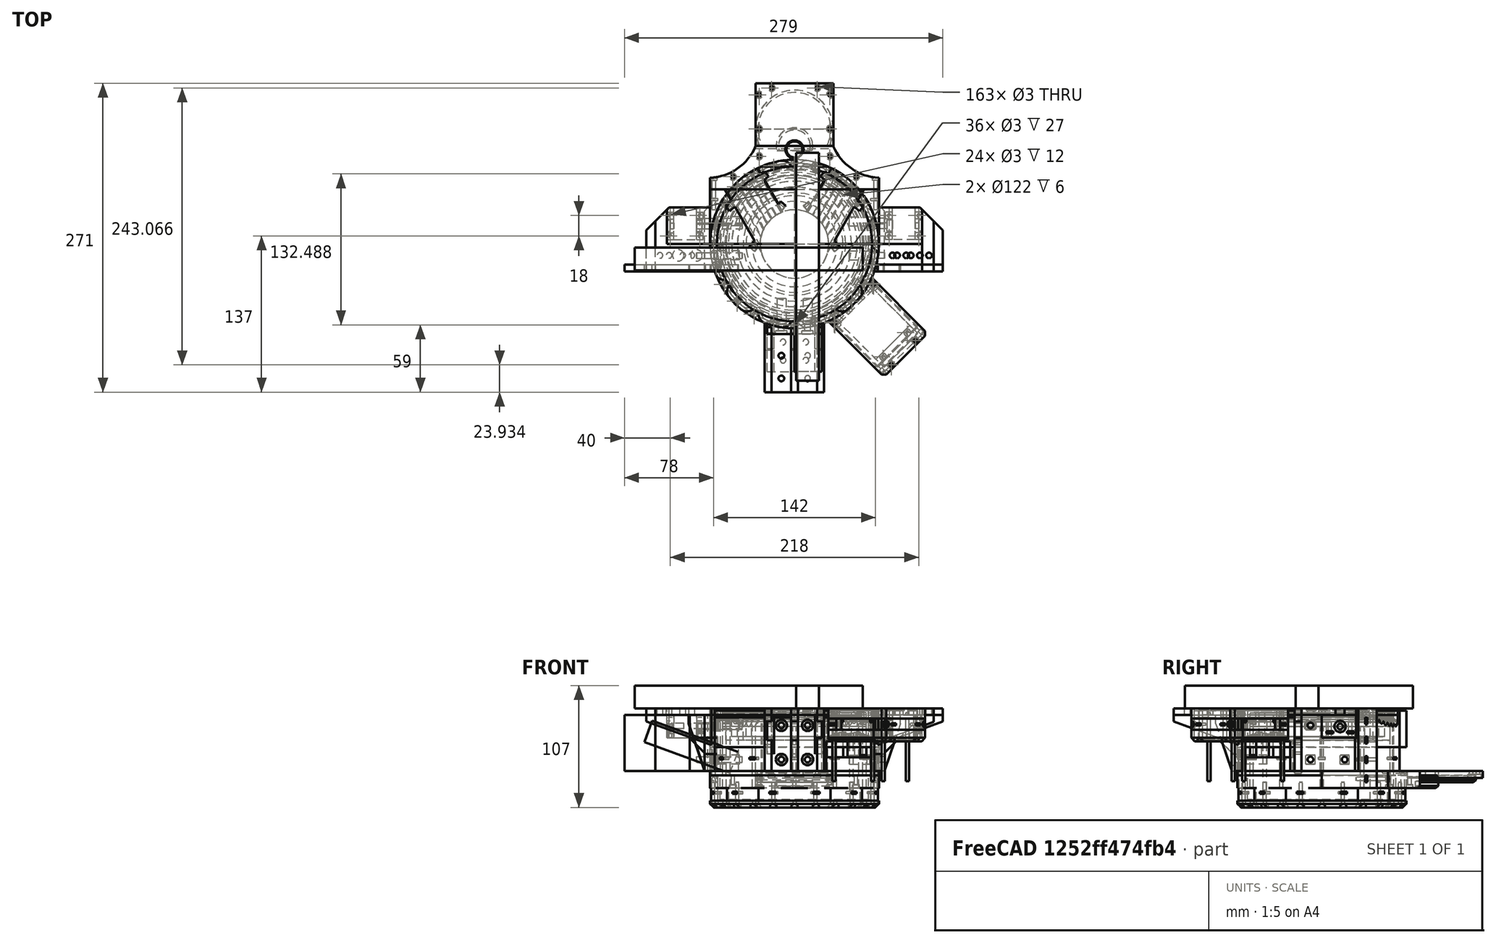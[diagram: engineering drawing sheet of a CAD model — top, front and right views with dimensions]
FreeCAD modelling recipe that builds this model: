
FCSTD DOCUMENT  (FreeCAD 0.19R24276 (Git))
Label: Base_turret_039
License: All rights reserved
LicenseURL: http://en.wikipedia.org/wiki/All_rights_reserved
objects: Part::Cylinder×614, Part::Box×522, Part::Compound×337, Part::Cut×305, Part::Mirroring×42, Part::Chamfer×39, Part::FeaturePython×20, Part::Fillet×14, Mesh::Feature×5, Part::Common×2
note: 1895 computed .brp shape members not serialized (recipe doc carries the construction recipe); baked Part::Feature solids carry a one-line shape summary decoded from their .brp

FEATURE [Part::Cylinder] Cylinder1727  label="Válec1727"
  Angle = 360
  AttacherType = Attacher::AttachEngine3D
  Height = 3
  Placement = pos=(-15,125,-80) rot=(0,0,1;0rad)
  Radius = 3
FEATURE [Part::Cylinder] Cylinder1728  label="Válec1728"
  Angle = 360
  AttacherType = Attacher::AttachEngine3D
  Height = 3
  Placement = pos=(15,125,-80) rot=(0,0,1;0rad)
  Radius = 3
FEATURE [Part::Cylinder] Cylinder1729  label="Válec1729"
  Angle = 360
  AttacherType = Attacher::AttachEngine3D
  Height = 3
  Placement = pos=(24,73,-80) rot=(0,0,1;0rad)
  Radius = 3
FEATURE [Part::Cylinder] Cylinder1730  label="Válec1730"
  Angle = 360
  AttacherType = Attacher::AttachEngine3D
  Height = 3
  Placement = pos=(-24,73,-80) rot=(0,0,1;0rad)
  Radius = 3
FEATURE [Part::Box] Box688  label="Krychle688"
  AttacherType = Attacher::AttachEngine3D
  Height = 50
  Length = 42
  Placement = pos=(-21.0011,60.0051,31) rot=(0,0,1;0rad)
  Width = 62
FEATURE [Part::Compound] Compound871
  Links = -> [Cylinder1729,Cylinder1730,Cylinder1727,Cylinder1728]
  Placement = pos=(0,0,135) rot=(0,0,1;3.92699rad)
FEATURE [Part::Compound] Compound872
  Links = -> [Box688]
  Placement = pos=(0,0,0) rot=(0,0,1;3.92699rad)
FEATURE [Part::Box] Box689  label="Krychle689"
  AttacherType = Attacher::AttachEngine3D
  Height = 10
  Length = 54
  Placement = pos=(-27.0044,59.998,75) rot=(0,0,1;0rad)
  Width = 68
FEATURE [Part::Compound] Compound873
  Links = -> [Box689]
  Placement = pos=(0,0,-20) rot=(0,0,1;3.92699rad)
FEATURE [Part::Cut] Cut502
  Base = -> Compound873
  Tool = -> Compound872
FEATURE [Part::Cylinder] Cylinder1731  label="Válec1731"
  Angle = 360
  AttacherType = Attacher::AttachEngine3D
  Height = 60
  Placement = pos=(-15,125,-80) rot=(0,0,1;0rad)
  Radius = 1.5
FEATURE [Part::Cylinder] Cylinder1732  label="Válec1732"
  Angle = 360
  AttacherType = Attacher::AttachEngine3D
  Height = 60
  Placement = pos=(15,125,-80) rot=(0,0,1;0rad)
  Radius = 1.5
FEATURE [Part::Cylinder] Cylinder1733  label="Válec1733"
  Angle = 360
  AttacherType = Attacher::AttachEngine3D
  Height = 60
  Placement = pos=(24,73,-80) rot=(0,0,1;0rad)
  Radius = 1.5
FEATURE [Part::Cylinder] Cylinder1734  label="Válec1734"
  Angle = 360
  AttacherType = Attacher::AttachEngine3D
  Height = 60
  Placement = pos=(-24,73,-80) rot=(0,0,1;0rad)
  Radius = 1.5
FEATURE [Part::Compound] Compound874
  Links = -> [Cylinder1733,Cylinder1734,Cylinder1731,Cylinder1732]
  Placement = pos=(0,0,100) rot=(0,0,1;3.92699rad)
FEATURE [Part::Cylinder] Cylinder1735  label="Válec1735"
  Angle = 360
  AttacherType = Attacher::AttachEngine3D
  Height = 40
  Placement = pos=(0,0,44) rot=(0,0,1;0rad)
  Radius = 74
FEATURE [Part::Box] Box690  label="Krychle690"
  AttacherType = Attacher::AttachEngine3D
  Height = 10
  Length = 42
  Placement = pos=(-21,-23,22) rot=(0,0,1;0rad)
  Width = 8
FEATURE [Part::Cylinder] Cylinder1736  label="Válec1736"
  Angle = 360
  AttacherType = Attacher::AttachEngine3D
  Height = 40
  Placement = pos=(0,0,44) rot=(0,0,1;0rad)
  Radius = 74
FEATURE [Part::Cylinder] Cylinder1739  label="Válec1739"
  Angle = 360
  AttacherType = Attacher::AttachEngine3D
  Height = 50
  Placement = pos=(9,100,59) rot=(1,0,0;1.5708rad)
  Radius = 1.5
FEATURE [Part::Cylinder] Cylinder1740  label="Válec1740"
  Angle = 360
  AttacherType = Attacher::AttachEngine3D
  Height = 50
  Placement = pos=(-9,100,59) rot=(1,0,0;1.5708rad)
  Radius = 1.5
FEATURE [Part::Compound] Compound876
  Links = -> [Box690]
  Placement = pos=(63.64,-63.64,43) rot=(0,0,1;3.92699rad)
FEATURE [Part::Cut] Cut506
  Base = -> Compound876
  Placement = pos=(0,0,-10) rot=(0,0,1;0rad)
  Tool = -> Cylinder1736
FEATURE [Part::Compound] Compound881
  Links = -> [Cylinder1739]
  Placement = pos=(0,0,0) rot=(0,0,1;3.92699rad)
FEATURE [Part::Compound] Compound882
  Links = -> [Cylinder1740]
  Placement = pos=(0,0,0) rot=(0,0,1;3.92699rad)
FEATURE [Part::Compound] Compound883
  Links = -> [Compound882,Compound881]
  Placement = pos=(0,0,1) rot=(0,0,1;0rad)
FEATURE [Part::Cut] Cut507
  Base = -> Cut506
  Tool = -> Compound883
FEATURE [Part::Cut] Cut510
  Base = -> Cut502
  Tool = -> Cylinder1735
FEATURE [Part::Chamfer] Chamfer054
  Base = -> Cut510
  Edges = 2 edges r=3: [Edge2,Edge13]
FEATURE [Part::Chamfer] Chamfer055
  Base = -> Chamfer054
  Edges = 2 edges r=2: [Edge3,Edge22]
FEATURE [Part::Chamfer] Chamfer056
  Base = -> Chamfer055
  Edges = 1 edges r=1: [Edge27]
FEATURE [Part::Cut] Cut511
  Base = -> Chamfer056
  Tool = -> Compound874
FEATURE [Part::Cut] Cut512
  Base = -> Cut511
  Tool = -> Compound871
FEATURE [Part::Box] Box485  label="Krychle485"
  AttacherType = Attacher::AttachEngine3D
  Height = 49
  Length = 56
  Placement = pos=(-28,35,29) rot=(0,0,1;0rad)
  Width = 200
FEATURE [Part::Box] Box486  label="Krychle486"
  AttacherType = Attacher::AttachEngine3D
  Height = 55
  Length = 148
  Placement = pos=(-74,68,29) rot=(0,0,1;0rad)
  Width = 26
FEATURE [Part::Cylinder] Cylinder971  label="Válec971"
  Angle = 360
  AttacherType = Attacher::AttachEngine3D
  Height = 6
  Placement = pos=(0,0,65) rot=(0,0,1;0rad)
  Radius = 74
FEATURE [Part::Box] Box483  label="Krychle483"
  AttacherType = Attacher::AttachEngine3D
  Height = 34
  Length = 148
  Placement = pos=(-74,68,38) rot=(0,0,1;0rad)
  Width = 20
FEATURE [Part::Cut] Cut453
  Base = -> Cylinder971
  Placement = pos=(0,0,13) rot=(0,0,1;0rad)
  Tool = -> Box483
FEATURE [Part::Box] Box648  label="Krychle648"
  AttacherType = Attacher::AttachEngine3D
  Height = 60
  Length = 200
  Placement = pos=(0,0,-5) rot=(0,0,-1;0.383972rad)
  Width = 200
FEATURE [Part::Box] Box647  label="Krychle647"
  AttacherType = Attacher::AttachEngine3D
  Height = 60
  Length = 200
  Placement = pos=(70.7107,70.7107,-5) rot=(0,0,1;3.92699rad)
  Width = 120
FEATURE [Part::Cut] Cut464
  Base = -> Box647
  Tool = -> Box648
FEATURE [Part::Box] Box649  label="Krychle649"
  AttacherType = Attacher::AttachEngine3D
  Height = 60
  Length = 200
  Placement = pos=(0,0,-5) rot=(0,0,1;3.52556rad)
  Width = 200
FEATURE [Part::Cut] Cut465
  Base = -> Cut464
  Tool = -> Box649
FEATURE [Part::FeaturePython] Tube035  # WARN: FeaturePython — macro-defined, semantics opaque (R4)
  AttacherType = Attacher::AttachEngine3D
  Height = 55
  InnerRadius = 68
  OuterRadius = 74
  Placement = pos=(0,0,29) rot=(0,0,1;0rad)
FEATURE [Part::Cut] Cut455
  Base = -> Tube035
  Tool = -> Box485
FEATURE [Part::Cut] Cut454
  Base = -> Cut455
  Tool = -> Box486
FEATURE [Part::Cut] Cut
  Base = -> Cut454
  Tool = -> Cut465
FEATURE [Part::FeaturePython] Tube036  # WARN: FeaturePython — macro-defined, semantics opaque (R4)
  AttacherType = Attacher::AttachEngine3D
  Height = 8
  InnerRadius = 50.1
  OuterRadius = 58
  Placement = pos=(0,0,72) rot=(0,0,1;0rad)
FEATURE [Part::Box] Box488  label="Krychle488"
  AttacherType = Attacher::AttachEngine3D
  Height = 2
  Length = 6
  Placement = pos=(-3,-75,39) rot=(0,0,1;0rad)
  Width = 8
FEATURE [Part::Box] Box489  label="Krychle489"
  AttacherType = Attacher::AttachEngine3D
  Height = 2
  Length = 6
  Placement = pos=(34.9,-66.45,58) rot=(0,0,1;0.523599rad)
  Width = 8
FEATURE [Part::Box] Box497  label="Krychle497"
  AttacherType = Attacher::AttachEngine3D
  Height = 2
  Length = 6
  Placement = pos=(-75,3,39) rot=(0,0,-1;1.5708rad)
  Width = 8
FEATURE [Part::Box] Box493  label="Krychle493"
  AttacherType = Attacher::AttachEngine3D
  Height = 2
  Length = 6
  Placement = pos=(40.0981,63.4519,39) rot=(0,0,1;2.61799rad)
  Width = 8
FEATURE [Part::Box] Box491  label="Krychle491"
  AttacherType = Attacher::AttachEngine3D
  Height = 2
  Length = 6
  Placement = pos=(75,-3,39) rot=(0,0,1;1.5708rad)
  Width = 8
FEATURE [Part::Box] Box495  label="Krychle495"
  AttacherType = Attacher::AttachEngine3D
  Height = 2
  Length = 6
  Placement = pos=(-34.9019,66.4519,39) rot=(0,0,1;3.66519rad)
  Width = 8
FEATURE [Part::Box] Box490  label="Krychle490"
  AttacherType = Attacher::AttachEngine3D
  Height = 2
  Length = 6
  Placement = pos=(63.45,-40.1,58) rot=(0,0,1;1.0472rad)
  Width = 8
FEATURE [Part::Box] Box494  label="Krychle494"
  AttacherType = Attacher::AttachEngine3D
  Height = 2
  Length = 6
  Placement = pos=(3,75,39) rot=(0,0,1;3.14159rad)
  Width = 8
FEATURE [Part::Box] Box498  label="Krychle498"
  AttacherType = Attacher::AttachEngine3D
  Height = 2
  Length = 6
  Placement = pos=(-66.4519,-34.9019,39) rot=(0,0,-1;1.0472rad)
  Width = 8
FEATURE [Part::Box] Box492  label="Krychle492"
  AttacherType = Attacher::AttachEngine3D
  Height = 2
  Length = 6
  Placement = pos=(66.4519,34.9019,39) rot=(0,0,1;2.0944rad)
  Width = 8
FEATURE [Part::Box] Box499  label="Krychle499"
  AttacherType = Attacher::AttachEngine3D
  Height = 2
  Length = 6
  Placement = pos=(-40.0981,-63.4519,39) rot=(0,0,-1;0.523599rad)
  Width = 8
FEATURE [Part::Box] Box496  label="Krychle496"
  AttacherType = Attacher::AttachEngine3D
  Height = 2
  Length = 6
  Placement = pos=(-63.4519,40.0981,39) rot=(0,0,1;4.18879rad)
  Width = 8
FEATURE [Part::Compound] Compound528
  Links = -> [Box488,Box489,Box490,Box491,Box492,Box493,Box494,Box495,Box496,Box497,Box498,Box499]
FEATURE [Part::Cut] Cut467
  Base = -> Cut
  Tool = -> Compound528
FEATURE [Part::Cylinder] Cylinder1629  label="Válec1629"
  Angle = 360
  AttacherType = Attacher::AttachEngine3D
  Height = 72
  Placement = pos=(71,-1.8e-14,0) rot=(0,0,1;1.5708rad)
  Radius = 1.5
FEATURE [Part::Cylinder] Cylinder1630  label="Válec1630"
  Angle = 360
  AttacherType = Attacher::AttachEngine3D
  Height = 72
  Placement = pos=(35.5,61.4878,0) rot=(0,0,1;2.61799rad)
  Radius = 1.5
FEATURE [Part::Cylinder] Cylinder1631  label="Válec1631"
  Angle = 360
  AttacherType = Attacher::AttachEngine3D
  Height = 72
  Placement = pos=(61.4878,-35.5,0) rot=(0,0,1;1.0472rad)
  Radius = 1.5
FEATURE [Part::Cylinder] Cylinder1632  label="Válec1632"
  Angle = 360
  AttacherType = Attacher::AttachEngine3D
  Height = 72
  Placement = pos=(35.5,-61.4878,0) rot=(0,0,1;0.523599rad)
  Radius = 1.5
FEATURE [Part::Cylinder] Cylinder1633  label="Válec1633"
  Angle = 360
  AttacherType = Attacher::AttachEngine3D
  Height = 72
  Placement = pos=(-35.5,-61.4878,0) rot=(0,0,-1;0.523599rad)
  Radius = 1.5
FEATURE [Part::Cylinder] Cylinder1634  label="Válec1634"
  Angle = 360
  AttacherType = Attacher::AttachEngine3D
  Height = 72
  Placement = pos=(-71,2.7e-14,0) rot=(0,0,-1;1.5708rad)
  Radius = 1.5
FEATURE [Part::Cylinder] Cylinder1635  label="Válec1635"
  Angle = 360
  AttacherType = Attacher::AttachEngine3D
  Height = 72
  Placement = pos=(-61.4878,-35.5,0) rot=(0,0,-1;1.0472rad)
  Radius = 1.5
FEATURE [Part::Cylinder] Cylinder1636  label="Válec1636"
  Angle = 360
  AttacherType = Attacher::AttachEngine3D
  Height = 72
  Placement = pos=(61.4878,35.5,0) rot=(0,0,1;2.0944rad)
  Radius = 1.5
FEATURE [Part::Cylinder] Cylinder1637  label="Válec1637"
  Angle = 360
  AttacherType = Attacher::AttachEngine3D
  Height = 72
  Placement = pos=(0,-71,0) rot=(0,0,1;0rad)
  Radius = 1.5
FEATURE [Part::Cylinder] Cylinder1638  label="Válec1638"
  Angle = 360
  AttacherType = Attacher::AttachEngine3D
  Height = 72
  Placement = pos=(-35.5,61.4878,0) rot=(0,0,1;3.66519rad)
  Radius = 1.5
FEATURE [Part::Cylinder] Cylinder1639  label="Válec1639"
  Angle = 360
  AttacherType = Attacher::AttachEngine3D
  Height = 72
  Placement = pos=(-61.4878,35.5,0) rot=(0,0,1;4.18879rad)
  Radius = 1.5
FEATURE [Part::Cylinder] Cylinder1640  label="Válec1640"
  Angle = 360
  AttacherType = Attacher::AttachEngine3D
  Height = 72
  Placement = pos=(3.1e-14,71,0) rot=(0,0,1;3.14159rad)
  Radius = 1.5
FEATURE [Part::Compound] Compound529
  Links = -> [Cylinder1637,Cylinder1632,Cylinder1631,Cylinder1629,Cylinder1636,Cylinder1630,Cylinder1640,Cylinder1638,Cylinder1639,Cylinder1634,Cylinder1635,Cylinder1633]
  Placement = pos=(0,0,-4) rot=(0,0,1;0rad)
FEATURE [Part::Cut] Cut468
  Base = -> Cut467
  Tool = -> Compound529
FEATURE [Part::Cylinder] Cylinder1722  label="Válec1722"
  Angle = 360
  AttacherType = Attacher::AttachEngine3D
  Height = 50
  Placement = pos=(-18,100,72) rot=(1,0,0;1.5708rad)
  Radius = 1.5
FEATURE [Part::Compound] Compound863
  Links = -> [Cylinder1722]
  Placement = pos=(0,0,0) rot=(0,0,1;3.92699rad)
FEATURE [Part::Cylinder] Cylinder1723  label="Válec1723"
  Angle = 360
  AttacherType = Attacher::AttachEngine3D
  Height = 50
  Placement = pos=(18,100,72) rot=(1,0,0;1.5708rad)
  Radius = 1.5
FEATURE [Part::Compound] Compound864
  Links = -> [Cylinder1723]
  Placement = pos=(0,0,0) rot=(0,0,1;3.92699rad)
FEATURE [Part::Compound] Compound865
  Links = -> [Compound863,Compound864]
  Placement = pos=(0,0,1) rot=(0,0,1;0rad)
FEATURE [Part::Box] Box686  label="Krychle686"
  AttacherType = Attacher::AttachEngine3D
  Height = 6
  Length = 6
  Placement = pos=(15,64,-50) rot=(0,0,1;0rad)
  Width = 4
FEATURE [Part::Box] Box687  label="Krychle687"
  AttacherType = Attacher::AttachEngine3D
  Height = 6
  Length = 6
  Placement = pos=(-21,64,-50) rot=(0,0,1;0rad)
  Width = 4
FEATURE [Part::Cut] Cut500
  Base = -> Cut468
  Tool = -> Compound865
FEATURE [Part::Compound] Compound866
  Links = -> [Box687,Box686]
  Placement = pos=(0,0,120) rot=(0,0,1;3.92699rad)
FEATURE [Part::Cut] Cut501
  Base = -> Cut500
  Tool = -> Compound866
FEATURE [Part::Cylinder] Cylinder1737  label="Válec1737"
  Angle = 360
  AttacherType = Attacher::AttachEngine3D
  Height = 50
  Placement = pos=(-9,100,59) rot=(1,0,0;1.5708rad)
  Radius = 1.5
FEATURE [Part::Cylinder] Cylinder1738  label="Válec1738"
  Angle = 360
  AttacherType = Attacher::AttachEngine3D
  Height = 50
  Placement = pos=(9,100,59) rot=(1,0,0;1.5708rad)
  Radius = 1.5
FEATURE [Part::Box] Box691  label="Krychle691"
  AttacherType = Attacher::AttachEngine3D
  Height = 6
  Length = 6
  Placement = pos=(6,66,-63) rot=(0,0,1;0rad)
  Width = 4
FEATURE [Part::Box] Box692  label="Krychle692"
  AttacherType = Attacher::AttachEngine3D
  Height = 6
  Length = 6
  Placement = pos=(-12,66,-63) rot=(0,0,1;0rad)
  Width = 4
FEATURE [Part::Compound] Compound878
  Links = -> [Cylinder1738]
  Placement = pos=(0,0,0) rot=(0,0,1;3.92699rad)
FEATURE [Part::Compound] Compound879
  Links = -> [Cylinder1737]
  Placement = pos=(0,0,0) rot=(0,0,1;3.92699rad)
FEATURE [Part::Compound] Compound877
  Links = -> [Compound879,Compound878]
  Placement = pos=(0,0,1) rot=(0,0,1;0rad)
FEATURE [Part::Cut] Cut508
  Base = -> Cut501
  Tool = -> Compound877
FEATURE [Part::Compound] Compound880
  Links = -> [Box692,Box691]
  Placement = pos=(0,0,120) rot=(0,0,1;3.92699rad)
FEATURE [Part::Cut] Cut509
  Base = -> Cut508
  Tool = -> Compound880
FEATURE [Part::Box] Box482  label="Krychle482"
  AttacherType = Attacher::AttachEngine3D
  Height = 55
  Length = 148
  Placement = pos=(-74,0,29) rot=(0,0,1;0rad)
  Width = 74
FEATURE [Part::Cylinder] Cylinder972  label="Válec972"
  Angle = 360
  AttacherType = Attacher::AttachEngine3D
  Height = 51
  Placement = pos=(0,0,29) rot=(0,0,1;0rad)
  Radius = 74
FEATURE [Part::Cut] Cut451
  Base = -> Box482
  Tool = -> Cylinder972
FEATURE [Part::Box] Box484  label="Krychle484"
  AttacherType = Attacher::AttachEngine3D
  Height = 55
  Length = 148
  Placement = pos=(-74,48,29) rot=(0,0,1;0rad)
  Width = 26
FEATURE [Part::Cut] Cut452
  Base = -> Cut451
  Tool = -> Box484
FEATURE [Part::Cylinder] Cylinder1753  label="Válec1753"
  Angle = 360
  AttacherType = Attacher::AttachEngine3D
  Height = 50
  Placement = pos=(-71,80,73) rot=(1,0,0;1.5708rad)
  Radius = 1.5
FEATURE [Part::Cylinder] Cylinder1754  label="Válec1754"
  Angle = 360
  AttacherType = Attacher::AttachEngine3D
  Height = 50
  Placement = pos=(71,80,39) rot=(1,0,0;1.5708rad)
  Radius = 1.5
FEATURE [Part::Cylinder] Cylinder1755  label="Válec1755"
  Angle = 360
  AttacherType = Attacher::AttachEngine3D
  Height = 50
  Placement = pos=(-71,80,39) rot=(1,0,0;1.5708rad)
  Radius = 1.5
FEATURE [Part::Cylinder] Cylinder1756  label="Válec1756"
  Angle = 360
  AttacherType = Attacher::AttachEngine3D
  Height = 50
  Placement = pos=(71,80,73) rot=(1,0,0;1.5708rad)
  Radius = 1.5
FEATURE [Part::Cylinder] Cylinder1757  label="Válec1757"
  Angle = 360
  AttacherType = Attacher::AttachEngine3D
  Height = 50
  Placement = pos=(-71,80,56) rot=(1,0,0;1.5708rad)
  Radius = 1.5
FEATURE [Part::Cylinder] Cylinder1758  label="Válec1758"
  Angle = 360
  AttacherType = Attacher::AttachEngine3D
  Height = 50
  Placement = pos=(71,80,56) rot=(1,0,0;1.5708rad)
  Radius = 1.5
FEATURE [Part::Compound] Compound887
  Links = -> [Cylinder1753,Cylinder1754,Cylinder1755,Cylinder1756,Cylinder1757,Cylinder1758]
FEATURE [Part::Cut] Cut518
  Base = -> Cut452
  Tool = -> Compound887
FEATURE [Part::Box] Box512  label="Krychle512"
  AttacherType = Attacher::AttachEngine3D
  Height = 6
  Length = 8
  Placement = pos=(-75,38,36) rot=(0,0,1;0rad)
  Width = 2
FEATURE [Part::Box] Box513  label="Krychle513"
  AttacherType = Attacher::AttachEngine3D
  Height = 6
  Length = 8
  Placement = pos=(67,38,36) rot=(0,0,1;0rad)
  Width = 2
FEATURE [Part::Box] Box514  label="Krychle514"
  AttacherType = Attacher::AttachEngine3D
  Height = 6
  Length = 8
  Placement = pos=(67,38,70) rot=(0,0,1;0rad)
  Width = 2
FEATURE [Part::Box] Box515  label="Krychle515"
  AttacherType = Attacher::AttachEngine3D
  Height = 6
  Length = 8
  Placement = pos=(-75,38,70) rot=(0,0,1;0rad)
  Width = 2
FEATURE [Part::Box] Box516  label="Krychle516"
  AttacherType = Attacher::AttachEngine3D
  Height = 6
  Length = 8
  Placement = pos=(-75,38,53) rot=(0,0,1;0rad)
  Width = 2
FEATURE [Part::Box] Box517  label="Krychle517"
  AttacherType = Attacher::AttachEngine3D
  Height = 6
  Length = 8
  Placement = pos=(67,38,53) rot=(0,0,1;0rad)
  Width = 2
FEATURE [Part::Compound] Compound530
  Links = -> [Box512,Box513,Box514,Box515,Box516,Box517]
FEATURE [Part::Cut] Cut519
  Base = -> Cut518
  Tool = -> Compound530
FEATURE [Part::Box] Box699  label="Krychle699"
  AttacherType = Attacher::AttachEngine3D
  Height = 2
  Length = 6
  Placement = pos=(-3,-75,39) rot=(0,0,1;0rad)
  Width = 8
FEATURE [Part::Box] Box700  label="Krychle700"
  AttacherType = Attacher::AttachEngine3D
  Height = 2
  Length = 6
  Placement = pos=(34.9019,-66.4519,39) rot=(0,0,1;0.523599rad)
  Width = 8
FEATURE [Part::Box] Box701  label="Krychle701"
  AttacherType = Attacher::AttachEngine3D
  Height = 2
  Length = 6
  Placement = pos=(63.4519,-40.0981,39) rot=(0,0,1;1.0472rad)
  Width = 8
FEATURE [Part::Box] Box702  label="Krychle702"
  AttacherType = Attacher::AttachEngine3D
  Height = 2
  Length = 6
  Placement = pos=(75,-3,39) rot=(0,0,1;1.5708rad)
  Width = 8
FEATURE [Part::Box] Box703  label="Krychle703"
  AttacherType = Attacher::AttachEngine3D
  Height = 2
  Length = 6
  Placement = pos=(66.4519,34.9019,39) rot=(0,0,1;2.0944rad)
  Width = 8
FEATURE [Part::Box] Box704  label="Krychle704"
  AttacherType = Attacher::AttachEngine3D
  Height = 2
  Length = 6
  Placement = pos=(40.0981,63.4519,39) rot=(0,0,1;2.61799rad)
  Width = 8
FEATURE [Part::Box] Box705  label="Krychle705"
  AttacherType = Attacher::AttachEngine3D
  Height = 2
  Length = 6
  Placement = pos=(3,75,39) rot=(0,0,1;3.14159rad)
  Width = 8
FEATURE [Part::Box] Box706  label="Krychle706"
  AttacherType = Attacher::AttachEngine3D
  Height = 2
  Length = 6
  Placement = pos=(-34.9019,66.4519,39) rot=(0,0,1;3.66519rad)
  Width = 8
FEATURE [Part::Box] Box707  label="Krychle707"
  AttacherType = Attacher::AttachEngine3D
  Height = 2
  Length = 6
  Placement = pos=(-63.4519,40.0981,39) rot=(0,0,1;4.18879rad)
  Width = 8
FEATURE [Part::Box] Box708  label="Krychle708"
  AttacherType = Attacher::AttachEngine3D
  Height = 2
  Length = 6
  Placement = pos=(-75,3,39) rot=(0,0,-1;1.5708rad)
  Width = 8
FEATURE [Part::Box] Box709  label="Krychle709"
  AttacherType = Attacher::AttachEngine3D
  Height = 2
  Length = 6
  Placement = pos=(-66.4519,-34.9019,39) rot=(0,0,-1;1.0472rad)
  Width = 8
FEATURE [Part::Box] Box710  label="Krychle710"
  AttacherType = Attacher::AttachEngine3D
  Height = 2
  Length = 6
  Placement = pos=(-40.0981,-63.4519,39) rot=(0,0,-1;0.523599rad)
  Width = 8
FEATURE [Part::Compound] Compound888
  Links = -> [Box699,Box700,Box701,Box702,Box703,Box704,Box705,Box706,Box707,Box708,Box709,Box710]
FEATURE [Part::Box] Box425  label="Krychle425"
  AttacherType = Attacher::AttachEngine3D
  Height = 2
  Length = 6
  Placement = pos=(-112,4,60) rot=(0,0,1;0rad)
  Width = 6
FEATURE [Part::Box] Box426  label="Krychle426"
  AttacherType = Attacher::AttachEngine3D
  Height = 20
  Length = 20
  Placement = pos=(-106,4,56) rot=(0,0,1;0rad)
  Width = 80
FEATURE [Part::Box] Box427  label="Krychle427"
  AttacherType = Attacher::AttachEngine3D
  Height = 2
  Length = 6
  Placement = pos=(-112,22,60) rot=(0,0,1;0rad)
  Width = 6
FEATURE [Part::Box] Box428  label="Krychle428"
  AttacherType = Attacher::AttachEngine3D
  Height = 2
  Length = 6
  Placement = pos=(-86,22,60) rot=(0,0,1;0rad)
  Width = 6
FEATURE [Part::Cylinder] Cylinder899  label="Válec899"
  Angle = 360
  AttacherType = Attacher::AttachEngine3D
  Height = 20
  Placement = pos=(-83,25,54) rot=(0,0,1;0rad)
  Radius = 1.5
FEATURE [Part::Cut] Cut520
  Base = -> Cut519
  Tool = -> Compound888
FEATURE [Part::Box] Box429  label="Krychle429"
  AttacherType = Attacher::AttachEngine3D
  Height = 2
  Length = 6
  Placement = pos=(-86,4,60) rot=(0,0,1;0rad)
  Width = 6
FEATURE [Part::Compound] Compound495
  Links = -> [Box425,Box427,Box429,Box428]
FEATURE [Part::Cylinder] Cylinder900  label="Válec900"
  Angle = 360
  AttacherType = Attacher::AttachEngine3D
  Height = 20
  Placement = pos=(-83,7,54) rot=(0,0,1;0rad)
  Radius = 1.5
FEATURE [Part::Cylinder] Cylinder901  label="Válec901"
  Angle = 360
  AttacherType = Attacher::AttachEngine3D
  Height = 20
  Placement = pos=(-109,7,54) rot=(0,0,1;0rad)
  Radius = 1.5
FEATURE [Part::Cylinder] Cylinder902  label="Válec902"
  Angle = 360
  AttacherType = Attacher::AttachEngine3D
  Height = 20
  Placement = pos=(-109,25,54) rot=(0,0,1;0rad)
  Radius = 1.5
FEATURE [Part::Compound] Compound496
  Links = -> [Cylinder900,Cylinder899,Cylinder901,Cylinder902]
FEATURE [Part::Box] Box430  label="Krychle430"
  AttacherType = Attacher::AttachEngine3D
  Height = 26
  Length = 38
  Placement = pos=(-112,0,56) rot=(0,0,1;0rad)
  Width = 32
FEATURE [Part::Cylinder] Cylinder903  label="Válec903"
  Angle = 360
  AttacherType = Attacher::AttachEngine3D
  Height = 3
  Placement = pos=(-112,16,66) rot=(0,1,0;1.5708rad)
  Radius = 5
FEATURE [Part::Cylinder] Cylinder904  label="Válec904"
  Angle = 360
  AttacherType = Attacher::AttachEngine3D
  Height = 20
  Placement = pos=(-117,16,66) rot=(0,1,0;1.5708rad)
  Radius = 2.5
FEATURE [Part::Box] Box431  label="Krychle431"
  AttacherType = Attacher::AttachEngine3D
  Height = 6
  Length = 62
  Placement = pos=(-122,-24,76) rot=(0,0,1;0rad)
  Width = 56
FEATURE [Part::Cylinder] Cylinder905  label="Válec905"
  Angle = 360
  AttacherType = Attacher::AttachEngine3D
  Height = 32
  Placement = pos=(0,0,66) rot=(0,0,1;0rad)
  Radius = 74
FEATURE [Part::Cylinder] Cylinder906  label="Válec906"
  Angle = 360
  AttacherType = Attacher::AttachEngine3D
  Height = 32
  Placement = pos=(0,0,50) rot=(0,0,1;0rad)
  Radius = 74
FEATURE [Part::Box] Box432  label="Krychle432"
  AttacherType = Attacher::AttachEngine3D
  Height = 49
  Length = 57
  Placement = pos=(-122,-24,29) rot=(0,0,1;0rad)
  Width = 6
FEATURE [Part::Cut] Cut406
  Base = -> Box432
  Tool = -> Cylinder906
FEATURE [Part::Cylinder] Cylinder907  label="Válec907"
  Angle = 360
  AttacherType = Attacher::AttachEngine3D
  Height = 20
  Placement = pos=(-90,-10,66) rot=(0,0,1;0rad)
  Radius = 2.5
FEATURE [Part::Cylinder] Cylinder908  label="Válec908"
  Angle = 360
  AttacherType = Attacher::AttachEngine3D
  Height = 20
  Placement = pos=(-110,-10,66) rot=(0,0,1;0rad)
  Radius = 2.5
FEATURE [Part::Compound] Compound498
  Links = -> [Cylinder908,Cylinder907]
FEATURE [Part::Box] Box521  label="Krychle521"
  AttacherType = Attacher::AttachEngine3D
  Height = 14
  Length = 24
  Placement = pos=(-92,-24,44) rot=(0,0,1;0rad)
  Width = 6
FEATURE [Part::Chamfer] Chamfer016
  Base = -> Box521
  Edges = 1 edges r=13.99: [Edge4]
FEATURE [Part::Box] Box416  label="Krychle416"
  AttacherType = Attacher::AttachEngine3D
  Height = 26
  Length = 38
  Placement = pos=(-112,0,56) rot=(0,0,1;0rad)
  Width = 32
FEATURE [Part::Box] Box417  label="Krychle417"
  AttacherType = Attacher::AttachEngine3D
  Height = 20
  Length = 20
  Placement = pos=(-106,4,56) rot=(0,0,1;0rad)
  Width = 80
FEATURE [Part::Box] Box418  label="Krychle418"
  AttacherType = Attacher::AttachEngine3D
  Height = 2
  Length = 6
  Placement = pos=(-112,4,60) rot=(0,0,1;0rad)
  Width = 6
FEATURE [Part::Box] Box419  label="Krychle419"
  AttacherType = Attacher::AttachEngine3D
  Height = 2
  Length = 6
  Placement = pos=(-112,22,60) rot=(0,0,1;0rad)
  Width = 6
FEATURE [Part::Box] Box420  label="Krychle420"
  AttacherType = Attacher::AttachEngine3D
  Height = 2
  Length = 6
  Placement = pos=(-86,4,60) rot=(0,0,1;0rad)
  Width = 6
FEATURE [Part::Box] Box421  label="Krychle421"
  AttacherType = Attacher::AttachEngine3D
  Height = 2
  Length = 6
  Placement = pos=(-86,22,60) rot=(0,0,1;0rad)
  Width = 6
FEATURE [Part::Cylinder] Cylinder1759  label="Válec1759"
  Angle = 360
  AttacherType = Attacher::AttachEngine3D
  Height = 20
  Placement = pos=(-83,7,54) rot=(0,0,1;0rad)
  Radius = 1.5
FEATURE [Part::Cylinder] Cylinder875  label="Válec875"
  Angle = 360
  AttacherType = Attacher::AttachEngine3D
  Height = 20
  Placement = pos=(-83,25,54) rot=(0,0,1;0rad)
  Radius = 1.5
FEATURE [Part::Cylinder] Cylinder876  label="Válec876"
  Angle = 360
  AttacherType = Attacher::AttachEngine3D
  Height = 20
  Placement = pos=(-109,7,54) rot=(0,0,1;0rad)
  Radius = 1.5
FEATURE [Part::Cylinder] Cylinder877  label="Válec877"
  Angle = 360
  AttacherType = Attacher::AttachEngine3D
  Height = 20
  Placement = pos=(-109,25,54) rot=(0,0,1;0rad)
  Radius = 1.5
FEATURE [Part::Cylinder] Cylinder892  label="Válec892"
  Angle = 360
  AttacherType = Attacher::AttachEngine3D
  Height = 20
  Placement = pos=(-117,16,66) rot=(0,1,0;1.5708rad)
  Radius = 2.5
FEATURE [Part::Cylinder] Cylinder893  label="Válec893"
  Angle = 360
  AttacherType = Attacher::AttachEngine3D
  Height = 3
  Placement = pos=(-112,16,66) rot=(0,1,0;1.5708rad)
  Radius = 5
FEATURE [Part::Box] Box423  label="Krychle423"
  AttacherType = Attacher::AttachEngine3D
  Height = 6
  Length = 51
  Placement = pos=(-112,-24,76) rot=(0,0,1;0rad)
  Width = 24
FEATURE [Part::Cylinder] Cylinder894  label="Válec894"
  Angle = 360
  AttacherType = Attacher::AttachEngine3D
  Height = 10
  Placement = pos=(0,0,72) rot=(0,0,1;0rad)
  Radius = 74
FEATURE [Part::Box] Box424  label="Krychle424"
  AttacherType = Attacher::AttachEngine3D
  Height = 26
  Length = 50
  Placement = pos=(-112,-24,56) rot=(0,0,1;0rad)
  Width = 6
FEATURE [Part::Cylinder] Cylinder895  label="Válec895"
  Angle = 360
  AttacherType = Attacher::AttachEngine3D
  Height = 20
  Placement = pos=(-102,-10,66) rot=(0,0,1;0rad)
  Radius = 2.5
FEATURE [Part::Cylinder] Cylinder897  label="Válec897"
  Angle = 360
  AttacherType = Attacher::AttachEngine3D
  Height = 32
  Placement = pos=(0,0,50) rot=(0,0,1;0rad)
  Radius = 74
FEATURE [Part::Cylinder] Cylinder898  label="Válec898"
  Angle = 360
  AttacherType = Attacher::AttachEngine3D
  Height = 20
  Placement = pos=(-86,-10,66) rot=(0,0,1;0rad)
  Radius = 2.5
FEATURE [Part::Box] Box522  label="Krychle522"
  AttacherType = Attacher::AttachEngine3D
  Height = 14
  Length = 24
  Placement = pos=(68,-24,44) rot=(0,0,1;0rad)
  Width = 6
FEATURE [Part::Cut] Cut408
  Base = -> Box431
  Tool = -> Cylinder905
FEATURE [Part::Cut] Cut407
  Base = -> Cut408
  Placement = pos=(0,0,2) rot=(0,0,1;0rad)
  Tool = -> Compound498
FEATURE [Part::Cut] Cut409
  Base = -> Box430
  Tool = -> Box426
FEATURE [Part::Cut] Cut410
  Base = -> Cut409
  Tool = -> Compound495
FEATURE [Part::Cut] Cut403
  Base = -> Cut410
  Tool = -> Compound496
FEATURE [Part::Cut] Cut404
  Base = -> Cut403
  Tool = -> Cylinder904
FEATURE [Part::Cut] Cut405
  Base = -> Cut404
  Tool = -> Cylinder903
FEATURE [Part::Chamfer] Chamfer004
  Base = -> Cut405
  Edges = 1 edges r=2: [Edge4]
  Placement = pos=(0,0,2) rot=(0,0,1;0rad)
FEATURE [Part::Cut] Cut521
  Base = -> Box416
  Tool = -> Box417
FEATURE [Part::Compound] Compound488
  Links = -> [Box418,Box419,Box420,Box421]
FEATURE [Part::Compound] Compound489
  Links = -> [Cylinder1759,Cylinder875,Cylinder876,Cylinder877]
FEATURE [Part::Compound] Compound493
  Links = -> [Cylinder895,Cylinder898]
FEATURE [Part::Cut] Cut392
  Base = -> Cut521
  Tool = -> Compound488
FEATURE [Part::Cut] Cut393
  Base = -> Cut392
  Tool = -> Compound489
FEATURE [Part::Cut] Cut398
  Base = -> Cut393
  Tool = -> Cylinder892
FEATURE [Part::Cut] Cut399
  Base = -> Cut398
  Tool = -> Cylinder893
FEATURE [Part::Chamfer] Chamfer002
  Base = -> Cut399
  Edges = 1 edges r=2: [Edge4]
FEATURE [Part::Cut] Cut400
  Base = -> Box423
  Tool = -> Cylinder894
FEATURE [Part::Cut] Cut401
  Base = -> Box424
  Tool = -> Cylinder897
FEATURE [Part::Cut] Cut402
  Base = -> Cut400
  Tool = -> Compound493
FEATURE [Part::Chamfer] Chamfer057
  Base = -> Cut401
  Edges = 1 edges r=20: [Edge4]
FEATURE [Part::Compound] Compound494  label="stabilo_holdo_left1"
  Links = -> [Chamfer057,Cut402,Chamfer002]
FEATURE [Part::Mirroring] mirror  label="stabilo_holdo_right"
  Base = (0,0,0)
  Normal = (1,0,0)
  Placement = pos=(0,0,2) rot=(0,0,1;0rad)
  Source = -> Compound494
FEATURE [Part::Chamfer] Chamfer017
  Base = -> Box522
  Edges = 1 edges r=13.99: [Edge8]
FEATURE [Part::Compound] Compound532  label="stabilo_holdo_right_silo"
  Links = -> [Chamfer017,mirror]
FEATURE [Part::Cylinder] Cylinder961  label="Válec961"
  Angle = 360
  AttacherType = Attacher::AttachEngine3D
  Height = 20
  Placement = pos=(-102,-10,66) rot=(0,0,1;0rad)
  Radius = 2.5
FEATURE [Part::Cylinder] Cylinder962  label="Válec962"
  Angle = 360
  AttacherType = Attacher::AttachEngine3D
  Height = 10
  Placement = pos=(0,0,72) rot=(0,0,1;0rad)
  Radius = 74
FEATURE [Part::Box] Box476  label="Krychle476"
  AttacherType = Attacher::AttachEngine3D
  Height = 26
  Length = 50
  Placement = pos=(-112,-24,56) rot=(0,0,1;0rad)
  Width = 6
FEATURE [Part::Cylinder] Cylinder963  label="Válec963"
  Angle = 360
  AttacherType = Attacher::AttachEngine3D
  Height = 20
  Placement = pos=(-86,-10,66) rot=(0,0,1;0rad)
  Radius = 2.5
FEATURE [Part::Compound] Compound519
  Links = -> [Cylinder961,Cylinder963]
FEATURE [Part::Cylinder] Cylinder964  label="Válec964"
  Angle = 360
  AttacherType = Attacher::AttachEngine3D
  Height = 32
  Placement = pos=(0,0,50) rot=(0,0,1;0rad)
  Radius = 74
FEATURE [Part::Cut] Cut443
  Base = -> Box476
  Placement = pos=(0,0,0) rot=(0,0,1;1.5708rad)
  Tool = -> Cylinder964
FEATURE [Part::Box] Box477  label="Krychle477"
  AttacherType = Attacher::AttachEngine3D
  Height = 6
  Length = 51
  Placement = pos=(-112,-24,76) rot=(0,0,1;0rad)
  Width = 24
FEATURE [Part::Cut] Cut445
  Base = -> Box477
  Tool = -> Cylinder962
FEATURE [Part::Cut] Cut444
  Base = -> Cut445
  Placement = pos=(0,0,0) rot=(0,0,1;1.5708rad)
  Tool = -> Compound519
FEATURE [Part::Compound] Compound520
  Links = -> [Cut443,Cut444]
  Placement = pos=(0,0,2) rot=(0,0,1;0rad)
FEATURE [Part::Cylinder] Cylinder965  label="Válec965"
  Angle = 360
  AttacherType = Attacher::AttachEngine3D
  Height = 20
  Placement = pos=(-102,-10,66) rot=(0,0,1;0rad)
  Radius = 2.5
FEATURE [Part::Box] Box478  label="Krychle478"
  AttacherType = Attacher::AttachEngine3D
  Height = 26
  Length = 50
  Placement = pos=(-112,-24,56) rot=(0,0,1;0rad)
  Width = 6
FEATURE [Part::Cylinder] Cylinder966  label="Válec966"
  Angle = 360
  AttacherType = Attacher::AttachEngine3D
  Height = 32
  Placement = pos=(0,0,50) rot=(0,0,1;0rad)
  Radius = 74
FEATURE [Part::Cut] Cut446
  Base = -> Box478
  Placement = pos=(0,0,0) rot=(0,0,1;1.5708rad)
  Tool = -> Cylinder966
FEATURE [Part::Cylinder] Cylinder967  label="Válec967"
  Angle = 360
  AttacherType = Attacher::AttachEngine3D
  Height = 10
  Placement = pos=(0,0,72) rot=(0,0,1;0rad)
  Radius = 74
FEATURE [Part::Box] Box479  label="Krychle479"
  AttacherType = Attacher::AttachEngine3D
  Height = 6
  Length = 51
  Placement = pos=(-112,-24,76) rot=(0,0,1;0rad)
  Width = 24
FEATURE [Part::Cut] Cut447
  Base = -> Box479
  Tool = -> Cylinder967
FEATURE [Part::Cylinder] Cylinder968  label="Válec968"
  Angle = 360
  AttacherType = Attacher::AttachEngine3D
  Height = 20
  Placement = pos=(-86,-10,66) rot=(0,0,1;0rad)
  Radius = 2.5
FEATURE [Part::Compound] Compound522
  Links = -> [Cylinder965,Cylinder968]
FEATURE [Part::Cut] Cut448
  Base = -> Cut447
  Placement = pos=(0,0,0) rot=(0,0,1;1.5708rad)
  Tool = -> Compound522
FEATURE [Part::Compound] Compound521
  Links = -> [Cut446,Cut448]
FEATURE [Part::Mirroring] mirror003  label="Compound521 (mirrored)"
  Base = (0,0,0)
  Normal = (1,0,0)
  Source = -> Compound521
FEATURE [Part::Box] Box480  label="Krychle480"
  AttacherType = Attacher::AttachEngine3D
  Height = 26
  Length = 50
  Placement = pos=(3,-112,56) rot=(0,0,1;1.5708rad)
  Width = 6
FEATURE [Part::Cylinder] Cylinder969  label="Válec969"
  Angle = 360
  AttacherType = Attacher::AttachEngine3D
  Height = 40
  Placement = pos=(0,0,42) rot=(0,0,1;0rad)
  Radius = 74
FEATURE [Part::Cut] Cut449
  Base = -> Box480
  Tool = -> Cylinder969
FEATURE [Part::Box] Box481  label="Krychle481"
  AttacherType = Attacher::AttachEngine3D
  Height = 55
  Length = 10
  Placement = pos=(24,-79,29) rot=(0,0,1;1.5708rad)
  Width = 48
FEATURE [Part::Cylinder] Cylinder970  label="Válec970"
  Angle = 360
  AttacherType = Attacher::AttachEngine3D
  Height = 64
  Placement = pos=(0,0,27) rot=(0,0,1;0rad)
  Radius = 74
FEATURE [Part::Cut] Cut450
  Base = -> Box481
  Tool = -> Cylinder970
FEATURE [Part::Box] Box518  label="Krychle518"
  AttacherType = Attacher::AttachEngine3D
  Height = 14
  Length = 18
  Placement = pos=(3,-92,44) rot=(0,0,1;1.5708rad)
  Width = 6
FEATURE [Part::Box] Box519  label="Krychle519"
  AttacherType = Attacher::AttachEngine3D
  Height = 14
  Length = 24
  Placement = pos=(3,-92,44) rot=(0,0,1;1.5708rad)
  Width = 6
FEATURE [Part::Box] Box520  label="Krychle520"
  AttacherType = Attacher::AttachEngine3D
  Height = 14
  Length = 24
  Placement = pos=(3,-92,44) rot=(0,0,1;1.5708rad)
  Width = 6
FEATURE [Part::Chamfer] Chamfer013
  Base = -> Box518
  Edges = 1 edges r=13.99: [Edge4]
FEATURE [Part::Chamfer] Chamfer014
  Base = -> Box519
  Edges = 1 edges r=13.99: [Edge4]
  Placement = pos=(-21,0,0) rot=(0,0,1;0rad)
FEATURE [Part::Chamfer] Chamfer015
  Base = -> Box520
  Edges = 1 edges r=13.99: [Edge4]
  Placement = pos=(21,0,0) rot=(0,0,1;0rad)
FEATURE [Part::Box] Box711  label="Krychle711"
  AttacherType = Attacher::AttachEngine3D
  Height = 10
  Length = 54
  Placement = pos=(-27,68,75) rot=(0,0,1;0rad)
  Width = 70
FEATURE [Part::Compound] Compound890
  Links = -> [Box711]
  Placement = pos=(0,0,-10) rot=(0,0,1;3.92699rad)
FEATURE [Part::Box] Box712  label="Krychle712"
  AttacherType = Attacher::AttachEngine3D
  Height = 10
  Length = 56
  Placement = pos=(-28,79,75) rot=(0,0,1;0rad)
  Width = 52
FEATURE [Part::Compound] Compound891
  Links = -> [Box712]
  Placement = pos=(0,0,-10) rot=(0,0,1;3.92699rad)
FEATURE [Part::Cut] Cut522
  Base = -> Compound890
  Tool = -> Compound891
FEATURE [Part::Box] Box713  label="Krychle713"
  AttacherType = Attacher::AttachEngine3D
  Height = 50
  Length = 42
  Placement = pos=(-21,62,31) rot=(0,0,1;0rad)
  Width = 62
FEATURE [Part::Compound] Compound892
  Links = -> [Box713]
  Placement = pos=(0,0,0) rot=(0,0,1;3.92699rad)
FEATURE [Part::Cut] Cut523
  Base = -> Cut522
  Tool = -> Compound892
FEATURE [Part::Cylinder] Cylinder1760  label="Válec1760"
  Angle = 360
  AttacherType = Attacher::AttachEngine3D
  Height = 40
  Placement = pos=(0,0,44) rot=(0,0,1;0rad)
  Radius = 74
FEATURE [Part::Cut] Cut524
  Base = -> Cut523
  Tool = -> Cylinder1760
FEATURE [Part::Cylinder] Cylinder1761  label="Válec1761"
  Angle = 360
  AttacherType = Attacher::AttachEngine3D
  Height = 50
  Placement = pos=(-24,140,72) rot=(1,0,0;1.5708rad)
  Radius = 1.5
FEATURE [Part::Compound] Compound893
  Links = -> [Cylinder1761]
  Placement = pos=(0,0,0) rot=(0,0,1;3.92699rad)
FEATURE [Part::Cylinder] Cylinder1762  label="Válec1762"
  Angle = 360
  AttacherType = Attacher::AttachEngine3D
  Height = 50
  Placement = pos=(24,140,72) rot=(1,0,0;1.5708rad)
  Radius = 1.5
FEATURE [Part::Compound] Compound894
  Links = -> [Cylinder1762]
  Placement = pos=(0,0,0) rot=(0,0,1;3.92699rad)
FEATURE [Part::Compound] Compound895
  Links = -> [Compound893,Compound894]
  Placement = pos=(0,0,-2) rot=(0,0,1;0rad)
FEATURE [Part::Cylinder] Cylinder1763  label="Válec1763"
  Angle = 360
  AttacherType = Attacher::AttachEngine3D
  Height = 3
  Placement = pos=(-24,138,72) rot=(1,0,0;1.5708rad)
  Radius = 3
FEATURE [Part::Compound] Compound896
  Links = -> [Cylinder1763]
  Placement = pos=(0,0,0) rot=(0,0,1;3.92699rad)
FEATURE [Part::Cylinder] Cylinder1764  label="Válec1764"
  Angle = 360
  AttacherType = Attacher::AttachEngine3D
  Height = 3
  Placement = pos=(24,138,72) rot=(1,0,0;1.5708rad)
  Radius = 3
FEATURE [Part::Compound] Compound897
  Links = -> [Cylinder1764]
  Placement = pos=(0,0,0) rot=(0,0,1;3.92699rad)
FEATURE [Part::Compound] Compound898
  Links = -> [Compound896,Compound897]
  Placement = pos=(0,0,-2) rot=(0,0,1;0rad)
FEATURE [Part::Box] Box714  label="Krychle714"
  AttacherType = Attacher::AttachEngine3D
  Height = 2
  Length = 6
  Placement = pos=(21,71,-48) rot=(0,0,1;0rad)
  Width = 6
FEATURE [Part::Box] Box715  label="Krychle715"
  AttacherType = Attacher::AttachEngine3D
  Height = 2
  Length = 6
  Placement = pos=(-27,71,-48) rot=(0,0,1;0rad)
  Width = 6
FEATURE [Part::Box] Box716  label="Krychle716"
  AttacherType = Attacher::AttachEngine3D
  Height = 2
  Length = 6
  Placement = pos=(-18,132,-48) rot=(0,0,1;0rad)
  Width = 6
FEATURE [Part::Box] Box717  label="Krychle717"
  AttacherType = Attacher::AttachEngine3D
  Height = 2
  Length = 6
  Placement = pos=(12,132,-48) rot=(0,0,1;0rad)
  Width = 6
FEATURE [Part::Compound] Compound899
  Links = -> [Box715,Box716,Box714,Box717]
  Placement = pos=(0,0,117) rot=(0,0,1;3.92699rad)
FEATURE [Part::Cylinder] Cylinder1765  label="Válec1765"
  Angle = 360
  AttacherType = Attacher::AttachEngine3D
  Height = 60
  Placement = pos=(-15,135,-80) rot=(0,0,1;0rad)
  Radius = 1.5
FEATURE [Part::Cylinder] Cylinder1766  label="Válec1766"
  Angle = 360
  AttacherType = Attacher::AttachEngine3D
  Height = 60
  Placement = pos=(15,135,-80) rot=(0,0,1;0rad)
  Radius = 1.5
FEATURE [Part::Cylinder] Cylinder1767  label="Válec1767"
  Angle = 360
  AttacherType = Attacher::AttachEngine3D
  Height = 60
  Placement = pos=(24,73,-80) rot=(0,0,1;0rad)
  Radius = 1.5
FEATURE [Part::Cylinder] Cylinder1768  label="Válec1768"
  Angle = 360
  AttacherType = Attacher::AttachEngine3D
  Height = 60
  Placement = pos=(-24,73,-80) rot=(0,0,1;0rad)
  Radius = 1.5
FEATURE [Part::Compound] Compound900
  Links = -> [Cylinder1767,Cylinder1768,Cylinder1765,Cylinder1766]
  Placement = pos=(0,0,100) rot=(0,0,1;3.92699rad)
FEATURE [Part::Box] Box718  label="Krychle718"
  AttacherType = Attacher::AttachEngine3D
  Height = 18
  Length = 42
  Placement = pos=(-21,-23,22) rot=(0,0,1;0rad)
  Width = 10
FEATURE [Part::Compound] Compound901
  Links = -> [Box718]
  Placement = pos=(63.64,-63.64,43) rot=(0,0,1;3.92699rad)
FEATURE [Part::Cylinder] Cylinder1769  label="Válec1769"
  Angle = 360
  AttacherType = Attacher::AttachEngine3D
  Height = 40
  Placement = pos=(0,0,44) rot=(0,0,1;0rad)
  Radius = 74
FEATURE [Part::Cut] Cut525
  Base = -> Compound901
  Tool = -> Cylinder1769
FEATURE [Part::Cylinder] Cylinder1770  label="Válec1770"
  Angle = 360
  AttacherType = Attacher::AttachEngine3D
  Height = 50
  Placement = pos=(-18,100,72) rot=(1,0,0;1.5708rad)
  Radius = 1.5
FEATURE [Part::Compound] Compound904
  Links = -> [Cylinder1770]
  Placement = pos=(0,0,0) rot=(0,0,1;3.92699rad)
FEATURE [Part::Cylinder] Cylinder1771  label="Válec1771"
  Angle = 360
  AttacherType = Attacher::AttachEngine3D
  Height = 50
  Placement = pos=(18,100,72) rot=(1,0,0;1.5708rad)
  Radius = 1.5
FEATURE [Part::Compound] Compound903
  Links = -> [Cylinder1771]
  Placement = pos=(0,0,0) rot=(0,0,1;3.92699rad)
FEATURE [Part::Compound] Compound902
  Links = -> [Compound904,Compound903]
  Placement = pos=(0,0,1) rot=(0,0,1;0rad)
FEATURE [Part::Cut] Cut526
  Base = -> Cut525
  Tool = -> Compound902
FEATURE [Part::Cut] Cut527
  Base = -> Cut526
  Tool = -> Compound900
FEATURE [Part::Cut] Cut528
  Base = -> Cut524
  Tool = -> Compound899
FEATURE [Part::Chamfer] Chamfer
  Base = -> Cut528
  Edges = 2 edges r=3: [Edge50,Edge57]
FEATURE [Part::Cut] Cut529
  Base = -> Chamfer
  Tool = -> Compound898
FEATURE [Part::Cut] Cut530
  Base = -> Cut529
  Tool = -> Compound895
FEATURE [Part::FeaturePython] Tube044  label="ZKL-6017"  # WARN: FeaturePython — macro-defined, semantics opaque (R4)
  AttacherType = Attacher::AttachEngine3D
  Height = 22
  InnerRadius = 42.5
  OuterRadius = 65
  Placement = pos=(0,0,3) rot=(0,0,1;0rad)
FEATURE [Part::Cylinder] Cylinder  label="Válec"
  Angle = 360
  AttacherType = Attacher::AttachEngine3D
  Height = 50
  Placement = pos=(50,-50,12) rot=(0,0,1;0rad)
  Radius = 1.5
FEATURE [Part::Box] Box720  label="Krychle720"
  AttacherType = Attacher::AttachEngine3D
  Height = 20
  Length = 80
  Placement = pos=(-118.17,-24,82.63) rot=(0,1,0;1.23918rad)
  Width = 6
FEATURE [Part::Cylinder] Cylinder1772  label="Válec1772"
  Angle = 360
  AttacherType = Attacher::AttachEngine3D
  Height = 32
  Placement = pos=(0,0,50) rot=(0,0,1;0rad)
  Radius = 74
FEATURE [Part::Box] Box724  label="Krychle724"
  AttacherType = Attacher::AttachEngine3D
  Height = 32
  Length = 57
  Placement = pos=(-122,-24,52) rot=(0,0,1;0rad)
  Width = 6
FEATURE [Part::Box] Box725  label="Krychle725"
  AttacherType = Attacher::AttachEngine3D
  Height = 49
  Length = 57
  Placement = pos=(-149,-24,29) rot=(0,0,1;0rad)
  Width = 6
FEATURE [Part::Box] Box726  label="Krychle726"
  AttacherType = Attacher::AttachEngine3D
  Height = 20
  Length = 80
  Placement = pos=(-131.7,-24,54.35) rot=(0,1,0;0.349066rad)
  Width = 6
FEATURE [Part::Box] Box727  label="Krychle727"
  AttacherType = Attacher::AttachEngine3D
  Height = 49
  Length = 44
  Placement = pos=(-93,-24,29) rot=(0,0,1;0rad)
  Width = 6
FEATURE [Part::Box] Box728  label="Krychle728"
  AttacherType = Attacher::AttachEngine3D
  Height = 20
  Length = 80
  Placement = pos=(-131.7,-24,54.35) rot=(0,1,0;0.349066rad)
  Width = 6
FEATURE [Part::Cut] Cut531
  Base = -> Box724
  Tool = -> Box728
FEATURE [Part::Cut] Cut532
  Base = -> Box727
  Tool = -> Box720
FEATURE [Part::Box] Box729  label="Krychle729"
  AttacherType = Attacher::AttachEngine3D
  Height = 20
  Length = 80
  Placement = pos=(-131.7,-24,54.35) rot=(0,1,0;0.349066rad)
  Width = 6
FEATURE [Part::Box] Box730  label="Krychle730"
  AttacherType = Attacher::AttachEngine3D
  Height = 49
  Length = 44
  Placement = pos=(-93,-24,29) rot=(0,0,1;0rad)
  Width = 6
FEATURE [Part::Box] Box731  label="Krychle731"
  AttacherType = Attacher::AttachEngine3D
  Height = 32
  Length = 57
  Placement = pos=(-122,-24,52) rot=(0,0,1;0rad)
  Width = 6
FEATURE [Part::Cut] Cut535
  Base = -> Box731
  Tool = -> Box729
FEATURE [Part::Box] Box732  label="Krychle732"
  AttacherType = Attacher::AttachEngine3D
  Height = 20
  Length = 80
  Placement = pos=(-118.17,-24,82.63) rot=(0,1,0;1.24616rad)
  Width = 6
FEATURE [Part::Cut] Cut536
  Base = -> Box730
  Tool = -> Box732
FEATURE [Part::Cylinder] Cylinder1773  label="Válec1773"
  Angle = 360
  AttacherType = Attacher::AttachEngine3D
  Height = 60
  Placement = pos=(0,0,26) rot=(0,0,1;0rad)
  Radius = 74
FEATURE [Part::Cut] Cut533
  Base = -> Cut536
  Tool = -> Cylinder1773
FEATURE [Part::Cylinder] Cylinder1774  label="Válec1774"
  Angle = 360
  AttacherType = Attacher::AttachEngine3D
  Height = 60
  Placement = pos=(0,0,26) rot=(0,0,1;0rad)
  Radius = 74
FEATURE [Part::Cut] Cut534
  Base = -> Cut535
  Tool = -> Cylinder1774
FEATURE [Part::Compound] Compound
  Links = -> [Cut534,Cut533]
FEATURE [Part::Box] Box733  label="Krychle733"
  AttacherType = Attacher::AttachEngine3D
  Height = 49
  Length = 10
  Placement = pos=(-79,-24,29) rot=(0,0,1;0rad)
  Width = 56
FEATURE [Part::Box] Box734  label="Krychle734"
  AttacherType = Attacher::AttachEngine3D
  Height = 20
  Length = 200
  Placement = pos=(-140,-23,84) rot=(0,0,1;0rad)
  Width = 20
FEATURE [Part::Cylinder] Cylinder1775  label="Válec1775"
  Angle = 360
  AttacherType = Attacher::AttachEngine3D
  Height = 5
  Placement = pos=(-86,-10,66) rot=(0,0,1;0rad)
  Radius = 5
FEATURE [Part::Cylinder] Cylinder1776  label="Válec1776"
  Angle = 360
  AttacherType = Attacher::AttachEngine3D
  Height = 5
  Placement = pos=(-102,-10,66) rot=(0,0,1;0rad)
  Radius = 5
FEATURE [Part::Compound] Compound905
  Links = -> [Cylinder1776,Cylinder1775]
FEATURE [Part::Box] Box001  label="Krychle001"
  AttacherType = Attacher::AttachEngine3D
  Height = 8
  Length = 8
  Placement = pos=(-68,-14,35) rot=(0,0,1;1.5708rad)
  Width = 2.5
FEATURE [Part::Box] Box735  label="Krychle735"
  AttacherType = Attacher::AttachEngine3D
  Height = 8
  Length = 8
  Placement = pos=(-48,-14,35) rot=(0,0,1;1.5708rad)
  Width = 20
FEATURE [Part::Cylinder] Cylinder1777  label="Válec1777"
  Angle = 360
  AttacherType = Attacher::AttachEngine3D
  Height = 40
  Placement = pos=(-86,-10,39) rot=(0,1,0;1.5708rad)
  Radius = 2.5
FEATURE [Part::Cylinder] Cylinder1778  label="Válec1778"
  Angle = 360
  AttacherType = Attacher::AttachEngine3D
  Height = 40
  Placement = pos=(-86,20,39) rot=(0,1,0;1.5708rad)
  Radius = 2.5
FEATURE [Part::Box] Box736  label="Krychle736"
  AttacherType = Attacher::AttachEngine3D
  Height = 8
  Length = 8
  Placement = pos=(-48,16,35) rot=(0,0,1;1.5708rad)
  Width = 20
FEATURE [Part::Box] Box737  label="Krychle737"
  AttacherType = Attacher::AttachEngine3D
  Height = 8
  Length = 8
  Placement = pos=(-68,16,35) rot=(0,0,1;1.5708rad)
  Width = 2.5
FEATURE [Part::Cylinder] Cylinder1779  label="Válec1779"
  Angle = 360
  AttacherType = Attacher::AttachEngine3D
  Height = 40
  Placement = pos=(-86,-10,69) rot=(0,1,0;1.5708rad)
  Radius = 2.5
FEATURE [Part::Box] Box738  label="Krychle738"
  AttacherType = Attacher::AttachEngine3D
  Height = 8
  Length = 8
  Placement = pos=(-48,-14,65) rot=(0,0,1;1.5708rad)
  Width = 20
FEATURE [Part::Box] Box739  label="Krychle739"
  AttacherType = Attacher::AttachEngine3D
  Height = 8
  Length = 8
  Placement = pos=(-68,-14,65) rot=(0,0,1;1.5708rad)
  Width = 2.5
FEATURE [Part::Compound] Compound906
  Links = -> [Cylinder1777,Cylinder1778,Cylinder1779]
FEATURE [Part::Compound] Compound907
  Links = -> [Box735,Box736,Box738]
FEATURE [Part::Compound] Compound908
  Links = -> [Box001,Box737,Box739]
FEATURE [Part::Chamfer] Chamfer058
  Base = -> Cut407
  Edges = 1 edges r=12: [Edge3]
FEATURE [Part::Chamfer] Chamfer059
  Base = -> Box733
  Edges = 1 edges r=3: [Edge3]
FEATURE [Part::Cut] Cut537
  Base = -> Chamfer059
  Tool = -> Compound906
FEATURE [Part::Cylinder] Cylinder1780  label="Válec1780"
  Angle = 360
  AttacherType = Attacher::AttachEngine3D
  Height = 60
  Placement = pos=(0,0,26) rot=(0,0,1;0rad)
  Radius = 74
FEATURE [Part::Cut] Cut538
  Base = -> Cut537
  Tool = -> Cylinder1780
FEATURE [Part::Box] Box740  label="Krychle740"
  AttacherType = Attacher::AttachEngine3D
  Height = 55
  Length = 148
  Placement = pos=(-74,0,29) rot=(0,0,1;0rad)
  Width = 74
FEATURE [Part::Cut] Cut539
  Base = -> Cut538
  Tool = -> Box740
FEATURE [Part::Box] Box741  label="Krychle741"
  AttacherType = Attacher::AttachEngine3D
  Height = 55
  Length = 148
  Placement = pos=(-74,0,29) rot=(0,0,1;0rad)
  Width = 74
FEATURE [Part::Cut] Cut540
  Base = -> Chamfer058
  Tool = -> Box741
FEATURE [Part::Compound] Compound909  label="Base_side-balancer1"
  Links = -> [Cut540,Cut539,Compound,Chamfer004]
FEATURE [Part::Mirroring] mirror004  label="Base_side-balancer (mirrored)"
  Base = (0,0,0)
  Normal = (1,0,0)
  Source = -> Compound909
FEATURE [Part::Box] Box742  label="Krychle742"
  AttacherType = Attacher::AttachEngine3D
  Height = 2
  Length = 6
  Placement = pos=(-112,4,60) rot=(0,0,1;0rad)
  Width = 6
FEATURE [Part::Box] Box743  label="Krychle743"
  AttacherType = Attacher::AttachEngine3D
  Height = 20
  Length = 20
  Placement = pos=(-106,4,56) rot=(0,0,1;0rad)
  Width = 80
FEATURE [Part::Box] Box744  label="Krychle744"
  AttacherType = Attacher::AttachEngine3D
  Height = 2
  Length = 6
  Placement = pos=(-112,22,60) rot=(0,0,1;0rad)
  Width = 6
FEATURE [Part::Box] Box745  label="Krychle745"
  AttacherType = Attacher::AttachEngine3D
  Height = 2
  Length = 6
  Placement = pos=(-86,22,60) rot=(0,0,1;0rad)
  Width = 6
FEATURE [Part::Cylinder] Cylinder1781  label="Válec1781"
  Angle = 360
  AttacherType = Attacher::AttachEngine3D
  Height = 20
  Placement = pos=(-83,25,54) rot=(0,0,1;0rad)
  Radius = 1.5
FEATURE [Part::Box] Box746  label="Krychle746"
  AttacherType = Attacher::AttachEngine3D
  Height = 2
  Length = 6
  Placement = pos=(-86,4,60) rot=(0,0,1;0rad)
  Width = 6
FEATURE [Part::Compound] Compound912
  Links = -> [Box742,Box744,Box746,Box745]
FEATURE [Part::Cylinder] Cylinder1782  label="Válec1782"
  Angle = 360
  AttacherType = Attacher::AttachEngine3D
  Height = 20
  Placement = pos=(-83,7,54) rot=(0,0,1;0rad)
  Radius = 1.5
FEATURE [Part::Cylinder] Cylinder1783  label="Válec1783"
  Angle = 360
  AttacherType = Attacher::AttachEngine3D
  Height = 20
  Placement = pos=(-109,7,54) rot=(0,0,1;0rad)
  Radius = 1.5
FEATURE [Part::Cylinder] Cylinder1784  label="Válec1784"
  Angle = 360
  AttacherType = Attacher::AttachEngine3D
  Height = 20
  Placement = pos=(-109,25,54) rot=(0,0,1;0rad)
  Radius = 1.5
FEATURE [Part::Compound] Compound913
  Links = -> [Cylinder1782,Cylinder1781,Cylinder1783,Cylinder1784]
FEATURE [Part::Box] Box747  label="Krychle747"
  AttacherType = Attacher::AttachEngine3D
  Height = 26
  Length = 38
  Placement = pos=(-112,0,56) rot=(0,0,1;0rad)
  Width = 32
FEATURE [Part::Cylinder] Cylinder1785  label="Válec1785"
  Angle = 360
  AttacherType = Attacher::AttachEngine3D
  Height = 3
  Placement = pos=(-112,16,66) rot=(0,1,0;1.5708rad)
  Radius = 5
FEATURE [Part::Cylinder] Cylinder1786  label="Válec1786"
  Angle = 360
  AttacherType = Attacher::AttachEngine3D
  Height = 20
  Placement = pos=(-117,16,66) rot=(0,1,0;1.5708rad)
  Radius = 2.5
FEATURE [Part::Box] Box748  label="Krychle748"
  AttacherType = Attacher::AttachEngine3D
  Height = 6
  Length = 62
  Placement = pos=(-122,-24,76) rot=(0,0,1;0rad)
  Width = 56
FEATURE [Part::Cylinder] Cylinder1787  label="Válec1787"
  Angle = 360
  AttacherType = Attacher::AttachEngine3D
  Height = 32
  Placement = pos=(0,0,66) rot=(0,0,1;0rad)
  Radius = 74
FEATURE [Part::Cut] Cut545
  Base = -> Box748
  Tool = -> Cylinder1787
FEATURE [Part::Cylinder] Cylinder1788  label="Válec1788"
  Angle = 360
  AttacherType = Attacher::AttachEngine3D
  Height = 20
  Placement = pos=(-90,-10,66) rot=(0,0,1;0rad)
  Radius = 2.5
FEATURE [Part::Cylinder] Cylinder1789  label="Válec1789"
  Angle = 360
  AttacherType = Attacher::AttachEngine3D
  Height = 20
  Placement = pos=(-110,-10,66) rot=(0,0,1;0rad)
  Radius = 2.5
FEATURE [Part::Compound] Compound914
  Links = -> [Cylinder1789,Cylinder1788]
FEATURE [Part::Cut] Cut544
  Base = -> Cut545
  Placement = pos=(0,0,2) rot=(0,0,1;0rad)
  Tool = -> Compound914
FEATURE [Part::Cut] Cut546
  Base = -> Box747
  Tool = -> Box743
FEATURE [Part::Cut] Cut547
  Base = -> Cut546
  Tool = -> Compound912
FEATURE [Part::Cut] Cut541
  Base = -> Cut547
  Tool = -> Compound913
FEATURE [Part::Cut] Cut542
  Base = -> Cut541
  Tool = -> Cylinder1786
FEATURE [Part::Cut] Cut543
  Base = -> Cut542
  Tool = -> Cylinder1785
FEATURE [Part::Chamfer] Chamfer060
  Base = -> Cut543
  Edges = 1 edges r=2: [Edge4]
  Placement = pos=(0,0,2) rot=(0,0,1;0rad)
FEATURE [Part::Chamfer] Chamfer062
  Base = -> Cut544
  Edges = 1 edges r=12: [Edge3]
FEATURE [Part::Box] Box749  label="Krychle749"
  AttacherType = Attacher::AttachEngine3D
  Height = 55
  Length = 148
  Placement = pos=(-74,0,29) rot=(0,0,1;0rad)
  Width = 74
FEATURE [Part::Box] Box750  label="Krychle750"
  AttacherType = Attacher::AttachEngine3D
  Height = 55
  Length = 148
  Placement = pos=(-74,0,29) rot=(0,0,1;0rad)
  Width = 74
FEATURE [Part::Cylinder] Cylinder1790  label="Válec1790"
  Angle = 360
  AttacherType = Attacher::AttachEngine3D
  Height = 60
  Placement = pos=(0,0,26) rot=(0,0,1;0rad)
  Radius = 74
FEATURE [Part::Cylinder] Cylinder1791  label="Válec1791"
  Angle = 360
  AttacherType = Attacher::AttachEngine3D
  Height = 40
  Placement = pos=(-86,-10,69) rot=(0,1,0;1.5708rad)
  Radius = 2.5
FEATURE [Part::Cut] Cut552
  Base = -> Chamfer062
  Tool = -> Box749
FEATURE [Part::Box] Box751  label="Krychle751"
  AttacherType = Attacher::AttachEngine3D
  Height = 20
  Length = 80
  Placement = pos=(-131.7,-24,54.35) rot=(0,1,0;0.349066rad)
  Width = 6
FEATURE [Part::Box] Box752  label="Krychle752"
  AttacherType = Attacher::AttachEngine3D
  Height = 49
  Length = 44
  Placement = pos=(-93,-24,29) rot=(0,0,1;0rad)
  Width = 6
FEATURE [Part::Box] Box753  label="Krychle753"
  AttacherType = Attacher::AttachEngine3D
  Height = 32
  Length = 57
  Placement = pos=(-122,-24,52) rot=(0,0,1;0rad)
  Width = 6
FEATURE [Part::Cut] Cut553
  Base = -> Box753
  Tool = -> Box751
FEATURE [Part::Box] Box754  label="Krychle754"
  AttacherType = Attacher::AttachEngine3D
  Height = 20
  Length = 80
  Placement = pos=(-118.17,-24,82.63) rot=(0,1,0;1.24616rad)
  Width = 6
FEATURE [Part::Cut] Cut548
  Base = -> Box752
  Tool = -> Box754
FEATURE [Part::Cylinder] Cylinder1792  label="Válec1792"
  Angle = 360
  AttacherType = Attacher::AttachEngine3D
  Height = 60
  Placement = pos=(0,0,26) rot=(0,0,1;0rad)
  Radius = 74
FEATURE [Part::Cut] Cut555
  Base = -> Cut548
  Tool = -> Cylinder1792
FEATURE [Part::Cylinder] Cylinder1793  label="Válec1793"
  Angle = 360
  AttacherType = Attacher::AttachEngine3D
  Height = 60
  Placement = pos=(0,0,26) rot=(0,0,1;0rad)
  Radius = 74
FEATURE [Part::Cut] Cut554
  Base = -> Cut553
  Tool = -> Cylinder1793
FEATURE [Part::Compound] Compound911
  Links = -> [Cut554,Cut555]
FEATURE [Part::Box] Box755  label="Krychle755"
  AttacherType = Attacher::AttachEngine3D
  Height = 49
  Length = 10
  Placement = pos=(-79,-24,29) rot=(0,0,1;0rad)
  Width = 56
FEATURE [Part::Chamfer] Chamfer061
  Base = -> Box755
  Edges = 1 edges r=3: [Edge3]
FEATURE [Part::Cylinder] Cylinder1794  label="Válec1794"
  Angle = 360
  AttacherType = Attacher::AttachEngine3D
  Height = 40
  Placement = pos=(-86,-10,39) rot=(0,1,0;1.5708rad)
  Radius = 2.5
FEATURE [Part::Cylinder] Cylinder1795  label="Válec1795"
  Angle = 360
  AttacherType = Attacher::AttachEngine3D
  Height = 40
  Placement = pos=(-86,20,39) rot=(0,1,0;1.5708rad)
  Radius = 2.5
FEATURE [Part::Compound] Compound910
  Links = -> [Cylinder1794,Cylinder1795,Cylinder1791]
FEATURE [Part::Cut] Cut549
  Base = -> Chamfer061
  Tool = -> Compound910
FEATURE [Part::Cut] Cut550
  Base = -> Cut549
  Tool = -> Cylinder1790
FEATURE [Part::Cut] Cut551
  Base = -> Cut550
  Tool = -> Box750
FEATURE [Part::Compound] Compound915  label="Base_side-balancer"
  Links = -> [Cut552,Cut551,Compound911,Chamfer060]
FEATURE [Part::Cylinder] Cylinder1796  label="Válec1796"
  Angle = 360
  AttacherType = Attacher::AttachEngine3D
  Height = 20
  Placement = pos=(-109,7,54) rot=(0,0,1;0rad)
  Radius = 1.5
FEATURE [Part::Cylinder] Cylinder1797  label="Válec1797"
  Angle = 360
  AttacherType = Attacher::AttachEngine3D
  Height = 20
  Placement = pos=(-109,25,54) rot=(0,0,1;0rad)
  Radius = 1.5
FEATURE [Part::Box] Box756  label="Krychle756"
  AttacherType = Attacher::AttachEngine3D
  Height = 2
  Length = 6
  Placement = pos=(-112,4,60) rot=(0,0,1;0rad)
  Width = 6
FEATURE [Part::Box] Box757  label="Krychle757"
  AttacherType = Attacher::AttachEngine3D
  Height = 20
  Length = 20
  Placement = pos=(-106,4,56) rot=(0,0,1;0rad)
  Width = 80
FEATURE [Part::Box] Box758  label="Krychle758"
  AttacherType = Attacher::AttachEngine3D
  Height = 2
  Length = 6
  Placement = pos=(-112,22,60) rot=(0,0,1;0rad)
  Width = 6
FEATURE [Part::Box] Box759  label="Krychle759"
  AttacherType = Attacher::AttachEngine3D
  Height = 2
  Length = 6
  Placement = pos=(-86,22,60) rot=(0,0,1;0rad)
  Width = 6
FEATURE [Part::Cylinder] Cylinder1798  label="Válec1798"
  Angle = 360
  AttacherType = Attacher::AttachEngine3D
  Height = 20
  Placement = pos=(-83,25,54) rot=(0,0,1;0rad)
  Radius = 1.5
FEATURE [Part::Box] Box760  label="Krychle760"
  AttacherType = Attacher::AttachEngine3D
  Height = 2
  Length = 6
  Placement = pos=(-86,4,60) rot=(0,0,1;0rad)
  Width = 6
FEATURE [Part::Cylinder] Cylinder1799  label="Válec1799"
  Angle = 360
  AttacherType = Attacher::AttachEngine3D
  Height = 20
  Placement = pos=(-83,7,54) rot=(0,0,1;0rad)
  Radius = 1.5
FEATURE [Part::Box] Box761  label="Krychle761"
  AttacherType = Attacher::AttachEngine3D
  Height = 26
  Length = 38
  Placement = pos=(-112,0,56) rot=(0,0,1;0rad)
  Width = 32
FEATURE [Part::Cylinder] Cylinder1800  label="Válec1800"
  Angle = 360
  AttacherType = Attacher::AttachEngine3D
  Height = 3
  Placement = pos=(-112,16,66) rot=(0,1,0;1.5708rad)
  Radius = 5
FEATURE [Part::Cylinder] Cylinder1801  label="Válec1801"
  Angle = 360
  AttacherType = Attacher::AttachEngine3D
  Height = 20
  Placement = pos=(-117,16,66) rot=(0,1,0;1.5708rad)
  Radius = 2.5
FEATURE [Part::Box] Box762  label="Krychle762"
  AttacherType = Attacher::AttachEngine3D
  Height = 6
  Length = 68
  Placement = pos=(-130,-24,76) rot=(0,0,1;0rad)
  Width = 56
FEATURE [Part::Cylinder] Cylinder1802  label="Válec1802"
  Angle = 360
  AttacherType = Attacher::AttachEngine3D
  Height = 32
  Placement = pos=(0,0,66) rot=(0,0,1;0rad)
  Radius = 74
FEATURE [Part::Cylinder] Cylinder1803  label="Válec1803"
  Angle = 360
  AttacherType = Attacher::AttachEngine3D
  Height = 20
  Placement = pos=(-90,-10,66) rot=(0,0,1;0rad)
  Radius = 2.5
FEATURE [Part::Cylinder] Cylinder1804  label="Válec1804"
  Angle = 360
  AttacherType = Attacher::AttachEngine3D
  Height = 20
  Placement = pos=(-110,-10,66) rot=(0,0,1;0rad)
  Radius = 2.5
FEATURE [Part::Box] Box763  label="Krychle763"
  AttacherType = Attacher::AttachEngine3D
  Height = 55
  Length = 148
  Placement = pos=(-74,0,29) rot=(0,0,1;0rad)
  Width = 74
FEATURE [Part::Box] Box764  label="Krychle764"
  AttacherType = Attacher::AttachEngine3D
  Height = 55
  Length = 148
  Placement = pos=(-74,0,29) rot=(0,0,1;0rad)
  Width = 74
FEATURE [Part::Cylinder] Cylinder1805  label="Válec1805"
  Angle = 360
  AttacherType = Attacher::AttachEngine3D
  Height = 60
  Placement = pos=(0,0,26) rot=(0,0,1;0rad)
  Radius = 74
FEATURE [Part::Cylinder] Cylinder1806  label="Válec1806"
  Angle = 360
  AttacherType = Attacher::AttachEngine3D
  Height = 40
  Placement = pos=(-86,-10,69) rot=(0,1,0;1.5708rad)
  Radius = 2.5
FEATURE [Part::Box] Box765  label="Krychle765"
  AttacherType = Attacher::AttachEngine3D
  Height = 20
  Length = 80
  Placement = pos=(-138.7,-24,54.35) rot=(0,1,0;0.349066rad)
  Width = 6
FEATURE [Part::Box] Box766  label="Krychle766"
  AttacherType = Attacher::AttachEngine3D
  Height = 49
  Length = 44
  Placement = pos=(-93,-24,29) rot=(0,0,1;0rad)
  Width = 6
FEATURE [Part::Box] Box767  label="Krychle767"
  AttacherType = Attacher::AttachEngine3D
  Height = 32
  Length = 57
  Placement = pos=(-130,-24,52) rot=(0,0,1;0rad)
  Width = 6
FEATURE [Part::Box] Box768  label="Krychle768"
  AttacherType = Attacher::AttachEngine3D
  Height = 20
  Length = 80
  Placement = pos=(-118.17,-24,82.63) rot=(0,1,0;1.24616rad)
  Width = 6
FEATURE [Part::Cylinder] Cylinder1807  label="Válec1807"
  Angle = 360
  AttacherType = Attacher::AttachEngine3D
  Height = 60
  Placement = pos=(0,0,26) rot=(0,0,1;0rad)
  Radius = 74
FEATURE [Part::Cylinder] Cylinder1808  label="Válec1808"
  Angle = 360
  AttacherType = Attacher::AttachEngine3D
  Height = 60
  Placement = pos=(0,0,26) rot=(0,0,1;0rad)
  Radius = 74
FEATURE [Part::Box] Box769  label="Krychle769"
  AttacherType = Attacher::AttachEngine3D
  Height = 49
  Length = 10
  Placement = pos=(-79,-24,29) rot=(0,0,1;0rad)
  Width = 56
FEATURE [Part::Cylinder] Cylinder1809  label="Válec1809"
  Angle = 360
  AttacherType = Attacher::AttachEngine3D
  Height = 40
  Placement = pos=(-86,-10,39) rot=(0,1,0;1.5708rad)
  Radius = 2.5
FEATURE [Part::Cylinder] Cylinder1810  label="Válec1810"
  Angle = 360
  AttacherType = Attacher::AttachEngine3D
  Height = 40
  Placement = pos=(-86,20,39) rot=(0,1,0;1.5708rad)
  Radius = 2.5
FEATURE [Part::Cut] Cut558
  Base = -> Box767
  Tool = -> Box765
FEATURE [Part::Cut] Cut559
  Base = -> Cut558
  Tool = -> Cylinder1808
FEATURE [Part::Cut] Cut561
  Base = -> Box762
  Tool = -> Cylinder1802
FEATURE [Part::Compound] Compound918
  Links = -> [Box756,Box758,Box760,Box759]
FEATURE [Part::Compound] Compound920
  Links = -> [Cylinder1799,Cylinder1798,Cylinder1796,Cylinder1797]
FEATURE [Part::Compound] Compound921
  Links = -> [Cylinder1804,Cylinder1803]
  Placement = pos=(-8,0,0) rot=(0,0,1;0rad)
FEATURE [Part::Cut] Cut562
  Base = -> Cut561
  Placement = pos=(0,0,2) rot=(0,0,1;0rad)
  Tool = -> Compound921
FEATURE [Part::Chamfer] Chamfer063
  Base = -> Cut562
  Edges = 1 edges r=20: [Edge3]
FEATURE [Part::Cut] Cut566
  Base = -> Chamfer063
  Tool = -> Box763
FEATURE [Part::Chamfer] Chamfer065
  Base = -> Box769
  Edges = 1 edges r=3: [Edge3]
FEATURE [Part::Cut] Cut567
  Base = -> Box761
  Tool = -> Box757
FEATURE [Part::Cut] Cut569
  Base = -> Cut567
  Tool = -> Compound918
FEATURE [Part::Cut] Cut563
  Base = -> Cut569
  Tool = -> Compound920
FEATURE [Part::Cut] Cut564
  Base = -> Cut563
  Tool = -> Cylinder1801
FEATURE [Part::Cut] Cut560
  Base = -> Cut564
  Tool = -> Cylinder1800
FEATURE [Part::Chamfer] Chamfer064
  Base = -> Cut560
  Edges = 1 edges r=2: [Edge4]
  Placement = pos=(0,0,2) rot=(0,0,1;0rad)
FEATURE [Part::Cut] Cut570
  Base = -> Box766
  Tool = -> Box768
FEATURE [Part::Cut] Cut565
  Base = -> Cut570
  Tool = -> Cylinder1807
FEATURE [Part::Compound] Compound917
  Links = -> [Cut559,Cut565]
FEATURE [Part::Cylinder] Cylinder1811  label="Válec1811"
  Angle = 360
  AttacherType = Attacher::AttachEngine3D
  Height = 20
  Placement = pos=(-109,7,54) rot=(0,0,1;0rad)
  Radius = 1.5
FEATURE [Part::Cylinder] Cylinder1812  label="Válec1812"
  Angle = 360
  AttacherType = Attacher::AttachEngine3D
  Height = 20
  Placement = pos=(-109,25,54) rot=(0,0,1;0rad)
  Radius = 1.5
FEATURE [Part::Box] Box770  label="Krychle770"
  AttacherType = Attacher::AttachEngine3D
  Height = 2
  Length = 6
  Placement = pos=(-112,4,60) rot=(0,0,1;0rad)
  Width = 6
FEATURE [Part::Box] Box771  label="Krychle771"
  AttacherType = Attacher::AttachEngine3D
  Height = 20
  Length = 20
  Placement = pos=(-106,4,56) rot=(0,0,1;0rad)
  Width = 80
FEATURE [Part::Box] Box772  label="Krychle772"
  AttacherType = Attacher::AttachEngine3D
  Height = 2
  Length = 6
  Placement = pos=(-112,22,60) rot=(0,0,1;0rad)
  Width = 6
FEATURE [Part::Box] Box773  label="Krychle773"
  AttacherType = Attacher::AttachEngine3D
  Height = 2
  Length = 6
  Placement = pos=(-86,22,60) rot=(0,0,1;0rad)
  Width = 6
FEATURE [Part::Cylinder] Cylinder1813  label="Válec1813"
  Angle = 360
  AttacherType = Attacher::AttachEngine3D
  Height = 20
  Placement = pos=(-83,25,54) rot=(0,0,1;0rad)
  Radius = 1.5
FEATURE [Part::Box] Box774  label="Krychle774"
  AttacherType = Attacher::AttachEngine3D
  Height = 2
  Length = 6
  Placement = pos=(-86,4,60) rot=(0,0,1;0rad)
  Width = 6
FEATURE [Part::Cylinder] Cylinder1814  label="Válec1814"
  Angle = 360
  AttacherType = Attacher::AttachEngine3D
  Height = 20
  Placement = pos=(-83,7,54) rot=(0,0,1;0rad)
  Radius = 1.5
FEATURE [Part::Box] Box775  label="Krychle775"
  AttacherType = Attacher::AttachEngine3D
  Height = 26
  Length = 38
  Placement = pos=(-112,0,56) rot=(0,0,1;0rad)
  Width = 32
FEATURE [Part::Cut] Cut582
  Base = -> Box775
  Tool = -> Box771
FEATURE [Part::Cylinder] Cylinder1815  label="Válec1815"
  Angle = 360
  AttacherType = Attacher::AttachEngine3D
  Height = 3
  Placement = pos=(-112,16,66) rot=(0,1,0;1.5708rad)
  Radius = 5
FEATURE [Part::Cylinder] Cylinder1816  label="Válec1816"
  Angle = 360
  AttacherType = Attacher::AttachEngine3D
  Height = 20
  Placement = pos=(-117,16,66) rot=(0,1,0;1.5708rad)
  Radius = 2.5
FEATURE [Part::Box] Box776  label="Krychle776"
  AttacherType = Attacher::AttachEngine3D
  Height = 6
  Length = 68
  Placement = pos=(-130,-24,76) rot=(0,0,1;0rad)
  Width = 56
FEATURE [Part::Cylinder] Cylinder1817  label="Válec1817"
  Angle = 360
  AttacherType = Attacher::AttachEngine3D
  Height = 32
  Placement = pos=(0,0,66) rot=(0,0,1;0rad)
  Radius = 74
FEATURE [Part::Cut] Cut571
  Base = -> Box776
  Tool = -> Cylinder1817
FEATURE [Part::Cylinder] Cylinder1818  label="Válec1818"
  Angle = 360
  AttacherType = Attacher::AttachEngine3D
  Height = 20
  Placement = pos=(-90,-10,66) rot=(0,0,1;0rad)
  Radius = 2.5
FEATURE [Part::Cylinder] Cylinder1819  label="Válec1819"
  Angle = 360
  AttacherType = Attacher::AttachEngine3D
  Height = 20
  Placement = pos=(-110,-10,66) rot=(0,0,1;0rad)
  Radius = 2.5
FEATURE [Part::Box] Box777  label="Krychle777"
  AttacherType = Attacher::AttachEngine3D
  Height = 55
  Length = 148
  Placement = pos=(-74,0,29) rot=(0,0,1;0rad)
  Width = 74
FEATURE [Part::Box] Box778  label="Krychle778"
  AttacherType = Attacher::AttachEngine3D
  Height = 55
  Length = 148
  Placement = pos=(-74,0,29) rot=(0,0,1;0rad)
  Width = 74
FEATURE [Part::Cylinder] Cylinder1820  label="Válec1820"
  Angle = 360
  AttacherType = Attacher::AttachEngine3D
  Height = 60
  Placement = pos=(0,0,26) rot=(0,0,1;0rad)
  Radius = 74
FEATURE [Part::Cylinder] Cylinder1821  label="Válec1821"
  Angle = 360
  AttacherType = Attacher::AttachEngine3D
  Height = 40
  Placement = pos=(-86,-10,69) rot=(0,1,0;1.5708rad)
  Radius = 2.5
FEATURE [Part::Box] Box779  label="Krychle779"
  AttacherType = Attacher::AttachEngine3D
  Height = 20
  Length = 80
  Placement = pos=(-138.7,-24,54.35) rot=(0,1,0;0.349066rad)
  Width = 6
FEATURE [Part::Box] Box780  label="Krychle780"
  AttacherType = Attacher::AttachEngine3D
  Height = 49
  Length = 44
  Placement = pos=(-93,-24,29) rot=(0,0,1;0rad)
  Width = 6
FEATURE [Part::Box] Box781  label="Krychle781"
  AttacherType = Attacher::AttachEngine3D
  Height = 32
  Length = 57
  Placement = pos=(-130,-24,52) rot=(0,0,1;0rad)
  Width = 6
FEATURE [Part::Cut] Cut578
  Base = -> Box781
  Tool = -> Box779
FEATURE [Part::Box] Box782  label="Krychle782"
  AttacherType = Attacher::AttachEngine3D
  Height = 20
  Length = 80
  Placement = pos=(-118.17,-24,82.63) rot=(0,1,0;1.24616rad)
  Width = 6
FEATURE [Part::Cut] Cut585
  Base = -> Box780
  Tool = -> Box782
FEATURE [Part::Cylinder] Cylinder1822  label="Válec1822"
  Angle = 360
  AttacherType = Attacher::AttachEngine3D
  Height = 60
  Placement = pos=(0,0,26) rot=(0,0,1;0rad)
  Radius = 74
FEATURE [Part::Cut] Cut575
  Base = -> Cut585
  Tool = -> Cylinder1822
FEATURE [Part::Cylinder] Cylinder1823  label="Válec1823"
  Angle = 360
  AttacherType = Attacher::AttachEngine3D
  Height = 60
  Placement = pos=(0,0,26) rot=(0,0,1;0rad)
  Radius = 74
FEATURE [Part::Cut] Cut579
  Base = -> Cut578
  Tool = -> Cylinder1823
FEATURE [Part::Box] Box783  label="Krychle783"
  AttacherType = Attacher::AttachEngine3D
  Height = 49
  Length = 10
  Placement = pos=(-79,-24,29) rot=(0,0,1;0rad)
  Width = 56
FEATURE [Part::Cylinder] Cylinder1824  label="Válec1824"
  Angle = 360
  AttacherType = Attacher::AttachEngine3D
  Height = 40
  Placement = pos=(-86,-10,39) rot=(0,1,0;1.5708rad)
  Radius = 2.5
FEATURE [Part::Cylinder] Cylinder1825  label="Válec1825"
  Angle = 360
  AttacherType = Attacher::AttachEngine3D
  Height = 40
  Placement = pos=(-86,20,39) rot=(0,1,0;1.5708rad)
  Radius = 2.5
FEATURE [Part::Compound] Compound923
  Links = -> [Cut579,Cut575]
FEATURE [Part::Compound] Compound924
  Links = -> [Box770,Box772,Box774,Box773]
FEATURE [Part::Cut] Cut584
  Base = -> Cut582
  Tool = -> Compound924
FEATURE [Part::Compound] Compound925
  Links = -> [Cylinder1824,Cylinder1825,Cylinder1821]
FEATURE [Part::Compound] Compound926
  Links = -> [Cylinder1814,Cylinder1813,Cylinder1811,Cylinder1812]
FEATURE [Part::Cut] Cut573
  Base = -> Cut584
  Tool = -> Compound926
FEATURE [Part::Cut] Cut574
  Base = -> Cut573
  Tool = -> Cylinder1816
FEATURE [Part::Cut] Cut580
  Base = -> Cut574
  Tool = -> Cylinder1815
FEATURE [Part::Chamfer] Chamfer067
  Base = -> Cut580
  Edges = 1 edges r=2: [Edge4]
  Placement = pos=(0,0,2) rot=(0,0,1;0rad)
FEATURE [Part::Compound] Compound927
  Links = -> [Cylinder1819,Cylinder1818]
  Placement = pos=(-8,0,0) rot=(0,0,1;0rad)
FEATURE [Part::Cut] Cut572
  Base = -> Cut571
  Placement = pos=(0,0,2) rot=(0,0,1;0rad)
  Tool = -> Compound927
FEATURE [Part::Chamfer] Chamfer066
  Base = -> Cut572
  Edges = 1 edges r=20: [Edge3]
FEATURE [Part::Cut] Cut581
  Base = -> Chamfer066
  Tool = -> Box777
FEATURE [Part::Chamfer] Chamfer068
  Base = -> Box783
  Edges = 1 edges r=3: [Edge3]
FEATURE [Part::Cut] Cut576
  Base = -> Chamfer068
  Tool = -> Compound925
FEATURE [Part::Cut] Cut577
  Base = -> Cut576
  Tool = -> Cylinder1820
FEATURE [Part::Cut] Cut583
  Base = -> Cut577
  Tool = -> Box778
FEATURE [Part::Compound] Compound922  label="Base_side-balancer-wide001"
  Links = -> [Compound923,Cut583,Chamfer067,Cut581]
FEATURE [Part::Mirroring] mirror005  label="Base_balancer-balancer-wide-opposite-old"
  Base = (0,0,0)
  Normal = (1,0,0)
  Source = -> Compound922
FEATURE [Part::Box] Box784  label="Krychle784"
  AttacherType = Attacher::AttachEngine3D
  Height = 20
  Length = 200
  Placement = pos=(21.5,-120,84) rot=(0,0,1;1.5708rad)
  Width = 20
FEATURE [Part::Box] Box785  label="Krychle785"
  AttacherType = Attacher::AttachEngine3D
  Height = 6
  Length = 72
  Placement = pos=(26,-130,78) rot=(0,0,1;1.5708rad)
  Width = 52
FEATURE [Part::Box] Box786  label="Krychle786"
  AttacherType = Attacher::AttachEngine3D
  Height = 20
  Length = 80
  Placement = pos=(-138.7,-24,54.35) rot=(0,1,0;0.349066rad)
  Width = 6
FEATURE [Part::Box] Box787  label="Krychle787"
  AttacherType = Attacher::AttachEngine3D
  Height = 49
  Length = 44
  Placement = pos=(-93,-24,29) rot=(0,0,1;0rad)
  Width = 6
FEATURE [Part::Box] Box788  label="Krychle788"
  AttacherType = Attacher::AttachEngine3D
  Height = 32
  Length = 57
  Placement = pos=(-130,-24,52) rot=(0,0,1;0rad)
  Width = 6
FEATURE [Part::Cut] Cut586
  Base = -> Box788
  Placement = pos=(2,0,0) rot=(0,0,1;1.5708rad)
  Tool = -> Box786
FEATURE [Part::Box] Box789  label="Krychle789"
  AttacherType = Attacher::AttachEngine3D
  Height = 20
  Length = 80
  Placement = pos=(-118.17,-24,82.63) rot=(0,1,0;1.24616rad)
  Width = 6
FEATURE [Part::Cut] Cut587
  Base = -> Box787
  Placement = pos=(2,0,0) rot=(0,0,1;1.5708rad)
  Tool = -> Box789
FEATURE [Part::Box] Box790  label="Krychle790"
  AttacherType = Attacher::AttachEngine3D
  Height = 20
  Length = 80
  Placement = pos=(-118.17,-24,82.63) rot=(0,1,0;1.24616rad)
  Width = 6
FEATURE [Part::Box] Box791  label="Krychle791"
  AttacherType = Attacher::AttachEngine3D
  Height = 32
  Length = 57
  Placement = pos=(-130,-24,52) rot=(0,0,1;0rad)
  Width = 6
FEATURE [Part::Box] Box792  label="Krychle792"
  AttacherType = Attacher::AttachEngine3D
  Height = 49
  Length = 44
  Placement = pos=(-93,-24,29) rot=(0,0,1;0rad)
  Width = 6
FEATURE [Part::Box] Box793  label="Krychle793"
  AttacherType = Attacher::AttachEngine3D
  Height = 20
  Length = 80
  Placement = pos=(-138.7,-24,54.35) rot=(0,1,0;0.349066rad)
  Width = 6
FEATURE [Part::Cut] Cut588
  Base = -> Box792
  Placement = pos=(-44,0,0) rot=(0,0,1;1.5708rad)
  Tool = -> Box790
FEATURE [Part::Cut] Cut589
  Base = -> Box791
  Placement = pos=(-44,0,0) rot=(0,0,1;1.5708rad)
  Tool = -> Box793
FEATURE [Part::Box] Box794  label="Krychle794"
  AttacherType = Attacher::AttachEngine3D
  Height = 32
  Length = 57
  Placement = pos=(-130,-24,52) rot=(0,0,1;0rad)
  Width = 6
FEATURE [Part::Box] Box795  label="Krychle795"
  AttacherType = Attacher::AttachEngine3D
  Height = 20
  Length = 80
  Placement = pos=(-118.17,-24,82.63) rot=(0,1,0;1.24616rad)
  Width = 6
FEATURE [Part::Box] Box796  label="Krychle796"
  AttacherType = Attacher::AttachEngine3D
  Height = 49
  Length = 44
  Placement = pos=(-93,-24,29) rot=(0,0,1;0rad)
  Width = 6
FEATURE [Part::Box] Box797  label="Krychle797"
  AttacherType = Attacher::AttachEngine3D
  Height = 20
  Length = 80
  Placement = pos=(-138.7,-24,54.35) rot=(0,1,0;0.349066rad)
  Width = 6
FEATURE [Part::Cut] Cut590
  Base = -> Box796
  Placement = pos=(-21,0,0) rot=(0,0,1;1.5708rad)
  Tool = -> Box795
FEATURE [Part::Cut] Cut591
  Base = -> Box794
  Placement = pos=(-21,0,0) rot=(0,0,1;1.5708rad)
  Tool = -> Box797
FEATURE [Part::Cylinder] Cylinder1826  label="Válec1826"
  Angle = 360
  AttacherType = Attacher::AttachEngine3D
  Height = 64
  Placement = pos=(0,0,25) rot=(0,0,1;0rad)
  Radius = 74
FEATURE [Part::Compound] Compound928
  Links = -> [Cut591,Cut589,Cut586]
FEATURE [Part::Compound] Compound929
  Links = -> [Cut587,Cut588,Cut590]
FEATURE [Part::Cylinder] Cylinder1827  label="Válec1827"
  Angle = 360
  AttacherType = Attacher::AttachEngine3D
  Height = 64
  Placement = pos=(0,0,25) rot=(0,0,1;0rad)
  Radius = 74
FEATURE [Part::Cut] Cut592
  Base = -> Compound928
  Tool = -> Cylinder1826
FEATURE [Part::Cut] Cut593
  Base = -> Compound929
  Tool = -> Cylinder1827
FEATURE [Part::Cylinder] Cylinder1828  label="Válec1828"
  Angle = 360
  AttacherType = Attacher::AttachEngine3D
  Height = 20
  Placement = pos=(-90,-10,66) rot=(0,0,1;0rad)
  Radius = 2.5
FEATURE [Part::Cylinder] Cylinder1829  label="Válec1829"
  Angle = 360
  AttacherType = Attacher::AttachEngine3D
  Height = 20
  Placement = pos=(-110,-10,66) rot=(0,0,1;0rad)
  Radius = 2.5
FEATURE [Part::Compound] Compound930
  Links = -> [Cylinder1829,Cylinder1828]
  Placement = pos=(1.5,-8,0) rot=(0,0,1;1.5708rad)
FEATURE [Part::Cylinder] Cylinder1830  label="Válec1830"
  Angle = 360
  AttacherType = Attacher::AttachEngine3D
  Height = 20
  Placement = pos=(-110,-10,66) rot=(0,0,1;0rad)
  Radius = 2.5
FEATURE [Part::Cylinder] Cylinder1831  label="Válec1831"
  Angle = 360
  AttacherType = Attacher::AttachEngine3D
  Height = 20
  Placement = pos=(-90,-10,66) rot=(0,0,1;0rad)
  Radius = 2.5
FEATURE [Part::Compound] Compound931
  Links = -> [Cylinder1830,Cylinder1831]
  Placement = pos=(-21.5,-8,0) rot=(0,0,1;1.5708rad)
FEATURE [Part::Compound] Compound932
  Links = -> [Compound930,Compound931]
FEATURE [Part::Cut] Cut594
  Base = -> Box785
  Tool = -> Compound932
FEATURE [Part::Cylinder] Cylinder1832  label="Válec1832"
  Angle = 360
  AttacherType = Attacher::AttachEngine3D
  Height = 40
  Placement = pos=(-86,-10,69) rot=(0,1,0;1.5708rad)
  Radius = 2.5
FEATURE [Part::Cylinder] Cylinder1833  label="Válec1833"
  Angle = 360
  AttacherType = Attacher::AttachEngine3D
  Height = 40
  Placement = pos=(-86,-10,39) rot=(0,1,0;1.5708rad)
  Radius = 2.5
FEATURE [Part::Compound] Compound933
  Links = -> [Cylinder1833,Cylinder1832]
  Placement = pos=(1.5,0,0) rot=(0,0,1;1.5708rad)
FEATURE [Part::Cylinder] Cylinder1834  label="Válec1834"
  Angle = 360
  AttacherType = Attacher::AttachEngine3D
  Height = 40
  Placement = pos=(-86,-10,69) rot=(0,1,0;1.5708rad)
  Radius = 2.5
FEATURE [Part::Cylinder] Cylinder1835  label="Válec1835"
  Angle = 360
  AttacherType = Attacher::AttachEngine3D
  Height = 40
  Placement = pos=(-86,-10,39) rot=(0,1,0;1.5708rad)
  Radius = 2.5
FEATURE [Part::Compound] Compound934
  Links = -> [Cylinder1835,Cylinder1834]
  Placement = pos=(-21.5,0,0) rot=(0,0,1;1.5708rad)
FEATURE [Part::Box] Box798  label="Krychle798"
  AttacherType = Attacher::AttachEngine3D
  Height = 8
  Length = 8
  Placement = pos=(-48,-14,65) rot=(0,0,1;1.5708rad)
  Width = 20
FEATURE [Part::Box] Box799  label="Krychle799"
  AttacherType = Attacher::AttachEngine3D
  Height = 8
  Length = 8
  Placement = pos=(-48,-14,35) rot=(0,0,1;1.5708rad)
  Width = 20
FEATURE [Part::Compound] Compound935
  Links = -> [Box799,Box798]
  Placement = pos=(1.5,0,0) rot=(0,0,1;1.5708rad)
FEATURE [Part::Box] Box801  label="Krychle801"
  AttacherType = Attacher::AttachEngine3D
  Height = 8
  Length = 8
  Placement = pos=(-68,-14,65) rot=(0,0,1;1.5708rad)
  Width = 2.5
FEATURE [Part::Box] Box803  label="Krychle803"
  AttacherType = Attacher::AttachEngine3D
  Height = 8
  Length = 8
  Placement = pos=(-68,-14,35) rot=(0,0,1;1.5708rad)
  Width = 2.5
FEATURE [Part::Compound] Compound936
  Links = -> [Box803,Box801]
  Placement = pos=(1.5,0,0) rot=(0,0,1;1.5708rad)
FEATURE [Part::Box] Box804  label="Krychle804"
  AttacherType = Attacher::AttachEngine3D
  Height = 8
  Length = 8
  Placement = pos=(-48,-14,35) rot=(0,0,1;1.5708rad)
  Width = 20
FEATURE [Part::Box] Box805  label="Krychle805"
  AttacherType = Attacher::AttachEngine3D
  Height = 8
  Length = 8
  Placement = pos=(-48,-14,65) rot=(0,0,1;1.5708rad)
  Width = 20
FEATURE [Part::Compound] Compound937
  Links = -> [Box804,Box805]
  Placement = pos=(-21.5,0,0) rot=(0,0,1;1.5708rad)
FEATURE [Part::Box] Box806  label="Krychle806"
  AttacherType = Attacher::AttachEngine3D
  Height = 8
  Length = 8
  Placement = pos=(-68,-14,65) rot=(0,0,1;1.5708rad)
  Width = 2.5
FEATURE [Part::Box] Box807  label="Krychle807"
  AttacherType = Attacher::AttachEngine3D
  Height = 8
  Length = 8
  Placement = pos=(-68,-14,35) rot=(0,0,1;1.5708rad)
  Width = 2.5
FEATURE [Part::Compound] Compound938
  Links = -> [Box807,Box806]
  Placement = pos=(-21.5,0,0) rot=(0,0,1;1.5708rad)
FEATURE [Part::Compound] Compound939
  Links = -> [Compound933,Compound934]
FEATURE [Part::Compound] Compound940
  Links = -> [Compound937,Compound935]
FEATURE [Part::Compound] Compound941
  Links = -> [Compound938,Compound936]
FEATURE [Part::Cut] Cut595
  Base = -> Cut450
  Tool = -> Compound939
FEATURE [Part::Box] Box808  label="Krychle808"
  AttacherType = Attacher::AttachEngine3D
  Height = 8
  Length = 8
  Placement = pos=(-68,-14,65) rot=(0,0,1;1.5708rad)
  Width = 2.5
FEATURE [Part::Box] Box809  label="Krychle809"
  AttacherType = Attacher::AttachEngine3D
  Height = 8
  Length = 8
  Placement = pos=(-48,-14,65) rot=(0,0,1;1.5708rad)
  Width = 20
FEATURE [Part::Box] Box810  label="Krychle810"
  AttacherType = Attacher::AttachEngine3D
  Height = 8
  Length = 8
  Placement = pos=(-68,16,35) rot=(0,0,1;1.5708rad)
  Width = 2.5
FEATURE [Part::Box] Box811  label="Krychle811"
  AttacherType = Attacher::AttachEngine3D
  Height = 8
  Length = 8
  Placement = pos=(-68,-14,35) rot=(0,0,1;1.5708rad)
  Width = 2.5
FEATURE [Part::Compound] Compound942
  Links = -> [Box811,Box810,Box808]
FEATURE [Part::Box] Box812  label="Krychle812"
  AttacherType = Attacher::AttachEngine3D
  Height = 8
  Length = 8
  Placement = pos=(-48,-14,35) rot=(0,0,1;1.5708rad)
  Width = 20
FEATURE [Part::Box] Box813  label="Krychle813"
  AttacherType = Attacher::AttachEngine3D
  Height = 8
  Length = 8
  Placement = pos=(-48,16,35) rot=(0,0,1;1.5708rad)
  Width = 20
FEATURE [Part::Compound] Compound943
  Links = -> [Box812,Box813,Box809]
FEATURE [Part::Mirroring] mirror006  label="Compound942 (mirrored)"
  Base = (0,0,0)
  Normal = (1,0,0)
  Source = -> Compound942
FEATURE [Part::Mirroring] mirror007  label="Compound943 (mirrored)"
  Base = (3.8147e-06,5,54)
  Normal = (1,0,-1.19209e-07)
  Source = -> Compound943
FEATURE [Part::Cylinder] Cylinder1836  label="Válec1836"
  Angle = 360
  AttacherType = Attacher::AttachEngine3D
  Height = 5
  Placement = pos=(-86,-10,69) rot=(0,1,0;1.5708rad)
  Radius = 5
FEATURE [Part::Cylinder] Cylinder1837  label="Válec1837"
  Angle = 360
  AttacherType = Attacher::AttachEngine3D
  Height = 5
  Placement = pos=(-86,-10,69) rot=(0,1,0;1.5708rad)
  Radius = 5
FEATURE [Part::Cylinder] Cylinder1838  label="Válec1838"
  Angle = 360
  AttacherType = Attacher::AttachEngine3D
  Height = 5
  Placement = pos=(-86,-10,39) rot=(0,1,0;1.5708rad)
  Radius = 5
FEATURE [Part::Compound] Compound944
  Links = -> [Cylinder1838,Cylinder1837]
  Placement = pos=(1.5,0,0) rot=(0,0,1;1.5708rad)
FEATURE [Part::Cylinder] Cylinder1839  label="Válec1839"
  Angle = 360
  AttacherType = Attacher::AttachEngine3D
  Height = 5
  Placement = pos=(-86,-10,39) rot=(0,1,0;1.5708rad)
  Radius = 5
FEATURE [Part::Compound] Compound945
  Links = -> [Cylinder1839,Cylinder1836]
  Placement = pos=(-21.5,0,0) rot=(0,0,1;1.5708rad)
FEATURE [Part::Compound] Compound946
  Links = -> [Compound944,Compound945]
  Placement = pos=(0,5,0) rot=(0,0,1;0rad)
FEATURE [Part::Cut] Cut596
  Base = -> Cut595
  Tool = -> Compound946
FEATURE [Part::Cylinder] Cylinder1840  label="Válec1840"
  Angle = 360
  AttacherType = Attacher::AttachEngine3D
  Height = 64
  Placement = pos=(0,0,25) rot=(0,0,1;0rad)
  Radius = 74
FEATURE [Part::Cut] Cut597
  Base = -> Cut594
  Tool = -> Cylinder1840
FEATURE [Part::Cylinder] Cylinder1848  label="Válec1848"
  Angle = 360
  AttacherType = Attacher::AttachEngine3D
  Height = 40
  Placement = pos=(-86,20,39) rot=(0,1,0;1.5708rad)
  Radius = 2.5
FEATURE [Part::Cylinder] Cylinder1845  label="Válec1845"
  Angle = 360
  AttacherType = Attacher::AttachEngine3D
  Height = 40
  Placement = pos=(-86,-10,39) rot=(0,1,0;1.5708rad)
  Radius = 2.5
FEATURE [Part::Cylinder] Cylinder1847  label="Válec1847"
  Angle = 360
  AttacherType = Attacher::AttachEngine3D
  Height = 40
  Placement = pos=(-86,-10,39) rot=(0,1,0;1.5708rad)
  Radius = 2.5
FEATURE [Part::Cylinder] Cylinder1844  label="Válec1844"
  Angle = 360
  AttacherType = Attacher::AttachEngine3D
  Height = 40
  Placement = pos=(-86,-10,69) rot=(0,1,0;1.5708rad)
  Radius = 2.5
FEATURE [Part::Cylinder] Cylinder1842  label="Válec1842"
  Angle = 360
  AttacherType = Attacher::AttachEngine3D
  Height = 40
  Placement = pos=(-86,20,39) rot=(0,1,0;1.5708rad)
  Radius = 2.5
FEATURE [Part::Cylinder] Cylinder1841  label="Válec1841"
  Angle = 360
  AttacherType = Attacher::AttachEngine3D
  Height = 40
  Placement = pos=(-86,-10,39) rot=(0,1,0;1.5708rad)
  Radius = 2.5
FEATURE [Part::Compound] Compound950
  Links = -> [Cylinder1841,Cylinder1844]
  Placement = pos=(-21.5,0,0) rot=(0,0,1;1.5708rad)
FEATURE [Part::Cylinder] Cylinder1843  label="Válec1843"
  Angle = 360
  AttacherType = Attacher::AttachEngine3D
  Height = 40
  Placement = pos=(-86,-10,69) rot=(0,1,0;1.5708rad)
  Radius = 2.5
FEATURE [Part::Compound] Compound949
  Links = -> [Cylinder1845,Cylinder1843]
  Placement = pos=(1.5,0,0) rot=(0,0,1;1.5708rad)
FEATURE [Part::Cylinder] Cylinder1849  label="Válec1849"
  Angle = 360
  AttacherType = Attacher::AttachEngine3D
  Height = 40
  Placement = pos=(-86,-10,39) rot=(0,1,0;1.5708rad)
  Radius = 2.5
FEATURE [Part::Cylinder] Cylinder1850  label="Válec1850"
  Angle = 360
  AttacherType = Attacher::AttachEngine3D
  Height = 40
  Placement = pos=(-86,-10,69) rot=(0,1,0;1.5708rad)
  Radius = 2.5
FEATURE [Part::Cylinder] Cylinder1851  label="Válec1851"
  Angle = 360
  AttacherType = Attacher::AttachEngine3D
  Height = 40
  Placement = pos=(-86,-10,39) rot=(0,1,0;1.5708rad)
  Radius = 2.5
FEATURE [Part::Cylinder] Cylinder1852  label="Válec1852"
  Angle = 360
  AttacherType = Attacher::AttachEngine3D
  Height = 40
  Placement = pos=(-86,-10,69) rot=(0,1,0;1.5708rad)
  Radius = 2.5
FEATURE [Part::Cylinder] Cylinder1853  label="Válec1853"
  Angle = 360
  AttacherType = Attacher::AttachEngine3D
  Height = 40
  Placement = pos=(-86,-10,39) rot=(0,1,0;1.5708rad)
  Radius = 2.5
FEATURE [Part::Cylinder] Cylinder1854  label="Válec1854"
  Angle = 360
  AttacherType = Attacher::AttachEngine3D
  Height = 40
  Placement = pos=(-86,20,39) rot=(0,1,0;1.5708rad)
  Radius = 2.5
FEATURE [Part::Compound] Compound951
  Links = -> [Cylinder1849,Cylinder1854,Cylinder1852]
FEATURE [Part::Cylinder] Cylinder1855  label="Válec1855"
  Angle = 360
  AttacherType = Attacher::AttachEngine3D
  Height = 40
  Placement = pos=(-86,-10,69) rot=(0,1,0;1.5708rad)
  Radius = 2.5
FEATURE [Part::Cylinder] Cylinder1856  label="Válec1856"
  Angle = 360
  AttacherType = Attacher::AttachEngine3D
  Height = 40
  Placement = pos=(-86,-10,69) rot=(0,1,0;1.5708rad)
  Radius = 2.5
FEATURE [Part::Cylinder] Cylinder1846  label="Válec1846"
  Angle = 360
  AttacherType = Attacher::AttachEngine3D
  Height = 40
  Placement = pos=(-86,-10,69) rot=(0,1,0;1.5708rad)
  Radius = 2.5
FEATURE [Part::Cylinder] Cylinder1857  label="Válec1857"
  Angle = 360
  AttacherType = Attacher::AttachEngine3D
  Height = 40
  Placement = pos=(-86,-10,39) rot=(0,1,0;1.5708rad)
  Radius = 2.5
FEATURE [Part::Cylinder] Cylinder1858  label="Válec1858"
  Angle = 360
  AttacherType = Attacher::AttachEngine3D
  Height = 50
  Placement = pos=(71,80,56) rot=(1,0,0;1.5708rad)
  Radius = 1.5
FEATURE [Part::Cylinder] Cylinder1859  label="Válec1859"
  Angle = 360
  AttacherType = Attacher::AttachEngine3D
  Height = 50
  Placement = pos=(-71,80,73) rot=(1,0,0;1.5708rad)
  Radius = 1.5
FEATURE [Part::Box] Box814  label="Krychle814"
  AttacherType = Attacher::AttachEngine3D
  Height = 6
  Length = 8
  Placement = pos=(67,38,36) rot=(0,0,1;0rad)
  Width = 2
FEATURE [Part::Box] Box815  label="Krychle815"
  AttacherType = Attacher::AttachEngine3D
  Height = 55
  Length = 148
  Placement = pos=(-74,48,29) rot=(0,0,1;0rad)
  Width = 26
FEATURE [Part::Box] Box816  label="Krychle816"
  AttacherType = Attacher::AttachEngine3D
  Height = 6
  Length = 8
  Placement = pos=(-75,38,36) rot=(0,0,1;0rad)
  Width = 2
FEATURE [Part::Cylinder] Cylinder1860  label="Válec1860"
  Angle = 360
  AttacherType = Attacher::AttachEngine3D
  Height = 51
  Placement = pos=(0,0,29) rot=(0,0,1;0rad)
  Radius = 74
FEATURE [Part::Cylinder] Cylinder1861  label="Válec1861"
  Angle = 360
  AttacherType = Attacher::AttachEngine3D
  Height = 50
  Placement = pos=(-71,80,56) rot=(1,0,0;1.5708rad)
  Radius = 1.5
FEATURE [Part::Box] Box817  label="Krychle817"
  AttacherType = Attacher::AttachEngine3D
  Height = 55
  Length = 148
  Placement = pos=(-74,0,29) rot=(0,0,1;0rad)
  Width = 74
FEATURE [Part::Cylinder] Cylinder1862  label="Válec1862"
  Angle = 360
  AttacherType = Attacher::AttachEngine3D
  Height = 50
  Placement = pos=(71,80,39) rot=(1,0,0;1.5708rad)
  Radius = 1.5
FEATURE [Part::Cylinder] Cylinder1863  label="Válec1863"
  Angle = 360
  AttacherType = Attacher::AttachEngine3D
  Height = 50
  Placement = pos=(71,80,73) rot=(1,0,0;1.5708rad)
  Radius = 1.5
FEATURE [Part::Box] Box818  label="Krychle818"
  AttacherType = Attacher::AttachEngine3D
  Height = 34
  Length = 148
  Placement = pos=(-74,68,38) rot=(0,0,1;0rad)
  Width = 20
FEATURE [Part::Cylinder] Cylinder1864  label="Válec1864"
  Angle = 360
  AttacherType = Attacher::AttachEngine3D
  Height = 6
  Placement = pos=(0,0,65) rot=(0,0,1;0rad)
  Radius = 74
FEATURE [Part::Box] Box819  label="Krychle819"
  AttacherType = Attacher::AttachEngine3D
  Height = 8
  Length = 8
  Placement = pos=(-48,16,35) rot=(0,0,1;1.5708rad)
  Width = 20
FEATURE [Part::Box] Box820  label="Krychle820"
  AttacherType = Attacher::AttachEngine3D
  Height = 8
  Length = 8
  Placement = pos=(-48,-14,35) rot=(0,0,1;1.5708rad)
  Width = 20
FEATURE [Part::Cylinder] Cylinder1865  label="Válec1865"
  Angle = 360
  AttacherType = Attacher::AttachEngine3D
  Height = 50
  Placement = pos=(-71,80,39) rot=(1,0,0;1.5708rad)
  Radius = 1.5
FEATURE [Part::Box] Box821  label="Krychle821"
  AttacherType = Attacher::AttachEngine3D
  Height = 8
  Length = 8
  Placement = pos=(-68,-14,35) rot=(0,0,1;1.5708rad)
  Width = 2.5
FEATURE [Part::Box] Box822  label="Krychle822"
  AttacherType = Attacher::AttachEngine3D
  Height = 8
  Length = 8
  Placement = pos=(-68,16,35) rot=(0,0,1;1.5708rad)
  Width = 2.5
FEATURE [Part::Box] Box823  label="Krychle823"
  AttacherType = Attacher::AttachEngine3D
  Height = 8
  Length = 8
  Placement = pos=(-48,-14,65) rot=(0,0,1;1.5708rad)
  Width = 20
FEATURE [Part::Box] Box824  label="Krychle824"
  AttacherType = Attacher::AttachEngine3D
  Height = 8
  Length = 8
  Placement = pos=(-68,-14,65) rot=(0,0,1;1.5708rad)
  Width = 2.5
FEATURE [Part::Box] Box825  label="Krychle825"
  AttacherType = Attacher::AttachEngine3D
  Height = 6
  Length = 8
  Placement = pos=(67,38,70) rot=(0,0,1;0rad)
  Width = 2
FEATURE [Part::Cut] Cut603
  Base = -> Cylinder1864
  Placement = pos=(0,0,13) rot=(0,0,1;0rad)
  Tool = -> Box818
FEATURE [Part::Compound] Compound967
  Links = -> [Box821,Box822,Box824]
FEATURE [Part::Compound] Compound969
  Links = -> [Cylinder1859,Cylinder1862,Cylinder1865,Cylinder1863,Cylinder1861,Cylinder1858]
FEATURE [Part::Compound] Compound972
  Links = -> [Box820,Box819,Box823]
FEATURE [Part::Compound] Compound974
  Links = -> [Cylinder1851,Cylinder1842,Cylinder1850]
FEATURE [Part::Mirroring] mirror008  label="Compound944 (mirrored)001"
  Base = (0,0,0)
  Normal = (1,0,0)
  Source = -> Compound974
FEATURE [Part::Compound] Compound975
  Links = -> [Compound949,Compound950]
FEATURE [Part::Mirroring] mirror009  label="Compound944 (mirrored)"
  Base = (0,0,0)
  Normal = (1,0,0)
  Source = -> Compound951
FEATURE [Part::Compound] Compound947
  Links = -> [Cylinder1847,Cylinder1848,Cylinder1846]
FEATURE [Part::Compound] Compound948
  Links = -> [Compound947,Compound975,mirror008]
FEATURE [Part::Box] Box826  label="Krychle826"
  AttacherType = Attacher::AttachEngine3D
  Height = 49
  Length = 56
  Placement = pos=(-28,35,29) rot=(0,0,1;0rad)
  Width = 200
FEATURE [Part::Box] Box827  label="Krychle827"
  AttacherType = Attacher::AttachEngine3D
  Height = 55
  Length = 148
  Placement = pos=(-74,68,29) rot=(0,0,1;0rad)
  Width = 26
FEATURE [Part::Box] Box828  label="Krychle828"
  AttacherType = Attacher::AttachEngine3D
  Height = 60
  Length = 200
  Placement = pos=(0,0,-5) rot=(0,0,-1;0.383972rad)
  Width = 200
FEATURE [Part::Box] Box829  label="Krychle829"
  AttacherType = Attacher::AttachEngine3D
  Height = 60
  Length = 200
  Placement = pos=(70.7107,70.7107,-5) rot=(0,0,1;3.92699rad)
  Width = 120
FEATURE [Part::Box] Box830  label="Krychle830"
  AttacherType = Attacher::AttachEngine3D
  Height = 60
  Length = 200
  Placement = pos=(0,0,-5) rot=(0,0,1;3.52556rad)
  Width = 200
FEATURE [Part::Box] Box831  label="Krychle831"
  AttacherType = Attacher::AttachEngine3D
  Height = 2
  Length = 6
  Placement = pos=(-3,-75,39) rot=(0,0,1;0rad)
  Width = 8
FEATURE [Part::Box] Box832  label="Krychle832"
  AttacherType = Attacher::AttachEngine3D
  Height = 2
  Length = 6
  Placement = pos=(34.9,-66.45,58) rot=(0,0,1;0.523599rad)
  Width = 8
FEATURE [Part::Box] Box833  label="Krychle833"
  AttacherType = Attacher::AttachEngine3D
  Height = 2
  Length = 6
  Placement = pos=(-75,3,39) rot=(0,0,-1;1.5708rad)
  Width = 8
FEATURE [Part::Box] Box834  label="Krychle834"
  AttacherType = Attacher::AttachEngine3D
  Height = 2
  Length = 6
  Placement = pos=(40.0981,63.4519,39) rot=(0,0,1;2.61799rad)
  Width = 8
FEATURE [Part::Cut] Cut606
  Base = -> Box829
  Tool = -> Box828
FEATURE [Part::Cut] Cut607
  Base = -> Cut606
  Tool = -> Box830
FEATURE [Part::Compound] Compound994
  Links = -> [Cylinder1857,Cylinder1855]
  Placement = pos=(1.5,0,0) rot=(0,0,1;1.5708rad)
FEATURE [Part::Compound] Compound995
  Links = -> [Cylinder1853,Cylinder1856]
  Placement = pos=(-21.5,0,0) rot=(0,0,1;1.5708rad)
FEATURE [Part::Compound] Compound952
  Links = -> [Compound994,Compound995]
FEATURE [Part::FeaturePython] Tube045  # WARN: FeaturePython — macro-defined, semantics opaque (R4)
  AttacherType = Attacher::AttachEngine3D
  Height = 55
  InnerRadius = 68
  OuterRadius = 74
  Placement = pos=(0,0,29) rot=(0,0,1;0rad)
FEATURE [Part::Cut] Cut605
  Base = -> Tube045
  Tool = -> Box826
FEATURE [Part::Cut] Cut604
  Base = -> Cut605
  Tool = -> Box827
FEATURE [Part::Cut] Cut608
  Base = -> Cut604
  Tool = -> Cut607
FEATURE [Part::FeaturePython] Tube046  # WARN: FeaturePython — macro-defined, semantics opaque (R4)
  AttacherType = Attacher::AttachEngine3D
  Height = 8
  InnerRadius = 50.1
  OuterRadius = 58
  Placement = pos=(0,0,72) rot=(0,0,1;0rad)
FEATURE [Part::Box] Box835  label="Krychle835"
  AttacherType = Attacher::AttachEngine3D
  Height = 2
  Length = 6
  Placement = pos=(75,-3,39) rot=(0,0,1;1.5708rad)
  Width = 8
FEATURE [Part::Box] Box836  label="Krychle836"
  AttacherType = Attacher::AttachEngine3D
  Height = 2
  Length = 6
  Placement = pos=(-34.9019,66.4519,39) rot=(0,0,1;3.66519rad)
  Width = 8
FEATURE [Part::Box] Box837  label="Krychle837"
  AttacherType = Attacher::AttachEngine3D
  Height = 2
  Length = 6
  Placement = pos=(63.45,-40.1,58) rot=(0,0,1;1.0472rad)
  Width = 8
FEATURE [Part::Box] Box838  label="Krychle838"
  AttacherType = Attacher::AttachEngine3D
  Height = 2
  Length = 6
  Placement = pos=(3,75,39) rot=(0,0,1;3.14159rad)
  Width = 8
FEATURE [Part::Box] Box839  label="Krychle839"
  AttacherType = Attacher::AttachEngine3D
  Height = 2
  Length = 6
  Placement = pos=(-66.4519,-34.9019,39) rot=(0,0,-1;1.0472rad)
  Width = 8
FEATURE [Part::Box] Box840  label="Krychle840"
  AttacherType = Attacher::AttachEngine3D
  Height = 2
  Length = 6
  Placement = pos=(66.4519,34.9019,39) rot=(0,0,1;2.0944rad)
  Width = 8
FEATURE [Part::Box] Box841  label="Krychle841"
  AttacherType = Attacher::AttachEngine3D
  Height = 2
  Length = 6
  Placement = pos=(-40.0981,-63.4519,39) rot=(0,0,-1;0.523599rad)
  Width = 8
FEATURE [Part::Box] Box842  label="Krychle842"
  AttacherType = Attacher::AttachEngine3D
  Height = 2
  Length = 6
  Placement = pos=(-63.4519,40.0981,39) rot=(0,0,1;4.18879rad)
  Width = 8
FEATURE [Part::Compound] Compound976
  Links = -> [Box831,Box832,Box837,Box835,Box840,Box834,Box838,Box836,Box842,Box833,Box839,Box841]
FEATURE [Part::Cut] Cut609
  Base = -> Cut608
  Tool = -> Compound976
FEATURE [Part::Cylinder] Cylinder1866  label="Válec1866"
  Angle = 360
  AttacherType = Attacher::AttachEngine3D
  Height = 72
  Placement = pos=(71,-1.8e-14,0) rot=(0,0,1;1.5708rad)
  Radius = 1.5
FEATURE [Part::Cylinder] Cylinder1867  label="Válec1867"
  Angle = 360
  AttacherType = Attacher::AttachEngine3D
  Height = 72
  Placement = pos=(35.5,61.4878,0) rot=(0,0,1;2.61799rad)
  Radius = 1.5
FEATURE [Part::Cylinder] Cylinder1868  label="Válec1868"
  Angle = 360
  AttacherType = Attacher::AttachEngine3D
  Height = 72
  Placement = pos=(61.4878,-35.5,0) rot=(0,0,1;1.0472rad)
  Radius = 1.5
FEATURE [Part::Cylinder] Cylinder1869  label="Válec1869"
  Angle = 360
  AttacherType = Attacher::AttachEngine3D
  Height = 72
  Placement = pos=(35.5,-61.4878,0) rot=(0,0,1;0.523599rad)
  Radius = 1.5
FEATURE [Part::Cylinder] Cylinder1870  label="Válec1870"
  Angle = 360
  AttacherType = Attacher::AttachEngine3D
  Height = 72
  Placement = pos=(-35.5,-61.4878,0) rot=(0,0,-1;0.523599rad)
  Radius = 1.5
FEATURE [Part::Cylinder] Cylinder1871  label="Válec1871"
  Angle = 360
  AttacherType = Attacher::AttachEngine3D
  Height = 72
  Placement = pos=(-71,2.7e-14,0) rot=(0,0,-1;1.5708rad)
  Radius = 1.5
FEATURE [Part::Cylinder] Cylinder1872  label="Válec1872"
  Angle = 360
  AttacherType = Attacher::AttachEngine3D
  Height = 72
  Placement = pos=(-61.4878,-35.5,0) rot=(0,0,-1;1.0472rad)
  Radius = 1.5
FEATURE [Part::Cylinder] Cylinder1873  label="Válec1873"
  Angle = 360
  AttacherType = Attacher::AttachEngine3D
  Height = 72
  Placement = pos=(61.4878,35.5,0) rot=(0,0,1;2.0944rad)
  Radius = 1.5
FEATURE [Part::Cylinder] Cylinder1874  label="Válec1874"
  Angle = 360
  AttacherType = Attacher::AttachEngine3D
  Height = 72
  Placement = pos=(0,-71,0) rot=(0,0,1;0rad)
  Radius = 1.5
FEATURE [Part::Cylinder] Cylinder1875  label="Válec1875"
  Angle = 360
  AttacherType = Attacher::AttachEngine3D
  Height = 72
  Placement = pos=(-35.5,61.4878,0) rot=(0,0,1;3.66519rad)
  Radius = 1.5
FEATURE [Part::Cylinder] Cylinder1876  label="Válec1876"
  Angle = 360
  AttacherType = Attacher::AttachEngine3D
  Height = 72
  Placement = pos=(-61.4878,35.5,0) rot=(0,0,1;4.18879rad)
  Radius = 1.5
FEATURE [Part::Cylinder] Cylinder1877  label="Válec1877"
  Angle = 360
  AttacherType = Attacher::AttachEngine3D
  Height = 72
  Placement = pos=(3.1e-14,71,0) rot=(0,0,1;3.14159rad)
  Radius = 1.5
FEATURE [Part::Compound] Compound977
  Links = -> [Cylinder1874,Cylinder1869,Cylinder1868,Cylinder1866,Cylinder1873,Cylinder1867,Cylinder1877,Cylinder1875,Cylinder1876,Cylinder1871,Cylinder1872,Cylinder1870]
  Placement = pos=(0,0,-4) rot=(0,0,1;0rad)
FEATURE [Part::Cut] Cut610
  Base = -> Cut609
  Tool = -> Compound977
FEATURE [Part::Cylinder] Cylinder1878  label="Válec1878"
  Angle = 360
  AttacherType = Attacher::AttachEngine3D
  Height = 50
  Placement = pos=(-18,100,72) rot=(1,0,0;1.5708rad)
  Radius = 1.5
FEATURE [Part::Compound] Compound978
  Links = -> [Cylinder1878]
  Placement = pos=(0,0,0) rot=(0,0,1;3.92699rad)
FEATURE [Part::Cylinder] Cylinder1879  label="Válec1879"
  Angle = 360
  AttacherType = Attacher::AttachEngine3D
  Height = 50
  Placement = pos=(18,100,72) rot=(1,0,0;1.5708rad)
  Radius = 1.5
FEATURE [Part::Compound] Compound979
  Links = -> [Cylinder1879]
  Placement = pos=(0,0,0) rot=(0,0,1;3.92699rad)
FEATURE [Part::Compound] Compound980
  Links = -> [Compound978,Compound979]
  Placement = pos=(0,0,1) rot=(0,0,1;0rad)
FEATURE [Part::Cut] Cut611
  Base = -> Cut610
  Tool = -> Compound980
FEATURE [Part::Box] Box843  label="Krychle843"
  AttacherType = Attacher::AttachEngine3D
  Height = 6
  Length = 6
  Placement = pos=(15,64,-50) rot=(0,0,1;0rad)
  Width = 4
FEATURE [Part::Box] Box844  label="Krychle844"
  AttacherType = Attacher::AttachEngine3D
  Height = 6
  Length = 6
  Placement = pos=(-21,64,-50) rot=(0,0,1;0rad)
  Width = 4
FEATURE [Part::Compound] Compound981
  Links = -> [Box844,Box843]
  Placement = pos=(0,0,120) rot=(0,0,1;3.92699rad)
FEATURE [Part::Cut] Cut612
  Base = -> Cut611
  Tool = -> Compound981
FEATURE [Part::Cylinder] Cylinder1880  label="Válec1880"
  Angle = 360
  AttacherType = Attacher::AttachEngine3D
  Height = 50
  Placement = pos=(-9,100,59) rot=(1,0,0;1.5708rad)
  Radius = 1.5
FEATURE [Part::Compound] Compound984
  Links = -> [Cylinder1880]
  Placement = pos=(0,0,0) rot=(0,0,1;3.92699rad)
FEATURE [Part::Cylinder] Cylinder1881  label="Válec1881"
  Angle = 360
  AttacherType = Attacher::AttachEngine3D
  Height = 50
  Placement = pos=(9,100,59) rot=(1,0,0;1.5708rad)
  Radius = 1.5
FEATURE [Part::Compound] Compound983
  Links = -> [Cylinder1881]
  Placement = pos=(0,0,0) rot=(0,0,1;3.92699rad)
FEATURE [Part::Compound] Compound982
  Links = -> [Compound984,Compound983]
  Placement = pos=(0,0,1) rot=(0,0,1;0rad)
FEATURE [Part::Box] Box845  label="Krychle845"
  AttacherType = Attacher::AttachEngine3D
  Height = 6
  Length = 6
  Placement = pos=(6,66,-63) rot=(0,0,1;0rad)
  Width = 4
FEATURE [Part::Box] Box846  label="Krychle846"
  AttacherType = Attacher::AttachEngine3D
  Height = 6
  Length = 6
  Placement = pos=(-12,66,-63) rot=(0,0,1;0rad)
  Width = 4
FEATURE [Part::Compound] Compound985
  Links = -> [Box846,Box845]
  Placement = pos=(0,0,120) rot=(0,0,1;3.92699rad)
FEATURE [Part::Box] Box847  label="Krychle847"
  AttacherType = Attacher::AttachEngine3D
  Height = 6
  Length = 8
  Placement = pos=(-75,38,70) rot=(0,0,1;0rad)
  Width = 2
FEATURE [Part::Box] Box848  label="Krychle848"
  AttacherType = Attacher::AttachEngine3D
  Height = 6
  Length = 8
  Placement = pos=(-75,38,53) rot=(0,0,1;0rad)
  Width = 2
FEATURE [Part::Box] Box849  label="Krychle849"
  AttacherType = Attacher::AttachEngine3D
  Height = 6
  Length = 8
  Placement = pos=(67,38,53) rot=(0,0,1;0rad)
  Width = 2
FEATURE [Part::Compound] Compound970
  Links = -> [Box816,Box814,Box825,Box847,Box848,Box849]
FEATURE [Part::Box] Box850  label="Krychle850"
  AttacherType = Attacher::AttachEngine3D
  Height = 2
  Length = 6
  Placement = pos=(-3,-75,39) rot=(0,0,1;0rad)
  Width = 8
FEATURE [Part::Box] Box851  label="Krychle851"
  AttacherType = Attacher::AttachEngine3D
  Height = 2
  Length = 6
  Placement = pos=(34.9019,-66.4519,39) rot=(0,0,1;0.523599rad)
  Width = 8
FEATURE [Part::Box] Box852  label="Krychle852"
  AttacherType = Attacher::AttachEngine3D
  Height = 2
  Length = 6
  Placement = pos=(63.4519,-40.0981,39) rot=(0,0,1;1.0472rad)
  Width = 8
FEATURE [Part::Box] Box853  label="Krychle853"
  AttacherType = Attacher::AttachEngine3D
  Height = 2
  Length = 6
  Placement = pos=(75,-3,39) rot=(0,0,1;1.5708rad)
  Width = 8
FEATURE [Part::Box] Box854  label="Krychle854"
  AttacherType = Attacher::AttachEngine3D
  Height = 2
  Length = 6
  Placement = pos=(66.4519,34.9019,39) rot=(0,0,1;2.0944rad)
  Width = 8
FEATURE [Part::Box] Box855  label="Krychle855"
  AttacherType = Attacher::AttachEngine3D
  Height = 2
  Length = 6
  Placement = pos=(40.0981,63.4519,39) rot=(0,0,1;2.61799rad)
  Width = 8
FEATURE [Part::Box] Box856  label="Krychle856"
  AttacherType = Attacher::AttachEngine3D
  Height = 2
  Length = 6
  Placement = pos=(3,75,39) rot=(0,0,1;3.14159rad)
  Width = 8
FEATURE [Part::Box] Box857  label="Krychle857"
  AttacherType = Attacher::AttachEngine3D
  Height = 2
  Length = 6
  Placement = pos=(-34.9019,66.4519,39) rot=(0,0,1;3.66519rad)
  Width = 8
FEATURE [Part::Box] Box858  label="Krychle858"
  AttacherType = Attacher::AttachEngine3D
  Height = 2
  Length = 6
  Placement = pos=(-63.4519,40.0981,39) rot=(0,0,1;4.18879rad)
  Width = 8
FEATURE [Part::Box] Box859  label="Krychle859"
  AttacherType = Attacher::AttachEngine3D
  Height = 2
  Length = 6
  Placement = pos=(-75,3,39) rot=(0,0,-1;1.5708rad)
  Width = 8
FEATURE [Part::Box] Box860  label="Krychle860"
  AttacherType = Attacher::AttachEngine3D
  Height = 2
  Length = 6
  Placement = pos=(-66.4519,-34.9019,39) rot=(0,0,-1;1.0472rad)
  Width = 8
FEATURE [Part::Box] Box861  label="Krychle861"
  AttacherType = Attacher::AttachEngine3D
  Height = 2
  Length = 6
  Placement = pos=(-40.0981,-63.4519,39) rot=(0,0,-1;0.523599rad)
  Width = 8
FEATURE [Part::Compound] Compound968
  Links = -> [Box850,Box851,Box852,Box853,Box854,Box855,Box856,Box857,Box858,Box859,Box860,Box861]
FEATURE [Part::Cylinder] Cylinder1882  label="Válec1882"
  Angle = 360
  AttacherType = Attacher::AttachEngine3D
  Height = 40
  Placement = pos=(-86,-10,69) rot=(0,1,0;1.5708rad)
  Radius = 2.5
FEATURE [Part::Cylinder] Cylinder1883  label="Válec1883"
  Angle = 360
  AttacherType = Attacher::AttachEngine3D
  Height = 40
  Placement = pos=(-86,-10,39) rot=(0,1,0;1.5708rad)
  Radius = 2.5
FEATURE [Part::Cylinder] Cylinder1884  label="Válec1884"
  Angle = 360
  AttacherType = Attacher::AttachEngine3D
  Height = 40
  Placement = pos=(-86,20,39) rot=(0,1,0;1.5708rad)
  Radius = 2.5
FEATURE [Part::Compound] Compound971
  Links = -> [Cylinder1883,Cylinder1884,Cylinder1882]
FEATURE [Part::Compound] Compound973
  Links = -> [Compound971,Compound952,mirror009]
FEATURE [Part::Box] Box862  label="Krychle862"
  AttacherType = Attacher::AttachEngine3D
  Height = 8
  Length = 8
  Placement = pos=(-48,-14,35) rot=(0,0,1;1.5708rad)
  Width = 20
FEATURE [Part::Box] Box863  label="Krychle863"
  AttacherType = Attacher::AttachEngine3D
  Height = 8
  Length = 8
  Placement = pos=(-68,-14,65) rot=(0,0,1;1.5708rad)
  Width = 2.5
FEATURE [Part::Box] Box864  label="Krychle864"
  AttacherType = Attacher::AttachEngine3D
  Height = 8
  Length = 8
  Placement = pos=(-48,-14,65) rot=(0,0,1;1.5708rad)
  Width = 20
FEATURE [Part::Compound] Compound988
  Links = -> [Box862,Box864]
  Placement = pos=(1.5,0,0) rot=(0,0,1;1.5708rad)
FEATURE [Part::Box] Box865  label="Krychle865"
  AttacherType = Attacher::AttachEngine3D
  Height = 8
  Length = 8
  Placement = pos=(-48,-14,65) rot=(0,0,1;1.5708rad)
  Width = 20
FEATURE [Part::Box] Box866  label="Krychle866"
  AttacherType = Attacher::AttachEngine3D
  Height = 8
  Length = 8
  Placement = pos=(-68,-14,65) rot=(0,0,1;1.5708rad)
  Width = 2.5
FEATURE [Part::Box] Box867  label="Krychle867"
  AttacherType = Attacher::AttachEngine3D
  Height = 8
  Length = 8
  Placement = pos=(-68,-14,35) rot=(0,0,1;1.5708rad)
  Width = 2.5
FEATURE [Part::Compound] Compound989
  Links = -> [Box867,Box866]
  Placement = pos=(1.5,0,0) rot=(0,0,1;1.5708rad)
FEATURE [Part::Box] Box868  label="Krychle868"
  AttacherType = Attacher::AttachEngine3D
  Height = 8
  Length = 8
  Placement = pos=(-48,-14,35) rot=(0,0,1;1.5708rad)
  Width = 20
FEATURE [Part::Box] Box869  label="Krychle869"
  AttacherType = Attacher::AttachEngine3D
  Height = 8
  Length = 8
  Placement = pos=(-48,-14,65) rot=(0,0,1;1.5708rad)
  Width = 20
FEATURE [Part::Compound] Compound990
  Links = -> [Box868,Box869]
  Placement = pos=(-21.5,0,0) rot=(0,0,1;1.5708rad)
FEATURE [Part::Compound] Compound987
  Links = -> [Compound990,Compound988]
FEATURE [Part::Box] Box870  label="Krychle870"
  AttacherType = Attacher::AttachEngine3D
  Height = 8
  Length = 8
  Placement = pos=(-68,-14,65) rot=(0,0,1;1.5708rad)
  Width = 2.5
FEATURE [Part::Box] Box871  label="Krychle871"
  AttacherType = Attacher::AttachEngine3D
  Height = 8
  Length = 8
  Placement = pos=(-68,-14,35) rot=(0,0,1;1.5708rad)
  Width = 2.5
FEATURE [Part::Compound] Compound991
  Links = -> [Box871,Box870]
  Placement = pos=(-21.5,0,0) rot=(0,0,1;1.5708rad)
FEATURE [Part::Compound] Compound986
  Links = -> [Compound991,Compound989]
FEATURE [Part::Box] Box872  label="Krychle872"
  AttacherType = Attacher::AttachEngine3D
  Height = 8
  Length = 8
  Placement = pos=(-68,16,35) rot=(0,0,1;1.5708rad)
  Width = 2.5
FEATURE [Part::Box] Box873  label="Krychle873"
  AttacherType = Attacher::AttachEngine3D
  Height = 8
  Length = 8
  Placement = pos=(-68,-14,35) rot=(0,0,1;1.5708rad)
  Width = 2.5
FEATURE [Part::Compound] Compound992
  Links = -> [Box873,Box872,Box863]
FEATURE [Part::Mirroring] mirror010  label="Compound942 (mirrored)001"
  Base = (0,0,0)
  Normal = (1,0,0)
  Source = -> Compound992
FEATURE [Part::Compound] Compound958
  Links = -> [Compound967,mirror010,Compound986]
FEATURE [Part::Box] Box874  label="Krychle874"
  AttacherType = Attacher::AttachEngine3D
  Height = 8
  Length = 8
  Placement = pos=(-48,-14,35) rot=(0,0,1;1.5708rad)
  Width = 20
FEATURE [Part::Box] Box875  label="Krychle875"
  AttacherType = Attacher::AttachEngine3D
  Height = 8
  Length = 8
  Placement = pos=(-48,16,35) rot=(0,0,1;1.5708rad)
  Width = 20
FEATURE [Part::Compound] Compound993
  Links = -> [Box874,Box875,Box865]
FEATURE [Part::Mirroring] mirror011  label="Compound943 (mirrored)001"
  Base = (0,0,0)
  Normal = (1,0,0)
  Source = -> Compound993
FEATURE [Part::Compound] Compound966
  Links = -> [Compound987,mirror011,Compound972]
FEATURE [Part::Cut] Cut613
  Base = -> Cut612
  Tool = -> Compound982
FEATURE [Part::Cut] Cut614
  Base = -> Cut613
  Tool = -> Compound985
FEATURE [Part::Cut] Cut599
  Base = -> Cut614
  Tool = -> Compound973
FEATURE [Part::Cut] Cut601
  Base = -> Cut599
  Tool = -> Compound966
FEATURE [Part::Cut] Cut602
  Base = -> Cut601
  Tool = -> Compound958
FEATURE [Part::Cut] Cut615
  Base = -> Box817
  Tool = -> Cylinder1860
FEATURE [Part::Cut] Cut616
  Base = -> Cut615
  Tool = -> Box815
FEATURE [Part::Cut] Cut617
  Base = -> Cut616
  Tool = -> Compound969
FEATURE [Part::Cut] Cut618
  Base = -> Cut617
  Tool = -> Compound970
FEATURE [Part::Cut] Cut598
  Base = -> Cut618
  Tool = -> Compound968
FEATURE [Part::Cut] Cut600
  Base = -> Cut598
  Tool = -> Compound948
FEATURE [Part::Compound] Compound996  label="Base_balancer-front"
  Links = -> [Cut597,Cut596,Cut593,Cut592]
FEATURE [Part::Cylinder] Cylinder1885  label="Válec1885"
  Angle = 360
  AttacherType = Attacher::AttachEngine3D
  Height = 40
  Placement = pos=(-86,16,68) rot=(0,1,0;1.5708rad)
  Radius = 2.5
FEATURE [Part::Compound] Compound919
  Links = -> [Cylinder1809,Cylinder1810,Cylinder1806,Cylinder1885]
FEATURE [Part::Cut] Cut556
  Base = -> Chamfer065
  Tool = -> Compound919
FEATURE [Part::Cut] Cut557
  Base = -> Cut556
  Tool = -> Cylinder1805
FEATURE [Part::Cut] Cut568
  Base = -> Cut557
  Tool = -> Box764
FEATURE [Part::Cylinder] Cylinder1886  label="Válec1886"
  Angle = 360
  AttacherType = Attacher::AttachEngine3D
  Height = 40
  Placement = pos=(-90,16,68) rot=(0,1,0;1.5708rad)
  Radius = 2.5
FEATURE [Part::Cylinder] Cylinder1887  label="Válec1887"
  Angle = 360
  AttacherType = Attacher::AttachEngine3D
  Height = 5
  Placement = pos=(-86,16,68) rot=(0,1,0;1.5708rad)
  Radius = 5
FEATURE [Part::Cylinder] Cylinder1888  label="Válec1888"
  Angle = 360
  AttacherType = Attacher::AttachEngine3D
  Height = 40
  Placement = pos=(-86,-10,69) rot=(0,1,0;1.5708rad)
  Radius = 2.5
FEATURE [Part::Cylinder] Cylinder1889  label="Válec1889"
  Angle = 360
  AttacherType = Attacher::AttachEngine3D
  Height = 40
  Placement = pos=(-86,-10,39) rot=(0,1,0;1.5708rad)
  Radius = 2.5
FEATURE [Part::Cylinder] Cylinder1890  label="Válec1890"
  Angle = 360
  AttacherType = Attacher::AttachEngine3D
  Height = 40
  Placement = pos=(-86,20,39) rot=(0,1,0;1.5708rad)
  Radius = 2.5
FEATURE [Part::Cylinder] Cylinder1891  label="Válec1891"
  Angle = 360
  AttacherType = Attacher::AttachEngine3D
  Height = 40
  Placement = pos=(-86,16,68) rot=(0,1,0;1.5708rad)
  Radius = 2.5
FEATURE [Part::Compound] Compound997
  Links = -> [Cylinder1889,Cylinder1890,Cylinder1888,Cylinder1891]
FEATURE [Part::Cut] Cut619
  Base = -> Chamfer064
  Tool = -> Cylinder1886
FEATURE [Part::Cut] Cut620
  Base = -> Cut619
  Tool = -> Cylinder1887
FEATURE [Part::Cylinder] Cylinder1892  label="Válec1892"
  Angle = 360
  AttacherType = Attacher::AttachEngine3D
  Height = 40
  Placement = pos=(-86,16,68) rot=(0,1,0;1.5708rad)
  Radius = 2.5
FEATURE [Part::Cylinder] Cylinder1893  label="Válec1893"
  Angle = 360
  AttacherType = Attacher::AttachEngine3D
  Height = 72
  Placement = pos=(0,-71,0) rot=(0,0,1;0rad)
  Radius = 1.5
FEATURE [Part::FeaturePython] Tube047  # WARN: FeaturePython — macro-defined, semantics opaque (R4)
  AttacherType = Attacher::AttachEngine3D
  Height = 55
  InnerRadius = 68
  OuterRadius = 74
  Placement = pos=(0,0,29) rot=(0,0,1;0rad)
FEATURE [Part::Box] Box876  label="Krychle876"
  AttacherType = Attacher::AttachEngine3D
  Height = 49
  Length = 56
  Placement = pos=(-28,35,29) rot=(0,0,1;0rad)
  Width = 200
FEATURE [Part::Box] Box877  label="Krychle877"
  AttacherType = Attacher::AttachEngine3D
  Height = 55
  Length = 148
  Placement = pos=(-74,68,29) rot=(0,0,1;0rad)
  Width = 26
FEATURE [Part::Box] Box878  label="Krychle878"
  AttacherType = Attacher::AttachEngine3D
  Height = 60
  Length = 200
  Placement = pos=(0,0,-5) rot=(0,0,-1;0.383972rad)
  Width = 200
FEATURE [Part::Box] Box879  label="Krychle879"
  AttacherType = Attacher::AttachEngine3D
  Height = 60
  Length = 200
  Placement = pos=(70.7107,70.7107,-5) rot=(0,0,1;3.92699rad)
  Width = 120
FEATURE [Part::Box] Box880  label="Krychle880"
  AttacherType = Attacher::AttachEngine3D
  Height = 60
  Length = 200
  Placement = pos=(0,0,-5) rot=(0,0,1;3.52556rad)
  Width = 200
FEATURE [Part::Box] Box881  label="Krychle881"
  AttacherType = Attacher::AttachEngine3D
  Height = 2
  Length = 6
  Placement = pos=(-3,-75,39) rot=(0,0,1;0rad)
  Width = 8
FEATURE [Part::Box] Box882  label="Krychle882"
  AttacherType = Attacher::AttachEngine3D
  Height = 2
  Length = 6
  Placement = pos=(34.9,-66.45,58) rot=(0,0,1;0.523599rad)
  Width = 8
FEATURE [Part::Box] Box883  label="Krychle883"
  AttacherType = Attacher::AttachEngine3D
  Height = 2
  Length = 6
  Placement = pos=(-75,3,39) rot=(0,0,-1;1.5708rad)
  Width = 8
FEATURE [Part::Box] Box884  label="Krychle884"
  AttacherType = Attacher::AttachEngine3D
  Height = 2
  Length = 6
  Placement = pos=(40.0981,63.4519,39) rot=(0,0,1;2.61799rad)
  Width = 8
FEATURE [Part::Cylinder] Cylinder1894  label="Válec1894"
  Angle = 360
  AttacherType = Attacher::AttachEngine3D
  Height = 72
  Placement = pos=(61.4878,35.5,0) rot=(0,0,1;2.0944rad)
  Radius = 1.5
FEATURE [Part::Box] Box885  label="Krychle885"
  AttacherType = Attacher::AttachEngine3D
  Height = 2
  Length = 6
  Placement = pos=(75,-3,39) rot=(0,0,1;1.5708rad)
  Width = 8
FEATURE [Part::Box] Box886  label="Krychle886"
  AttacherType = Attacher::AttachEngine3D
  Height = 2
  Length = 6
  Placement = pos=(-34.9019,66.4519,39) rot=(0,0,1;3.66519rad)
  Width = 8
FEATURE [Part::Box] Box887  label="Krychle887"
  AttacherType = Attacher::AttachEngine3D
  Height = 2
  Length = 6
  Placement = pos=(63.45,-40.1,58) rot=(0,0,1;1.0472rad)
  Width = 8
FEATURE [Part::Box] Box888  label="Krychle888"
  AttacherType = Attacher::AttachEngine3D
  Height = 2
  Length = 6
  Placement = pos=(3,75,39) rot=(0,0,1;3.14159rad)
  Width = 8
FEATURE [Part::Box] Box889  label="Krychle889"
  AttacherType = Attacher::AttachEngine3D
  Height = 2
  Length = 6
  Placement = pos=(-66.4519,-34.9019,39) rot=(0,0,-1;1.0472rad)
  Width = 8
FEATURE [Part::Box] Box890  label="Krychle890"
  AttacherType = Attacher::AttachEngine3D
  Height = 2
  Length = 6
  Placement = pos=(66.4519,34.9019,39) rot=(0,0,1;2.0944rad)
  Width = 8
FEATURE [Part::Box] Box891  label="Krychle891"
  AttacherType = Attacher::AttachEngine3D
  Height = 2
  Length = 6
  Placement = pos=(-40.0981,-63.4519,39) rot=(0,0,-1;0.523599rad)
  Width = 8
FEATURE [Part::Box] Box892  label="Krychle892"
  AttacherType = Attacher::AttachEngine3D
  Height = 2
  Length = 6
  Placement = pos=(-63.4519,40.0981,39) rot=(0,0,1;4.18879rad)
  Width = 8
FEATURE [Part::Compound] Compound998
  Links = -> [Box881,Box882,Box887,Box885,Box890,Box884,Box888,Box886,Box892,Box883,Box889,Box891]
FEATURE [Part::Cylinder] Cylinder1895  label="Válec1895"
  Angle = 360
  AttacherType = Attacher::AttachEngine3D
  Height = 72
  Placement = pos=(71,-1.8e-14,0) rot=(0,0,1;1.5708rad)
  Radius = 1.5
FEATURE [Part::Cylinder] Cylinder1896  label="Válec1896"
  Angle = 360
  AttacherType = Attacher::AttachEngine3D
  Height = 72
  Placement = pos=(35.5,61.4878,0) rot=(0,0,1;2.61799rad)
  Radius = 1.5
FEATURE [Part::Cylinder] Cylinder1897  label="Válec1897"
  Angle = 360
  AttacherType = Attacher::AttachEngine3D
  Height = 72
  Placement = pos=(61.4878,-35.5,0) rot=(0,0,1;1.0472rad)
  Radius = 1.5
FEATURE [Part::Cylinder] Cylinder1898  label="Válec1898"
  Angle = 360
  AttacherType = Attacher::AttachEngine3D
  Height = 72
  Placement = pos=(35.5,-61.4878,0) rot=(0,0,1;0.523599rad)
  Radius = 1.5
FEATURE [Part::Cylinder] Cylinder1899  label="Válec1899"
  Angle = 360
  AttacherType = Attacher::AttachEngine3D
  Height = 72
  Placement = pos=(-35.5,-61.4878,0) rot=(0,0,-1;0.523599rad)
  Radius = 1.5
FEATURE [Part::Cylinder] Cylinder1900  label="Válec1900"
  Angle = 360
  AttacherType = Attacher::AttachEngine3D
  Height = 72
  Placement = pos=(-71,2.7e-14,0) rot=(0,0,-1;1.5708rad)
  Radius = 1.5
FEATURE [Part::Cylinder] Cylinder1901  label="Válec1901"
  Angle = 360
  AttacherType = Attacher::AttachEngine3D
  Height = 72
  Placement = pos=(-61.4878,-35.5,0) rot=(0,0,-1;1.0472rad)
  Radius = 1.5
FEATURE [Part::Cut] Cut622
  Base = -> Tube047
  Tool = -> Box876
FEATURE [Part::Cut] Cut621
  Base = -> Cut622
  Tool = -> Box877
FEATURE [Part::FeaturePython] Tube048  # WARN: FeaturePython — macro-defined, semantics opaque (R4)
  AttacherType = Attacher::AttachEngine3D
  Height = 8
  InnerRadius = 55.1
  OuterRadius = 63
  Placement = pos=(0,0,72) rot=(0,0,1;0rad)
FEATURE [Part::Cut] Cut628
  Base = -> Box879
  Tool = -> Box878
FEATURE [Part::Cut] Cut629
  Base = -> Cut628
  Tool = -> Box880
FEATURE [Part::Cut] Cut630
  Base = -> Cut621
  Tool = -> Cut629
FEATURE [Part::Cut] Cut631
  Base = -> Cut630
  Tool = -> Compound998
FEATURE [Part::Cylinder] Cylinder1902  label="Válec1902"
  Angle = 360
  AttacherType = Attacher::AttachEngine3D
  Height = 72
  Placement = pos=(-35.5,61.4878,0) rot=(0,0,1;3.66519rad)
  Radius = 1.5
FEATURE [Part::Cylinder] Cylinder1903  label="Válec1903"
  Angle = 360
  AttacherType = Attacher::AttachEngine3D
  Height = 72
  Placement = pos=(-61.4878,35.5,0) rot=(0,0,1;4.18879rad)
  Radius = 1.5
FEATURE [Part::Cylinder] Cylinder1904  label="Válec1904"
  Angle = 360
  AttacherType = Attacher::AttachEngine3D
  Height = 72
  Placement = pos=(3.1e-14,71,0) rot=(0,0,1;3.14159rad)
  Radius = 1.5
FEATURE [Part::Compound] Compound1000
  Links = -> [Cylinder1893,Cylinder1898,Cylinder1897,Cylinder1895,Cylinder1894,Cylinder1896,Cylinder1904,Cylinder1902,Cylinder1903,Cylinder1900,Cylinder1901,Cylinder1899]
  Placement = pos=(0,0,-4) rot=(0,0,1;0rad)
FEATURE [Part::Cut] Cut632
  Base = -> Cut631
  Tool = -> Compound1000
FEATURE [Part::Cylinder] Cylinder1905  label="Válec1905"
  Angle = 360
  AttacherType = Attacher::AttachEngine3D
  Height = 50
  Placement = pos=(-18,100,72) rot=(1,0,0;1.5708rad)
  Radius = 1.5
FEATURE [Part::Compound] Compound999
  Links = -> [Cylinder1905]
  Placement = pos=(0,0,0) rot=(0,0,1;3.92699rad)
FEATURE [Part::Cylinder] Cylinder1906  label="Válec1906"
  Angle = 360
  AttacherType = Attacher::AttachEngine3D
  Height = 50
  Placement = pos=(18,100,72) rot=(1,0,0;1.5708rad)
  Radius = 1.5
FEATURE [Part::Compound] Compound1001
  Links = -> [Cylinder1906]
  Placement = pos=(0,0,0) rot=(0,0,1;3.92699rad)
FEATURE [Part::Compound] Compound1002
  Links = -> [Compound999,Compound1001]
  Placement = pos=(0,0,1) rot=(0,0,1;0rad)
FEATURE [Part::Cut] Cut633
  Base = -> Cut632
  Tool = -> Compound1002
FEATURE [Part::Box] Box893  label="Krychle893"
  AttacherType = Attacher::AttachEngine3D
  Height = 6
  Length = 6
  Placement = pos=(15,64,-50) rot=(0,0,1;0rad)
  Width = 4
FEATURE [Part::Box] Box894  label="Krychle894"
  AttacherType = Attacher::AttachEngine3D
  Height = 6
  Length = 6
  Placement = pos=(-21,64,-50) rot=(0,0,1;0rad)
  Width = 4
FEATURE [Part::Compound] Compound1003
  Links = -> [Box894,Box893]
  Placement = pos=(0,0,120) rot=(0,0,1;3.92699rad)
FEATURE [Part::Cut] Cut634
  Base = -> Cut633
  Tool = -> Compound1003
FEATURE [Part::Cylinder] Cylinder1907  label="Válec1907"
  Angle = 360
  AttacherType = Attacher::AttachEngine3D
  Height = 50
  Placement = pos=(-9,100,59) rot=(1,0,0;1.5708rad)
  Radius = 1.5
FEATURE [Part::Compound] Compound1006
  Links = -> [Cylinder1907]
  Placement = pos=(0,0,0) rot=(0,0,1;3.92699rad)
FEATURE [Part::Cylinder] Cylinder1908  label="Válec1908"
  Angle = 360
  AttacherType = Attacher::AttachEngine3D
  Height = 50
  Placement = pos=(9,100,59) rot=(1,0,0;1.5708rad)
  Radius = 1.5
FEATURE [Part::Compound] Compound1005
  Links = -> [Cylinder1908]
  Placement = pos=(0,0,0) rot=(0,0,1;3.92699rad)
FEATURE [Part::Compound] Compound1004
  Links = -> [Compound1006,Compound1005]
  Placement = pos=(0,0,1) rot=(0,0,1;0rad)
FEATURE [Part::Cut] Cut635
  Base = -> Cut634
  Tool = -> Compound1004
FEATURE [Part::Box] Box895  label="Krychle895"
  AttacherType = Attacher::AttachEngine3D
  Height = 6
  Length = 6
  Placement = pos=(6,66,-63) rot=(0,0,1;0rad)
  Width = 4
FEATURE [Part::Box] Box896  label="Krychle896"
  AttacherType = Attacher::AttachEngine3D
  Height = 6
  Length = 6
  Placement = pos=(-12,66,-63) rot=(0,0,1;0rad)
  Width = 4
FEATURE [Part::Compound] Compound1007
  Links = -> [Box896,Box895]
  Placement = pos=(0,0,120) rot=(0,0,1;3.92699rad)
FEATURE [Part::Cut] Cut636
  Base = -> Cut635
  Tool = -> Compound1007
FEATURE [Part::Box] Box897  label="Krychle897"
  AttacherType = Attacher::AttachEngine3D
  Height = 8
  Length = 8
  Placement = pos=(-48,16,35) rot=(0,0,1;1.5708rad)
  Width = 20
FEATURE [Part::Box] Box898  label="Krychle898"
  AttacherType = Attacher::AttachEngine3D
  Height = 8
  Length = 8
  Placement = pos=(-48,-14,35) rot=(0,0,1;1.5708rad)
  Width = 20
FEATURE [Part::Box] Box899  label="Krychle899"
  AttacherType = Attacher::AttachEngine3D
  Height = 8
  Length = 8
  Placement = pos=(-48,-14,65) rot=(0,0,1;1.5708rad)
  Width = 20
FEATURE [Part::Box] Box900  label="Krychle900"
  AttacherType = Attacher::AttachEngine3D
  Height = 8
  Length = 8
  Placement = pos=(-48,-14,35) rot=(0,0,1;1.5708rad)
  Width = 20
FEATURE [Part::Box] Box901  label="Krychle901"
  AttacherType = Attacher::AttachEngine3D
  Height = 8
  Length = 8
  Placement = pos=(-48,-14,65) rot=(0,0,1;1.5708rad)
  Width = 20
FEATURE [Part::Box] Box902  label="Krychle902"
  AttacherType = Attacher::AttachEngine3D
  Height = 8
  Length = 8
  Placement = pos=(-48,-14,35) rot=(0,0,1;1.5708rad)
  Width = 20
FEATURE [Part::Box] Box903  label="Krychle903"
  AttacherType = Attacher::AttachEngine3D
  Height = 8
  Length = 8
  Placement = pos=(-48,-14,65) rot=(0,0,1;1.5708rad)
  Width = 20
FEATURE [Part::Cylinder] Cylinder1909  label="Válec1909"
  Angle = 360
  AttacherType = Attacher::AttachEngine3D
  Height = 40
  Placement = pos=(-86,-10,69) rot=(0,1,0;1.5708rad)
  Radius = 2.5
FEATURE [Part::Cylinder] Cylinder1910  label="Válec1910"
  Angle = 360
  AttacherType = Attacher::AttachEngine3D
  Height = 40
  Placement = pos=(-86,-10,39) rot=(0,1,0;1.5708rad)
  Radius = 2.5
FEATURE [Part::Cylinder] Cylinder1911  label="Válec1911"
  Angle = 360
  AttacherType = Attacher::AttachEngine3D
  Height = 40
  Placement = pos=(-86,20,39) rot=(0,1,0;1.5708rad)
  Radius = 2.5
FEATURE [Part::Cylinder] Cylinder1912  label="Válec1912"
  Angle = 360
  AttacherType = Attacher::AttachEngine3D
  Height = 40
  Placement = pos=(-86,16,68) rot=(0,1,0;1.5708rad)
  Radius = 2.5
FEATURE [Part::Cylinder] Cylinder1913  label="Válec1913"
  Angle = 360
  AttacherType = Attacher::AttachEngine3D
  Height = 40
  Placement = pos=(-86,-10,39) rot=(0,1,0;1.5708rad)
  Radius = 2.5
FEATURE [Part::Cylinder] Cylinder1914  label="Válec1914"
  Angle = 360
  AttacherType = Attacher::AttachEngine3D
  Height = 40
  Placement = pos=(-86,-10,69) rot=(0,1,0;1.5708rad)
  Radius = 2.5
FEATURE [Part::Compound] Compound1010
  Links = -> [Box900,Box901]
  Placement = pos=(1.5,0,0) rot=(0,0,1;1.5708rad)
FEATURE [Part::Compound] Compound1011
  Links = -> [Box902,Box903]
  Placement = pos=(-21.5,0,0) rot=(0,0,1;1.5708rad)
FEATURE [Part::Compound] Compound1009
  Links = -> [Compound1011,Compound1010]
FEATURE [Part::Compound] Compound1012
  Links = -> [Cylinder1910,Cylinder1911,Cylinder1909,Cylinder1912]
FEATURE [Part::Cylinder] Cylinder1915  label="Válec1915"
  Angle = 360
  AttacherType = Attacher::AttachEngine3D
  Height = 40
  Placement = pos=(-86,-10,69) rot=(0,1,0;1.5708rad)
  Radius = 2.5
FEATURE [Part::Compound] Compound1014
  Links = -> [Cylinder1913,Cylinder1915]
  Placement = pos=(-21.5,0,0) rot=(0,0,1;1.5708rad)
FEATURE [Part::Cylinder] Cylinder1916  label="Válec1916"
  Angle = 360
  AttacherType = Attacher::AttachEngine3D
  Height = 40
  Placement = pos=(-86,-10,39) rot=(0,1,0;1.5708rad)
  Radius = 2.5
FEATURE [Part::Compound] Compound1013
  Links = -> [Cylinder1916,Cylinder1914]
  Placement = pos=(1.5,0,0) rot=(0,0,1;1.5708rad)
FEATURE [Part::Compound] Compound1015
  Links = -> [Compound1013,Compound1014]
FEATURE [Part::Box] Box904  label="Krychle904"
  AttacherType = Attacher::AttachEngine3D
  Height = 8
  Length = 8
  Placement = pos=(-68,-14,35) rot=(0,0,1;1.5708rad)
  Width = 2.5
FEATURE [Part::Box] Box905  label="Krychle905"
  AttacherType = Attacher::AttachEngine3D
  Height = 8
  Length = 8
  Placement = pos=(-68,16,35) rot=(0,0,1;1.5708rad)
  Width = 2.5
FEATURE [Part::Box] Box906  label="Krychle906"
  AttacherType = Attacher::AttachEngine3D
  Height = 8
  Length = 8
  Placement = pos=(-68,-14,65) rot=(0,0,1;1.5708rad)
  Width = 2.5
FEATURE [Part::Box] Box907  label="Krychle907"
  AttacherType = Attacher::AttachEngine3D
  Height = 8
  Length = 8
  Placement = pos=(-68,-14,65) rot=(0,0,1;1.5708rad)
  Width = 2.5
FEATURE [Part::Box] Box908  label="Krychle908"
  AttacherType = Attacher::AttachEngine3D
  Height = 8
  Length = 8
  Placement = pos=(-68,-14,35) rot=(0,0,1;1.5708rad)
  Width = 2.5
FEATURE [Part::Compound] Compound1018
  Links = -> [Box908,Box907]
  Placement = pos=(1.5,0,0) rot=(0,0,1;1.5708rad)
FEATURE [Part::Box] Box909  label="Krychle909"
  AttacherType = Attacher::AttachEngine3D
  Height = 8
  Length = 8
  Placement = pos=(-68,-14,65) rot=(0,0,1;1.5708rad)
  Width = 2.5
FEATURE [Part::Box] Box910  label="Krychle910"
  AttacherType = Attacher::AttachEngine3D
  Height = 8
  Length = 8
  Placement = pos=(-68,-14,35) rot=(0,0,1;1.5708rad)
  Width = 2.5
FEATURE [Part::Compound] Compound1019
  Links = -> [Box910,Box909]
  Placement = pos=(-21.5,0,0) rot=(0,0,1;1.5708rad)
FEATURE [Part::Compound] Compound1017
  Links = -> [Compound1019,Compound1018]
FEATURE [Part::Box] Box911  label="Krychle911"
  AttacherType = Attacher::AttachEngine3D
  Height = 8
  Length = 8
  Placement = pos=(-48,12,64) rot=(0,0,1;1.5708rad)
  Width = 20
FEATURE [Part::Compound] Compound1008
  Links = -> [Box898,Box897,Box899,Box911]
FEATURE [Part::Box] Box912  label="Krychle912"
  AttacherType = Attacher::AttachEngine3D
  Height = 8
  Length = 8
  Placement = pos=(-68,12,64) rot=(0,0,1;1.5708rad)
  Width = 2.5
FEATURE [Part::Compound] Compound1016
  Links = -> [Box904,Box905,Box906,Box912]
FEATURE [Part::Cylinder] Cylinder1917  label="Válec1917"
  Angle = 360
  AttacherType = Attacher::AttachEngine3D
  Height = 51
  Placement = pos=(0,0,29) rot=(0,0,1;0rad)
  Radius = 74
FEATURE [Part::Box] Box913  label="Krychle913"
  AttacherType = Attacher::AttachEngine3D
  Height = 6
  Length = 8
  Placement = pos=(-75,38,36) rot=(0,0,1;0rad)
  Width = 2
FEATURE [Part::Box] Box914  label="Krychle914"
  AttacherType = Attacher::AttachEngine3D
  Height = 55
  Length = 148
  Placement = pos=(-74,48,29) rot=(0,0,1;0rad)
  Width = 26
FEATURE [Part::Box] Box915  label="Krychle915"
  AttacherType = Attacher::AttachEngine3D
  Height = 6
  Length = 8
  Placement = pos=(67,38,36) rot=(0,0,1;0rad)
  Width = 2
FEATURE [Part::Cylinder] Cylinder1918  label="Válec1918"
  Angle = 360
  AttacherType = Attacher::AttachEngine3D
  Height = 50
  Placement = pos=(-71,80,73) rot=(1,0,0;1.5708rad)
  Radius = 1.5
FEATURE [Part::Cylinder] Cylinder1919  label="Válec1919"
  Angle = 360
  AttacherType = Attacher::AttachEngine3D
  Height = 50
  Placement = pos=(71,80,56) rot=(1,0,0;1.5708rad)
  Radius = 1.5
FEATURE [Part::Cylinder] Cylinder1920  label="Válec1920"
  Angle = 360
  AttacherType = Attacher::AttachEngine3D
  Height = 40
  Placement = pos=(-86,-10,69) rot=(0,1,0;1.5708rad)
  Radius = 2.5
FEATURE [Part::Cylinder] Cylinder1921  label="Válec1921"
  Angle = 360
  AttacherType = Attacher::AttachEngine3D
  Height = 40
  Placement = pos=(-86,-10,39) rot=(0,1,0;1.5708rad)
  Radius = 2.5
FEATURE [Part::Box] Box916  label="Krychle916"
  AttacherType = Attacher::AttachEngine3D
  Height = 55
  Length = 148
  Placement = pos=(-74,0,29) rot=(0,0,1;0rad)
  Width = 74
FEATURE [Part::Cylinder] Cylinder1922  label="Válec1922"
  Angle = 360
  AttacherType = Attacher::AttachEngine3D
  Height = 50
  Placement = pos=(71,80,73) rot=(1,0,0;1.5708rad)
  Radius = 1.5
FEATURE [Part::Cylinder] Cylinder1923  label="Válec1923"
  Angle = 360
  AttacherType = Attacher::AttachEngine3D
  Height = 50
  Placement = pos=(71,80,39) rot=(1,0,0;1.5708rad)
  Radius = 1.5
FEATURE [Part::Cylinder] Cylinder1924  label="Válec1924"
  Angle = 360
  AttacherType = Attacher::AttachEngine3D
  Height = 50
  Placement = pos=(-71,80,56) rot=(1,0,0;1.5708rad)
  Radius = 1.5
FEATURE [Part::Cut] Cut638
  Base = -> Box916
  Tool = -> Cylinder1917
FEATURE [Part::Cut] Cut639
  Base = -> Cut638
  Tool = -> Box914
FEATURE [Part::Cylinder] Cylinder1925  label="Válec1925"
  Angle = 360
  AttacherType = Attacher::AttachEngine3D
  Height = 40
  Placement = pos=(-86,-10,69) rot=(0,1,0;1.5708rad)
  Radius = 2.5
FEATURE [Part::Cylinder] Cylinder1926  label="Válec1926"
  Angle = 360
  AttacherType = Attacher::AttachEngine3D
  Height = 40
  Placement = pos=(-86,-10,39) rot=(0,1,0;1.5708rad)
  Radius = 2.5
FEATURE [Part::Cylinder] Cylinder1927  label="Válec1927"
  Angle = 360
  AttacherType = Attacher::AttachEngine3D
  Height = 40
  Placement = pos=(-86,-10,39) rot=(0,1,0;1.5708rad)
  Radius = 2.5
FEATURE [Part::Cylinder] Cylinder1928  label="Válec1928"
  Angle = 360
  AttacherType = Attacher::AttachEngine3D
  Height = 40
  Placement = pos=(-86,20,39) rot=(0,1,0;1.5708rad)
  Radius = 2.5
FEATURE [Part::Cylinder] Cylinder1929  label="Válec1929"
  Angle = 360
  AttacherType = Attacher::AttachEngine3D
  Height = 40
  Placement = pos=(-86,-10,69) rot=(0,1,0;1.5708rad)
  Radius = 2.5
FEATURE [Part::Box] Box917  label="Krychle917"
  AttacherType = Attacher::AttachEngine3D
  Height = 8
  Length = 8
  Placement = pos=(-48,-14,65) rot=(0,0,1;1.5708rad)
  Width = 20
FEATURE [Part::Box] Box918  label="Krychle918"
  AttacherType = Attacher::AttachEngine3D
  Height = 8
  Length = 8
  Placement = pos=(-48,-14,35) rot=(0,0,1;1.5708rad)
  Width = 20
FEATURE [Part::Compound] Compound1029
  Links = -> [Box918,Box917]
  Placement = pos=(-21.5,0,0) rot=(0,0,1;1.5708rad)
FEATURE [Part::Box] Box919  label="Krychle919"
  AttacherType = Attacher::AttachEngine3D
  Height = 8
  Length = 8
  Placement = pos=(-48,-14,65) rot=(0,0,1;1.5708rad)
  Width = 20
FEATURE [Part::Cylinder] Cylinder1930  label="Válec1930"
  Angle = 360
  AttacherType = Attacher::AttachEngine3D
  Height = 40
  Placement = pos=(-86,-10,39) rot=(0,1,0;1.5708rad)
  Radius = 2.5
FEATURE [Part::Compound] Compound1022
  Links = -> [Cylinder1930,Cylinder1925]
  Placement = pos=(-21.5,0,0) rot=(0,0,1;1.5708rad)
FEATURE [Part::Cylinder] Cylinder1931  label="Válec1931"
  Angle = 360
  AttacherType = Attacher::AttachEngine3D
  Height = 40
  Placement = pos=(-86,20,39) rot=(0,1,0;1.5708rad)
  Radius = 2.5
FEATURE [Part::Cylinder] Cylinder1932  label="Válec1932"
  Angle = 360
  AttacherType = Attacher::AttachEngine3D
  Height = 6
  Placement = pos=(0,0,65) rot=(0,0,1;0rad)
  Radius = 74
FEATURE [Part::Box] Box920  label="Krychle920"
  AttacherType = Attacher::AttachEngine3D
  Height = 34
  Length = 148
  Placement = pos=(-74,68,38) rot=(0,0,1;0rad)
  Width = 20
FEATURE [Part::Cut] Cut625
  Base = -> Cylinder1932
  Placement = pos=(0,0,13) rot=(0,0,1;0rad)
  Tool = -> Box920
FEATURE [Part::Box] Box921  label="Krychle921"
  AttacherType = Attacher::AttachEngine3D
  Height = 8
  Length = 8
  Placement = pos=(-48,-14,35) rot=(0,0,1;1.5708rad)
  Width = 20
FEATURE [Part::Box] Box922  label="Krychle922"
  AttacherType = Attacher::AttachEngine3D
  Height = 8
  Length = 8
  Placement = pos=(-48,-14,35) rot=(0,0,1;1.5708rad)
  Width = 20
FEATURE [Part::Compound] Compound1032
  Links = -> [Box922,Box919]
  Placement = pos=(1.5,0,0) rot=(0,0,1;1.5708rad)
FEATURE [Part::Compound] Compound1028
  Links = -> [Compound1029,Compound1032]
FEATURE [Part::Box] Box923  label="Krychle923"
  AttacherType = Attacher::AttachEngine3D
  Height = 8
  Length = 8
  Placement = pos=(-48,-14,65) rot=(0,0,1;1.5708rad)
  Width = 20
FEATURE [Part::Box] Box924  label="Krychle924"
  AttacherType = Attacher::AttachEngine3D
  Height = 8
  Length = 8
  Placement = pos=(-48,16,35) rot=(0,0,1;1.5708rad)
  Width = 20
FEATURE [Part::Box] Box925  label="Krychle925"
  AttacherType = Attacher::AttachEngine3D
  Height = 8
  Length = 8
  Placement = pos=(-48,16,35) rot=(0,0,1;1.5708rad)
  Width = 20
FEATURE [Part::Box] Box926  label="Krychle926"
  AttacherType = Attacher::AttachEngine3D
  Height = 8
  Length = 8
  Placement = pos=(-68,12,64) rot=(0,0,1;1.5708rad)
  Width = 2.5
FEATURE [Part::Box] Box927  label="Krychle927"
  AttacherType = Attacher::AttachEngine3D
  Height = 8
  Length = 8
  Placement = pos=(-48,-14,65) rot=(0,0,1;1.5708rad)
  Width = 20
FEATURE [Part::Box] Box928  label="Krychle928"
  AttacherType = Attacher::AttachEngine3D
  Height = 8
  Length = 8
  Placement = pos=(-48,-14,35) rot=(0,0,1;1.5708rad)
  Width = 20
FEATURE [Part::Box] Box929  label="Krychle929"
  AttacherType = Attacher::AttachEngine3D
  Height = 8
  Length = 8
  Placement = pos=(-68,-14,65) rot=(0,0,1;1.5708rad)
  Width = 2.5
FEATURE [Part::Box] Box930  label="Krychle930"
  AttacherType = Attacher::AttachEngine3D
  Height = 8
  Length = 8
  Placement = pos=(-68,16,35) rot=(0,0,1;1.5708rad)
  Width = 2.5
FEATURE [Part::Box] Box931  label="Krychle931"
  AttacherType = Attacher::AttachEngine3D
  Height = 8
  Length = 8
  Placement = pos=(-68,-14,35) rot=(0,0,1;1.5708rad)
  Width = 2.5
FEATURE [Part::Box] Box932  label="Krychle932"
  AttacherType = Attacher::AttachEngine3D
  Height = 8
  Length = 8
  Placement = pos=(-48,12,64) rot=(0,0,1;1.5708rad)
  Width = 20
FEATURE [Part::Cylinder] Cylinder1933  label="Válec1933"
  Angle = 360
  AttacherType = Attacher::AttachEngine3D
  Height = 40
  Placement = pos=(-86,-10,69) rot=(0,1,0;1.5708rad)
  Radius = 2.5
FEATURE [Part::Cylinder] Cylinder1934  label="Válec1934"
  Angle = 360
  AttacherType = Attacher::AttachEngine3D
  Height = 40
  Placement = pos=(-86,-10,69) rot=(0,1,0;1.5708rad)
  Radius = 2.5
FEATURE [Part::Compound] Compound1020
  Links = -> [Cylinder1927,Cylinder1934]
  Placement = pos=(1.5,0,0) rot=(0,0,1;1.5708rad)
FEATURE [Part::Cylinder] Cylinder1935  label="Válec1935"
  Angle = 360
  AttacherType = Attacher::AttachEngine3D
  Height = 40
  Placement = pos=(-86,16,68) rot=(0,1,0;1.5708rad)
  Radius = 2.5
FEATURE [Part::Cylinder] Cylinder1936  label="Válec1936"
  Angle = 360
  AttacherType = Attacher::AttachEngine3D
  Height = 40
  Placement = pos=(-86,20,39) rot=(0,1,0;1.5708rad)
  Radius = 2.5
FEATURE [Part::Cylinder] Cylinder1937  label="Válec1937"
  Angle = 360
  AttacherType = Attacher::AttachEngine3D
  Height = 40
  Placement = pos=(-86,-10,39) rot=(0,1,0;1.5708rad)
  Radius = 2.5
FEATURE [Part::Cylinder] Cylinder1938  label="Válec1938"
  Angle = 360
  AttacherType = Attacher::AttachEngine3D
  Height = 40
  Placement = pos=(-86,-10,69) rot=(0,1,0;1.5708rad)
  Radius = 2.5
FEATURE [Part::Box] Box933  label="Krychle933"
  AttacherType = Attacher::AttachEngine3D
  Height = 8
  Length = 8
  Placement = pos=(-68,12,64) rot=(0,0,1;1.5708rad)
  Width = 2.5
FEATURE [Part::Box] Box934  label="Krychle934"
  AttacherType = Attacher::AttachEngine3D
  Height = 8
  Length = 8
  Placement = pos=(-48,16,35) rot=(0,0,1;1.5708rad)
  Width = 20
FEATURE [Part::Box] Box935  label="Krychle935"
  AttacherType = Attacher::AttachEngine3D
  Height = 8
  Length = 8
  Placement = pos=(-48,-14,35) rot=(0,0,1;1.5708rad)
  Width = 20
FEATURE [Part::Box] Box936  label="Krychle936"
  AttacherType = Attacher::AttachEngine3D
  Height = 8
  Length = 8
  Placement = pos=(-48,-14,65) rot=(0,0,1;1.5708rad)
  Width = 20
FEATURE [Part::Box] Box937  label="Krychle937"
  AttacherType = Attacher::AttachEngine3D
  Height = 8
  Length = 8
  Placement = pos=(-48,12,64) rot=(0,0,1;1.5708rad)
  Width = 20
FEATURE [Part::Box] Box938  label="Krychle938"
  AttacherType = Attacher::AttachEngine3D
  Height = 8
  Length = 8
  Placement = pos=(-68,-14,35) rot=(0,0,1;1.5708rad)
  Width = 2.5
FEATURE [Part::Box] Box939  label="Krychle939"
  AttacherType = Attacher::AttachEngine3D
  Height = 8
  Length = 8
  Placement = pos=(-68,16,35) rot=(0,0,1;1.5708rad)
  Width = 2.5
FEATURE [Part::Box] Box940  label="Krychle940"
  AttacherType = Attacher::AttachEngine3D
  Height = 8
  Length = 8
  Placement = pos=(-68,-14,65) rot=(0,0,1;1.5708rad)
  Width = 2.5
FEATURE [Part::Box] Box941  label="Krychle941"
  AttacherType = Attacher::AttachEngine3D
  Height = 8
  Length = 8
  Placement = pos=(-68,12,64) rot=(0,0,1;1.5708rad)
  Width = 2.5
FEATURE [Part::Compound] Compound1024
  Links = -> [Box938,Box939,Box940,Box941]
FEATURE [Part::Mirroring] mirror001  label="Compound999 (mirrored)"
  Base = (0,0,0)
  Normal = (1,0,0)
  Source = -> Compound1024
FEATURE [Part::Compound] Compound1030
  Links = -> [Compound1016,Compound1017,mirror001]
FEATURE [Part::Cylinder] Cylinder1939  label="Válec1939"
  Angle = 360
  AttacherType = Attacher::AttachEngine3D
  Height = 40
  Placement = pos=(-86,-10,69) rot=(0,1,0;1.5708rad)
  Radius = 2.5
FEATURE [Part::Cylinder] Cylinder1940  label="Válec1940"
  Angle = 360
  AttacherType = Attacher::AttachEngine3D
  Height = 40
  Placement = pos=(-86,-10,39) rot=(0,1,0;1.5708rad)
  Radius = 2.5
FEATURE [Part::Cylinder] Cylinder1941  label="Válec1941"
  Angle = 360
  AttacherType = Attacher::AttachEngine3D
  Height = 40
  Placement = pos=(-86,20,39) rot=(0,1,0;1.5708rad)
  Radius = 2.5
FEATURE [Part::Cylinder] Cylinder1942  label="Válec1942"
  Angle = 360
  AttacherType = Attacher::AttachEngine3D
  Height = 40
  Placement = pos=(-86,16,68) rot=(0,1,0;1.5708rad)
  Radius = 2.5
FEATURE [Part::Compound] Compound1026
  Links = -> [Cylinder1940,Cylinder1941,Cylinder1939,Cylinder1942]
FEATURE [Part::Mirroring] mirror002  label="Compound1000 (mirrored)"
  Base = (0,0,0)
  Normal = (1,0,0)
  Source = -> Compound1026
FEATURE [Part::Cylinder] Cylinder1943  label="Válec1943"
  Angle = 360
  AttacherType = Attacher::AttachEngine3D
  Height = 40
  Placement = pos=(-86,-10,39) rot=(0,1,0;1.5708rad)
  Radius = 2.5
FEATURE [Part::Cylinder] Cylinder1944  label="Válec1944"
  Angle = 360
  AttacherType = Attacher::AttachEngine3D
  Height = 40
  Placement = pos=(-86,20,39) rot=(0,1,0;1.5708rad)
  Radius = 2.5
FEATURE [Part::Cylinder] Cylinder1945  label="Válec1945"
  Angle = 360
  AttacherType = Attacher::AttachEngine3D
  Height = 40
  Placement = pos=(-86,16,68) rot=(0,1,0;1.5708rad)
  Radius = 2.5
FEATURE [Part::Cylinder] Cylinder1946  label="Válec1946"
  Angle = 360
  AttacherType = Attacher::AttachEngine3D
  Height = 40
  Placement = pos=(-86,-10,39) rot=(0,1,0;1.5708rad)
  Radius = 2.5
FEATURE [Part::Cylinder] Cylinder1947  label="Válec1947"
  Angle = 360
  AttacherType = Attacher::AttachEngine3D
  Height = 40
  Placement = pos=(-86,-10,69) rot=(0,1,0;1.5708rad)
  Radius = 2.5
FEATURE [Part::Cylinder] Cylinder1948  label="Válec1948"
  Angle = 360
  AttacherType = Attacher::AttachEngine3D
  Height = 40
  Placement = pos=(-86,-10,69) rot=(0,1,0;1.5708rad)
  Radius = 2.5
FEATURE [Part::Cylinder] Cylinder1949  label="Válec1949"
  Angle = 360
  AttacherType = Attacher::AttachEngine3D
  Height = 40
  Placement = pos=(-86,-10,39) rot=(0,1,0;1.5708rad)
  Radius = 2.5
FEATURE [Part::Box] Box942  label="Krychle942"
  AttacherType = Attacher::AttachEngine3D
  Height = 8
  Length = 8
  Placement = pos=(-68,-14,35) rot=(0,0,1;1.5708rad)
  Width = 2.5
FEATURE [Part::Box] Box943  label="Krychle943"
  AttacherType = Attacher::AttachEngine3D
  Height = 8
  Length = 8
  Placement = pos=(-68,16,35) rot=(0,0,1;1.5708rad)
  Width = 2.5
FEATURE [Part::Box] Box944  label="Krychle944"
  AttacherType = Attacher::AttachEngine3D
  Height = 8
  Length = 8
  Placement = pos=(-68,-14,65) rot=(0,0,1;1.5708rad)
  Width = 2.5
FEATURE [Part::Box] Box945  label="Krychle945"
  AttacherType = Attacher::AttachEngine3D
  Height = 8
  Length = 8
  Placement = pos=(-68,-14,65) rot=(0,0,1;1.5708rad)
  Width = 2.5
FEATURE [Part::Box] Box946  label="Krychle946"
  AttacherType = Attacher::AttachEngine3D
  Height = 8
  Length = 8
  Placement = pos=(-68,-14,35) rot=(0,0,1;1.5708rad)
  Width = 2.5
FEATURE [Part::Box] Box947  label="Krychle947"
  AttacherType = Attacher::AttachEngine3D
  Height = 8
  Length = 8
  Placement = pos=(-68,-14,65) rot=(0,0,1;1.5708rad)
  Width = 2.5
FEATURE [Part::Box] Box948  label="Krychle948"
  AttacherType = Attacher::AttachEngine3D
  Height = 8
  Length = 8
  Placement = pos=(-68,-14,35) rot=(0,0,1;1.5708rad)
  Width = 2.5
FEATURE [Part::Box] Box949  label="Krychle949"
  AttacherType = Attacher::AttachEngine3D
  Height = 8
  Length = 8
  Placement = pos=(-48,12,64) rot=(0,0,1;1.5708rad)
  Width = 20
FEATURE [Part::Compound] Compound1031
  Links = -> [Box921,Box924,Box923,Box949]
FEATURE [Part::Compound] Compound1033
  Links = -> [Compound1012,Compound1015,mirror002]
FEATURE [Part::Cylinder] Cylinder1950  label="Válec1950"
  Angle = 360
  AttacherType = Attacher::AttachEngine3D
  Height = 50
  Placement = pos=(-71,80,39) rot=(1,0,0;1.5708rad)
  Radius = 1.5
FEATURE [Part::Compound] Compound1025
  Links = -> [Cylinder1918,Cylinder1923,Cylinder1950,Cylinder1922,Cylinder1924,Cylinder1919]
FEATURE [Part::Cut] Cut640
  Base = -> Cut639
  Tool = -> Compound1025
FEATURE [Part::Box] Box950  label="Krychle950"
  AttacherType = Attacher::AttachEngine3D
  Height = 6
  Length = 8
  Placement = pos=(67,38,70) rot=(0,0,1;0rad)
  Width = 2
FEATURE [Part::Box] Box951  label="Krychle951"
  AttacherType = Attacher::AttachEngine3D
  Height = 6
  Length = 8
  Placement = pos=(-75,38,70) rot=(0,0,1;0rad)
  Width = 2
FEATURE [Part::Box] Box952  label="Krychle952"
  AttacherType = Attacher::AttachEngine3D
  Height = 6
  Length = 8
  Placement = pos=(-75,38,53) rot=(0,0,1;0rad)
  Width = 2
FEATURE [Part::Box] Box953  label="Krychle953"
  AttacherType = Attacher::AttachEngine3D
  Height = 6
  Length = 8
  Placement = pos=(67,38,53) rot=(0,0,1;0rad)
  Width = 2
FEATURE [Part::Compound] Compound1021
  Links = -> [Box913,Box915,Box950,Box951,Box952,Box953]
FEATURE [Part::Cut] Cut641
  Base = -> Cut640
  Tool = -> Compound1021
FEATURE [Part::Box] Box954  label="Krychle954"
  AttacherType = Attacher::AttachEngine3D
  Height = 2
  Length = 6
  Placement = pos=(-3,-75,39) rot=(0,0,1;0rad)
  Width = 8
FEATURE [Part::Box] Box955  label="Krychle955"
  AttacherType = Attacher::AttachEngine3D
  Height = 2
  Length = 6
  Placement = pos=(34.9019,-66.4519,39) rot=(0,0,1;0.523599rad)
  Width = 8
FEATURE [Part::Box] Box956  label="Krychle956"
  AttacherType = Attacher::AttachEngine3D
  Height = 2
  Length = 6
  Placement = pos=(63.4519,-40.0981,39) rot=(0,0,1;1.0472rad)
  Width = 8
FEATURE [Part::Box] Box957  label="Krychle957"
  AttacherType = Attacher::AttachEngine3D
  Height = 2
  Length = 6
  Placement = pos=(75,-3,39) rot=(0,0,1;1.5708rad)
  Width = 8
FEATURE [Part::Box] Box958  label="Krychle958"
  AttacherType = Attacher::AttachEngine3D
  Height = 2
  Length = 6
  Placement = pos=(66.4519,34.9019,39) rot=(0,0,1;2.0944rad)
  Width = 8
FEATURE [Part::Box] Box959  label="Krychle959"
  AttacherType = Attacher::AttachEngine3D
  Height = 2
  Length = 6
  Placement = pos=(40.0981,63.4519,39) rot=(0,0,1;2.61799rad)
  Width = 8
FEATURE [Part::Box] Box960  label="Krychle960"
  AttacherType = Attacher::AttachEngine3D
  Height = 2
  Length = 6
  Placement = pos=(3,75,39) rot=(0,0,1;3.14159rad)
  Width = 8
FEATURE [Part::Box] Box961  label="Krychle961"
  AttacherType = Attacher::AttachEngine3D
  Height = 2
  Length = 6
  Placement = pos=(-34.9019,66.4519,39) rot=(0,0,1;3.66519rad)
  Width = 8
FEATURE [Part::Box] Box962  label="Krychle962"
  AttacherType = Attacher::AttachEngine3D
  Height = 2
  Length = 6
  Placement = pos=(-63.4519,40.0981,39) rot=(0,0,1;4.18879rad)
  Width = 8
FEATURE [Part::Box] Box963  label="Krychle963"
  AttacherType = Attacher::AttachEngine3D
  Height = 2
  Length = 6
  Placement = pos=(-75,3,39) rot=(0,0,-1;1.5708rad)
  Width = 8
FEATURE [Part::Box] Box964  label="Krychle964"
  AttacherType = Attacher::AttachEngine3D
  Height = 2
  Length = 6
  Placement = pos=(-66.4519,-34.9019,39) rot=(0,0,-1;1.0472rad)
  Width = 8
FEATURE [Part::Box] Box965  label="Krychle965"
  AttacherType = Attacher::AttachEngine3D
  Height = 2
  Length = 6
  Placement = pos=(-40.0981,-63.4519,39) rot=(0,0,-1;0.523599rad)
  Width = 8
FEATURE [Part::Compound] Compound1023
  Links = -> [Box954,Box955,Box956,Box957,Box958,Box959,Box960,Box961,Box962,Box963,Box964,Box965]
FEATURE [Part::Cut] Cut626
  Base = -> Cut641
  Tool = -> Compound1023
FEATURE [Part::Compound] Compound1034
  Links = -> [Box935,Box934,Box936,Box937]
FEATURE [Part::Mirroring] mirror013  label="Compound998 (mirrored)"
  Base = (0,0,0)
  Normal = (1,0,0)
  Source = -> Compound1034
FEATURE [Part::Compound] Compound1035
  Links = -> [Cylinder1949,Cylinder1947]
  Placement = pos=(1.5,0,0) rot=(0,0,1;1.5708rad)
FEATURE [Part::Compound] Compound1036
  Links = -> [Cylinder1943,Cylinder1944,Cylinder1929,Cylinder1945]
FEATURE [Part::Compound] Compound1037
  Links = -> [Compound1008,Compound1009,mirror013]
FEATURE [Part::Cut] Cut637
  Base = -> Cut636
  Tool = -> Compound1037
FEATURE [Part::Cut] Cut623
  Base = -> Cut637
  Tool = -> Compound1030
FEATURE [Part::Cut] Cut624
  Base = -> Cut623
  Tool = -> Compound1033
FEATURE [Part::Compound] Compound1038
  Links = -> [Cylinder1946,Cylinder1948]
  Placement = pos=(-21.5,0,0) rot=(0,0,1;1.5708rad)
FEATURE [Part::Compound] Compound1039
  Links = -> [Compound1035,Compound1038]
FEATURE [Part::Compound] Compound1040
  Links = -> [Box942,Box943,Box944,Box926]
FEATURE [Part::Compound] Compound1042
  Links = -> [Box946,Box945]
  Placement = pos=(1.5,0,0) rot=(0,0,1;1.5708rad)
FEATURE [Part::Compound] Compound1043
  Links = -> [Box948,Box947]
  Placement = pos=(-21.5,0,0) rot=(0,0,1;1.5708rad)
FEATURE [Part::Compound] Compound1041
  Links = -> [Compound1043,Compound1042]
FEATURE [Part::Compound] Compound1044
  Links = -> [Box931,Box930,Box929,Box933]
FEATURE [Part::Mirroring] mirror014  label="Compound999 (mirrored)001"
  Base = (0,0,0)
  Normal = (1,0,0)
  Source = -> Compound1044
FEATURE [Part::Compound] Compound1045
  Links = -> [Cylinder1937,Cylinder1936,Cylinder1938,Cylinder1935]
FEATURE [Part::Mirroring] mirror015  label="Compound1000 (mirrored)001"
  Base = (0,0,0)
  Normal = (1,0,0)
  Source = -> Compound1045
FEATURE [Part::Compound] Compound1046
  Links = -> [Compound1040,Compound1041,mirror014]
FEATURE [Part::Compound] Compound1047
  Links = -> [Compound1036,Compound1039,mirror015]
FEATURE [Part::Compound] Compound1048
  Links = -> [Box928,Box925,Box927,Box932]
FEATURE [Part::Mirroring] mirror016  label="Compound998 (mirrored)001"
  Base = (0,0,0)
  Normal = (1,0,0)
  Source = -> Compound1048
FEATURE [Part::Compound] Compound1049
  Links = -> [Compound1031,Compound1028,mirror016]
FEATURE [Part::Compound] Compound1050
  Links = -> [Cylinder1921,Cylinder1931,Cylinder1933]
FEATURE [Part::Mirroring] mirror012  label="Compound944 (mirrored)002"
  Base = (0,0,0)
  Normal = (1,0,0)
  Source = -> Compound1050
FEATURE [Part::Compound] Compound1051
  Links = -> [Compound1020,Compound1022]
FEATURE [Part::Compound] Compound1053
  Links = -> [Cylinder1926,Cylinder1928,Cylinder1920]
FEATURE [Part::Compound] Compound1052
  Links = -> [Compound1053,Compound1051,mirror012]
FEATURE [Part::Cut] Cut627
  Base = -> Cut626
  Tool = -> Compound1052
FEATURE [Part::Cut] Cut642
  Base = -> Cut627
  Tool = -> Compound1049
FEATURE [Part::Cut] Cut643
  Base = -> Cut642
  Tool = -> Compound1047
FEATURE [Part::Cut] Cut644
  Base = -> Cut643
  Tool = -> Compound1046
FEATURE [Part::Compound] Compound1027  label="Base_bare-turret"
  Links = -> [Cut624,Cut625,Cut644,Tube048]
FEATURE [Part::Compound] Compound1054  label="Base_balancer-side-wide"
  Links = -> [Cut566,Compound917,Cut620,Cut568]
FEATURE [Part::Cylinder] Cylinder1951  label="Válec1951"
  Angle = 360
  AttacherType = Attacher::AttachEngine3D
  Height = 20
  Placement = pos=(-109,7,54) rot=(0,0,1;0rad)
  Radius = 1.5
FEATURE [Part::Cylinder] Cylinder1952  label="Válec1952"
  Angle = 360
  AttacherType = Attacher::AttachEngine3D
  Height = 20
  Placement = pos=(-109,25,54) rot=(0,0,1;0rad)
  Radius = 1.5
FEATURE [Part::Box] Box966  label="Krychle966"
  AttacherType = Attacher::AttachEngine3D
  Height = 2
  Length = 6
  Placement = pos=(-112,4,60) rot=(0,0,1;0rad)
  Width = 6
FEATURE [Part::Box] Box967  label="Krychle967"
  AttacherType = Attacher::AttachEngine3D
  Height = 20
  Length = 20
  Placement = pos=(-106,4,56) rot=(0,0,1;0rad)
  Width = 80
FEATURE [Part::Box] Box968  label="Krychle968"
  AttacherType = Attacher::AttachEngine3D
  Height = 2
  Length = 6
  Placement = pos=(-112,22,60) rot=(0,0,1;0rad)
  Width = 6
FEATURE [Part::Box] Box969  label="Krychle969"
  AttacherType = Attacher::AttachEngine3D
  Height = 2
  Length = 6
  Placement = pos=(-86,22,60) rot=(0,0,1;0rad)
  Width = 6
FEATURE [Part::Cylinder] Cylinder1953  label="Válec1953"
  Angle = 360
  AttacherType = Attacher::AttachEngine3D
  Height = 20
  Placement = pos=(-83,25,54) rot=(0,0,1;0rad)
  Radius = 1.5
FEATURE [Part::Box] Box970  label="Krychle970"
  AttacherType = Attacher::AttachEngine3D
  Height = 2
  Length = 6
  Placement = pos=(-86,4,60) rot=(0,0,1;0rad)
  Width = 6
FEATURE [Part::Cylinder] Cylinder1954  label="Válec1954"
  Angle = 360
  AttacherType = Attacher::AttachEngine3D
  Height = 20
  Placement = pos=(-83,7,54) rot=(0,0,1;0rad)
  Radius = 1.5
FEATURE [Part::Box] Box971  label="Krychle971"
  AttacherType = Attacher::AttachEngine3D
  Height = 26
  Length = 38
  Placement = pos=(-112,0,56) rot=(0,0,1;0rad)
  Width = 32
FEATURE [Part::Cylinder] Cylinder1955  label="Válec1955"
  Angle = 360
  AttacherType = Attacher::AttachEngine3D
  Height = 3
  Placement = pos=(-112,16,66) rot=(0,1,0;1.5708rad)
  Radius = 5
FEATURE [Part::Cylinder] Cylinder1956  label="Válec1956"
  Angle = 360
  AttacherType = Attacher::AttachEngine3D
  Height = 20
  Placement = pos=(-117,16,66) rot=(0,1,0;1.5708rad)
  Radius = 2.5
FEATURE [Part::Box] Box972  label="Krychle972"
  AttacherType = Attacher::AttachEngine3D
  Height = 6
  Length = 68
  Placement = pos=(-130,-24,76) rot=(0,0,1;0rad)
  Width = 56
FEATURE [Part::Cylinder] Cylinder1957  label="Válec1957"
  Angle = 360
  AttacherType = Attacher::AttachEngine3D
  Height = 32
  Placement = pos=(0,0,66) rot=(0,0,1;0rad)
  Radius = 74
FEATURE [Part::Cylinder] Cylinder1958  label="Válec1958"
  Angle = 360
  AttacherType = Attacher::AttachEngine3D
  Height = 20
  Placement = pos=(-90,-10,66) rot=(0,0,1;0rad)
  Radius = 2.5
FEATURE [Part::Cylinder] Cylinder1959  label="Válec1959"
  Angle = 360
  AttacherType = Attacher::AttachEngine3D
  Height = 20
  Placement = pos=(-110,-10,66) rot=(0,0,1;0rad)
  Radius = 2.5
FEATURE [Part::Box] Box973  label="Krychle973"
  AttacherType = Attacher::AttachEngine3D
  Height = 55
  Length = 148
  Placement = pos=(-74,0,29) rot=(0,0,1;0rad)
  Width = 74
FEATURE [Part::Box] Box974  label="Krychle974"
  AttacherType = Attacher::AttachEngine3D
  Height = 55
  Length = 148
  Placement = pos=(-74,0,29) rot=(0,0,1;0rad)
  Width = 74
FEATURE [Part::Cylinder] Cylinder1960  label="Válec1960"
  Angle = 360
  AttacherType = Attacher::AttachEngine3D
  Height = 60
  Placement = pos=(0,0,26) rot=(0,0,1;0rad)
  Radius = 74
FEATURE [Part::Cylinder] Cylinder1961  label="Válec1961"
  Angle = 360
  AttacherType = Attacher::AttachEngine3D
  Height = 40
  Placement = pos=(-86,-10,69) rot=(0,1,0;1.5708rad)
  Radius = 2.5
FEATURE [Part::Box] Box975  label="Krychle975"
  AttacherType = Attacher::AttachEngine3D
  Height = 20
  Length = 80
  Placement = pos=(-138.7,-24,54.35) rot=(0,1,0;0.349066rad)
  Width = 6
FEATURE [Part::Box] Box976  label="Krychle976"
  AttacherType = Attacher::AttachEngine3D
  Height = 49
  Length = 44
  Placement = pos=(-93,-24,29) rot=(0,0,1;0rad)
  Width = 6
FEATURE [Part::Box] Box977  label="Krychle977"
  AttacherType = Attacher::AttachEngine3D
  Height = 32
  Length = 57
  Placement = pos=(-130,-24,52) rot=(0,0,1;0rad)
  Width = 6
FEATURE [Part::Cut] Cut649
  Base = -> Box977
  Tool = -> Box975
FEATURE [Part::Box] Box978  label="Krychle978"
  AttacherType = Attacher::AttachEngine3D
  Height = 20
  Length = 80
  Placement = pos=(-118.17,-24,82.63) rot=(0,1,0;1.24616rad)
  Width = 6
FEATURE [Part::Cylinder] Cylinder1962  label="Válec1962"
  Angle = 360
  AttacherType = Attacher::AttachEngine3D
  Height = 60
  Placement = pos=(0,0,26) rot=(0,0,1;0rad)
  Radius = 74
FEATURE [Part::Cylinder] Cylinder1963  label="Válec1963"
  Angle = 360
  AttacherType = Attacher::AttachEngine3D
  Height = 60
  Placement = pos=(0,0,26) rot=(0,0,1;0rad)
  Radius = 74
FEATURE [Part::Cut] Cut650
  Base = -> Cut649
  Tool = -> Cylinder1963
FEATURE [Part::Cut] Cut652
  Base = -> Box972
  Tool = -> Cylinder1957
FEATURE [Part::Cut] Cut658
  Base = -> Box971
  Tool = -> Box967
FEATURE [Part::Box] Box979  label="Krychle979"
  AttacherType = Attacher::AttachEngine3D
  Height = 49
  Length = 10
  Placement = pos=(-79,-24,29) rot=(0,0,1;0rad)
  Width = 56
FEATURE [Part::Cylinder] Cylinder1964  label="Válec1964"
  Angle = 360
  AttacherType = Attacher::AttachEngine3D
  Height = 40
  Placement = pos=(-86,-10,39) rot=(0,1,0;1.5708rad)
  Radius = 2.5
FEATURE [Part::Cylinder] Cylinder1965  label="Válec1965"
  Angle = 360
  AttacherType = Attacher::AttachEngine3D
  Height = 40
  Placement = pos=(-86,20,39) rot=(0,1,0;1.5708rad)
  Radius = 2.5
FEATURE [Part::Compound] Compound1056
  Links = -> [Box966,Box968,Box970,Box969]
FEATURE [Part::Compound] Compound1058
  Links = -> [Cylinder1954,Cylinder1953,Cylinder1951,Cylinder1952]
FEATURE [Part::Compound] Compound1059
  Links = -> [Cylinder1959,Cylinder1958]
  Placement = pos=(-8,0,0) rot=(0,0,1;0rad)
FEATURE [Part::Cut] Cut653
  Base = -> Cut652
  Placement = pos=(0,0,2) rot=(0,0,1;0rad)
  Tool = -> Compound1059
FEATURE [Part::Chamfer] Chamfer069
  Base = -> Cut653
  Edges = 1 edges r=20: [Edge3]
FEATURE [Part::Cut] Cut657
  Base = -> Chamfer069
  Tool = -> Box973
FEATURE [Part::Chamfer] Chamfer071
  Base = -> Box979
  Edges = 1 edges r=3: [Edge3]
FEATURE [Part::Cut] Cut660
  Base = -> Cut658
  Tool = -> Compound1056
FEATURE [Part::Cut] Cut654
  Base = -> Cut660
  Tool = -> Compound1058
FEATURE [Part::Cut] Cut655
  Base = -> Cut654
  Tool = -> Cylinder1956
FEATURE [Part::Cut] Cut651
  Base = -> Cut655
  Tool = -> Cylinder1955
FEATURE [Part::Chamfer] Chamfer070
  Base = -> Cut651
  Edges = 1 edges r=2: [Edge4]
  Placement = pos=(0,0,2) rot=(0,0,1;0rad)
FEATURE [Part::Cut] Cut661
  Base = -> Box976
  Tool = -> Box978
FEATURE [Part::Cut] Cut656
  Base = -> Cut661
  Tool = -> Cylinder1962
FEATURE [Part::Compound] Compound1055
  Links = -> [Cut650,Cut656]
FEATURE [Part::Cylinder] Cylinder1966  label="Válec1966"
  Angle = 360
  AttacherType = Attacher::AttachEngine3D
  Height = 40
  Placement = pos=(-90,16,68) rot=(0,1,0;1.5708rad)
  Radius = 2.5
FEATURE [Part::Cut] Cut645
  Base = -> Chamfer070
  Tool = -> Cylinder1966
FEATURE [Part::Cylinder] Cylinder1967  label="Válec1967"
  Angle = 360
  AttacherType = Attacher::AttachEngine3D
  Height = 40
  Placement = pos=(-86,16,68) rot=(0,1,0;1.5708rad)
  Radius = 2.5
FEATURE [Part::Compound] Compound1057
  Links = -> [Cylinder1964,Cylinder1965,Cylinder1961,Cylinder1967]
FEATURE [Part::Cut] Cut647
  Base = -> Chamfer071
  Tool = -> Compound1057
FEATURE [Part::Cut] Cut648
  Base = -> Cut647
  Tool = -> Cylinder1960
FEATURE [Part::Cut] Cut659
  Base = -> Cut648
  Tool = -> Box974
FEATURE [Part::Cylinder] Cylinder1968  label="Válec1968"
  Angle = 360
  AttacherType = Attacher::AttachEngine3D
  Height = 5
  Placement = pos=(-86,16,68) rot=(0,1,0;1.5708rad)
  Radius = 5
FEATURE [Part::Cut] Cut646
  Base = -> Cut645
  Tool = -> Cylinder1968
FEATURE [Part::Compound] Compound1060  label="Base_balancer-side-wide001"
  Links = -> [Cut657,Compound1055,Cut646,Cut659]
FEATURE [Part::Mirroring] mirror017  label="Base_balancer-side-wide_opposite"
  Base = (0,0,0)
  Normal = (1,0,0)
  Source = -> Compound1060
FEATURE [Part::FeaturePython] Tube  label="ZKL-51115A-NF"  # WARN: FeaturePython — macro-defined, semantics opaque (R4)
  AttacherType = Attacher::AttachEngine3D
  Height = 19
  InnerRadius = 37.5
  OuterRadius = 50
  Placement = pos=(0,0,59) rot=(0,0,1;0rad)
FEATURE [Part::FeaturePython] Tube049  label="ZKL-51117A-NF"  # WARN: FeaturePython — macro-defined, semantics opaque (R4)
  AttacherType = Attacher::AttachEngine3D
  Height = 19
  InnerRadius = 42.5
  OuterRadius = 55
  Placement = pos=(0,0,59) rot=(0,0,1;0rad)
FEATURE [Part::FeaturePython] Tube050  label="ZKL-51118A-NF"  # WARN: FeaturePython — macro-defined, semantics opaque (R4)
  AttacherType = Attacher::AttachEngine3D
  Height = 22
  InnerRadius = 45
  OuterRadius = 60
  Placement = pos=(0,0,56) rot=(0,0,1;0rad)
FEATURE [Part::Box] Box980  label="Krychle980"
  AttacherType = Attacher::AttachEngine3D
  Height = 50
  Length = 42
  Placement = pos=(-21.0011,60.0051,31) rot=(0,0,1;0rad)
  Width = 72
FEATURE [Part::Compound] Compound1061
  Links = -> [Box980]
  Placement = pos=(0,0,1) rot=(0,0,1;3.92699rad)
FEATURE [Part::Box] Box981  label="Krychle981"
  AttacherType = Attacher::AttachEngine3D
  Height = 9
  Length = 54
  Placement = pos=(-27.0044,59.998,75) rot=(0,0,1;0rad)
  Width = 78
FEATURE [Part::Compound] Compound1062
  Links = -> [Box981]
  Placement = pos=(0,0,0) rot=(0,0,1;3.92699rad)
FEATURE [Part::Cylinder] Cylinder1969  label="Válec1969"
  Angle = 360
  AttacherType = Attacher::AttachEngine3D
  Height = 40
  Placement = pos=(0,0,44) rot=(0,0,1;0rad)
  Radius = 74
FEATURE [Part::Cut] Cut662
  Base = -> Compound1062
  Tool = -> Compound1061
FEATURE [Part::Cut] Cut663
  Base = -> Cut662
  Tool = -> Cylinder1969
FEATURE [Part::Chamfer] Chamfer072
  Base = -> Cut663
  Edges = 2 edges r=3: [Edge2,Edge9]
FEATURE [Part::Cylinder] Cylinder1970  label="Válec1970"
  Angle = 360
  AttacherType = Attacher::AttachEngine3D
  Height = 60
  Placement = pos=(-15,125,-80) rot=(0,0,1;0rad)
  Radius = 1.5
FEATURE [Part::Cylinder] Cylinder1971  label="Válec1971"
  Angle = 360
  AttacherType = Attacher::AttachEngine3D
  Height = 60
  Placement = pos=(15,125,-80) rot=(0,0,1;0rad)
  Radius = 1.5
FEATURE [Part::Cylinder] Cylinder1972  label="Válec1972"
  Angle = 360
  AttacherType = Attacher::AttachEngine3D
  Height = 60
  Placement = pos=(24,73,-80) rot=(0,0,1;0rad)
  Radius = 1.5
FEATURE [Part::Cylinder] Cylinder1973  label="Válec1973"
  Angle = 360
  AttacherType = Attacher::AttachEngine3D
  Height = 60
  Placement = pos=(-24,73,-80) rot=(0,0,1;0rad)
  Radius = 1.5
FEATURE [Part::Compound] Compound1063
  Links = -> [Cylinder1972,Cylinder1973,Cylinder1970,Cylinder1971]
  Placement = pos=(0,0,100) rot=(0,0,1;3.92699rad)
FEATURE [Part::Cylinder] Cylinder1974  label="Válec1974"
  Angle = 360
  AttacherType = Attacher::AttachEngine3D
  Height = 3
  Placement = pos=(-15,135,-80) rot=(0,0,1;0rad)
  Radius = 3
FEATURE [Part::Cylinder] Cylinder1975  label="Válec1975"
  Angle = 360
  AttacherType = Attacher::AttachEngine3D
  Height = 3
  Placement = pos=(15,135,-80) rot=(0,0,1;0rad)
  Radius = 3
FEATURE [Part::Cylinder] Cylinder1976  label="Válec1976"
  Angle = 360
  AttacherType = Attacher::AttachEngine3D
  Height = 3
  Placement = pos=(24,74,-80) rot=(0,0,1;0rad)
  Radius = 3
FEATURE [Part::Cylinder] Cylinder1977  label="Válec1977"
  Angle = 360
  AttacherType = Attacher::AttachEngine3D
  Height = 3
  Placement = pos=(-24,74,-80) rot=(0,0,1;0rad)
  Radius = 3
FEATURE [Part::Compound] Compound1064
  Links = -> [Cylinder1976,Cylinder1977,Cylinder1974,Cylinder1975]
  Placement = pos=(0,0,135) rot=(0,0,1;3.92699rad)
FEATURE [Part::Box] Box982  label="Krychle982"
  AttacherType = Attacher::AttachEngine3D
  Height = 50
  Length = 42
  Placement = pos=(-21.0011,60.0051,31) rot=(0,0,1;0rad)
  Width = 62
FEATURE [Part::Compound] Compound1065
  Links = -> [Box982]
  Placement = pos=(0,0,0) rot=(0,0,1;3.92699rad)
FEATURE [Part::Box] Box983  label="Krychle983"
  AttacherType = Attacher::AttachEngine3D
  Height = 10
  Length = 54
  Placement = pos=(-27.0044,59.998,75) rot=(0,0,1;0rad)
  Width = 68
FEATURE [Part::Compound] Compound1066
  Links = -> [Box983]
  Placement = pos=(0,0,-20) rot=(0,0,1;3.92699rad)
FEATURE [Part::Cut] Cut666
  Base = -> Compound1066
  Tool = -> Compound1065
FEATURE [Part::Cylinder] Cylinder1978  label="Válec1978"
  Angle = 360
  AttacherType = Attacher::AttachEngine3D
  Height = 60
  Placement = pos=(-15,135,-80) rot=(0,0,1;0rad)
  Radius = 1.5
FEATURE [Part::Cylinder] Cylinder1979  label="Válec1979"
  Angle = 360
  AttacherType = Attacher::AttachEngine3D
  Height = 60
  Placement = pos=(15,135,-80) rot=(0,0,1;0rad)
  Radius = 1.5
FEATURE [Part::Cylinder] Cylinder1980  label="Válec1980"
  Angle = 360
  AttacherType = Attacher::AttachEngine3D
  Height = 60
  Placement = pos=(24,74,-80) rot=(0,0,1;0rad)
  Radius = 1.5
FEATURE [Part::Cylinder] Cylinder1981  label="Válec1981"
  Angle = 360
  AttacherType = Attacher::AttachEngine3D
  Height = 60
  Placement = pos=(-24,74,-80) rot=(0,0,1;0rad)
  Radius = 1.5
FEATURE [Part::Compound] Compound1067
  Links = -> [Cylinder1980,Cylinder1981,Cylinder1978,Cylinder1979]
  Placement = pos=(0,0,100) rot=(0,0,1;3.92699rad)
FEATURE [Part::Cylinder] Cylinder1982  label="Válec1982"
  Angle = 360
  AttacherType = Attacher::AttachEngine3D
  Height = 40
  Placement = pos=(0,0,44) rot=(0,0,1;0rad)
  Radius = 74
FEATURE [Part::Box] Box984  label="Krychle984"
  AttacherType = Attacher::AttachEngine3D
  Height = 10
  Length = 42
  Placement = pos=(-21,-23,22) rot=(0,0,1;0rad)
  Width = 8
FEATURE [Part::Compound] Compound1068
  Links = -> [Box984]
  Placement = pos=(63.64,-63.64,43) rot=(0,0,1;3.92699rad)
FEATURE [Part::Cylinder] Cylinder1983  label="Válec1983"
  Angle = 360
  AttacherType = Attacher::AttachEngine3D
  Height = 40
  Placement = pos=(0,0,44) rot=(0,0,1;0rad)
  Radius = 74
FEATURE [Part::Cut] Cut667
  Base = -> Compound1068
  Placement = pos=(0,0,-10) rot=(0,0,1;0rad)
  Tool = -> Cylinder1983
FEATURE [Part::Cylinder] Cylinder1984  label="Válec1984"
  Angle = 360
  AttacherType = Attacher::AttachEngine3D
  Height = 50
  Placement = pos=(9,100,59) rot=(1,0,0;1.5708rad)
  Radius = 1.5
FEATURE [Part::Compound] Compound1069
  Links = -> [Cylinder1984]
  Placement = pos=(0,0,0) rot=(0,0,1;3.92699rad)
FEATURE [Part::Cylinder] Cylinder1985  label="Válec1985"
  Angle = 360
  AttacherType = Attacher::AttachEngine3D
  Height = 50
  Placement = pos=(-9,100,59) rot=(1,0,0;1.5708rad)
  Radius = 1.5
FEATURE [Part::Compound] Compound1070
  Links = -> [Cylinder1985]
  Placement = pos=(0,0,0) rot=(0,0,1;3.92699rad)
FEATURE [Part::Compound] Compound1071
  Links = -> [Compound1070,Compound1069]
  Placement = pos=(0,0,1) rot=(0,0,1;0rad)
FEATURE [Part::Cut] Cut668
  Base = -> Cut667
  Tool = -> Compound1071
FEATURE [Part::Cut] Cut669
  Base = -> Cut666
  Tool = -> Cylinder1982
FEATURE [Part::Chamfer] Chamfer073
  Base = -> Cut669
  Edges = 2 edges r=3: [Edge2,Edge13]
FEATURE [Part::Chamfer] Chamfer074
  Base = -> Chamfer073
  Edges = 2 edges r=2: [Edge3,Edge22]
FEATURE [Part::Chamfer] Chamfer075
  Base = -> Chamfer074
  Edges = 1 edges r=1: [Edge27]
FEATURE [Part::Cut] Cut665
  Base = -> Chamfer075
  Tool = -> Compound1067
FEATURE [Part::Cut] Cut664
  Base = -> Cut665
  Tool = -> Compound1064
FEATURE [Part::Box] Box985  label="Krychle985"
  AttacherType = Attacher::AttachEngine3D
  Height = 50
  Length = 42
  Placement = pos=(-21.0011,60.0051,31) rot=(0,0,1;0rad)
  Width = 72
FEATURE [Part::Box] Box986  label="Krychle986"
  AttacherType = Attacher::AttachEngine3D
  Height = 10
  Length = 54
  Placement = pos=(-27.0044,59.998,75) rot=(0,0,1;0rad)
  Width = 78
FEATURE [Part::Cylinder] Cylinder1986  label="Válec1986"
  Angle = 360
  AttacherType = Attacher::AttachEngine3D
  Height = 40
  Placement = pos=(0,0,44) rot=(0,0,1;0rad)
  Radius = 74
FEATURE [Part::Compound] Compound1072
  Links = -> [Box985]
  Placement = pos=(0,0,0) rot=(0,0,1;3.92699rad)
FEATURE [Part::Compound] Compound1073
  Links = -> [Box986]
  Placement = pos=(0,0,-20) rot=(0,0,1;3.92699rad)
FEATURE [Part::Cut] Cut670
  Base = -> Compound1073
  Tool = -> Compound1072
FEATURE [Part::Cut] Cut671
  Base = -> Cut670
  Tool = -> Cylinder1986
FEATURE [Part::Cylinder] Cylinder1987  label="Válec1987"
  Angle = 360
  AttacherType = Attacher::AttachEngine3D
  Height = 3
  Placement = pos=(-15,135,-80) rot=(0,0,1;0rad)
  Radius = 3
FEATURE [Part::Cylinder] Cylinder1988  label="Válec1988"
  Angle = 360
  AttacherType = Attacher::AttachEngine3D
  Height = 3
  Placement = pos=(15,135,-80) rot=(0,0,1;0rad)
  Radius = 3
FEATURE [Part::Cylinder] Cylinder1989  label="Válec1989"
  Angle = 360
  AttacherType = Attacher::AttachEngine3D
  Height = 3
  Placement = pos=(24,74,-80) rot=(0,0,1;0rad)
  Radius = 3
FEATURE [Part::Cylinder] Cylinder1990  label="Válec1990"
  Angle = 360
  AttacherType = Attacher::AttachEngine3D
  Height = 3
  Placement = pos=(-24,74,-80) rot=(0,0,1;0rad)
  Radius = 3
FEATURE [Part::Cylinder] Cylinder1991  label="Válec1991"
  Angle = 360
  AttacherType = Attacher::AttachEngine3D
  Height = 60
  Placement = pos=(-15,135,-80) rot=(0,0,1;0rad)
  Radius = 1.5
FEATURE [Part::Cylinder] Cylinder1992  label="Válec1992"
  Angle = 360
  AttacherType = Attacher::AttachEngine3D
  Height = 60
  Placement = pos=(15,135,-80) rot=(0,0,1;0rad)
  Radius = 1.5
FEATURE [Part::Cylinder] Cylinder1993  label="Válec1993"
  Angle = 360
  AttacherType = Attacher::AttachEngine3D
  Height = 60
  Placement = pos=(24,74,-80) rot=(0,0,1;0rad)
  Radius = 1.5
FEATURE [Part::Cylinder] Cylinder1994  label="Válec1994"
  Angle = 360
  AttacherType = Attacher::AttachEngine3D
  Height = 60
  Placement = pos=(-24,74,-80) rot=(0,0,1;0rad)
  Radius = 1.5
FEATURE [Part::Compound] Compound1074
  Links = -> [Cylinder1993,Cylinder1994,Cylinder1991,Cylinder1992]
  Placement = pos=(0,0,100) rot=(0,0,1;3.92699rad)
FEATURE [Part::Compound] Compound1075
  Links = -> [Cylinder1989,Cylinder1990,Cylinder1987,Cylinder1988]
  Placement = pos=(0,0,135) rot=(0,0,1;3.92699rad)
FEATURE [Part::Box] Box987  label="Krychle987"
  AttacherType = Attacher::AttachEngine3D
  Height = 10
  Length = 42
  Placement = pos=(-21,-23,22) rot=(0,0,1;0rad)
  Width = 10
FEATURE [Part::Compound] Compound1076
  Links = -> [Box987]
  Placement = pos=(63.64,-63.64,43) rot=(0,0,1;3.92699rad)
FEATURE [Part::Cylinder] Cylinder1995  label="Válec1995"
  Angle = 360
  AttacherType = Attacher::AttachEngine3D
  Height = 40
  Placement = pos=(0,0,44) rot=(0,0,1;0rad)
  Radius = 74
FEATURE [Part::Cut] Cut672
  Base = -> Compound1076
  Placement = pos=(0,0,-10) rot=(0,0,1;0rad)
  Tool = -> Cylinder1995
FEATURE [Part::Cylinder] Cylinder1996  label="Válec1996"
  Angle = 360
  AttacherType = Attacher::AttachEngine3D
  Height = 50
  Placement = pos=(9,100,59) rot=(1,0,0;1.5708rad)
  Radius = 1.5
FEATURE [Part::Compound] Compound1077
  Links = -> [Cylinder1996]
  Placement = pos=(0,0,0) rot=(0,0,1;3.92699rad)
FEATURE [Part::Cylinder] Cylinder1997  label="Válec1997"
  Angle = 360
  AttacherType = Attacher::AttachEngine3D
  Height = 50
  Placement = pos=(-9,100,59) rot=(1,0,0;1.5708rad)
  Radius = 1.5
FEATURE [Part::Compound] Compound1078
  Links = -> [Cylinder1997]
  Placement = pos=(0,0,0) rot=(0,0,1;3.92699rad)
FEATURE [Part::Compound] Compound1079
  Links = -> [Compound1078,Compound1077]
  Placement = pos=(0,0,1) rot=(0,0,1;0rad)
FEATURE [Part::Cut] Cut673
  Base = -> Cut672
  Tool = -> Compound1079
FEATURE [Part::Cylinder] Cylinder1998  label="Válec1998"
  Angle = 360
  AttacherType = Attacher::AttachEngine3D
  Height = 60
  Placement = pos=(-15,135,-80) rot=(0,0,1;0rad)
  Radius = 1.5
FEATURE [Part::Cylinder] Cylinder1999  label="Válec1999"
  Angle = 360
  AttacherType = Attacher::AttachEngine3D
  Height = 60
  Placement = pos=(15,135,-80) rot=(0,0,1;0rad)
  Radius = 1.5
FEATURE [Part::Cylinder] Cylinder2000  label="Válec2000"
  Angle = 360
  AttacherType = Attacher::AttachEngine3D
  Height = 60
  Placement = pos=(24,74,-80) rot=(0,0,1;0rad)
  Radius = 1.5
FEATURE [Part::Cylinder] Cylinder2001  label="Válec2001"
  Angle = 360
  AttacherType = Attacher::AttachEngine3D
  Height = 60
  Placement = pos=(-24,74,-80) rot=(0,0,1;0rad)
  Radius = 1.5
FEATURE [Part::Compound] Compound1080
  Links = -> [Cylinder2000,Cylinder2001,Cylinder1998,Cylinder1999]
  Placement = pos=(0,0,100) rot=(0,0,1;3.92699rad)
FEATURE [Part::Cut] Cut674
  Base = -> Cut530
  Tool = -> Compound1080
FEATURE [Part::Chamfer] Chamfer076
  Base = -> Cut671
  Edges = 2 edges r=3: [Edge2,Edge13]
FEATURE [Part::Chamfer] Chamfer077
  Base = -> Chamfer076
  Edges = 5 edges r=3: [Edge3,Edge14,Edge22,Edge23,Edge24]
FEATURE [Part::Cut] Cut675
  Base = -> Chamfer077
  Tool = -> Compound1075
FEATURE [Part::Cut] Cut676
  Base = -> Cut675
  Tool = -> Compound1074
FEATURE [Part::Cylinder] Cylinder2002  label="Válec2002"
  Angle = 360
  AttacherType = Attacher::AttachEngine3D
  Height = 60
  Placement = pos=(-15,135,-80) rot=(0,0,1;0rad)
  Radius = 1.5
FEATURE [Part::Cylinder] Cylinder2003  label="Válec2003"
  Angle = 360
  AttacherType = Attacher::AttachEngine3D
  Height = 60
  Placement = pos=(15,135,-80) rot=(0,0,1;0rad)
  Radius = 1.5
FEATURE [Part::Cylinder] Cylinder2004  label="Válec2004"
  Angle = 360
  AttacherType = Attacher::AttachEngine3D
  Height = 60
  Placement = pos=(24,74,-80) rot=(0,0,1;0rad)
  Radius = 1.5
FEATURE [Part::Cylinder] Cylinder2005  label="Válec2005"
  Angle = 360
  AttacherType = Attacher::AttachEngine3D
  Height = 60
  Placement = pos=(-24,74,-80) rot=(0,0,1;0rad)
  Radius = 1.5
FEATURE [Part::Compound] Compound1081
  Links = -> [Cylinder2004,Cylinder2005,Cylinder2002,Cylinder2003]
  Placement = pos=(0,0,109) rot=(0,0,1;3.92699rad)
FEATURE [Part::Cut] Cut677
  Base = -> Chamfer072
  Tool = -> Compound1081
FEATURE [Part::Compound] Compound1082  label="Base_encoder-tophold"
  Links = -> [Cut673,Cut676]
FEATURE [Part::Compound] Compound1083  label="Base_encoder-lowhold"
  Links = -> [Cut527,Cut677,Cut674]
FEATURE [Mesh::Feature] Mesh001  label="Base_encoder-tophold (Meshed)"
FEATURE [Mesh::Feature] Mesh002  label="Base_encoder-lowhold (Meshed)"
FEATURE [Part::FeaturePython] Tube051  label="ring"  # WARN: FeaturePython — macro-defined, semantics opaque (R4)
  AttacherType = Attacher::AttachEngine3D
  Height = 22
  InnerRadius = 65.1
  OuterRadius = 74
  Placement = pos=(0,0,3) rot=(0,0,1;0rad)
FEATURE [Part::FeaturePython] Tube052  label="ring001"  # WARN: FeaturePython — macro-defined, semantics opaque (R4)
  AttacherType = Attacher::AttachEngine3D
  Height = 4
  InnerRadius = 60
  OuterRadius = 74
  Placement = pos=(0,0,25) rot=(0,0,1;0rad)
FEATURE [Part::Cylinder] Cylinder2006  label="Válec2006"
  Angle = 360
  AttacherType = Attacher::AttachEngine3D
  Height = 72
  Placement = pos=(61.4878,-35.5,0) rot=(0,0,1;1.0472rad)
  Radius = 1.5
FEATURE [Part::Cylinder] Cylinder2007  label="Válec2007"
  Angle = 360
  AttacherType = Attacher::AttachEngine3D
  Height = 72
  Placement = pos=(35.5,-61.4878,0) rot=(0,0,1;0.523599rad)
  Radius = 1.5
FEATURE [Part::Cylinder] Cylinder2008  label="Válec2008"
  Angle = 360
  AttacherType = Attacher::AttachEngine3D
  Height = 72
  Placement = pos=(-61.4878,-35.5,0) rot=(0,0,-1;1.0472rad)
  Radius = 1.5
FEATURE [Part::Cylinder] Cylinder2009  label="Válec2009"
  Angle = 360
  AttacherType = Attacher::AttachEngine3D
  Height = 72
  Placement = pos=(0,-71,0) rot=(0,0,1;0rad)
  Radius = 1.5
FEATURE [Part::Cylinder] Cylinder2010  label="Válec2010"
  Angle = 360
  AttacherType = Attacher::AttachEngine3D
  Height = 72
  Placement = pos=(3.1e-14,71,0) rot=(0,0,1;3.14159rad)
  Radius = 1.5
FEATURE [Part::Cylinder] Cylinder2011  label="Válec2011"
  Angle = 360
  AttacherType = Attacher::AttachEngine3D
  Height = 72
  Placement = pos=(71,-1.8e-14,0) rot=(0,0,1;1.5708rad)
  Radius = 1.5
FEATURE [Part::Cylinder] Cylinder2012  label="Válec2012"
  Angle = 360
  AttacherType = Attacher::AttachEngine3D
  Height = 72
  Placement = pos=(61.4878,35.5,0) rot=(0,0,1;2.0944rad)
  Radius = 1.5
FEATURE [Part::Cylinder] Cylinder2013  label="Válec2013"
  Angle = 360
  AttacherType = Attacher::AttachEngine3D
  Height = 72
  Placement = pos=(35.5,61.4878,0) rot=(0,0,1;2.61799rad)
  Radius = 1.5
FEATURE [Part::Cylinder] Cylinder2014  label="Válec2014"
  Angle = 360
  AttacherType = Attacher::AttachEngine3D
  Height = 72
  Placement = pos=(-35.5,-61.4878,0) rot=(0,0,-1;0.523599rad)
  Radius = 1.5
FEATURE [Part::Cylinder] Cylinder2015  label="Válec2015"
  Angle = 360
  AttacherType = Attacher::AttachEngine3D
  Height = 72
  Placement = pos=(-71,2.7e-14,0) rot=(0,0,-1;1.5708rad)
  Radius = 1.5
FEATURE [Part::Cylinder] Cylinder2016  label="Válec2016"
  Angle = 360
  AttacherType = Attacher::AttachEngine3D
  Height = 72
  Placement = pos=(-61.4878,35.5,0) rot=(0,0,1;4.18879rad)
  Radius = 1.5
FEATURE [Part::Cylinder] Cylinder2017  label="Válec2017"
  Angle = 360
  AttacherType = Attacher::AttachEngine3D
  Height = 72
  Placement = pos=(-35.5,61.4878,0) rot=(0,0,1;3.66519rad)
  Radius = 1.5
FEATURE [Part::Compound] Compound1084
  Links = -> [Cylinder2009,Cylinder2007,Cylinder2006,Cylinder2011,Cylinder2012,Cylinder2013,Cylinder2010,Cylinder2017,Cylinder2016,Cylinder2015,Cylinder2008,Cylinder2014]
  Placement = pos=(0,0,-4) rot=(0,0,1;0rad)
FEATURE [Part::Cylinder] Cylinder2018  label="Válec2018"
  Angle = 360
  AttacherType = Attacher::AttachEngine3D
  Height = 72
  Placement = pos=(61.4878,-35.5,0) rot=(0,0,1;1.0472rad)
  Radius = 1.5
FEATURE [Part::Cylinder] Cylinder2019  label="Válec2019"
  Angle = 360
  AttacherType = Attacher::AttachEngine3D
  Height = 72
  Placement = pos=(35.5,-61.4878,0) rot=(0,0,1;0.523599rad)
  Radius = 1.5
FEATURE [Part::Cylinder] Cylinder2020  label="Válec2020"
  Angle = 360
  AttacherType = Attacher::AttachEngine3D
  Height = 72
  Placement = pos=(-61.4878,-35.5,0) rot=(0,0,-1;1.0472rad)
  Radius = 1.5
FEATURE [Part::Cylinder] Cylinder2021  label="Válec2021"
  Angle = 360
  AttacherType = Attacher::AttachEngine3D
  Height = 72
  Placement = pos=(0,-71,0) rot=(0,0,1;0rad)
  Radius = 1.5
FEATURE [Part::Cylinder] Cylinder2022  label="Válec2022"
  Angle = 360
  AttacherType = Attacher::AttachEngine3D
  Height = 72
  Placement = pos=(3.1e-14,71,0) rot=(0,0,1;3.14159rad)
  Radius = 1.5
FEATURE [Part::Cylinder] Cylinder2023  label="Válec2023"
  Angle = 360
  AttacherType = Attacher::AttachEngine3D
  Height = 72
  Placement = pos=(71,-1.8e-14,0) rot=(0,0,1;1.5708rad)
  Radius = 1.5
FEATURE [Part::Cylinder] Cylinder2024  label="Válec2024"
  Angle = 360
  AttacherType = Attacher::AttachEngine3D
  Height = 72
  Placement = pos=(61.4878,35.5,0) rot=(0,0,1;2.0944rad)
  Radius = 1.5
FEATURE [Part::Cylinder] Cylinder2025  label="Válec2025"
  Angle = 360
  AttacherType = Attacher::AttachEngine3D
  Height = 72
  Placement = pos=(35.5,61.4878,0) rot=(0,0,1;2.61799rad)
  Radius = 1.5
FEATURE [Part::Cylinder] Cylinder2026  label="Válec2026"
  Angle = 360
  AttacherType = Attacher::AttachEngine3D
  Height = 72
  Placement = pos=(-61.4878,35.5,0) rot=(0,0,1;4.18879rad)
  Radius = 1.5
FEATURE [Part::Cylinder] Cylinder2027  label="Válec2027"
  Angle = 360
  AttacherType = Attacher::AttachEngine3D
  Height = 72
  Placement = pos=(-35.5,61.4878,0) rot=(0,0,1;3.66519rad)
  Radius = 1.5
FEATURE [Part::Cylinder] Cylinder2028  label="Válec2028"
  Angle = 360
  AttacherType = Attacher::AttachEngine3D
  Height = 72
  Placement = pos=(-35.5,-61.4878,0) rot=(0,0,-1;0.523599rad)
  Radius = 1.5
FEATURE [Part::Cylinder] Cylinder2029  label="Válec2029"
  Angle = 360
  AttacherType = Attacher::AttachEngine3D
  Height = 72
  Placement = pos=(-71,2.7e-14,0) rot=(0,0,-1;1.5708rad)
  Radius = 1.5
FEATURE [Part::Compound] Compound1085
  Links = -> [Cylinder2021,Cylinder2019,Cylinder2018,Cylinder2023,Cylinder2024,Cylinder2025,Cylinder2022,Cylinder2027,Cylinder2026,Cylinder2029,Cylinder2020,Cylinder2028]
  Placement = pos=(0,0,-4) rot=(0,0,1;0rad)
FEATURE [Part::Cut] Cut678
  Base = -> Tube052
  Tool = -> Compound1084
FEATURE [Part::Cut] Cut679
  Base = -> Tube051
  Tool = -> Compound1085
FEATURE [Part::Cylinder] Cylinder2030  label="Válec2030"
  Angle = 360
  AttacherType = Attacher::AttachEngine3D
  Height = 32
  Placement = pos=(61.4878,-35.5,0) rot=(0,0,1;1.0472rad)
  Radius = 4
FEATURE [Part::Cylinder] Cylinder2031  label="Válec2031"
  Angle = 360
  AttacherType = Attacher::AttachEngine3D
  Height = 32
  Placement = pos=(35.5,-61.4878,0) rot=(0,0,1;0.523599rad)
  Radius = 4
FEATURE [Part::Cylinder] Cylinder2032  label="Válec2032"
  Angle = 360
  AttacherType = Attacher::AttachEngine3D
  Height = 32
  Placement = pos=(-61.4878,-35.5,0) rot=(0,0,-1;1.0472rad)
  Radius = 4
FEATURE [Part::Cylinder] Cylinder2033  label="Válec2033"
  Angle = 360
  AttacherType = Attacher::AttachEngine3D
  Height = 32
  Placement = pos=(0,-71,0) rot=(0,0,1;0rad)
  Radius = 4
FEATURE [Part::Cylinder] Cylinder2034  label="Válec2034"
  Angle = 360
  AttacherType = Attacher::AttachEngine3D
  Height = 32
  Placement = pos=(3.1e-14,71,0) rot=(0,0,1;3.14159rad)
  Radius = 4
FEATURE [Part::Cylinder] Cylinder2035  label="Válec2035"
  Angle = 360
  AttacherType = Attacher::AttachEngine3D
  Height = 32
  Placement = pos=(71,-1.8e-14,0) rot=(0,0,1;1.5708rad)
  Radius = 4
FEATURE [Part::Cylinder] Cylinder2036  label="Válec2036"
  Angle = 360
  AttacherType = Attacher::AttachEngine3D
  Height = 32
  Placement = pos=(61.4878,35.5,0) rot=(0,0,1;2.0944rad)
  Radius = 4
FEATURE [Part::Cylinder] Cylinder2037  label="Válec2037"
  Angle = 360
  AttacherType = Attacher::AttachEngine3D
  Height = 32
  Placement = pos=(35.5,61.4878,0) rot=(0,0,1;2.61799rad)
  Radius = 4
FEATURE [Part::Cylinder] Cylinder2038  label="Válec2038"
  Angle = 360
  AttacherType = Attacher::AttachEngine3D
  Height = 32
  Placement = pos=(-61.4878,35.5,0) rot=(0,0,1;4.18879rad)
  Radius = 4
FEATURE [Part::Cylinder] Cylinder2039  label="Válec2039"
  Angle = 360
  AttacherType = Attacher::AttachEngine3D
  Height = 32
  Placement = pos=(-35.5,61.4878,0) rot=(0,0,1;3.66519rad)
  Radius = 4
FEATURE [Part::Cylinder] Cylinder2040  label="Válec2040"
  Angle = 360
  AttacherType = Attacher::AttachEngine3D
  Height = 32
  Placement = pos=(-35.5,-61.4878,0) rot=(0,0,-1;0.523599rad)
  Radius = 4
FEATURE [Part::Cylinder] Cylinder2041  label="Válec2041"
  Angle = 360
  AttacherType = Attacher::AttachEngine3D
  Height = 32
  Placement = pos=(-71,2.7e-14,0) rot=(0,0,-1;1.5708rad)
  Radius = 4
FEATURE [Part::Compound] Compound1086
  Links = -> [Cylinder2033,Cylinder2031,Cylinder2030,Cylinder2035,Cylinder2036,Cylinder2037,Cylinder2034,Cylinder2039,Cylinder2038,Cylinder2041,Cylinder2032,Cylinder2040]
  Placement = pos=(0,0,-18) rot=(0,0,1;0rad)
FEATURE [Part::Cut] Cut680
  Base = -> Cut679
  Tool = -> Compound1086
FEATURE [Part::Box] Box176  label="Krychle176"
  AttacherType = Attacher::AttachEngine3D
  Height = 15
  Length = 148
  Placement = pos=(-74,0,16) rot=(0,0,1;0rad)
  Width = 48
FEATURE [Part::Cylinder] Cylinder485  label="Válec485"
  Angle = 360
  AttacherType = Attacher::AttachEngine3D
  Height = 15
  Placement = pos=(0,0,16) rot=(0,0,1;0rad)
  Radius = 74
FEATURE [Part::Cylinder] Cylinder482  label="Válec482"
  Angle = 360
  AttacherType = Attacher::AttachEngine3D
  Height = 15
  Placement = pos=(0,0,16) rot=(0,0,1;0rad)
  Radius = 74
FEATURE [Part::Cut] Cut185
  Base = -> Box176
  Tool = -> Cylinder482
FEATURE [Part::Cut] Cut188
  Base = -> Cut185
  Tool = -> Cylinder485
FEATURE [Part::Cylinder] Cylinder510  label="Válec510"
  Angle = 360
  AttacherType = Attacher::AttachEngine3D
  Height = 50
  Placement = pos=(-71,80,24) rot=(1,0,0;1.5708rad)
  Radius = 1.5
FEATURE [Part::Box] Box208  label="Krychle208"
  AttacherType = Attacher::AttachEngine3D
  Height = 6
  Length = 8
  Placement = pos=(67,38,21) rot=(0,0,1;0rad)
  Width = 2
FEATURE [Part::Cylinder] Cylinder509  label="Válec509"
  Angle = 360
  AttacherType = Attacher::AttachEngine3D
  Height = 50
  Placement = pos=(71,80,24) rot=(1,0,0;1.5708rad)
  Radius = 1.5
FEATURE [Part::Compound] Compound339
  Links = -> [Cylinder509,Cylinder510]
FEATURE [Part::Box] Box209  label="Krychle209"
  AttacherType = Attacher::AttachEngine3D
  Height = 6
  Length = 8
  Placement = pos=(-75,38,21) rot=(0,0,1;0rad)
  Width = 2
FEATURE [Part::Compound] Compound338
  Links = -> [Box208,Box209]
FEATURE [Part::Cut] Cut681
  Base = -> Cut188
  Tool = -> Compound338
FEATURE [Part::Cut] Cut682
  Base = -> Cut681
  Placement = pos=(0,0,-2) rot=(0,0,1;0rad)
  Tool = -> Compound339
FEATURE [Part::Box] Box179  label="Krychle179"
  AttacherType = Attacher::AttachEngine3D
  Height = 47
  Length = 56
  Placement = pos=(-28,0,27) rot=(0,0,1;0rad)
  Width = 200
FEATURE [Part::Cut] Cut683
  Base = -> Cut678
  Tool = -> Box179
FEATURE [Part::FeaturePython] Tube032  # WARN: FeaturePython — macro-defined, semantics opaque (R4)
  AttacherType = Attacher::AttachEngine3D
  Height = 1
  InnerRadius = 7
  OuterRadius = 8
  Placement = pos=(0,83,25) rot=(0,0,1;0rad)
FEATURE [Part::Cylinder] Cylinder2042  label="Válec2042"
  Angle = 360
  AttacherType = Attacher::AttachEngine3D
  Height = 15
  Placement = pos=(0,0,16) rot=(0,0,1;0rad)
  Radius = 74
FEATURE [Part::Box] Box988  label="Krychle988"
  AttacherType = Attacher::AttachEngine3D
  Height = 15
  Length = 148
  Placement = pos=(-74,48,16) rot=(0,0,1;0rad)
  Width = 38
FEATURE [Part::Cylinder] Cylinder2043  label="Válec2043"
  Angle = 360
  AttacherType = Attacher::AttachEngine3D
  Height = 36
  Placement = pos=(-76.3,104,16) rot=(0,0,1;0rad)
  Radius = 46
FEATURE [Part::Cylinder] Cylinder2044  label="Válec2044"
  Angle = 360
  AttacherType = Attacher::AttachEngine3D
  Height = 50
  Placement = pos=(71,80,24) rot=(1,0,0;1.5708rad)
  Radius = 1.5
FEATURE [Part::Cylinder] Cylinder2045  label="Válec2045"
  Angle = 360
  AttacherType = Attacher::AttachEngine3D
  Height = 50
  Placement = pos=(-71,106,24) rot=(1,0,0;1.5708rad)
  Radius = 3
FEATURE [Part::Cylinder] Cylinder2046  label="Válec2046"
  Angle = 360
  AttacherType = Attacher::AttachEngine3D
  Height = 50
  Placement = pos=(-71,80,24) rot=(1,0,0;1.5708rad)
  Radius = 1.5
FEATURE [Part::Cylinder] Cylinder2047  label="Válec2047"
  Angle = 360
  AttacherType = Attacher::AttachEngine3D
  Height = 36
  Placement = pos=(76.3,104,16) rot=(0,0,1;0rad)
  Radius = 46
FEATURE [Part::Cylinder] Cylinder2048  label="Válec2048"
  Angle = 360
  AttacherType = Attacher::AttachEngine3D
  Height = 6
  Placement = pos=(0,83,25) rot=(0,0,1;0rad)
  Radius = 8
FEATURE [Part::Cylinder] Cylinder2049  label="Válec2049"
  Angle = 360
  AttacherType = Attacher::AttachEngine3D
  Height = 50
  Placement = pos=(-31,131,0) rot=(0,0,1;0.785398rad)
  Radius = 1.5
FEATURE [Part::Cylinder] Cylinder2050  label="Válec2050"
  Angle = 360
  AttacherType = Attacher::AttachEngine3D
  Height = 50
  Placement = pos=(31,131,0) rot=(0,0,1;0.785398rad)
  Radius = 1.5
FEATURE [Part::Cylinder] Cylinder2051  label="Válec2051"
  Angle = 360
  AttacherType = Attacher::AttachEngine3D
  Height = 50
  Placement = pos=(20,137,0) rot=(0,0,1;0.785398rad)
  Radius = 1.5
FEATURE [Part::Cylinder] Cylinder2052  label="Válec2052"
  Angle = 360
  AttacherType = Attacher::AttachEngine3D
  Height = 50
  Placement = pos=(-20,137,0) rot=(0,0,1;0.785398rad)
  Radius = 1.5
FEATURE [Part::Cylinder] Cylinder2053  label="Válec2053"
  Angle = 360
  AttacherType = Attacher::AttachEngine3D
  Height = 50
  Placement = pos=(-54,59,0) rot=(0,0,1;0.785398rad)
  Radius = 1.5
FEATURE [Part::Cylinder] Cylinder2054  label="Válec2054"
  Angle = 360
  AttacherType = Attacher::AttachEngine3D
  Height = 3
  Placement = pos=(-31,77,0) rot=(0,0,1;0.785398rad)
  Radius = 3
FEATURE [Part::Cylinder] Cylinder2055  label="Válec2055"
  Angle = 360
  AttacherType = Attacher::AttachEngine3D
  Height = 50
  Placement = pos=(54,59,0) rot=(0,0,1;0.785398rad)
  Radius = 1.5
FEATURE [Part::Cylinder] Cylinder2056  label="Válec2056"
  Angle = 360
  AttacherType = Attacher::AttachEngine3D
  Height = 50
  Placement = pos=(31,77,0) rot=(0,0,1;0.785398rad)
  Radius = 1.5
FEATURE [Part::Cylinder] Cylinder2057  label="Válec2057"
  Angle = 360
  AttacherType = Attacher::AttachEngine3D
  Height = 50
  Placement = pos=(-31,77,0) rot=(0,0,1;0.785398rad)
  Radius = 1.5
FEATURE [Part::Cylinder] Cylinder2058  label="Válec2058"
  Angle = 360
  AttacherType = Attacher::AttachEngine3D
  Height = 3
  Placement = pos=(31,77,0) rot=(0,0,1;0.785398rad)
  Radius = 3
FEATURE [Part::Cylinder] Cylinder2059  label="Válec2059"
  Angle = 360
  AttacherType = Attacher::AttachEngine3D
  Height = 3
  Placement = pos=(54,59,0) rot=(0,0,1;0.785398rad)
  Radius = 3
FEATURE [Part::Cylinder] Cylinder2060  label="Válec2060"
  Angle = 360
  AttacherType = Attacher::AttachEngine3D
  Height = 50
  Placement = pos=(71,106,24) rot=(1,0,0;1.5708rad)
  Radius = 3
FEATURE [Part::Cylinder] Cylinder2061  label="Válec2061"
  Angle = 360
  AttacherType = Attacher::AttachEngine3D
  Height = 6
  Placement = pos=(0,83,25) rot=(0,0,1;0rad)
  Radius = 8
FEATURE [Part::Compound] Compound955
  Links = -> [Cylinder2060,Cylinder2045]
FEATURE [Part::Cut] Cut701
  Base = -> Box988
  Tool = -> Cylinder2043
FEATURE [Part::Cut] Cut695
  Base = -> Cut701
  Tool = -> Cylinder2047
FEATURE [Part::Cut] Cut699
  Base = -> Cut695
  Tool = -> Cylinder2042
FEATURE [Part::Compound] Compound964
  Links = -> [Cylinder2049,Cylinder2050]
FEATURE [Part::Compound] Compound959
  Links = -> [Cylinder2055,Cylinder2053]
FEATURE [Part::Compound] Compound1105
  Links = -> [Cylinder2058,Cylinder2054]
FEATURE [Part::Compound] Compound960
  Links = -> [Cylinder2056,Cylinder2057]
FEATURE [Part::Compound] Compound1089
  Links = -> [Compound959,Compound960]
FEATURE [Part::Compound] Compound953
  Links = -> [Cylinder2044,Cylinder2046]
FEATURE [Part::Cut] Cut685
  Base = -> Cut699
  Tool = -> Compound953
FEATURE [Part::Cut] Cut697
  Base = -> Cut685
  Tool = -> Compound955
FEATURE [Part::Cut] Cut687
  Base = -> Cut697
  Tool = -> Cylinder2048
FEATURE [Part::Chamfer] Chamfer078
  Base = -> Cut687
  Edges = 1 edges r=2: [Edge24]
FEATURE [Part::Compound] Compound961
  Links = -> [Cylinder2052,Cylinder2051]
FEATURE [Part::Box] Box989  label="Krychle989"
  AttacherType = Attacher::AttachEngine3D
  Height = 6
  Length = 68
  Placement = pos=(-34,86,21) rot=(0,0,1;0rad)
  Width = 15
FEATURE [Part::Cylinder] Cylinder2062  label="Válec2062"
  Angle = 360
  AttacherType = Attacher::AttachEngine3D
  Height = 50
  Placement = pos=(31,101,0) rot=(0,0,1;0.785398rad)
  Radius = 1.5
FEATURE [Part::Cylinder] Cylinder2063  label="Válec2063"
  Angle = 360
  AttacherType = Attacher::AttachEngine3D
  Height = 3
  Placement = pos=(20,137,0) rot=(0,0,1;0.785398rad)
  Radius = 3
FEATURE [Part::Cylinder] Cylinder2064  label="Válec2064"
  Angle = 360
  AttacherType = Attacher::AttachEngine3D
  Height = 3
  Placement = pos=(-31,101,0) rot=(0,0,1;0.785398rad)
  Radius = 3
FEATURE [Part::Cylinder] Cylinder2065  label="Válec2065"
  Angle = 360
  AttacherType = Attacher::AttachEngine3D
  Height = 3
  Placement = pos=(-31,131,0) rot=(0,0,1;0.785398rad)
  Radius = 3
FEATURE [Part::Cylinder] Cylinder2066  label="Válec2066"
  Angle = 360
  AttacherType = Attacher::AttachEngine3D
  Height = 50
  Placement = pos=(-20,137,0) rot=(0,0,1;0.785398rad)
  Radius = 1.5
FEATURE [Part::Cylinder] Cylinder2067  label="Válec2067"
  Angle = 360
  AttacherType = Attacher::AttachEngine3D
  Height = 3
  Placement = pos=(-31,101,0) rot=(0,0,1;0.785398rad)
  Radius = 3
FEATURE [Part::Cylinder] Cylinder2068  label="Válec2068"
  Angle = 360
  AttacherType = Attacher::AttachEngine3D
  Height = 3
  Placement = pos=(-54,59,0) rot=(0,0,1;0.785398rad)
  Radius = 3
FEATURE [Part::Compound] Compound965
  Links = -> [Cylinder2059,Cylinder2068]
FEATURE [Part::Compound] Compound1098
  Links = -> [Compound965,Compound1105]
  Placement = pos=(0,0,16) rot=(0,0,1;0rad)
FEATURE [Part::Cut] Cut689
  Base = -> Chamfer078
  Tool = -> Compound1098
FEATURE [Part::Cut] Cut686
  Base = -> Cut689
  Tool = -> Compound1089
FEATURE [Part::Cylinder] Cylinder2069  label="Válec2069"
  Angle = 360
  AttacherType = Attacher::AttachEngine3D
  Height = 50
  Placement = pos=(-31,101,0) rot=(0,0,1;0.785398rad)
  Radius = 1.5
FEATURE [Part::Compound] Compound1090
  Links = -> [Cylinder2069,Cylinder2062]
FEATURE [Part::Compound] Compound1109
  Links = -> [Compound1090,Compound961,Compound964]
FEATURE [Part::Cylinder] Cylinder2070  label="Válec2070"
  Angle = 360
  AttacherType = Attacher::AttachEngine3D
  Height = 3
  Placement = pos=(-20,137,0) rot=(0,0,1;0.785398rad)
  Radius = 3
FEATURE [Part::Compound] Compound1097
  Links = -> [Cylinder2070,Cylinder2063]
  Placement = pos=(0,0,25) rot=(0,0,1;0rad)
FEATURE [Part::Cylinder] Cylinder2071  label="Válec2071"
  Angle = 360
  AttacherType = Attacher::AttachEngine3D
  Height = 6
  Placement = pos=(0,83,25) rot=(0,0,1;0rad)
  Radius = 8
FEATURE [Part::Cut] Cut702
  Base = -> Box989
  Tool = -> Cylinder2071
FEATURE [Part::Cylinder] Cylinder2072  label="Válec2072"
  Angle = 360
  AttacherType = Attacher::AttachEngine3D
  Height = 6
  Placement = pos=(0,101,21) rot=(0,0,1;0rad)
  Radius = 34
FEATURE [Part::Cylinder] Cylinder2073  label="Válec2073"
  Angle = 360
  AttacherType = Attacher::AttachEngine3D
  Height = 6
  Placement = pos=(0,83,25) rot=(0,0,1;0rad)
  Radius = 8
FEATURE [Part::Cylinder] Cylinder2074  label="Válec2074"
  Angle = 360
  AttacherType = Attacher::AttachEngine3D
  Height = 3
  Placement = pos=(31,101,0) rot=(0,0,1;0.785398rad)
  Radius = 3
FEATURE [Part::Compound] Compound1091
  Links = -> [Cylinder2064,Cylinder2074]
  Placement = pos=(0,0,21) rot=(0,0,1;0rad)
FEATURE [Part::Cylinder] Cylinder2075  label="Válec2075"
  Angle = 360
  AttacherType = Attacher::AttachEngine3D
  Height = 50
  Placement = pos=(-31,131,0) rot=(0,0,1;0.785398rad)
  Radius = 1.5
FEATURE [Part::Box] Box802  label="Krychle802"
  AttacherType = Attacher::AttachEngine3D
  Height = 6
  Length = 68
  Placement = pos=(-34,86,25) rot=(0,0,1;0rad)
  Width = 55
FEATURE [Part::Cut] Cut692
  Base = -> Box802
  Tool = -> Cylinder2061
FEATURE [Part::Cylinder] Cylinder2076  label="Válec2076"
  Angle = 360
  AttacherType = Attacher::AttachEngine3D
  Height = 3
  Placement = pos=(31,131,0) rot=(0,0,1;0.785398rad)
  Radius = 3
FEATURE [Part::Compound] Compound1099
  Links = -> [Cylinder2065,Cylinder2076]
  Placement = pos=(0,0,25) rot=(0,0,1;0rad)
FEATURE [Part::Compound] Compound1096
  Links = -> [Compound1097,Compound1099,Compound1091]
FEATURE [Part::Cut] Cut700
  Base = -> Cut702
  Tool = -> Compound1096
FEATURE [Part::Chamfer] Chamfer081
  Base = -> Cut700
  Edges = 2 edges r=2: [Edge5,Edge25]
FEATURE [Part::Cylinder] Cylinder2077  label="Válec2077"
  Angle = 360
  AttacherType = Attacher::AttachEngine3D
  Height = 50
  Placement = pos=(20,137,0) rot=(0,0,1;0.785398rad)
  Radius = 1.5
FEATURE [Part::Compound] Compound1111
  Links = -> [Cylinder2066,Cylinder2077]
FEATURE [Part::Cylinder] Cylinder2078  label="Válec2078"
  Angle = 360
  AttacherType = Attacher::AttachEngine3D
  Height = 3
  Placement = pos=(31,131,0) rot=(0,0,1;0.785398rad)
  Radius = 3
FEATURE [Part::Box] Box990  label="Krychle990"
  AttacherType = Attacher::AttachEngine3D
  Height = 40
  Length = 148
  Placement = pos=(-74,46,16) rot=(0,0,1;0rad)
  Width = 40
FEATURE [Part::Cut] Cut693
  Base = -> Cylinder2072
  Tool = -> Box990
FEATURE [Part::Cut] Cut684
  Base = -> Cut693
  Tool = -> Cylinder2073
FEATURE [Part::Chamfer] Chamfer079
  Base = -> Cut684
  Edges = 1 edges r=2: [Edge7]
FEATURE [Part::Cylinder] Cylinder2079  label="Válec2079"
  Angle = 360
  AttacherType = Attacher::AttachEngine3D
  Height = 3
  Placement = pos=(-31,101,0) rot=(0,0,1;0.785398rad)
  Radius = 3
FEATURE [Part::Cylinder] Cylinder2080  label="Válec2080"
  Angle = 360
  AttacherType = Attacher::AttachEngine3D
  Height = 3
  Placement = pos=(20,137,0) rot=(0,0,1;0.785398rad)
  Radius = 3
FEATURE [Part::Cylinder] Cylinder2081  label="Válec2081"
  Angle = 360
  AttacherType = Attacher::AttachEngine3D
  Height = 3
  Placement = pos=(-31,131,0) rot=(0,0,1;0.785398rad)
  Radius = 3
FEATURE [Part::Cylinder] Cylinder2082  label="Válec2082"
  Angle = 360
  AttacherType = Attacher::AttachEngine3D
  Height = 3
  Placement = pos=(-20,137,0) rot=(0,0,1;0.785398rad)
  Radius = 3
FEATURE [Part::Cylinder] Cylinder2083  label="Válec2083"
  Angle = 360
  AttacherType = Attacher::AttachEngine3D
  Height = 50
  Placement = pos=(-20,137,0) rot=(0,0,1;0.785398rad)
  Radius = 1.5
FEATURE [Part::Cylinder] Cylinder2084  label="Válec2084"
  Angle = 360
  AttacherType = Attacher::AttachEngine3D
  Height = 3
  Placement = pos=(20,137,0) rot=(0,0,1;0.785398rad)
  Radius = 3
FEATURE [Part::Compound] Compound1102
  Links = -> [Cylinder2082,Cylinder2084]
  Placement = pos=(0,0,25) rot=(0,0,1;0rad)
FEATURE [Part::Cylinder] Cylinder2085  label="Válec2085"
  Angle = 360
  AttacherType = Attacher::AttachEngine3D
  Height = 3
  Placement = pos=(31,131,0) rot=(0,0,1;0.785398rad)
  Radius = 3
FEATURE [Part::Compound] Compound1101
  Links = -> [Cylinder2081,Cylinder2085]
  Placement = pos=(0,0,25) rot=(0,0,1;0rad)
FEATURE [Part::Cylinder] Cylinder2086  label="Válec2086"
  Angle = 360
  AttacherType = Attacher::AttachEngine3D
  Height = 3
  Placement = pos=(31,101,0) rot=(0,0,1;0.785398rad)
  Radius = 3
FEATURE [Part::Compound] Compound1095
  Links = -> [Cylinder2079,Cylinder2086]
  Placement = pos=(0,0,21) rot=(0,0,1;0rad)
FEATURE [Part::Cylinder] Cylinder2087  label="Válec2087"
  Angle = 360
  AttacherType = Attacher::AttachEngine3D
  Height = 3
  Placement = pos=(-31,131,0) rot=(0,0,1;0.785398rad)
  Radius = 3
FEATURE [Part::Compound] Compound1094
  Links = -> [Cylinder2087,Cylinder2078]
  Placement = pos=(0,0,25) rot=(0,0,1;0rad)
FEATURE [Part::Compound] Compound1093
  Links = -> [Compound1102,Compound1094,Compound1095]
FEATURE [Part::Cut] Cut694
  Base = -> Chamfer079
  Tool = -> Compound1093
FEATURE [Part::Cylinder] Cylinder2088  label="Válec2088"
  Angle = 360
  AttacherType = Attacher::AttachEngine3D
  Height = 3
  Placement = pos=(-20,137,0) rot=(0,0,1;0.785398rad)
  Radius = 3
FEATURE [Part::Compound] Compound1104
  Links = -> [Cylinder2088,Cylinder2080]
  Placement = pos=(0,0,25) rot=(0,0,1;0rad)
FEATURE [Part::Cylinder] Cylinder2089  label="Válec2089"
  Angle = 360
  AttacherType = Attacher::AttachEngine3D
  Height = 50
  Placement = pos=(31,131,0) rot=(0,0,1;0.785398rad)
  Radius = 1.5
FEATURE [Part::Compound] Compound1108
  Links = -> [Cylinder2075,Cylinder2089]
FEATURE [Part::Cylinder] Cylinder2090  label="Válec2090"
  Angle = 360
  AttacherType = Attacher::AttachEngine3D
  Height = 50
  Placement = pos=(-31,101,0) rot=(0,0,1;0.785398rad)
  Radius = 1.5
FEATURE [Part::Cylinder] Cylinder2091  label="Válec2091"
  Angle = 360
  AttacherType = Attacher::AttachEngine3D
  Height = 3
  Placement = pos=(31,101,0) rot=(0,0,1;0.785398rad)
  Radius = 3
FEATURE [Part::Compound] Compound1103
  Links = -> [Cylinder2067,Cylinder2091]
  Placement = pos=(0,0,21) rot=(0,0,1;0rad)
FEATURE [Part::Compound] Compound1106
  Links = -> [Compound1104,Compound1101,Compound1103]
FEATURE [Part::Cut] Cut696
  Base = -> Cut692
  Tool = -> Compound1106
FEATURE [Part::Cut] Cut698
  Base = -> Cut696
  Tool = -> Compound1109
FEATURE [Part::Cylinder] Cylinder2092  label="Válec2092"
  Angle = 360
  AttacherType = Attacher::AttachEngine3D
  Height = 50
  Placement = pos=(-31,131,0) rot=(0,0,1;0.785398rad)
  Radius = 1.5
FEATURE [Part::Cylinder] Cylinder2093  label="Válec2093"
  Angle = 360
  AttacherType = Attacher::AttachEngine3D
  Height = 50
  Placement = pos=(31,101,0) rot=(0,0,1;0.785398rad)
  Radius = 1.5
FEATURE [Part::Compound] Compound1100
  Links = -> [Cylinder2090,Cylinder2093]
FEATURE [Part::Compound] Compound1092
  Links = -> [Compound1100,Compound1111,Compound1108]
FEATURE [Part::Cut] Cut688
  Base = -> Cut694
  Tool = -> Compound1092
FEATURE [Part::Cylinder] Cylinder2094  label="Válec2094"
  Angle = 360
  AttacherType = Attacher::AttachEngine3D
  Height = 50
  Placement = pos=(-31,101,0) rot=(0,0,1;0.785398rad)
  Radius = 1.5
FEATURE [Part::Cylinder] Cylinder2095  label="Válec2095"
  Angle = 360
  AttacherType = Attacher::AttachEngine3D
  Height = 50
  Placement = pos=(31,101,0) rot=(0,0,1;0.785398rad)
  Radius = 1.5
FEATURE [Part::Compound] Compound1112
  Links = -> [Cylinder2094,Cylinder2095]
FEATURE [Part::Cylinder] Cylinder2096  label="Válec2096"
  Angle = 360
  AttacherType = Attacher::AttachEngine3D
  Height = 50
  Placement = pos=(31,131,0) rot=(0,0,1;0.785398rad)
  Radius = 1.5
FEATURE [Part::Compound] Compound1088
  Links = -> [Cylinder2092,Cylinder2096]
FEATURE [Part::Cylinder] Cylinder2097  label="Válec2097"
  Angle = 360
  AttacherType = Attacher::AttachEngine3D
  Height = 50
  Placement = pos=(20,137,0) rot=(0,0,1;0.785398rad)
  Radius = 1.5
FEATURE [Part::Compound] Compound1087
  Links = -> [Cylinder2083,Cylinder2097]
FEATURE [Part::Compound] Compound1110
  Links = -> [Compound1112,Compound1087,Compound1088]
FEATURE [Part::Cut] Cut690
  Base = -> Chamfer081
  Tool = -> Compound1110
FEATURE [Part::Box] Box991  label="Krychle991"
  AttacherType = Attacher::AttachEngine3D
  Height = 40
  Length = 148
  Placement = pos=(-74,42,16) rot=(0,0,1;0rad)
  Width = 40
FEATURE [Part::Cylinder] Cylinder2098  label="Válec2098"
  Angle = 360
  AttacherType = Attacher::AttachEngine3D
  Height = 6
  Placement = pos=(0,86,16) rot=(0,0,1;0rad)
  Radius = 16
FEATURE [Part::Cut] Cut691
  Base = -> Cylinder2098
  Tool = -> Box991
FEATURE [Part::Chamfer] Chamfer080
  Base = -> Cut691
  Edges = 1 edges r=2: [Edge7]
FEATURE [Part::Compound] Compound1107  label="Base_rear-gearbox-cover"
  Links = -> [Tube032,Cut688,Cut690,Cut698,Cut686,Chamfer080]
  Placement = pos=(0,0,-2) rot=(0,0,1;0rad)
FEATURE [Part::Fillet] Fillet
  Base = -> Cut680
  Edges = 4 edges r=8: [Edge29,Edge31,Edge33,Edge35]
FEATURE [Part::Fillet] Fillet001
  Base = -> Fillet
  Edges = 4 edges r=8: [Edge26,Edge30,Edge34,Edge38]
FEATURE [Part::Fillet] Fillet002
  Base = -> Fillet001
  Edges = 4 edges r=8: [Edge26,Edge30,Edge34,Edge45]
FEATURE [Part::Fillet] Fillet003
  Base = -> Fillet002
  Edges = 6 edges r=8: [Edge33,Edge37,Edge41,Edge45,Edge49,Edge53]
FEATURE [Part::Fillet] Fillet004
  Base = -> Fillet003
  Edges = 6 edges r=8: [Edge37,Edge41,Edge45,Edge49,Edge53,Edge57]
FEATURE [Part::Box] Box992  label="Krychle992"
  AttacherType = Attacher::AttachEngine3D
  Height = 2
  Length = 6
  Placement = pos=(66.4519,34.9019,39) rot=(0,0,1;2.0944rad)
  Width = 8
FEATURE [Part::Box] Box993  label="Krychle993"
  AttacherType = Attacher::AttachEngine3D
  Height = 2
  Length = 6
  Placement = pos=(75,-3,39) rot=(0,0,1;1.5708rad)
  Width = 8
FEATURE [Part::Box] Box994  label="Krychle994"
  AttacherType = Attacher::AttachEngine3D
  Height = 2
  Length = 6
  Placement = pos=(3,75,39) rot=(0,0,1;3.14159rad)
  Width = 8
FEATURE [Part::Box] Box995  label="Krychle995"
  AttacherType = Attacher::AttachEngine3D
  Height = 2
  Length = 6
  Placement = pos=(-63.4519,40.0981,39) rot=(0,0,1;4.18879rad)
  Width = 8
FEATURE [Part::Box] Box996  label="Krychle996"
  AttacherType = Attacher::AttachEngine3D
  Height = 2
  Length = 6
  Placement = pos=(-3,-75,39) rot=(0,0,1;0rad)
  Width = 8
FEATURE [Part::Box] Box997  label="Krychle997"
  AttacherType = Attacher::AttachEngine3D
  Height = 2
  Length = 6
  Placement = pos=(34.9019,-66.4519,39) rot=(0,0,1;0.523599rad)
  Width = 8
FEATURE [Part::Box] Box998  label="Krychle998"
  AttacherType = Attacher::AttachEngine3D
  Height = 2
  Length = 6
  Placement = pos=(-34.9019,66.4519,39) rot=(0,0,1;3.66519rad)
  Width = 8
FEATURE [Part::Box] Box999  label="Krychle999"
  AttacherType = Attacher::AttachEngine3D
  Height = 2
  Length = 6
  Placement = pos=(40.0981,63.4519,39) rot=(0,0,1;2.61799rad)
  Width = 8
FEATURE [Part::Box] Box1000  label="Krychle1000"
  AttacherType = Attacher::AttachEngine3D
  Height = 2
  Length = 6
  Placement = pos=(-75,3,39) rot=(0,0,-1;1.5708rad)
  Width = 8
FEATURE [Part::Box] Box1001  label="Krychle1001"
  AttacherType = Attacher::AttachEngine3D
  Height = 2
  Length = 6
  Placement = pos=(63.4519,-40.0981,39) rot=(0,0,1;1.0472rad)
  Width = 8
FEATURE [Part::Box] Box1002  label="Krychle1002"
  AttacherType = Attacher::AttachEngine3D
  Height = 2
  Length = 6
  Placement = pos=(-66.4519,-34.9019,39) rot=(0,0,-1;1.0472rad)
  Width = 8
FEATURE [Part::Box] Box1003  label="Krychle1003"
  AttacherType = Attacher::AttachEngine3D
  Height = 2
  Length = 6
  Placement = pos=(-40.0981,-63.4519,39) rot=(0,0,-1;0.523599rad)
  Width = 8
FEATURE [Part::Compound] Compound1113
  Links = -> [Box996,Box997,Box1001,Box993,Box992,Box999,Box994,Box998,Box995,Box1000,Box1002,Box1003]
  Placement = pos=(0,0,-30) rot=(0,0,1;0.261799rad)
FEATURE [Part::Cylinder] Cylinder2099  label="Válec2099"
  Angle = 360
  AttacherType = Attacher::AttachEngine3D
  Height = 32
  Placement = pos=(61.4878,-35.5,0) rot=(0,0,1;1.0472rad)
  Radius = 1.5
FEATURE [Part::Cylinder] Cylinder2100  label="Válec2100"
  Angle = 360
  AttacherType = Attacher::AttachEngine3D
  Height = 32
  Placement = pos=(35.5,-61.4878,0) rot=(0,0,1;0.523599rad)
  Radius = 1.5
FEATURE [Part::Cylinder] Cylinder2101  label="Válec2101"
  Angle = 360
  AttacherType = Attacher::AttachEngine3D
  Height = 32
  Placement = pos=(-61.4878,-35.5,0) rot=(0,0,-1;1.0472rad)
  Radius = 1.5
FEATURE [Part::Cylinder] Cylinder2102  label="Válec2102"
  Angle = 360
  AttacherType = Attacher::AttachEngine3D
  Height = 32
  Placement = pos=(0,-71,0) rot=(0,0,1;0rad)
  Radius = 1.5
FEATURE [Part::Cylinder] Cylinder2103  label="Válec2103"
  Angle = 360
  AttacherType = Attacher::AttachEngine3D
  Height = 32
  Placement = pos=(3.1e-14,71,0) rot=(0,0,1;3.14159rad)
  Radius = 1.5
FEATURE [Part::Cylinder] Cylinder2104  label="Válec2104"
  Angle = 360
  AttacherType = Attacher::AttachEngine3D
  Height = 32
  Placement = pos=(71,-1.8e-14,0) rot=(0,0,1;1.5708rad)
  Radius = 1.5
FEATURE [Part::Cylinder] Cylinder2105  label="Válec2105"
  Angle = 360
  AttacherType = Attacher::AttachEngine3D
  Height = 32
  Placement = pos=(61.4878,35.5,0) rot=(0,0,1;2.0944rad)
  Radius = 1.5
FEATURE [Part::Cylinder] Cylinder2106  label="Válec2106"
  Angle = 360
  AttacherType = Attacher::AttachEngine3D
  Height = 32
  Placement = pos=(35.5,61.4878,0) rot=(0,0,1;2.61799rad)
  Radius = 1.5
FEATURE [Part::Cylinder] Cylinder2107  label="Válec2107"
  Angle = 360
  AttacherType = Attacher::AttachEngine3D
  Height = 32
  Placement = pos=(-35.5,-61.4878,0) rot=(0,0,-1;0.523599rad)
  Radius = 1.5
FEATURE [Part::Cylinder] Cylinder2108  label="Válec2108"
  Angle = 360
  AttacherType = Attacher::AttachEngine3D
  Height = 32
  Placement = pos=(-71,2.7e-14,0) rot=(0,0,-1;1.5708rad)
  Radius = 1.5
FEATURE [Part::Cylinder] Cylinder2109  label="Válec2109"
  Angle = 360
  AttacherType = Attacher::AttachEngine3D
  Height = 32
  Placement = pos=(-61.4878,35.5,0) rot=(0,0,1;4.18879rad)
  Radius = 1.5
FEATURE [Part::Cylinder] Cylinder2110  label="Válec2110"
  Angle = 360
  AttacherType = Attacher::AttachEngine3D
  Height = 32
  Placement = pos=(-35.5,61.4878,0) rot=(0,0,1;3.66519rad)
  Radius = 1.5
FEATURE [Part::Compound] Compound1114
  Links = -> [Cylinder2102,Cylinder2100,Cylinder2099,Cylinder2104,Cylinder2105,Cylinder2106,Cylinder2103,Cylinder2110,Cylinder2109,Cylinder2108,Cylinder2101,Cylinder2107]
  Placement = pos=(0,0,-13) rot=(0,0,1;0.261799rad)
FEATURE [Part::Cut] Cut703
  Base = -> Fillet004
  Tool = -> Compound1113
FEATURE [Part::Cut] Cut704
  Base = -> Cut703
  Tool = -> Compound1114
FEATURE [Part::Chamfer] Chamfer082
  Base = -> Cut704
  Edges = 1 edges r=1: [Edge171]
FEATURE [Part::Compound] Compound1115  label="Base_turret-big-ring"
  Links = -> [Cut682,Cut683,Chamfer082]
FEATURE [Part::Box] Box698  label="Krychle698"
  AttacherType = Attacher::AttachEngine3D
  Height = 14
  Length = 200
  Placement = pos=(70.7107,70.7107,-5) rot=(0,0,1;3.92699rad)
  Width = 120
FEATURE [Part::Cylinder] Cylinder1747  label="Válec1747"
  Angle = 360
  AttacherType = Attacher::AttachEngine3D
  Height = 72
  Placement = pos=(-61.4878,-35.5,0) rot=(0,0,-1;1.0472rad)
  Radius = 1.5
FEATURE [Part::Box] Box694  label="Krychle694"
  AttacherType = Attacher::AttachEngine3D
  Height = 12
  Length = 200
  Placement = pos=(70.7107,70.7107,-5) rot=(0,0,1;3.92699rad)
  Width = 120
FEATURE [Part::Cylinder] Cylinder1744  label="Válec1744"
  Angle = 360
  AttacherType = Attacher::AttachEngine3D
  Height = 72
  Placement = pos=(35.5,-61.4878,0) rot=(0,0,1;0.523599rad)
  Radius = 1.5
FEATURE [Part::Cylinder] Cylinder1748  label="Válec1748"
  Angle = 360
  AttacherType = Attacher::AttachEngine3D
  Height = 72
  Placement = pos=(61.4878,35.5,0) rot=(0,0,1;2.0944rad)
  Radius = 1.5
FEATURE [Part::Cylinder] Cylinder1741  label="Válec1741"
  Angle = 360
  AttacherType = Attacher::AttachEngine3D
  Height = 72
  Placement = pos=(71,-1.8e-14,0) rot=(0,0,1;1.5708rad)
  Radius = 1.5
FEATURE [Part::Box] Box695  label="Krychle695"
  AttacherType = Attacher::AttachEngine3D
  Height = 60
  Length = 200
  Placement = pos=(0,0,-5) rot=(0,0,1;3.52556rad)
  Width = 200
FEATURE [Part::Box] Box697  label="Krychle697"
  AttacherType = Attacher::AttachEngine3D
  Height = 60
  Length = 200
  Placement = pos=(0,0,-5) rot=(0,0,1;3.82227rad)
  Width = 200
FEATURE [Part::Cylinder] Cylinder1743  label="Válec1743"
  Angle = 360
  AttacherType = Attacher::AttachEngine3D
  Height = 72
  Placement = pos=(61.4878,-35.5,0) rot=(0,0,1;1.0472rad)
  Radius = 1.5
FEATURE [Part::Cylinder] Cylinder1745  label="Válec1745"
  Angle = 360
  AttacherType = Attacher::AttachEngine3D
  Height = 72
  Placement = pos=(-35.5,-61.4878,0) rot=(0,0,-1;0.523599rad)
  Radius = 1.5
FEATURE [Part::Box] Box693  label="Krychle693"
  AttacherType = Attacher::AttachEngine3D
  Height = 60
  Length = 200
  Placement = pos=(0,0,-5) rot=(0,0,-1;0.383972rad)
  Width = 200
FEATURE [Part::Box] Box696  label="Krychle696"
  AttacherType = Attacher::AttachEngine3D
  Height = 60
  Length = 200
  Placement = pos=(0,0,-5) rot=(0,0,-1;0.680678rad)
  Width = 200
FEATURE [Part::Cylinder] Cylinder1742  label="Válec1742"
  Angle = 360
  AttacherType = Attacher::AttachEngine3D
  Height = 72
  Placement = pos=(35.5,61.4878,0) rot=(0,0,1;2.61799rad)
  Radius = 1.5
FEATURE [Part::Cylinder] Cylinder1746  label="Válec1746"
  Angle = 360
  AttacherType = Attacher::AttachEngine3D
  Height = 72
  Placement = pos=(-71,2.7e-14,0) rot=(0,0,-1;1.5708rad)
  Radius = 1.5
FEATURE [Part::FeaturePython] Tube038  # WARN: FeaturePython — macro-defined, semantics opaque (R4)
  AttacherType = Attacher::AttachEngine3D
  Height = 55
  InnerRadius = 68
  OuterRadius = 74
  Placement = pos=(0,0,29) rot=(0,0,1;0rad)
FEATURE [Part::FeaturePython] Tube039  # WARN: FeaturePython — macro-defined, semantics opaque (R4)
  AttacherType = Attacher::AttachEngine3D
  Height = 55
  InnerRadius = 68
  OuterRadius = 74
  Placement = pos=(0,0,29) rot=(0,0,1;0rad)
FEATURE [Part::Cut] Cut513
  Base = -> Box694
  Tool = -> Box693
FEATURE [Part::Cut] Cut514
  Base = -> Cut513
  Placement = pos=(0,0,34) rot=(0,0,1;0rad)
  Tool = -> Box695
FEATURE [Part::Common] Common
  Base = -> Cut514
  Tool = -> Tube038
FEATURE [Part::Cut] Cut515
  Base = -> Box698
  Tool = -> Box696
FEATURE [Part::Cut] Cut516
  Base = -> Cut515
  Placement = pos=(0,0,46) rot=(0,0,1;0rad)
  Tool = -> Box697
FEATURE [Part::Common] Common001
  Base = -> Cut516
  Tool = -> Tube039
FEATURE [Part::Compound] Compound885
  Links = -> [Common,Common001]
FEATURE [Part::Cylinder] Cylinder1749  label="Válec1749"
  Angle = 360
  AttacherType = Attacher::AttachEngine3D
  Height = 72
  Placement = pos=(0,-71,0) rot=(0,0,1;0rad)
  Radius = 1.5
FEATURE [Part::Cylinder] Cylinder1752  label="Válec1752"
  Angle = 360
  AttacherType = Attacher::AttachEngine3D
  Height = 72
  Placement = pos=(3.1e-14,71,0) rot=(0,0,1;3.14159rad)
  Radius = 1.5
FEATURE [Part::Cylinder] Cylinder1751  label="Válec1751"
  Angle = 360
  AttacherType = Attacher::AttachEngine3D
  Height = 72
  Placement = pos=(-61.4878,35.5,0) rot=(0,0,1;4.18879rad)
  Radius = 1.5
FEATURE [Part::Cylinder] Cylinder1750  label="Válec1750"
  Angle = 360
  AttacherType = Attacher::AttachEngine3D
  Height = 72
  Placement = pos=(-35.5,61.4878,0) rot=(0,0,1;3.66519rad)
  Radius = 1.5
FEATURE [Part::Compound] Compound886
  Links = -> [Cylinder1749,Cylinder1744,Cylinder1743,Cylinder1741,Cylinder1748,Cylinder1742,Cylinder1752,Cylinder1750,Cylinder1751,Cylinder1746,Cylinder1747,Cylinder1745]
FEATURE [Part::Cut] Cut517  label="Base_pulley-cover"
  Base = -> Compound885
  Tool = -> Compound886
FEATURE [Mesh::Feature] Mesh004  label="Base_pulley-cover (Meshed)"
FEATURE [Part::Cylinder] Cylinder979  label="Válec979"
  Angle = 360
  AttacherType = Attacher::AttachEngine3D
  Height = 60
  Placement = pos=(3.1e-14,71,0) rot=(0,0,1;3.14159rad)
  Radius = 1.5
FEATURE [Part::Cylinder] Cylinder975  label="Válec975"
  Angle = 360
  AttacherType = Attacher::AttachEngine3D
  Height = 60
  Placement = pos=(61.4878,-35.5,0) rot=(0,0,1;1.0472rad)
  Radius = 1.5
FEATURE [Part::Cylinder] Cylinder983  label="Válec983"
  Angle = 360
  AttacherType = Attacher::AttachEngine3D
  Height = 60
  Placement = pos=(-61.4878,-35.5,0) rot=(0,0,-1;1.0472rad)
  Radius = 1.5
FEATURE [Part::Cylinder] Cylinder978  label="Válec978"
  Angle = 360
  AttacherType = Attacher::AttachEngine3D
  Height = 60
  Placement = pos=(35.5,61.4878,0) rot=(0,0,1;2.61799rad)
  Radius = 1.5
FEATURE [Part::Cylinder] Cylinder976  label="Válec976"
  Angle = 360
  AttacherType = Attacher::AttachEngine3D
  Height = 60
  Placement = pos=(71,-1.8e-14,0) rot=(0,0,1;1.5708rad)
  Radius = 1.5
FEATURE [Part::Cylinder] Cylinder982  label="Válec982"
  Angle = 360
  AttacherType = Attacher::AttachEngine3D
  Height = 60
  Placement = pos=(-71,2.7e-14,0) rot=(0,0,-1;1.5708rad)
  Radius = 1.5
FEATURE [Part::Cylinder] Cylinder981  label="Válec981"
  Angle = 360
  AttacherType = Attacher::AttachEngine3D
  Height = 60
  Placement = pos=(-61.4878,35.5,0) rot=(0,0,1;4.18879rad)
  Radius = 1.5
FEATURE [Part::Cylinder] Cylinder977  label="Válec977"
  Angle = 360
  AttacherType = Attacher::AttachEngine3D
  Height = 60
  Placement = pos=(61.4878,35.5,0) rot=(0,0,1;2.0944rad)
  Radius = 1.5
FEATURE [Part::Cylinder] Cylinder986  label="Válec986"
  Angle = 360
  AttacherType = Attacher::AttachEngine3D
  Height = 3
  Placement = pos=(-71,2.7e-14,0) rot=(0,0,-1;1.5708rad)
  Radius = 3
FEATURE [Part::Cylinder] Cylinder980  label="Válec980"
  Angle = 360
  AttacherType = Attacher::AttachEngine3D
  Height = 60
  Placement = pos=(-35.5,61.4878,0) rot=(0,0,1;3.66519rad)
  Radius = 1.5
FEATURE [Part::Cylinder] Cylinder973  label="Válec973"
  Angle = 360
  AttacherType = Attacher::AttachEngine3D
  Height = 60
  Placement = pos=(0,-71,0) rot=(0,0,1;0rad)
  Radius = 1.5
FEATURE [Part::Cylinder] Cylinder992  label="Válec992"
  Angle = 360
  AttacherType = Attacher::AttachEngine3D
  Height = 3
  Placement = pos=(-61.4878,-35.5,0) rot=(0,0,-1;1.0472rad)
  Radius = 3
FEATURE [Part::Cylinder] Cylinder988  label="Válec988"
  Angle = 360
  AttacherType = Attacher::AttachEngine3D
  Height = 3
  Placement = pos=(61.4878,35.5,0) rot=(0,0,1;2.0944rad)
  Radius = 3
FEATURE [Part::Cylinder] Cylinder989  label="Válec989"
  Angle = 360
  AttacherType = Attacher::AttachEngine3D
  Height = 3
  Placement = pos=(3.1e-14,71,0) rot=(0,0,1;3.14159rad)
  Radius = 3
FEATURE [Part::Cylinder] Cylinder984  label="Válec984"
  Angle = 360
  AttacherType = Attacher::AttachEngine3D
  Height = 3
  Placement = pos=(35.5,61.4878,0) rot=(0,0,1;2.61799rad)
  Radius = 3
FEATURE [Part::Cylinder] Cylinder985  label="Válec985"
  Angle = 360
  AttacherType = Attacher::AttachEngine3D
  Height = 3
  Placement = pos=(-61.4878,35.5,0) rot=(0,0,1;4.18879rad)
  Radius = 3
FEATURE [Part::Cylinder] Cylinder974  label="Válec974"
  Angle = 360
  AttacherType = Attacher::AttachEngine3D
  Height = 60
  Placement = pos=(35.5,-61.4878,0) rot=(0,0,1;0.523599rad)
  Radius = 1.5
FEATURE [Part::Compound] Compound525
  Links = -> [Cylinder973,Cylinder974,Cylinder975,Cylinder976,Cylinder977,Cylinder978,Cylinder979,Cylinder980,Cylinder981,Cylinder982,Cylinder983]
FEATURE [Part::Cylinder] Cylinder991  label="Válec991"
  Angle = 360
  AttacherType = Attacher::AttachEngine3D
  Height = 3
  Placement = pos=(61.4878,-35.5,0) rot=(0,0,1;1.0472rad)
  Radius = 3
FEATURE [Part::Cylinder] Cylinder990  label="Válec990"
  Angle = 360
  AttacherType = Attacher::AttachEngine3D
  Height = 3
  Placement = pos=(35.5,-61.4878,0) rot=(0,0,1;0.523599rad)
  Radius = 3
FEATURE [Part::Cylinder] Cylinder993  label="Válec993"
  Angle = 360
  AttacherType = Attacher::AttachEngine3D
  Height = 3
  Placement = pos=(0,-71,0) rot=(0,0,1;0rad)
  Radius = 3
FEATURE [Part::Cylinder] Cylinder987  label="Válec987"
  Angle = 360
  AttacherType = Attacher::AttachEngine3D
  Height = 3
  Placement = pos=(71,-1.8e-14,0) rot=(0,0,1;1.5708rad)
  Radius = 3
FEATURE [Part::Cylinder] Cylinder994  label="Válec994"
  Angle = 360
  AttacherType = Attacher::AttachEngine3D
  Height = 3
  Placement = pos=(-35.5,61.4878,0) rot=(0,0,1;3.66519rad)
  Radius = 3
FEATURE [Part::Compound] Compound526
  Links = -> [Cylinder993,Cylinder990,Cylinder991,Cylinder987,Cylinder988,Cylinder984,Cylinder989,Cylinder994,Cylinder985,Cylinder986,Cylinder992]
  Placement = pos=(0,0,17) rot=(0,0,1;0rad)
FEATURE [Part::FeaturePython] Tube031  # WARN: FeaturePython — macro-defined, semantics opaque (R4)
  AttacherType = Attacher::AttachEngine3D
  Height = 6
  InnerRadius = 61
  OuterRadius = 74
  Placement = pos=(0,0,14) rot=(0,0,1;0rad)
FEATURE [Part::Chamfer] Chamfer083
  Base = -> Tube031
  Edges = 1 edges r=3: [Edge1]
FEATURE [Part::Cut] Cut207
  Base = -> Chamfer083
  Tool = -> Compound526
FEATURE [Part::Cut] Cut208  label="Base_big-ring-seal"
  Base = -> Cut207
  Placement = pos=(0,0,17) rot=(1,0,0;3.14159rad)
  Tool = -> Compound525
FEATURE [Part::Cylinder] Cylinder2111  label="Válec2111"
  Angle = 360
  AttacherType = Attacher::AttachEngine3D
  Height = 3
  Placement = pos=(-61.4878,35.5,0) rot=(0,0,1;4.18879rad)
  Radius = 3
FEATURE [Part::Cylinder] Cylinder2112  label="Válec2112"
  Angle = 360
  AttacherType = Attacher::AttachEngine3D
  Height = 60
  Placement = pos=(-61.4878,35.5,0) rot=(0,0,1;4.18879rad)
  Radius = 1.5
FEATURE [Part::Cylinder] Cylinder2113  label="Válec2113"
  Angle = 360
  AttacherType = Attacher::AttachEngine3D
  Height = 60
  Placement = pos=(-71,2.7e-14,0) rot=(0,0,-1;1.5708rad)
  Radius = 1.5
FEATURE [Part::Cylinder] Cylinder2114  label="Válec2114"
  Angle = 360
  AttacherType = Attacher::AttachEngine3D
  Height = 60
  Placement = pos=(-61.4878,-35.5,0) rot=(0,0,-1;1.0472rad)
  Radius = 1.5
FEATURE [Part::FeaturePython] Tube053  # WARN: FeaturePython — macro-defined, semantics opaque (R4)
  AttacherType = Attacher::AttachEngine3D
  Height = 6
  InnerRadius = 61
  OuterRadius = 74
  Placement = pos=(0,0,14) rot=(0,0,1;0rad)
FEATURE [Part::Cylinder] Cylinder2115  label="Válec2115"
  Angle = 360
  AttacherType = Attacher::AttachEngine3D
  Height = 3
  Placement = pos=(35.5,-61.4878,0) rot=(0,0,1;0.523599rad)
  Radius = 3
FEATURE [Part::Cylinder] Cylinder2116  label="Válec2116"
  Angle = 360
  AttacherType = Attacher::AttachEngine3D
  Height = 3
  Placement = pos=(-61.4878,-35.5,0) rot=(0,0,-1;1.0472rad)
  Radius = 3
FEATURE [Part::Cylinder] Cylinder2117  label="Válec2117"
  Angle = 360
  AttacherType = Attacher::AttachEngine3D
  Height = 60
  Placement = pos=(71,-1.8e-14,0) rot=(0,0,1;1.5708rad)
  Radius = 1.5
FEATURE [Part::Cylinder] Cylinder2118  label="Válec2118"
  Angle = 360
  AttacherType = Attacher::AttachEngine3D
  Height = 60
  Placement = pos=(61.4878,35.5,0) rot=(0,0,1;2.0944rad)
  Radius = 1.5
FEATURE [Part::Cylinder] Cylinder2119  label="Válec2119"
  Angle = 360
  AttacherType = Attacher::AttachEngine3D
  Height = 3
  Placement = pos=(35.5,61.4878,0) rot=(0,0,1;2.61799rad)
  Radius = 3
FEATURE [Part::Cylinder] Cylinder2120  label="Válec2120"
  Angle = 360
  AttacherType = Attacher::AttachEngine3D
  Height = 3
  Placement = pos=(61.4878,35.5,0) rot=(0,0,1;2.0944rad)
  Radius = 3
FEATURE [Part::Cylinder] Cylinder2121  label="Válec2121"
  Angle = 360
  AttacherType = Attacher::AttachEngine3D
  Height = 60
  Placement = pos=(-35.5,61.4878,0) rot=(0,0,1;3.66519rad)
  Radius = 1.5
FEATURE [Part::Cylinder] Cylinder2122  label="Válec2122"
  Angle = 360
  AttacherType = Attacher::AttachEngine3D
  Height = 60
  Placement = pos=(0,-71,0) rot=(0,0,1;0rad)
  Radius = 1.5
FEATURE [Part::Cylinder] Cylinder2123  label="Válec2123"
  Angle = 360
  AttacherType = Attacher::AttachEngine3D
  Height = 60
  Placement = pos=(3.1e-14,71,0) rot=(0,0,1;3.14159rad)
  Radius = 1.5
FEATURE [Part::Cylinder] Cylinder2124  label="Válec2124"
  Angle = 360
  AttacherType = Attacher::AttachEngine3D
  Height = 60
  Placement = pos=(35.5,-61.4878,0) rot=(0,0,1;0.523599rad)
  Radius = 1.5
FEATURE [Part::Cylinder] Cylinder2125  label="Válec2125"
  Angle = 360
  AttacherType = Attacher::AttachEngine3D
  Height = 3
  Placement = pos=(-71,2.7e-14,0) rot=(0,0,-1;1.5708rad)
  Radius = 3
FEATURE [Part::Cylinder] Cylinder2126  label="Válec2126"
  Angle = 360
  AttacherType = Attacher::AttachEngine3D
  Height = 60
  Placement = pos=(35.5,61.4878,0) rot=(0,0,1;2.61799rad)
  Radius = 1.5
FEATURE [Part::Cylinder] Cylinder2127  label="Válec2127"
  Angle = 360
  AttacherType = Attacher::AttachEngine3D
  Height = 3
  Placement = pos=(71,-1.8e-14,0) rot=(0,0,1;1.5708rad)
  Radius = 3
FEATURE [Part::Cylinder] Cylinder2128  label="Válec2128"
  Angle = 360
  AttacherType = Attacher::AttachEngine3D
  Height = 60
  Placement = pos=(61.4878,-35.5,0) rot=(0,0,1;1.0472rad)
  Radius = 1.5
FEATURE [Part::Cylinder] Cylinder2129  label="Válec2129"
  Angle = 360
  AttacherType = Attacher::AttachEngine3D
  Height = 3
  Placement = pos=(61.4878,-35.5,0) rot=(0,0,1;1.0472rad)
  Radius = 3
FEATURE [Part::Cylinder] Cylinder2130  label="Válec2130"
  Angle = 360
  AttacherType = Attacher::AttachEngine3D
  Height = 3
  Placement = pos=(3.1e-14,71,0) rot=(0,0,1;3.14159rad)
  Radius = 3
FEATURE [Part::Cylinder] Cylinder2131  label="Válec2131"
  Angle = 360
  AttacherType = Attacher::AttachEngine3D
  Height = 32
  Placement = pos=(61.4878,35.5,0) rot=(0,0,1;2.0944rad)
  Radius = 4
FEATURE [Part::Cylinder] Cylinder2132  label="Válec2132"
  Angle = 360
  AttacherType = Attacher::AttachEngine3D
  Height = 32
  Placement = pos=(-35.5,61.4878,0) rot=(0,0,1;3.66519rad)
  Radius = 4
FEATURE [Part::Cylinder] Cylinder2133  label="Válec2133"
  Angle = 360
  AttacherType = Attacher::AttachEngine3D
  Height = 32
  Placement = pos=(0,-71,0) rot=(0,0,1;0rad)
  Radius = 4
FEATURE [Part::Cylinder] Cylinder2134  label="Válec2134"
  Angle = 360
  AttacherType = Attacher::AttachEngine3D
  Height = 32
  Placement = pos=(71,-1.8e-14,0) rot=(0,0,1;1.5708rad)
  Radius = 4
FEATURE [Part::Cylinder] Cylinder2135  label="Válec2135"
  Angle = 360
  AttacherType = Attacher::AttachEngine3D
  Height = 32
  Placement = pos=(35.5,61.4878,0) rot=(0,0,1;2.61799rad)
  Radius = 4
FEATURE [Part::Cylinder] Cylinder2136  label="Válec2136"
  Angle = 360
  AttacherType = Attacher::AttachEngine3D
  Height = 32
  Placement = pos=(-35.5,-61.4878,0) rot=(0,0,-1;0.523599rad)
  Radius = 4
FEATURE [Part::Cylinder] Cylinder2137  label="Válec2137"
  Angle = 360
  AttacherType = Attacher::AttachEngine3D
  Height = 32
  Placement = pos=(61.4878,-35.5,0) rot=(0,0,1;1.0472rad)
  Radius = 4
FEATURE [Part::Cylinder] Cylinder2138  label="Válec2138"
  Angle = 360
  AttacherType = Attacher::AttachEngine3D
  Height = 3
  Placement = pos=(0,-71,0) rot=(0,0,1;0rad)
  Radius = 3
FEATURE [Part::Cylinder] Cylinder2139  label="Válec2139"
  Angle = 360
  AttacherType = Attacher::AttachEngine3D
  Height = 3
  Placement = pos=(-35.5,61.4878,0) rot=(0,0,1;3.66519rad)
  Radius = 3
FEATURE [Part::Cylinder] Cylinder2140  label="Válec2140"
  Angle = 360
  AttacherType = Attacher::AttachEngine3D
  Height = 32
  Placement = pos=(-71,2.7e-14,0) rot=(0,0,-1;1.5708rad)
  Radius = 4
FEATURE [Part::Cylinder] Cylinder2141  label="Válec2141"
  Angle = 360
  AttacherType = Attacher::AttachEngine3D
  Height = 32
  Placement = pos=(3.1e-14,71,0) rot=(0,0,1;3.14159rad)
  Radius = 4
FEATURE [Part::Cylinder] Cylinder2142  label="Válec2142"
  Angle = 360
  AttacherType = Attacher::AttachEngine3D
  Height = 32
  Placement = pos=(35.5,-61.4878,0) rot=(0,0,1;0.523599rad)
  Radius = 4
FEATURE [Part::Cylinder] Cylinder2143  label="Válec2143"
  Angle = 360
  AttacherType = Attacher::AttachEngine3D
  Height = 32
  Placement = pos=(-61.4878,35.5,0) rot=(0,0,1;4.18879rad)
  Radius = 4
FEATURE [Part::Cylinder] Cylinder2144  label="Válec2144"
  Angle = 360
  AttacherType = Attacher::AttachEngine3D
  Height = 32
  Placement = pos=(-61.4878,-35.5,0) rot=(0,0,-1;1.0472rad)
  Radius = 4
FEATURE [Part::Compound] Compound1118
  Links = -> [Cylinder2133,Cylinder2142,Cylinder2137,Cylinder2134,Cylinder2131,Cylinder2135,Cylinder2141,Cylinder2132,Cylinder2143,Cylinder2140,Cylinder2144,Cylinder2136]
  Placement = pos=(8e-15,0,0) rot=(0,0,1;0.261799rad)
FEATURE [Part::Cut] Cut705
  Base = -> Tube053
  Tool = -> Compound1118
FEATURE [Part::Fillet] Fillet005
  Base = -> Cut705
  Edges = 2 edges r=8: [Edge98,Edge100]
FEATURE [Part::Fillet] Fillet006
  Base = -> Fillet005
  Edges = 6 edges r=8: [Edge56,Edge64,Edge68,Edge76,Edge80,Edge88]
FEATURE [Part::Fillet] Fillet007
  Base = -> Fillet006
  Edges = 10 edges r=8: [Edge44,Edge53,Edge57,Edge65,Edge72,Edge81,Edge84,Edge93,Edge96,Edge105]
FEATURE [Part::Fillet] Fillet008
  Base = -> Fillet007
  Edges = 6 edges r=8: [Edge114,Edge121,Edge125,Edge132,Edge133,Edge137]
FEATURE [Part::Chamfer] Chamfer084
  Base = -> Fillet008
  Edges = 13 edges r=3: [Edge51,Edge55,Edge57,Edge58,Edge60,Edge63,Edge65,Edge67,Edge68,Edge71,Edge74,Edge79,Edge83]
FEATURE [Part::Box] Box1292  label="Krychle1292"
  AttacherType = Attacher::AttachEngine3D
  Height = 8
  Length = 8
  Placement = pos=(-68,-14,35) rot=(0,0,1;1.5708rad)
  Width = 2.5
FEATURE [Part::Box] Box1289  label="Krychle1289"
  AttacherType = Attacher::AttachEngine3D
  Height = 8
  Length = 8
  Placement = pos=(-68,-14,35) rot=(0,0,1;1.5708rad)
  Width = 2.5
FEATURE [Part::Box] Box1285  label="Krychle1285"
  AttacherType = Attacher::AttachEngine3D
  Height = 8
  Length = 8
  Placement = pos=(-48,-14,35) rot=(0,0,1;1.5708rad)
  Width = 20
FEATURE [Part::Box] Box1291  label="Krychle1291"
  AttacherType = Attacher::AttachEngine3D
  Height = 8
  Length = 8
  Placement = pos=(-68,12,64) rot=(0,0,1;1.5708rad)
  Width = 2.5
FEATURE [Part::Box] Box1287  label="Krychle1287"
  AttacherType = Attacher::AttachEngine3D
  Height = 8
  Length = 8
  Placement = pos=(-48,12,64) rot=(0,0,1;1.5708rad)
  Width = 20
FEATURE [Part::Box] Box1290  label="Krychle1290"
  AttacherType = Attacher::AttachEngine3D
  Height = 8
  Length = 8
  Placement = pos=(-68,12,64) rot=(0,0,1;1.5708rad)
  Width = 2.5
FEATURE [Part::Box] Box1286  label="Krychle1286"
  AttacherType = Attacher::AttachEngine3D
  Height = 8
  Length = 8
  Placement = pos=(-48,-14,65) rot=(0,0,1;1.5708rad)
  Width = 20
FEATURE [Part::Box] Box1288  label="Krychle1288"
  AttacherType = Attacher::AttachEngine3D
  Height = 8
  Length = 8
  Placement = pos=(-48,-14,35) rot=(0,0,1;1.5708rad)
  Width = 20
FEATURE [Part::Box] Box1293  label="Krychle1293"
  AttacherType = Attacher::AttachEngine3D
  Height = 8
  Length = 8
  Placement = pos=(-68,16,35) rot=(0,0,1;1.5708rad)
  Width = 2.5
FEATURE [Part::Box] Box1294  label="Krychle1294"
  AttacherType = Attacher::AttachEngine3D
  Height = 8
  Length = 8
  Placement = pos=(-68,-14,65) rot=(0,0,1;1.5708rad)
  Width = 2.5
FEATURE [Part::Compound] Compound1174
  Links = -> [Box1292,Box1293,Box1294,Box1291]
FEATURE [Part::Mirroring] mirror041  label="Compound999 (mirrored)002"
  Base = (0,0,0)
  Normal = (1,0,0)
  Source = -> Compound1174
FEATURE [Part::FeaturePython] Tube054  # WARN: FeaturePython — macro-defined, semantics opaque (R4)
  AttacherType = Attacher::AttachEngine3D
  Height = 4
  InnerRadius = 63
  OuterRadius = 74
  Placement = pos=(0,0,68) rot=(0,0,1;0rad)
FEATURE [Part::Box] Box1295  label="Krychle1295"
  AttacherType = Attacher::AttachEngine3D
  Height = 8
  Length = 8
  Placement = pos=(-48,16,35) rot=(0,0,1;1.5708rad)
  Width = 20
FEATURE [Part::Cylinder] Cylinder2145  label="Válec2145"
  Angle = 360
  AttacherType = Attacher::AttachEngine3D
  Height = 40
  Placement = pos=(-86,-10,69) rot=(0,1,0;1.5708rad)
  Radius = 2.5
FEATURE [Part::Cylinder] Cylinder2146  label="Válec2146"
  Angle = 360
  AttacherType = Attacher::AttachEngine3D
  Height = 40
  Placement = pos=(-86,-10,39) rot=(0,1,0;1.5708rad)
  Radius = 2.5
FEATURE [Part::Cylinder] Cylinder2147  label="Válec2147"
  Angle = 360
  AttacherType = Attacher::AttachEngine3D
  Height = 40
  Placement = pos=(-86,-10,39) rot=(0,1,0;1.5708rad)
  Radius = 2.5
FEATURE [Part::Cylinder] Cylinder2148  label="Válec2148"
  Angle = 360
  AttacherType = Attacher::AttachEngine3D
  Height = 40
  Placement = pos=(-86,-10,39) rot=(0,1,0;1.5708rad)
  Radius = 2.5
FEATURE [Part::Cylinder] Cylinder2149  label="Válec2149"
  Angle = 360
  AttacherType = Attacher::AttachEngine3D
  Height = 40
  Placement = pos=(-86,-10,69) rot=(0,1,0;1.5708rad)
  Radius = 2.5
FEATURE [Part::Cylinder] Cylinder2150  label="Válec2150"
  Angle = 360
  AttacherType = Attacher::AttachEngine3D
  Height = 40
  Placement = pos=(-86,-10,69) rot=(0,1,0;1.5708rad)
  Radius = 2.5
FEATURE [Part::Cylinder] Cylinder2151  label="Válec2151"
  Angle = 360
  AttacherType = Attacher::AttachEngine3D
  Height = 40
  Placement = pos=(-86,20,39) rot=(0,1,0;1.5708rad)
  Radius = 2.5
FEATURE [Part::Cylinder] Cylinder2152  label="Válec2152"
  Angle = 360
  AttacherType = Attacher::AttachEngine3D
  Height = 40
  Placement = pos=(-86,-10,39) rot=(0,1,0;1.5708rad)
  Radius = 2.5
FEATURE [Part::Cylinder] Cylinder2153  label="Válec2153"
  Angle = 360
  AttacherType = Attacher::AttachEngine3D
  Height = 40
  Placement = pos=(-86,16,68) rot=(0,1,0;1.5708rad)
  Radius = 2.5
FEATURE [Part::Cylinder] Cylinder2154  label="Válec2154"
  Angle = 360
  AttacherType = Attacher::AttachEngine3D
  Height = 40
  Placement = pos=(-86,20,39) rot=(0,1,0;1.5708rad)
  Radius = 2.5
FEATURE [Part::Box] Box1296  label="Krychle1296"
  AttacherType = Attacher::AttachEngine3D
  Height = 8
  Length = 8
  Placement = pos=(-48,-14,35) rot=(0,0,1;1.5708rad)
  Width = 20
FEATURE [Part::Cylinder] Cylinder2155  label="Válec2155"
  Angle = 360
  AttacherType = Attacher::AttachEngine3D
  Height = 40
  Placement = pos=(-86,-10,69) rot=(0,1,0;1.5708rad)
  Radius = 2.5
FEATURE [Part::Cylinder] Cylinder2156  label="Válec2156"
  Angle = 360
  AttacherType = Attacher::AttachEngine3D
  Height = 40
  Placement = pos=(-86,16,68) rot=(0,1,0;1.5708rad)
  Radius = 2.5
FEATURE [Part::Box] Box1297  label="Krychle1297"
  AttacherType = Attacher::AttachEngine3D
  Height = 8
  Length = 8
  Placement = pos=(-68,-14,65) rot=(0,0,1;1.5708rad)
  Width = 2.5
FEATURE [Part::Box] Box1298  label="Krychle1298"
  AttacherType = Attacher::AttachEngine3D
  Height = 8
  Length = 8
  Placement = pos=(-68,-14,65) rot=(0,0,1;1.5708rad)
  Width = 2.5
FEATURE [Part::Box] Box1299  label="Krychle1299"
  AttacherType = Attacher::AttachEngine3D
  Height = 8
  Length = 8
  Placement = pos=(-68,-14,35) rot=(0,0,1;1.5708rad)
  Width = 2.5
FEATURE [Part::Box] Box1300  label="Krychle1300"
  AttacherType = Attacher::AttachEngine3D
  Height = 8
  Length = 8
  Placement = pos=(-48,12,64) rot=(0,0,1;1.5708rad)
  Width = 20
FEATURE [Part::Box] Box1301  label="Krychle1301"
  AttacherType = Attacher::AttachEngine3D
  Height = 8
  Length = 8
  Placement = pos=(-48,-14,65) rot=(0,0,1;1.5708rad)
  Width = 20
FEATURE [Part::Box] Box1302  label="Krychle1302"
  AttacherType = Attacher::AttachEngine3D
  Height = 8
  Length = 8
  Placement = pos=(-48,16,35) rot=(0,0,1;1.5708rad)
  Width = 20
FEATURE [Part::Box] Box1303  label="Krychle1303"
  AttacherType = Attacher::AttachEngine3D
  Height = 8
  Length = 8
  Placement = pos=(-68,16,35) rot=(0,0,1;1.5708rad)
  Width = 2.5
FEATURE [Part::Box] Box1304  label="Krychle1304"
  AttacherType = Attacher::AttachEngine3D
  Height = 8
  Length = 8
  Placement = pos=(-68,-14,35) rot=(0,0,1;1.5708rad)
  Width = 2.5
FEATURE [Part::Box] Box1305  label="Krychle1305"
  AttacherType = Attacher::AttachEngine3D
  Height = 8
  Length = 8
  Placement = pos=(-48,-14,65) rot=(0,0,1;1.5708rad)
  Width = 20
FEATURE [Part::Box] Box1306  label="Krychle1306"
  AttacherType = Attacher::AttachEngine3D
  Height = 8
  Length = 8
  Placement = pos=(-68,-14,65) rot=(0,0,1;1.5708rad)
  Width = 2.5
FEATURE [Part::Box] Box1307  label="Krychle1307"
  AttacherType = Attacher::AttachEngine3D
  Height = 8
  Length = 8
  Placement = pos=(-48,-14,65) rot=(0,0,1;1.5708rad)
  Width = 20
FEATURE [Part::Box] Box1308  label="Krychle1308"
  AttacherType = Attacher::AttachEngine3D
  Height = 8
  Length = 8
  Placement = pos=(-48,-14,35) rot=(0,0,1;1.5708rad)
  Width = 20
FEATURE [Part::Box] Box1309  label="Krychle1309"
  AttacherType = Attacher::AttachEngine3D
  Height = 8
  Length = 8
  Placement = pos=(-48,-14,35) rot=(0,0,1;1.5708rad)
  Width = 20
FEATURE [Part::Box] Box1310  label="Krychle1310"
  AttacherType = Attacher::AttachEngine3D
  Height = 8
  Length = 8
  Placement = pos=(-48,-14,65) rot=(0,0,1;1.5708rad)
  Width = 20
FEATURE [Part::Box] Box1311  label="Krychle1311"
  AttacherType = Attacher::AttachEngine3D
  Height = 8
  Length = 8
  Placement = pos=(-48,12,64) rot=(0,0,1;1.5708rad)
  Width = 20
FEATURE [Part::Box] Box1312  label="Krychle1312"
  AttacherType = Attacher::AttachEngine3D
  Height = 8
  Length = 8
  Placement = pos=(-48,-14,35) rot=(0,0,1;1.5708rad)
  Width = 20
FEATURE [Part::Box] Box1313  label="Krychle1313"
  AttacherType = Attacher::AttachEngine3D
  Height = 8
  Length = 8
  Placement = pos=(-68,-14,35) rot=(0,0,1;1.5708rad)
  Width = 2.5
FEATURE [Part::Box] Box1314  label="Krychle1314"
  AttacherType = Attacher::AttachEngine3D
  Height = 8
  Length = 8
  Placement = pos=(-68,12,64) rot=(0,0,1;1.5708rad)
  Width = 2.5
FEATURE [Part::Cylinder] Cylinder2396  label="Válec2396"
  Angle = 360
  AttacherType = Attacher::AttachEngine3D
  Height = 40
  Placement = pos=(-86,-10,39) rot=(0,1,0;1.5708rad)
  Radius = 2.5
FEATURE [Part::Box] Box1315  label="Krychle1315"
  AttacherType = Attacher::AttachEngine3D
  Height = 8
  Length = 8
  Placement = pos=(-68,12,64) rot=(0,0,1;1.5708rad)
  Width = 2.5
FEATURE [Part::Box] Box1272  label="Krychle1272"
  AttacherType = Attacher::AttachEngine3D
  Height = 8
  Length = 8
  Placement = pos=(-48,-14,35) rot=(0,0,1;1.5708rad)
  Width = 20
FEATURE [Part::Box] Box1316  label="Krychle1316"
  AttacherType = Attacher::AttachEngine3D
  Height = 8
  Length = 8
  Placement = pos=(-68,-14,35) rot=(0,0,1;1.5708rad)
  Width = 2.5
FEATURE [Part::Box] Box1317  label="Krychle1317"
  AttacherType = Attacher::AttachEngine3D
  Height = 8
  Length = 8
  Placement = pos=(-68,16,35) rot=(0,0,1;1.5708rad)
  Width = 2.5
FEATURE [Part::Cylinder] Cylinder2389  label="Válec2389"
  Angle = 360
  AttacherType = Attacher::AttachEngine3D
  Height = 40
  Placement = pos=(-86,-10,69) rot=(0,1,0;1.5708rad)
  Radius = 2.5
FEATURE [Part::Compound] Compound1167
  Links = -> [Cylinder2396,Cylinder2389]
  Placement = pos=(-21.5,0,0) rot=(0,0,1;1.5708rad)
FEATURE [Part::Cylinder] Cylinder2390  label="Válec2390"
  Angle = 360
  AttacherType = Attacher::AttachEngine3D
  Height = 40
  Placement = pos=(-86,-10,39) rot=(0,1,0;1.5708rad)
  Radius = 2.5
FEATURE [Part::Cylinder] Cylinder2399  label="Válec2399"
  Angle = 360
  AttacherType = Attacher::AttachEngine3D
  Height = 40
  Placement = pos=(-86,-10,69) rot=(0,1,0;1.5708rad)
  Radius = 2.5
FEATURE [Part::Box] Box1278  label="Krychle1278"
  AttacherType = Attacher::AttachEngine3D
  Height = 8
  Length = 8
  Placement = pos=(-48,16,35) rot=(0,0,1;1.5708rad)
  Width = 20
FEATURE [Part::Compound] Compound1171
  Links = -> [Box1288,Box1278,Box1286,Box1287]
FEATURE [Part::Mirroring] mirror040  label="Compound998 (mirrored)002"
  Base = (0,0,0)
  Normal = (1,0,0)
  Source = -> Compound1171
FEATURE [Part::Cylinder] Cylinder2391  label="Válec2391"
  Angle = 360
  AttacherType = Attacher::AttachEngine3D
  Height = 40
  Placement = pos=(-86,-10,39) rot=(0,1,0;1.5708rad)
  Radius = 2.5
FEATURE [Part::Box] Box1318  label="Krychle1318"
  AttacherType = Attacher::AttachEngine3D
  Height = 8
  Length = 8
  Placement = pos=(-68,-14,65) rot=(0,0,1;1.5708rad)
  Width = 2.5
FEATURE [Part::Cylinder] Cylinder2394  label="Válec2394"
  Angle = 360
  AttacherType = Attacher::AttachEngine3D
  Height = 40
  Placement = pos=(-86,-10,69) rot=(0,1,0;1.5708rad)
  Radius = 2.5
FEATURE [Part::Cylinder] Cylinder2393  label="Válec2393"
  Angle = 360
  AttacherType = Attacher::AttachEngine3D
  Height = 40
  Placement = pos=(-86,-10,69) rot=(0,1,0;1.5708rad)
  Radius = 2.5
FEATURE [Part::Box] Box1271  label="Krychle1271"
  AttacherType = Attacher::AttachEngine3D
  Height = 8
  Length = 8
  Placement = pos=(-48,16,35) rot=(0,0,1;1.5708rad)
  Width = 20
FEATURE [Part::Cylinder] Cylinder2392  label="Válec2392"
  Angle = 360
  AttacherType = Attacher::AttachEngine3D
  Height = 40
  Placement = pos=(-86,-10,39) rot=(0,1,0;1.5708rad)
  Radius = 2.5
FEATURE [Part::Compound] Compound1168
  Links = -> [Cylinder2392,Cylinder2393]
  Placement = pos=(1.5,0,0) rot=(0,0,1;1.5708rad)
FEATURE [Part::Compound] Compound1166
  Links = -> [Compound1168,Compound1167]
FEATURE [Part::Cylinder] Cylinder2395  label="Válec2395"
  Angle = 360
  AttacherType = Attacher::AttachEngine3D
  Height = 40
  Placement = pos=(-86,20,39) rot=(0,1,0;1.5708rad)
  Radius = 2.5
FEATURE [Part::Cylinder] Cylinder2397  label="Válec2397"
  Angle = 360
  AttacherType = Attacher::AttachEngine3D
  Height = 40
  Placement = pos=(-86,16,68) rot=(0,1,0;1.5708rad)
  Radius = 2.5
FEATURE [Part::Compound] Compound1163
  Links = -> [Cylinder2390,Cylinder2395,Cylinder2399,Cylinder2397]
FEATURE [Part::Cylinder] Cylinder2398  label="Válec2398"
  Angle = 360
  AttacherType = Attacher::AttachEngine3D
  Height = 40
  Placement = pos=(-86,20,39) rot=(0,1,0;1.5708rad)
  Radius = 2.5
FEATURE [Part::Box] Box1274  label="Krychle1274"
  AttacherType = Attacher::AttachEngine3D
  Height = 8
  Length = 8
  Placement = pos=(-68,-14,65) rot=(0,0,1;1.5708rad)
  Width = 2.5
FEATURE [Part::Compound] Compound1176
  Links = -> [Box1289,Box1274]
  Placement = pos=(-21.5,0,0) rot=(0,0,1;1.5708rad)
FEATURE [Part::Cylinder] Cylinder2400  label="Válec2400"
  Angle = 360
  AttacherType = Attacher::AttachEngine3D
  Height = 40
  Placement = pos=(-86,16,68) rot=(0,1,0;1.5708rad)
  Radius = 2.5
FEATURE [Part::Compound] Compound1164
  Links = -> [Cylinder2391,Cylinder2398,Cylinder2394,Cylinder2400]
FEATURE [Part::Mirroring] mirror039  label="Compound1000 (mirrored)002"
  Base = (0,0,0)
  Normal = (1,0,0)
  Source = -> Compound1164
FEATURE [Part::Compound] Compound1165
  Links = -> [Compound1163,Compound1166,mirror039]
FEATURE [Part::Box] Box1273  label="Krychle1273"
  AttacherType = Attacher::AttachEngine3D
  Height = 8
  Length = 8
  Placement = pos=(-68,-14,65) rot=(0,0,1;1.5708rad)
  Width = 2.5
FEATURE [Part::Box] Box1275  label="Krychle1275"
  AttacherType = Attacher::AttachEngine3D
  Height = 8
  Length = 8
  Placement = pos=(-68,-14,35) rot=(0,0,1;1.5708rad)
  Width = 2.5
FEATURE [Part::Compound] Compound1179
  Links = -> [Box1275,Box1273]
  Placement = pos=(1.5,0,0) rot=(0,0,1;1.5708rad)
FEATURE [Part::Compound] Compound1177
  Links = -> [Compound1176,Compound1179]
FEATURE [Part::Box] Box1277  label="Krychle1277"
  AttacherType = Attacher::AttachEngine3D
  Height = 8
  Length = 8
  Placement = pos=(-48,-14,65) rot=(0,0,1;1.5708rad)
  Width = 20
FEATURE [Part::Box] Box1276  label="Krychle1276"
  AttacherType = Attacher::AttachEngine3D
  Height = 8
  Length = 8
  Placement = pos=(-48,12,64) rot=(0,0,1;1.5708rad)
  Width = 20
FEATURE [Part::Compound] Compound1172
  Links = -> [Box1285,Box1271,Box1277,Box1276]
FEATURE [Part::Box] Box1279  label="Krychle1279"
  AttacherType = Attacher::AttachEngine3D
  Height = 8
  Length = 8
  Placement = pos=(-68,16,35) rot=(0,0,1;1.5708rad)
  Width = 2.5
FEATURE [Part::Box] Box1280  label="Krychle1280"
  AttacherType = Attacher::AttachEngine3D
  Height = 8
  Length = 8
  Placement = pos=(-68,-14,35) rot=(0,0,1;1.5708rad)
  Width = 2.5
FEATURE [Part::Box] Box1281  label="Krychle1281"
  AttacherType = Attacher::AttachEngine3D
  Height = 8
  Length = 8
  Placement = pos=(-48,-14,65) rot=(0,0,1;1.5708rad)
  Width = 20
FEATURE [Part::Compound] Compound1180
  Links = -> [Box1272,Box1281]
  Placement = pos=(1.5,0,0) rot=(0,0,1;1.5708rad)
FEATURE [Part::Box] Box1282  label="Krychle1282"
  AttacherType = Attacher::AttachEngine3D
  Height = 8
  Length = 8
  Placement = pos=(-68,-14,65) rot=(0,0,1;1.5708rad)
  Width = 2.5
FEATURE [Part::Compound] Compound1178
  Links = -> [Box1280,Box1279,Box1282,Box1290]
FEATURE [Part::Compound] Compound1175
  Links = -> [Compound1178,Compound1177,mirror041]
FEATURE [Part::Box] Box1283  label="Krychle1283"
  AttacherType = Attacher::AttachEngine3D
  Height = 8
  Length = 8
  Placement = pos=(-48,-14,65) rot=(0,0,1;1.5708rad)
  Width = 20
FEATURE [Part::Box] Box1284  label="Krychle1284"
  AttacherType = Attacher::AttachEngine3D
  Height = 8
  Length = 8
  Placement = pos=(-48,-14,35) rot=(0,0,1;1.5708rad)
  Width = 20
FEATURE [Part::Compound] Compound1173
  Links = -> [Box1284,Box1283]
  Placement = pos=(-21.5,0,0) rot=(0,0,1;1.5708rad)
FEATURE [Part::Compound] Compound1169
  Links = -> [Compound1173,Compound1180]
FEATURE [Part::Compound] Compound1170
  Links = -> [Compound1172,Compound1169,mirror040]
FEATURE [Part::Box] Box1222  label="Krychle1222"
  AttacherType = Attacher::AttachEngine3D
  Height = 40
  Length = 34
  Placement = pos=(-6,0,80) rot=(0,0,-1;0.523599rad)
  Width = 100
FEATURE [Part::Mirroring] mirror029  label="Krychle1212 (mirrored)001"
  Base = (0,0,0)
  Normal = (1,0,0)
  Placement = pos=(0,0,-2) rot=(0,0,1;0rad)
  Source = -> Box1222
FEATURE [Part::Cylinder] Cylinder2366  label="Válec2366"
  Angle = 360
  AttacherType = Attacher::AttachEngine3D
  Height = 200
  Placement = pos=(30,0,81) rot=(0.186157,0.694747,0.694747;2.7735rad)
  Radius = 2.5
FEATURE [Part::Cylinder] Cylinder2365  label="Válec2365"
  Angle = 360
  AttacherType = Attacher::AttachEngine3D
  Height = 200
  Placement = pos=(6,0,81) rot=(0.186157,0.694747,0.694747;2.7735rad)
  Radius = 2.5
FEATURE [Part::Box] Box1221  label="Krychle1221"
  AttacherType = Attacher::AttachEngine3D
  Height = 20
  Length = 8
  Placement = pos=(50.79,34,80) rot=(0,0,-1;0.698132rad)
  Width = 6
FEATURE [Part::Compound] Compound1181
  Links = -> [Cylinder2146,Cylinder2151,Cylinder2155,Cylinder2153]
FEATURE [Part::Compound] Compound1182
  Links = -> [Cylinder2147,Cylinder2154,Cylinder2150,Cylinder2156]
FEATURE [Part::Mirroring] mirror042  label="Compound1000 (mirrored)003"
  Base = (0,0,0)
  Normal = (1,0,0)
  Source = -> Compound1182
FEATURE [Part::Cylinder] Cylinder2318  label="Válec2318"
  Angle = 360
  AttacherType = Attacher::AttachEngine3D
  Height = 200
  Placement = pos=(12,0,81) rot=(0.186157,0.694747,0.694747;2.7735rad)
  Radius = 2.5
FEATURE [Part::Cylinder] Cylinder2401  label="Válec2401"
  Angle = 360
  AttacherType = Attacher::AttachEngine3D
  Height = 72
  Placement = pos=(61.4878,-35.5,0) rot=(0,0,1;1.0472rad)
  Radius = 1.5
FEATURE [Part::Cylinder] Cylinder2402  label="Válec2402"
  Angle = 360
  AttacherType = Attacher::AttachEngine3D
  Height = 50
  Placement = pos=(9,100,59) rot=(1,0,0;1.5708rad)
  Radius = 1.5
FEATURE [Part::Cylinder] Cylinder2403  label="Válec2403"
  Angle = 360
  AttacherType = Attacher::AttachEngine3D
  Height = 72
  Placement = pos=(3.1e-14,71,0) rot=(0,0,1;3.14159rad)
  Radius = 1.5
FEATURE [Part::Cylinder] Cylinder2404  label="Válec2404"
  Angle = 360
  AttacherType = Attacher::AttachEngine3D
  Height = 72
  Placement = pos=(61.4878,35.5,0) rot=(0,0,1;2.0944rad)
  Radius = 1.5
FEATURE [Part::Box] Box1032  label="Krychle1032"
  AttacherType = Attacher::AttachEngine3D
  Height = 2
  Length = 6
  Placement = pos=(3,75,39) rot=(0,0,1;3.14159rad)
  Width = 8
FEATURE [Part::Box] Box1033  label="Krychle1033"
  AttacherType = Attacher::AttachEngine3D
  Height = 60
  Length = 200
  Placement = pos=(70.7107,70.7107,-5) rot=(0,0,1;3.92699rad)
  Width = 120
FEATURE [Part::Box] Box1034  label="Krychle1034"
  AttacherType = Attacher::AttachEngine3D
  Height = 2
  Length = 6
  Placement = pos=(-3,-75,39) rot=(0,0,1;0rad)
  Width = 8
FEATURE [Part::Cylinder] Cylinder2405  label="Válec2405"
  Angle = 360
  AttacherType = Attacher::AttachEngine3D
  Height = 50
  Placement = pos=(18,100,72) rot=(1,0,0;1.5708rad)
  Radius = 1.5
FEATURE [Part::Box] Box1031  label="Krychle1031"
  AttacherType = Attacher::AttachEngine3D
  Height = 6
  Length = 6
  Placement = pos=(15,64,-50) rot=(0,0,1;0rad)
  Width = 4
FEATURE [Part::Box] Box1035  label="Krychle1035"
  AttacherType = Attacher::AttachEngine3D
  Height = 6
  Length = 6
  Placement = pos=(6,66,-63) rot=(0,0,1;0rad)
  Width = 4
FEATURE [Part::Cylinder] Cylinder2406  label="Válec2406"
  Angle = 360
  AttacherType = Attacher::AttachEngine3D
  Height = 72
  Placement = pos=(0,-71,0) rot=(0,0,1;0rad)
  Radius = 1.5
FEATURE [Part::Box] Box1043  label="Krychle1043"
  AttacherType = Attacher::AttachEngine3D
  Height = 2
  Length = 6
  Placement = pos=(75,-3,39) rot=(0,0,1;1.5708rad)
  Width = 8
FEATURE [Part::Box] Box1045  label="Krychle1045"
  AttacherType = Attacher::AttachEngine3D
  Height = 2
  Length = 6
  Placement = pos=(66.4519,34.9019,39) rot=(0,0,1;2.0944rad)
  Width = 8
FEATURE [Part::Cylinder] Cylinder2407  label="Válec2407"
  Angle = 360
  AttacherType = Attacher::AttachEngine3D
  Height = 72
  Placement = pos=(-61.4878,-35.5,0) rot=(0,0,-1;1.0472rad)
  Radius = 1.5
FEATURE [Part::Box] Box1041  label="Krychle1041"
  AttacherType = Attacher::AttachEngine3D
  Height = 2
  Length = 6
  Placement = pos=(-75,3,39) rot=(0,0,-1;1.5708rad)
  Width = 8
FEATURE [Part::Box] Box1039  label="Krychle1039"
  AttacherType = Attacher::AttachEngine3D
  Height = 2
  Length = 6
  Placement = pos=(34.9,-66.45,58) rot=(0,0,1;0.523599rad)
  Width = 8
FEATURE [Part::Box] Box1038  label="Krychle1038"
  AttacherType = Attacher::AttachEngine3D
  Height = 2
  Length = 6
  Placement = pos=(40.0981,63.4519,39) rot=(0,0,1;2.61799rad)
  Width = 8
FEATURE [Part::Cylinder] Cylinder2408  label="Válec2408"
  Angle = 360
  AttacherType = Attacher::AttachEngine3D
  Height = 72
  Placement = pos=(35.5,-61.4878,0) rot=(0,0,1;0.523599rad)
  Radius = 1.5
FEATURE [Part::Box] Box1049  label="Krychle1049"
  AttacherType = Attacher::AttachEngine3D
  Height = 6
  Length = 6
  Placement = pos=(-12,66,-63) rot=(0,0,1;0rad)
  Width = 4
FEATURE [Part::Box] Box1046  label="Krychle1046"
  AttacherType = Attacher::AttachEngine3D
  Height = 2
  Length = 6
  Placement = pos=(-40.0981,-63.4519,39) rot=(0,0,-1;0.523599rad)
  Width = 8
FEATURE [Part::Box] Box1037  label="Krychle1037"
  AttacherType = Attacher::AttachEngine3D
  Height = 55
  Length = 148
  Placement = pos=(-74,68,29) rot=(0,0,1;0rad)
  Width = 26
FEATURE [Part::Box] Box1040  label="Krychle1040"
  AttacherType = Attacher::AttachEngine3D
  Height = 60
  Length = 200
  Placement = pos=(0,0,-5) rot=(0,0,-1;0.383972rad)
  Width = 200
FEATURE [Part::Box] Box1042  label="Krychle1042"
  AttacherType = Attacher::AttachEngine3D
  Height = 2
  Length = 6
  Placement = pos=(-63.4519,40.0981,39) rot=(0,0,1;4.18879rad)
  Width = 8
FEATURE [Part::Box] Box1044  label="Krychle1044"
  AttacherType = Attacher::AttachEngine3D
  Height = 60
  Length = 200
  Placement = pos=(0,0,-5) rot=(0,0,1;3.52556rad)
  Width = 200
FEATURE [Part::Cylinder] Cylinder2409  label="Válec2409"
  Angle = 360
  AttacherType = Attacher::AttachEngine3D
  Height = 72
  Placement = pos=(71,-1.8e-14,0) rot=(0,0,1;1.5708rad)
  Radius = 1.5
FEATURE [Part::Box] Box1036  label="Krychle1036"
  AttacherType = Attacher::AttachEngine3D
  Height = 49
  Length = 56
  Placement = pos=(-28,35,29) rot=(0,0,1;0rad)
  Width = 200
FEATURE [Part::Box] Box1047  label="Krychle1047"
  AttacherType = Attacher::AttachEngine3D
  Height = 2
  Length = 6
  Placement = pos=(-34.9019,66.4519,39) rot=(0,0,1;3.66519rad)
  Width = 8
FEATURE [Part::Cylinder] Cylinder2410  label="Válec2410"
  Angle = 360
  AttacherType = Attacher::AttachEngine3D
  Height = 50
  Placement = pos=(-18,100,72) rot=(1,0,0;1.5708rad)
  Radius = 1.5
FEATURE [Part::Cylinder] Cylinder2411  label="Válec2411"
  Angle = 360
  AttacherType = Attacher::AttachEngine3D
  Height = 72
  Placement = pos=(-35.5,-61.4878,0) rot=(0,0,-1;0.523599rad)
  Radius = 1.5
FEATURE [Part::Box] Box1048  label="Krychle1048"
  AttacherType = Attacher::AttachEngine3D
  Height = 2
  Length = 6
  Placement = pos=(-66.4519,-34.9019,39) rot=(0,0,-1;1.0472rad)
  Width = 8
FEATURE [Part::Cylinder] Cylinder2307  label="Válec2307"
  Angle = 360
  AttacherType = Attacher::AttachEngine3D
  Height = 160
  Placement = pos=(0,0,-60) rot=(0,0,1;0rad)
  Radius = 30
FEATURE [Part::Cylinder] Cylinder2412  label="Válec2412"
  Angle = 360
  AttacherType = Attacher::AttachEngine3D
  Height = 72
  Placement = pos=(-71,2.7e-14,0) rot=(0,0,-1;1.5708rad)
  Radius = 1.5
FEATURE [Part::Cylinder] Cylinder2413  label="Válec2413"
  Angle = 360
  AttacherType = Attacher::AttachEngine3D
  Height = 72
  Placement = pos=(-61.4878,35.5,0) rot=(0,0,1;4.18879rad)
  Radius = 1.5
FEATURE [Part::Box] Box1164  label="Krychle1164"
  AttacherType = Attacher::AttachEngine3D
  Height = 2
  Length = 6
  Placement = pos=(66.4519,34.9019,39) rot=(0,0,1;2.0944rad)
  Width = 8
FEATURE [Part::Box] Box1149  label="Krychle1149"
  AttacherType = Attacher::AttachEngine3D
  Height = 40
  Length = 34
  Placement = pos=(-6,0,78) rot=(0,0,-1;0.523599rad)
  Width = 100
FEATURE [Part::Cylinder] Cylinder2414  label="Válec2414"
  Angle = 360
  AttacherType = Attacher::AttachEngine3D
  Height = 72
  Placement = pos=(35.5,61.4878,0) rot=(0,0,1;2.61799rad)
  Radius = 1.5
FEATURE [Part::Cylinder] Cylinder2309  label="Válec2309"
  Angle = 360
  AttacherType = Attacher::AttachEngine3D
  Height = 50
  Placement = pos=(71,80,39) rot=(1,0,0;1.5708rad)
  Radius = 1.5
FEATURE [Part::Box] Box1050  label="Krychle1050"
  AttacherType = Attacher::AttachEngine3D
  Height = 2
  Length = 6
  Placement = pos=(63.45,-40.1,58) rot=(0,0,1;1.0472rad)
  Width = 8
FEATURE [Part::Box] Box1051  label="Krychle1051"
  AttacherType = Attacher::AttachEngine3D
  Height = 6
  Length = 6
  Placement = pos=(-21,64,-50) rot=(0,0,1;0rad)
  Width = 4
FEATURE [Part::Cylinder] Cylinder2415  label="Válec2415"
  Angle = 360
  AttacherType = Attacher::AttachEngine3D
  Height = 72
  Placement = pos=(-35.5,61.4878,0) rot=(0,0,1;3.66519rad)
  Radius = 1.5
FEATURE [Part::Box] Box1156  label="Krychle1156"
  AttacherType = Attacher::AttachEngine3D
  Height = 6
  Length = 8
  Placement = pos=(67,38,70) rot=(0,0,1;0rad)
  Width = 2
FEATURE [Part::Box] Box1157  label="Krychle1157"
  AttacherType = Attacher::AttachEngine3D
  Height = 6
  Length = 8
  Placement = pos=(-75,38,53) rot=(0,0,1;0rad)
  Width = 2
FEATURE [Part::Box] Box1162  label="Krychle1162"
  AttacherType = Attacher::AttachEngine3D
  Height = 6
  Length = 8
  Placement = pos=(-75,38,70) rot=(0,0,1;0rad)
  Width = 2
FEATURE [Part::Cylinder] Cylinder2306  label="Válec2306"
  Angle = 360
  AttacherType = Attacher::AttachEngine3D
  Height = 10
  Placement = pos=(0,0,61) rot=(0,0,1;0rad)
  Radius = 74
FEATURE [Part::Cylinder] Cylinder2310  label="Válec2310"
  Angle = 360
  AttacherType = Attacher::AttachEngine3D
  Height = 50
  Placement = pos=(-71,80,73) rot=(1,0,0;1.5708rad)
  Radius = 1.5
FEATURE [Part::Cylinder] Cylinder2416  label="Válec2416"
  Angle = 360
  AttacherType = Attacher::AttachEngine3D
  Height = 50
  Placement = pos=(-9,100,59) rot=(1,0,0;1.5708rad)
  Radius = 1.5
FEATURE [Part::Box] Box1153  label="Krychle1153"
  AttacherType = Attacher::AttachEngine3D
  Height = 34
  Length = 148
  Placement = pos=(-74,68,38) rot=(0,0,1;0rad)
  Width = 20
FEATURE [Part::Box] Box1158  label="Krychle1158"
  AttacherType = Attacher::AttachEngine3D
  Height = 6
  Length = 8
  Placement = pos=(67,38,53) rot=(0,0,1;0rad)
  Width = 2
FEATURE [Part::Box] Box1161  label="Krychle1161"
  AttacherType = Attacher::AttachEngine3D
  Height = 2
  Length = 6
  Placement = pos=(-3,-75,39) rot=(0,0,1;0rad)
  Width = 8
FEATURE [Part::Box] Box1165  label="Krychle1165"
  AttacherType = Attacher::AttachEngine3D
  Height = 2
  Length = 6
  Placement = pos=(34.9019,-66.4519,39) rot=(0,0,1;0.523599rad)
  Width = 8
FEATURE [Part::Box] Box1155  label="Krychle1155"
  AttacherType = Attacher::AttachEngine3D
  Height = 2
  Length = 6
  Placement = pos=(75,-3,39) rot=(0,0,1;1.5708rad)
  Width = 8
FEATURE [Part::Box] Box1172  label="Krychle1172"
  AttacherType = Attacher::AttachEngine3D
  Height = 55
  Length = 148
  Placement = pos=(-74,0,29) rot=(0,0,1;0rad)
  Width = 74
FEATURE [Part::Cylinder] Cylinder2308  label="Válec2308"
  Angle = 360
  AttacherType = Attacher::AttachEngine3D
  Height = 50
  Placement = pos=(-71,80,39) rot=(1,0,0;1.5708rad)
  Radius = 1.5
FEATURE [Part::Box] Box1160  label="Krychle1160"
  AttacherType = Attacher::AttachEngine3D
  Height = 2
  Length = 6
  Placement = pos=(-75,3,39) rot=(0,0,-1;1.5708rad)
  Width = 8
FEATURE [Part::Box] Box1163  label="Krychle1163"
  AttacherType = Attacher::AttachEngine3D
  Height = 2
  Length = 6
  Placement = pos=(-66.4519,-34.9019,39) rot=(0,0,-1;1.0472rad)
  Width = 8
FEATURE [Part::Box] Box1175  label="Krychle1175"
  AttacherType = Attacher::AttachEngine3D
  Height = 40
  Length = 34
  Placement = pos=(-6,0,78) rot=(0,0,-1;0.523599rad)
  Width = 100
FEATURE [Part::Box] Box1159  label="Krychle1159"
  AttacherType = Attacher::AttachEngine3D
  Height = 2
  Length = 6
  Placement = pos=(-34.9019,66.4519,39) rot=(0,0,1;3.66519rad)
  Width = 8
FEATURE [Part::Box] Box1166  label="Krychle1166"
  AttacherType = Attacher::AttachEngine3D
  Height = 6
  Length = 8
  Placement = pos=(67,38,36) rot=(0,0,1;0rad)
  Width = 2
FEATURE [Part::Box] Box1154  label="Krychle1154"
  AttacherType = Attacher::AttachEngine3D
  Height = 2
  Length = 6
  Placement = pos=(63.4519,-40.0981,39) rot=(0,0,1;1.0472rad)
  Width = 8
FEATURE [Part::Compound] Compound1185
  Links = -> [Cylinder2152,Cylinder2145]
  Placement = pos=(-21.5,0,0) rot=(0,0,1;1.5708rad)
FEATURE [Part::Compound] Compound1186
  Links = -> [Cylinder2148,Cylinder2149]
  Placement = pos=(1.5,0,0) rot=(0,0,1;1.5708rad)
FEATURE [Part::Compound] Compound1184
  Links = -> [Compound1186,Compound1185]
FEATURE [Part::Compound] Compound1183
  Links = -> [Compound1181,Compound1184,mirror042]
FEATURE [Part::Compound] Compound1187
  Links = -> [Cylinder2410]
  Placement = pos=(0,0,0) rot=(0,0,1;3.92699rad)
FEATURE [Part::FeaturePython] Tube055  # WARN: FeaturePython — macro-defined, semantics opaque (R4)
  AttacherType = Attacher::AttachEngine3D
  Height = 8
  InnerRadius = 55.1
  OuterRadius = 63
  Placement = pos=(0,0,68) rot=(0,0,1;0rad)
FEATURE [Part::FeaturePython] Tube056  # WARN: FeaturePython — macro-defined, semantics opaque (R4)
  AttacherType = Attacher::AttachEngine3D
  Height = 55
  InnerRadius = 68
  OuterRadius = 74
  Placement = pos=(0,0,29) rot=(0,0,1;0rad)
FEATURE [Part::Compound] Compound1190
  Links = -> [Box1312,Box1302,Box1310,Box1311]
FEATURE [Part::Mirroring] mirror043  label="Compound998 (mirrored)003"
  Base = (0,0,0)
  Normal = (1,0,0)
  Source = -> Compound1190
FEATURE [Part::Compound] Compound1191
  Links = -> [Box1309,Box1295,Box1301,Box1300]
FEATURE [Part::Compound] Compound1192
  Links = -> [Box1308,Box1307]
  Placement = pos=(-21.5,0,0) rot=(0,0,1;1.5708rad)
FEATURE [Part::Compound] Compound1194
  Links = -> [Box1316,Box1317,Box1318,Box1315]
FEATURE [Part::Mirroring] mirror044  label="Compound999 (mirrored)003"
  Base = (0,0,0)
  Normal = (1,0,0)
  Source = -> Compound1194
FEATURE [Part::Compound] Compound1196
  Links = -> [Box1313,Box1298]
  Placement = pos=(-21.5,0,0) rot=(0,0,1;1.5708rad)
FEATURE [Part::Compound] Compound1198
  Links = -> [Box1304,Box1303,Box1306,Box1314]
FEATURE [Part::Compound] Compound1199
  Links = -> [Box1299,Box1297]
  Placement = pos=(1.5,0,0) rot=(0,0,1;1.5708rad)
FEATURE [Part::Compound] Compound1197
  Links = -> [Compound1196,Compound1199]
FEATURE [Part::Compound] Compound1195
  Links = -> [Compound1198,Compound1197,mirror044]
FEATURE [Part::Cut] Cut812
  Base = -> Tube056
  Tool = -> Box1036
FEATURE [Part::Cut] Cut811
  Base = -> Cut812
  Tool = -> Box1037
FEATURE [Part::Cut] Cut754
  Base = -> Cylinder2306
  Placement = pos=(0,0,13) rot=(0,0,1;0rad)
  Tool = -> Box1153
FEATURE [Part::Cut] Cut755
  Base = -> Cut754
  Tool = -> Cylinder2307
FEATURE [Part::Cut] Cut762
  Base = -> Cut755
  Tool = -> Box1149
FEATURE [Part::Cut] Cut814
  Base = -> Box1033
  Tool = -> Box1040
FEATURE [Part::Cut] Cut806
  Base = -> Cut814
  Tool = -> Box1044
FEATURE [Part::Cut] Cut810
  Base = -> Cut811
  Tool = -> Cut806
FEATURE [Part::Compound] Compound1200
  Links = -> [Box1296,Box1305]
  Placement = pos=(1.5,0,0) rot=(0,0,1;1.5708rad)
FEATURE [Part::Compound] Compound1188
  Links = -> [Compound1192,Compound1200]
FEATURE [Part::Compound] Compound1189
  Links = -> [Compound1191,Compound1188,mirror043]
FEATURE [Part::Compound] Compound1202
  Links = -> [Box1034,Box1039,Box1050,Box1043,Box1045,Box1038,Box1032,Box1047,Box1042,Box1041,Box1048,Box1046]
FEATURE [Part::Cut] Cut813
  Base = -> Cut810
  Tool = -> Compound1202
FEATURE [Part::Compound] Compound1203
  Links = -> [Cylinder2402]
  Placement = pos=(0,0,0) rot=(0,0,1;3.92699rad)
FEATURE [Part::Compound] Compound1204
  Links = -> [Box1051,Box1031]
  Placement = pos=(0,0,120) rot=(0,0,1;3.92699rad)
FEATURE [Part::Compound] Compound1206
  Links = -> [Box1049,Box1035]
  Placement = pos=(0,0,120) rot=(0,0,1;3.92699rad)
FEATURE [Part::Compound] Compound1207
  Links = -> [Cylinder2416]
  Placement = pos=(0,0,0) rot=(0,0,1;3.92699rad)
FEATURE [Part::Compound] Compound1205
  Links = -> [Compound1207,Compound1203]
  Placement = pos=(0,0,1) rot=(0,0,1;0rad)
FEATURE [Part::Compound] Compound1208
  Links = -> [Cylinder2406,Cylinder2408,Cylinder2401,Cylinder2409,Cylinder2404,Cylinder2414,Cylinder2403,Cylinder2415,Cylinder2413,Cylinder2412,Cylinder2407,Cylinder2411]
  Placement = pos=(0,0,-4) rot=(0,0,1;0rad)
FEATURE [Part::Cut] Cut815
  Base = -> Cut813
  Tool = -> Compound1208
FEATURE [Part::Compound] Compound1209
  Links = -> [Cylinder2405]
  Placement = pos=(0,0,0) rot=(0,0,1;3.92699rad)
FEATURE [Part::Compound] Compound1201
  Links = -> [Compound1187,Compound1209]
  Placement = pos=(0,0,1) rot=(0,0,1;0rad)
FEATURE [Part::Cut] Cut816
  Base = -> Cut815
  Tool = -> Compound1201
FEATURE [Part::Cut] Cut809
  Base = -> Cut816
  Tool = -> Compound1204
FEATURE [Part::Cut] Cut808
  Base = -> Cut809
  Tool = -> Compound1205
FEATURE [Part::Cut] Cut807
  Base = -> Cut808
  Tool = -> Compound1206
FEATURE [Part::Cut] Cut764
  Base = -> Cut807
  Tool = -> Box1175
FEATURE [Part::Cylinder] Cylinder2342  label="Válec2342"
  Angle = 360
  AttacherType = Attacher::AttachEngine3D
  Height = 200
  Placement = pos=(0,0,81) rot=(0.186157,0.694747,0.694747;2.77349rad)
  Radius = 2.5
FEATURE [Part::Box] Box1268  label="Krychle1268"
  AttacherType = Attacher::AttachEngine3D
  Height = 20
  Length = 8
  Placement = pos=(50.79,34,80) rot=(0,0,-1;0.698132rad)
  Width = 6
FEATURE [Part::Cylinder] Cylinder2337  label="Válec2337"
  Angle = 360
  AttacherType = Attacher::AttachEngine3D
  Height = 200
  Placement = pos=(6,0,81) rot=(0.186157,0.694747,0.694747;2.7735rad)
  Radius = 2.5
FEATURE [Part::Cylinder] Cylinder2341  label="Válec2341"
  Angle = 360
  AttacherType = Attacher::AttachEngine3D
  Height = 200
  Placement = pos=(24,0,81) rot=(0.186157,0.694747,0.694747;2.7735rad)
  Radius = 2.5
FEATURE [Part::Cylinder] Cylinder2347  label="Válec2347"
  Angle = 360
  AttacherType = Attacher::AttachEngine3D
  Height = 200
  Placement = pos=(24,0,81) rot=(0.186157,0.694747,0.694747;2.7735rad)
  Radius = 2.5
FEATURE [Part::Cylinder] Cylinder2345  label="Válec2345"
  Angle = 360
  AttacherType = Attacher::AttachEngine3D
  Height = 200
  Placement = pos=(30,0,81) rot=(0.186157,0.694747,0.694747;2.7735rad)
  Radius = 2.5
FEATURE [Part::Box] Box1263  label="Krychle1263"
  AttacherType = Attacher::AttachEngine3D
  Height = 20
  Length = 8
  Placement = pos=(7.64,33.65,80) rot=(0,0,-1;0.872665rad)
  Width = 6
FEATURE [Part::Cylinder] Cylinder2340  label="Válec2340"
  Angle = 360
  AttacherType = Attacher::AttachEngine3D
  Height = 200
  Placement = pos=(18,0,81) rot=(0.186157,0.694747,0.694747;2.7735rad)
  Radius = 2.5
FEATURE [Part::Cylinder] Cylinder2333  label="Válec2333"
  Angle = 360
  AttacherType = Attacher::AttachEngine3D
  Height = 200
  Placement = pos=(18,0,81) rot=(0.186157,0.694747,0.694747;2.7735rad)
  Radius = 2.5
FEATURE [Part::Cylinder] Cylinder2350  label="Válec2350"
  Angle = 360
  AttacherType = Attacher::AttachEngine3D
  Height = 200
  Placement = pos=(12,0,81) rot=(0.186157,0.694747,0.694747;2.7735rad)
  Radius = 2.5
FEATURE [Part::Cylinder] Cylinder2343  label="Válec2343"
  Angle = 360
  AttacherType = Attacher::AttachEngine3D
  Height = 200
  Placement = pos=(6,0,81) rot=(0.186157,0.694747,0.694747;2.7735rad)
  Radius = 2.5
FEATURE [Part::Cylinder] Cylinder2335  label="Válec2335"
  Angle = 360
  AttacherType = Attacher::AttachEngine3D
  Height = 200
  Placement = pos=(24,0,81) rot=(0.186157,0.694747,0.694747;2.7735rad)
  Radius = 2.5
FEATURE [Part::Cylinder] Cylinder2334  label="Válec2334"
  Angle = 360
  AttacherType = Attacher::AttachEngine3D
  Height = 200
  Placement = pos=(30,0,81) rot=(0.186157,0.694747,0.694747;2.7735rad)
  Radius = 2.5
FEATURE [Part::Box] Box1270  label="Krychle1270"
  AttacherType = Attacher::AttachEngine3D
  Height = 55
  Length = 148
  Placement = pos=(-74,0,29) rot=(0,0,1;0rad)
  Width = 74
FEATURE [Part::Cut] Cut798
  Base = -> Tube054
  Placement = pos=(0,0,4) rot=(0,0,1;0rad)
  Tool = -> Box1270
FEATURE [Part::Cylinder] Cylinder2348  label="Válec2348"
  Angle = 360
  AttacherType = Attacher::AttachEngine3D
  Height = 200
  Placement = pos=(0,0,81) rot=(0.186157,0.694747,0.694747;2.77349rad)
  Radius = 2.5
FEATURE [Part::Cylinder] Cylinder2339  label="Válec2339"
  Angle = 360
  AttacherType = Attacher::AttachEngine3D
  Height = 200
  Placement = pos=(30,0,81) rot=(0.186157,0.694747,0.694747;2.7735rad)
  Radius = 2.5
FEATURE [Part::Cylinder] Cylinder2338  label="Válec2338"
  Angle = 360
  AttacherType = Attacher::AttachEngine3D
  Height = 200
  Placement = pos=(12,0,81) rot=(0.186157,0.694747,0.694747;2.7735rad)
  Radius = 2.5
FEATURE [Part::Cylinder] Cylinder2344  label="Válec2344"
  Angle = 360
  AttacherType = Attacher::AttachEngine3D
  Height = 200
  Placement = pos=(12,0,81) rot=(0.186157,0.694747,0.694747;2.7735rad)
  Radius = 2.5
FEATURE [Part::Cylinder] Cylinder2346  label="Válec2346"
  Angle = 360
  AttacherType = Attacher::AttachEngine3D
  Height = 200
  Placement = pos=(18,0,81) rot=(0.186157,0.694747,0.694747;2.7735rad)
  Radius = 2.5
FEATURE [Part::Compound] Compound1141
  Links = -> [Cylinder2342,Cylinder2343,Cylinder2344,Cylinder2346,Cylinder2341,Cylinder2345]
  Placement = pos=(-6.01912,-7.56902,40.5645) rot=(-0.866025,0.5,0;0.785398rad)
FEATURE [Part::Cylinder] Cylinder2336  label="Válec2336"
  Angle = 360
  AttacherType = Attacher::AttachEngine3D
  Height = 200
  Placement = pos=(0,0,81) rot=(0.186157,0.694747,0.694747;2.77349rad)
  Radius = 2.5
FEATURE [Part::Compound] Compound1140
  Links = -> [Cylinder2336,Cylinder2337,Cylinder2338,Cylinder2340,Cylinder2335,Cylinder2339]
  Placement = pos=(-6.01912,-7.56902,40.5645) rot=(-0.866025,0.5,0;0.785398rad)
FEATURE [Part::Box] Box1178  label="Krychle1178"
  AttacherType = Attacher::AttachEngine3D
  Height = 40
  Length = 34
  Placement = pos=(23.08,50.36,89.4) rot=(-0.819161,0.219493,-0.529904;0.936369rad)
  Width = 100
FEATURE [Part::Box] Box1198  label="Krychle1198"
  AttacherType = Attacher::AttachEngine3D
  Height = 100
  Length = 1.5
  Placement = pos=(8.63532,33.646,7e-15) rot=(0,0,-1;0.872665rad)
  Width = 4
FEATURE [Part::Cylinder] Cylinder2352  label="Válec2352"
  Angle = 360
  AttacherType = Attacher::AttachEngine3D
  Height = 200
  Placement = pos=(18,0,81) rot=(0.186157,0.694747,0.694747;2.7735rad)
  Radius = 2.5
FEATURE [Part::Box] Box1195  label="Krychle1195"
  AttacherType = Attacher::AttachEngine3D
  Height = 100
  Length = 1.5
  Placement = pos=(53.7894,33.3071,0) rot=(0,0,-1;0.698132rad)
  Width = 4
FEATURE [Part::Box] Box1179  label="Krychle1179"
  AttacherType = Attacher::AttachEngine3D
  Height = 40
  Length = 34
  Placement = pos=(23.08,50.36,89.4) rot=(-0.819161,0.219493,-0.529904;0.936369rad)
  Width = 100
FEATURE [Part::Cylinder] Cylinder2351  label="Válec2351"
  Angle = 360
  AttacherType = Attacher::AttachEngine3D
  Height = 200
  Placement = pos=(30,0,81) rot=(0.186157,0.694747,0.694747;2.7735rad)
  Radius = 2.5
FEATURE [Part::Box] Box1193  label="Krychle1193"
  AttacherType = Attacher::AttachEngine3D
  Height = 100
  Length = 1.5
  Placement = pos=(33.6353,-2.354,7e-15) rot=(0,0,-1;0.872665rad)
  Width = 4
FEATURE [Part::Box] Box1188  label="Krychle1188"
  AttacherType = Attacher::AttachEngine3D
  Height = 100
  Length = 1.5
  Placement = pos=(23.7894,59.3071,0) rot=(0,0,-1;0.698132rad)
  Width = 4
FEATURE [Part::Box] Box1191  label="Krychle1191"
  AttacherType = Attacher::AttachEngine3D
  Height = 100
  Length = 1.5
  Placement = pos=(53.7894,33.3071,0) rot=(0,0,-1;0.698132rad)
  Width = 4
FEATURE [Part::Box] Box1177  label="Krychle1177"
  AttacherType = Attacher::AttachEngine3D
  Height = 40
  Length = 34
  Placement = pos=(23.08,50.36,89.4) rot=(-0.819161,0.219493,-0.529904;0.936369rad)
  Width = 100
FEATURE [Part::Box] Box1190  label="Krychle1190"
  AttacherType = Attacher::AttachEngine3D
  Height = 100
  Length = 1.5
  Placement = pos=(8.63532,33.646,7e-15) rot=(0,0,-1;0.872665rad)
  Width = 4
FEATURE [Part::Box] Box1194  label="Krychle1194"
  AttacherType = Attacher::AttachEngine3D
  Height = 100
  Length = 1.5
  Placement = pos=(8.63532,33.646,7e-15) rot=(0,0,-1;0.872665rad)
  Width = 4
FEATURE [Part::Cylinder] Cylinder2356  label="Válec2356"
  Angle = 360
  AttacherType = Attacher::AttachEngine3D
  Height = 200
  Placement = pos=(6,0,81) rot=(0.186157,0.694747,0.694747;2.7735rad)
  Radius = 2.5
FEATURE [Part::Cylinder] Cylinder2360  label="Válec2360"
  Angle = 360
  AttacherType = Attacher::AttachEngine3D
  Height = 200
  Placement = pos=(12,0,81) rot=(0.186157,0.694747,0.694747;2.7735rad)
  Radius = 2.5
FEATURE [Part::Cylinder] Cylinder2349  label="Válec2349"
  Angle = 360
  AttacherType = Attacher::AttachEngine3D
  Height = 200
  Placement = pos=(6,0,81) rot=(0.186157,0.694747,0.694747;2.7735rad)
  Radius = 2.5
FEATURE [Part::Compound] Compound1142
  Links = -> [Cylinder2348,Cylinder2349,Cylinder2350,Cylinder2352,Cylinder2347,Cylinder2351]
  Placement = pos=(-6.01912,-7.56902,40.5645) rot=(-0.866025,0.5,0;0.785398rad)
FEATURE [Part::Box] Box1189  label="Krychle1189"
  AttacherType = Attacher::AttachEngine3D
  Height = 100
  Length = 1.5
  Placement = pos=(33.6353,-2.354,7e-15) rot=(0,0,-1;0.872665rad)
  Width = 4
FEATURE [Part::Compound] Compound1145
  Links = -> [Box1188,Box1190,Box1189,Box1191]
FEATURE [Part::Box] Box1192  label="Krychle1192"
  AttacherType = Attacher::AttachEngine3D
  Height = 100
  Length = 1.5
  Placement = pos=(23.7894,59.3071,0) rot=(0,0,-1;0.698132rad)
  Width = 4
FEATURE [Part::Compound] Compound1146
  Links = -> [Box1192,Box1194,Box1193,Box1195]
FEATURE [Part::Cylinder] Cylinder2359  label="Válec2359"
  Angle = 360
  AttacherType = Attacher::AttachEngine3D
  Height = 200
  Placement = pos=(24,0,81) rot=(0.186157,0.694747,0.694747;2.7735rad)
  Radius = 2.5
FEATURE [Part::Cylinder] Cylinder2358  label="Válec2358"
  Angle = 360
  AttacherType = Attacher::AttachEngine3D
  Height = 200
  Placement = pos=(24,0,81) rot=(0.186157,0.694747,0.694747;2.7735rad)
  Radius = 2.5
FEATURE [Part::Cylinder] Cylinder2361  label="Válec2361"
  Angle = 360
  AttacherType = Attacher::AttachEngine3D
  Height = 200
  Placement = pos=(0,0,81) rot=(0.186157,0.694747,0.694747;2.77349rad)
  Radius = 2.5
FEATURE [Part::Box] Box1214  label="Krychle1214"
  AttacherType = Attacher::AttachEngine3D
  Height = 100
  Length = 1.5
  Placement = pos=(23.7894,59.3071,0) rot=(0,0,-1;0.698132rad)
  Width = 4
FEATURE [Part::Cylinder] Cylinder2353  label="Válec2353"
  Angle = 360
  AttacherType = Attacher::AttachEngine3D
  Height = 200
  Placement = pos=(0,0,81) rot=(0.186157,0.694747,0.694747;2.77349rad)
  Radius = 2.5
FEATURE [Part::Box] Box1196  label="Krychle1196"
  AttacherType = Attacher::AttachEngine3D
  Height = 100
  Length = 1.5
  Placement = pos=(23.7894,59.3071,0) rot=(0,0,-1;0.698132rad)
  Width = 4
FEATURE [Part::Box] Box1199  label="Krychle1199"
  AttacherType = Attacher::AttachEngine3D
  Height = 100
  Length = 1.5
  Placement = pos=(53.7894,33.3071,0) rot=(0,0,-1;0.698132rad)
  Width = 4
FEATURE [Part::Box] Box1201  label="Krychle1201"
  AttacherType = Attacher::AttachEngine3D
  Height = 20
  Length = 8
  Placement = pos=(22.79,59.31,80) rot=(0,0,-1;0.698132rad)
  Width = 6
FEATURE [Part::Box] Box1197  label="Krychle1197"
  AttacherType = Attacher::AttachEngine3D
  Height = 100
  Length = 1.5
  Placement = pos=(33.6353,-2.354,7e-15) rot=(0,0,-1;0.872665rad)
  Width = 4
FEATURE [Part::Compound] Compound1147
  Links = -> [Box1196,Box1198,Box1197,Box1199]
FEATURE [Part::Cylinder] Cylinder2355  label="Válec2355"
  Angle = 360
  AttacherType = Attacher::AttachEngine3D
  Height = 200
  Placement = pos=(18,0,81) rot=(0.186157,0.694747,0.694747;2.7735rad)
  Radius = 2.5
FEATURE [Part::Box] Box1202  label="Krychle1202"
  AttacherType = Attacher::AttachEngine3D
  Height = 20
  Length = 8
  Placement = pos=(50.79,34,80) rot=(0,0,-1;0.698132rad)
  Width = 6
FEATURE [Part::Box] Box1200  label="Krychle1200"
  AttacherType = Attacher::AttachEngine3D
  Height = 20
  Length = 8
  Placement = pos=(7.64,33.65,80) rot=(0,0,-1;0.872665rad)
  Width = 6
FEATURE [Part::Cylinder] Cylinder2354  label="Válec2354"
  Angle = 360
  AttacherType = Attacher::AttachEngine3D
  Height = 200
  Placement = pos=(30,0,81) rot=(0.186157,0.694747,0.694747;2.7735rad)
  Radius = 2.5
FEATURE [Part::Box] Box1212  label="Krychle1212"
  AttacherType = Attacher::AttachEngine3D
  Height = 40
  Length = 34
  Placement = pos=(-6,0,78) rot=(0,0,-1;0.523599rad)
  Width = 100
FEATURE [Part::Mirroring] mirror024  label="Krychle1212 (mirrored)"
  Base = (0,0,0)
  Normal = (1,0,0)
  Source = -> Box1212
FEATURE [Part::Box] Box1203  label="Krychle1203"
  AttacherType = Attacher::AttachEngine3D
  Height = 20
  Length = 8
  Placement = pos=(30,-0.35,80) rot=(0,0,-1;0.872665rad)
  Width = 6
FEATURE [Part::Compound] Compound1148
  Links = -> [Box1201,Box1200,Box1202,Box1203]
FEATURE [Part::Cylinder] Cylinder2357  label="Válec2357"
  Angle = 360
  AttacherType = Attacher::AttachEngine3D
  Height = 200
  Placement = pos=(12,0,81) rot=(0.186157,0.694747,0.694747;2.7735rad)
  Radius = 2.5
FEATURE [Part::Compound] Compound1151
  Links = -> [Cylinder2353,Cylinder2356,Cylinder2357,Cylinder2355,Cylinder2358,Cylinder2354]
  Placement = pos=(-8,-11,-2) rot=(0,0,1;0rad)
FEATURE [Part::Mirroring] mirror021  label="Compound1151 (mirrored)"
  Base = (0,0,0)
  Normal = (1,0,0)
  Source = -> Compound1151
FEATURE [Part::Box] Box1213  label="Krychle1213"
  AttacherType = Attacher::AttachEngine3D
  Height = 40
  Length = 34
  Placement = pos=(23.08,50.36,89.4) rot=(-0.819161,0.219493,-0.529904;0.936369rad)
  Width = 100
FEATURE [Part::Mirroring] mirror025  label="Krychle1213 (mirrored)"
  Base = (0,0,0)
  Normal = (1,0,0)
  Source = -> Box1213
FEATURE [Part::Cylinder] Cylinder2362  label="Válec2362"
  Angle = 360
  AttacherType = Attacher::AttachEngine3D
  Height = 200
  Placement = pos=(6,0,81) rot=(0.186157,0.694747,0.694747;2.7735rad)
  Radius = 2.5
FEATURE [Part::Cylinder] Cylinder2363  label="Válec2363"
  Angle = 360
  AttacherType = Attacher::AttachEngine3D
  Height = 200
  Placement = pos=(30,0,81) rot=(0.186157,0.694747,0.694747;2.7735rad)
  Radius = 2.5
FEATURE [Part::Box] Box1216  label="Krychle1216"
  AttacherType = Attacher::AttachEngine3D
  Height = 100
  Length = 1.5
  Placement = pos=(53.7894,33.3071,0) rot=(0,0,-1;0.698132rad)
  Width = 4
FEATURE [Part::Box] Box1215  label="Krychle1215"
  AttacherType = Attacher::AttachEngine3D
  Height = 100
  Length = 1.5
  Placement = pos=(33.6353,-2.354,7e-15) rot=(0,0,-1;0.872665rad)
  Width = 4
FEATURE [Part::Cylinder] Cylinder2364  label="Válec2364"
  Angle = 360
  AttacherType = Attacher::AttachEngine3D
  Height = 200
  Placement = pos=(18,0,81) rot=(0.186157,0.694747,0.694747;2.7735rad)
  Radius = 2.5
FEATURE [Part::Compound] Compound1154
  Links = -> [Cylinder2361,Cylinder2362,Cylinder2360,Cylinder2364,Cylinder2359,Cylinder2363]
  Placement = pos=(-6.01912,-7.56902,40.5645) rot=(-0.866025,0.5,0;0.785398rad)
FEATURE [Part::Mirroring] mirror026  label="Compound1154 (mirrored)"
  Base = (0,0,0)
  Normal = (1,0,0)
  Source = -> Compound1154
FEATURE [Part::Box] Box1218  label="Krychle1218"
  AttacherType = Attacher::AttachEngine3D
  Height = 20
  Length = 8
  Placement = pos=(7.64,33.65,80) rot=(0,0,-1;0.872665rad)
  Width = 6
FEATURE [Part::Box] Box1219  label="Krychle1219"
  AttacherType = Attacher::AttachEngine3D
  Height = 20
  Length = 8
  Placement = pos=(22.79,59.31,80) rot=(0,0,-1;0.698132rad)
  Width = 6
FEATURE [Part::Cylinder] Cylinder2367  label="Válec2367"
  Angle = 360
  AttacherType = Attacher::AttachEngine3D
  Height = 200
  Placement = pos=(0,0,81) rot=(0.186157,0.694747,0.694747;2.77349rad)
  Radius = 2.5
FEATURE [Part::Box] Box1220  label="Krychle1220"
  AttacherType = Attacher::AttachEngine3D
  Height = 20
  Length = 8
  Placement = pos=(30,-0.35,80) rot=(0,0,-1;0.872665rad)
  Width = 6
FEATURE [Part::Compound] Compound1153
  Links = -> [Box1219,Box1218,Box1221,Box1220]
FEATURE [Part::Mirroring] mirror023  label="Compound1153 (mirrored)"
  Base = (0,0,0)
  Normal = (1,0,0)
  Source = -> Compound1153
FEATURE [Part::Box] Box1217  label="Krychle1217"
  AttacherType = Attacher::AttachEngine3D
  Height = 100
  Length = 1.5
  Placement = pos=(8.63532,33.646,7e-15) rot=(0,0,-1;0.872665rad)
  Width = 4
FEATURE [Part::Compound] Compound1152
  Links = -> [Box1214,Box1217,Box1215,Box1216]
FEATURE [Part::Mirroring] mirror022  label="Compound1152 (mirrored)"
  Base = (0,0,0)
  Normal = (1,0,0)
  Source = -> Compound1152
FEATURE [Part::Box] Box1171  label="Krychle1171"
  AttacherType = Attacher::AttachEngine3D
  Height = 6
  Length = 8
  Placement = pos=(-75,38,36) rot=(0,0,1;0rad)
  Width = 2
FEATURE [Part::Compound] Compound1135
  Links = -> [Box1171,Box1166,Box1156,Box1162,Box1157,Box1158]
FEATURE [Part::Cylinder] Cylinder2313  label="Válec2313"
  Angle = 360
  AttacherType = Attacher::AttachEngine3D
  Height = 50
  Placement = pos=(71,80,56) rot=(1,0,0;1.5708rad)
  Radius = 1.5
FEATURE [Part::Box] Box1173  label="Krychle1173"
  AttacherType = Attacher::AttachEngine3D
  Height = 2
  Length = 6
  Placement = pos=(-40.0981,-63.4519,39) rot=(0,0,-1;0.523599rad)
  Width = 8
FEATURE [Part::Cylinder] Cylinder2311  label="Válec2311"
  Angle = 360
  AttacherType = Attacher::AttachEngine3D
  Height = 50
  Placement = pos=(71,80,73) rot=(1,0,0;1.5708rad)
  Radius = 1.5
FEATURE [Part::Cylinder] Cylinder2312  label="Válec2312"
  Angle = 360
  AttacherType = Attacher::AttachEngine3D
  Height = 50
  Placement = pos=(-71,80,56) rot=(1,0,0;1.5708rad)
  Radius = 1.5
FEATURE [Part::Compound] Compound1134
  Links = -> [Cylinder2310,Cylinder2309,Cylinder2308,Cylinder2311,Cylinder2312,Cylinder2313]
FEATURE [Part::Cylinder] Cylinder2315  label="Válec2315"
  Angle = 360
  AttacherType = Attacher::AttachEngine3D
  Height = 160
  Placement = pos=(0,0,-60) rot=(0,0,1;0rad)
  Radius = 30
FEATURE [Part::Cylinder] Cylinder2326  label="Válec2326"
  Angle = 360
  AttacherType = Attacher::AttachEngine3D
  Height = 200
  Placement = pos=(6,0,81) rot=(0.186157,0.694747,0.694747;2.7735rad)
  Radius = 2.5
FEATURE [Part::Cylinder] Cylinder2331  label="Válec2331"
  Angle = 360
  AttacherType = Attacher::AttachEngine3D
  Height = 200
  Placement = pos=(0,0,81) rot=(0.186157,0.694747,0.694747;2.77349rad)
  Radius = 2.5
FEATURE [Part::Box] Box1169  label="Krychle1169"
  AttacherType = Attacher::AttachEngine3D
  Height = 2
  Length = 6
  Placement = pos=(40.0981,63.4519,39) rot=(0,0,1;2.61799rad)
  Width = 8
FEATURE [Part::Cylinder] Cylinder2324  label="Válec2324"
  Angle = 360
  AttacherType = Attacher::AttachEngine3D
  Height = 200
  Placement = pos=(12,0,81) rot=(0.186157,0.694747,0.694747;2.7735rad)
  Radius = 2.5
FEATURE [Part::Box] Box1167  label="Krychle1167"
  AttacherType = Attacher::AttachEngine3D
  Height = 2
  Length = 6
  Placement = pos=(-63.4519,40.0981,39) rot=(0,0,1;4.18879rad)
  Width = 8
FEATURE [Part::Cylinder] Cylinder2320  label="Válec2320"
  Angle = 360
  AttacherType = Attacher::AttachEngine3D
  Height = 200
  Placement = pos=(6,0,81) rot=(0.186157,0.694747,0.694747;2.7735rad)
  Radius = 2.5
FEATURE [Part::Cylinder] Cylinder2314  label="Válec2314"
  Angle = 360
  AttacherType = Attacher::AttachEngine3D
  Height = 51
  Placement = pos=(0,0,23) rot=(0,0,1;0rad)
  Radius = 74
FEATURE [Part::Cut] Cut759
  Base = -> Box1172
  Tool = -> Cylinder2314
FEATURE [Part::Box] Box1170  label="Krychle1170"
  AttacherType = Attacher::AttachEngine3D
  Height = 2
  Length = 6
  Placement = pos=(3,75,39) rot=(0,0,1;3.14159rad)
  Width = 8
FEATURE [Part::Compound] Compound1136
  Links = -> [Box1161,Box1165,Box1154,Box1155,Box1164,Box1169,Box1170,Box1159,Box1167,Box1160,Box1163,Box1173]
FEATURE [Part::Box] Box1174  label="Krychle1174"
  AttacherType = Attacher::AttachEngine3D
  Height = 40
  Length = 34
  Placement = pos=(-6,0,78) rot=(0,0,-1;0.523599rad)
  Width = 100
FEATURE [Part::Box] Box1168  label="Krychle1168"
  AttacherType = Attacher::AttachEngine3D
  Height = 55
  Length = 148
  Placement = pos=(-74,48,29) rot=(0,0,1;0rad)
  Width = 26
FEATURE [Part::Cut] Cut757
  Base = -> Cut759
  Tool = -> Box1168
FEATURE [Part::Cut] Cut760
  Base = -> Cut757
  Tool = -> Compound1134
FEATURE [Part::Cut] Cut756
  Base = -> Cut760
  Tool = -> Compound1135
FEATURE [Part::Cut] Cut758
  Base = -> Cut756
  Tool = -> Compound1136
FEATURE [Part::Cut] Cut761
  Base = -> Cut758
  Tool = -> Cylinder2315
FEATURE [Part::Cut] Cut763
  Base = -> Cut761
  Tool = -> Box1174
FEATURE [Part::Cylinder] Cylinder2317  label="Válec2317"
  Angle = 360
  AttacherType = Attacher::AttachEngine3D
  Height = 200
  Placement = pos=(24,0,81) rot=(0.186157,0.694747,0.694747;2.7735rad)
  Radius = 2.5
FEATURE [Part::Cylinder] Cylinder2319  label="Válec2319"
  Angle = 360
  AttacherType = Attacher::AttachEngine3D
  Height = 200
  Placement = pos=(0,0,81) rot=(0.186157,0.694747,0.694747;2.77349rad)
  Radius = 2.5
FEATURE [Part::Cylinder] Cylinder2321  label="Válec2321"
  Angle = 360
  AttacherType = Attacher::AttachEngine3D
  Height = 200
  Placement = pos=(18,0,81) rot=(0.186157,0.694747,0.694747;2.7735rad)
  Radius = 2.5
FEATURE [Part::Cylinder] Cylinder2323  label="Válec2323"
  Angle = 360
  AttacherType = Attacher::AttachEngine3D
  Height = 200
  Placement = pos=(24,0,81) rot=(0.186157,0.694747,0.694747;2.7735rad)
  Radius = 2.5
FEATURE [Part::Cylinder] Cylinder2327  label="Válec2327"
  Angle = 360
  AttacherType = Attacher::AttachEngine3D
  Height = 200
  Placement = pos=(18,0,81) rot=(0.186157,0.694747,0.694747;2.7735rad)
  Radius = 2.5
FEATURE [Part::Cylinder] Cylinder2322  label="Válec2322"
  Angle = 360
  AttacherType = Attacher::AttachEngine3D
  Height = 200
  Placement = pos=(30,0,81) rot=(0.186157,0.694747,0.694747;2.7735rad)
  Radius = 2.5
FEATURE [Part::Compound] Compound1137
  Links = -> [Cylinder2319,Cylinder2320,Cylinder2318,Cylinder2321,Cylinder2317,Cylinder2322]
  Placement = pos=(-8,-11,-2) rot=(0,0,1;0rad)
FEATURE [Part::Cut] Cut765
  Base = -> Cut762
  Tool = -> Compound1137
FEATURE [Part::Cut] Cut768
  Base = -> Cut765
  Tool = -> Compound1140
FEATURE [Part::Cut] Cut771
  Base = -> Cut768
  Tool = -> Box1177
FEATURE [Part::Cut] Cut774
  Base = -> Cut771
  Tool = -> Compound1147
FEATURE [Part::Cylinder] Cylinder2330  label="Válec2330"
  Angle = 360
  AttacherType = Attacher::AttachEngine3D
  Height = 200
  Placement = pos=(12,0,81) rot=(0.186157,0.694747,0.694747;2.7735rad)
  Radius = 2.5
FEATURE [Part::Cylinder] Cylinder2325  label="Válec2325"
  Angle = 360
  AttacherType = Attacher::AttachEngine3D
  Height = 200
  Placement = pos=(0,0,81) rot=(0.186157,0.694747,0.694747;2.77349rad)
  Radius = 2.5
FEATURE [Part::Cylinder] Cylinder2368  label="Válec2368"
  Angle = 360
  AttacherType = Attacher::AttachEngine3D
  Height = 200
  Placement = pos=(18,0,81) rot=(0.186157,0.694747,0.694747;2.7735rad)
  Radius = 2.5
FEATURE [Part::Box] Box1224  label="Krychle1224"
  AttacherType = Attacher::AttachEngine3D
  Height = 40
  Length = 34
  Placement = pos=(23.08,50.36,89.4) rot=(-0.819161,0.219493,-0.529904;0.936369rad)
  Width = 100
FEATURE [Part::Mirroring] mirror030  label="Krychle1213 (mirrored)001"
  Base = (0,0,0)
  Normal = (1,0,0)
  Source = -> Box1224
FEATURE [Part::Cylinder] Cylinder2378  label="Válec2378"
  Angle = 360
  AttacherType = Attacher::AttachEngine3D
  Height = 200
  Placement = pos=(30,0,81) rot=(0.186157,0.694747,0.694747;2.7735rad)
  Radius = 2.5
FEATURE [Part::Box] Box1230  label="Krychle1230"
  AttacherType = Attacher::AttachEngine3D
  Height = 20
  Length = 8
  Placement = pos=(31,-1.35,80) rot=(0,0,-1;0.872665rad)
  Width = 6
FEATURE [Part::Box] Box1232  label="Krychle1232"
  AttacherType = Attacher::AttachEngine3D
  Height = 40
  Length = 34
  Placement = pos=(-6,0,78) rot=(0,0,-1;0.523599rad)
  Width = 100
FEATURE [Part::Mirroring] mirror035  label="Krychle1212 (mirrored)002"
  Base = (0,0,0)
  Normal = (1,0,0)
  Source = -> Box1232
FEATURE [Part::Cylinder] Cylinder2374  label="Válec2374"
  Angle = 360
  AttacherType = Attacher::AttachEngine3D
  Height = 200
  Placement = pos=(12,0,81) rot=(0.186157,0.694747,0.694747;2.7735rad)
  Radius = 2.5
FEATURE [Part::Cylinder] Cylinder2373  label="Válec2373"
  Angle = 360
  AttacherType = Attacher::AttachEngine3D
  Height = 200
  Placement = pos=(18,0,81) rot=(0.186157,0.694747,0.694747;2.7735rad)
  Radius = 2.5
FEATURE [Part::Cylinder] Cylinder2369  label="Válec2369"
  Angle = 360
  AttacherType = Attacher::AttachEngine3D
  Height = 200
  Placement = pos=(30,0,81) rot=(0.186157,0.694747,0.694747;2.7735rad)
  Radius = 2.5
FEATURE [Part::Cylinder] Cylinder2372  label="Válec2372"
  Angle = 360
  AttacherType = Attacher::AttachEngine3D
  Height = 200
  Placement = pos=(12,0,81) rot=(0.186157,0.694747,0.694747;2.7735rad)
  Radius = 2.5
FEATURE [Part::Box] Box1223  label="Krychle1223"
  AttacherType = Attacher::AttachEngine3D
  Height = 100
  Length = 1.5
  Placement = pos=(23.7894,59.3071,0) rot=(0,0,-1;0.698132rad)
  Width = 4
FEATURE [Part::Box] Box1225  label="Krychle1225"
  AttacherType = Attacher::AttachEngine3D
  Height = 100
  Length = 1.5
  Placement = pos=(33.6353,-2.354,7e-15) rot=(0,0,-1;0.872665rad)
  Width = 4
FEATURE [Part::Cylinder] Cylinder2329  label="Válec2329"
  Angle = 360
  AttacherType = Attacher::AttachEngine3D
  Height = 200
  Placement = pos=(24,0,81) rot=(0.186157,0.694747,0.694747;2.7735rad)
  Radius = 2.5
FEATURE [Part::Cylinder] Cylinder2332  label="Válec2332"
  Angle = 360
  AttacherType = Attacher::AttachEngine3D
  Height = 200
  Placement = pos=(6,0,81) rot=(0.186157,0.694747,0.694747;2.7735rad)
  Radius = 2.5
FEATURE [Part::Compound] Compound1139
  Links = -> [Cylinder2331,Cylinder2332,Cylinder2330,Cylinder2333,Cylinder2329,Cylinder2334]
  Placement = pos=(-8,-11,-2) rot=(0,0,1;0rad)
FEATURE [Part::Cut] Cut767
  Base = -> Cut764
  Tool = -> Compound1139
FEATURE [Part::Cut] Cut770
  Base = -> Cut767
  Tool = -> Compound1142
FEATURE [Part::Cut] Cut773
  Base = -> Cut770
  Tool = -> Box1179
FEATURE [Part::Cut] Cut775
  Base = -> Cut773
  Tool = -> Compound1146
FEATURE [Part::Cylinder] Cylinder2328  label="Válec2328"
  Angle = 360
  AttacherType = Attacher::AttachEngine3D
  Height = 200
  Placement = pos=(30,0,81) rot=(0.186157,0.694747,0.694747;2.7735rad)
  Radius = 2.5
FEATURE [Part::Compound] Compound1138
  Links = -> [Cylinder2325,Cylinder2326,Cylinder2324,Cylinder2327,Cylinder2323,Cylinder2328]
  Placement = pos=(-8,-11,-2) rot=(0,0,1;0rad)
FEATURE [Part::Cut] Cut766
  Base = -> Cut763
  Tool = -> Compound1138
FEATURE [Part::Cut] Cut769
  Base = -> Cut766
  Tool = -> Compound1141
FEATURE [Part::Cut] Cut772
  Base = -> Cut769
  Tool = -> Box1178
FEATURE [Part::Cut] Cut776
  Base = -> Cut772
  Tool = -> Compound1145
FEATURE [Part::Cut] Cut777
  Base = -> Cut776
  Tool = -> Compound1148
FEATURE [Part::Cut] Cut780
  Base = -> Cut777
  Tool = -> mirror021
FEATURE [Part::Cut] Cut783
  Base = -> Cut780
  Tool = -> mirror022
FEATURE [Part::Cut] Cut786
  Base = -> Cut783
  Tool = -> mirror023
FEATURE [Part::Cut] Cut789
  Base = -> Cut786
  Tool = -> mirror024
FEATURE [Part::Cut] Cut792
  Base = -> Cut789
  Tool = -> mirror025
FEATURE [Part::Cut] Cut795
  Base = -> Cut792
  Tool = -> mirror026
FEATURE [Part::Fillet] Fillet011
  Base = -> Cut795
  Edges = 1 edges r=4: [Edge195]
FEATURE [Part::Fillet] Fillet012
  Base = -> Fillet011
  Edges = 1 edges r=2: [Edge17]
FEATURE [Part::Cut] Cut802
  Base = -> Fillet012
  Tool = -> Compound1165
FEATURE [Part::Cut] Cut803
  Base = -> Cut802
  Tool = -> Compound1170
FEATURE [Part::Cut] Cut804
  Base = -> Cut803
  Tool = -> Compound1175
FEATURE [Part::Cylinder] Cylinder2371  label="Válec2371"
  Angle = 360
  AttacherType = Attacher::AttachEngine3D
  Height = 200
  Placement = pos=(24,0,81) rot=(0.186157,0.694747,0.694747;2.7735rad)
  Radius = 2.5
FEATURE [Part::Box] Box1226  label="Krychle1226"
  AttacherType = Attacher::AttachEngine3D
  Height = 100
  Length = 1.5
  Placement = pos=(53.7894,33.3071,0) rot=(0,0,-1;0.698132rad)
  Width = 4
FEATURE [Part::Box] Box1229  label="Krychle1229"
  AttacherType = Attacher::AttachEngine3D
  Height = 20
  Length = 8
  Placement = pos=(22.79,59.31,80) rot=(0,0,-1;0.698132rad)
  Width = 6
FEATURE [Part::Cylinder] Cylinder2375  label="Válec2375"
  Angle = 360
  AttacherType = Attacher::AttachEngine3D
  Height = 200
  Placement = pos=(0,0,81) rot=(0.186157,0.694747,0.694747;2.77349rad)
  Radius = 2.5
FEATURE [Part::Box] Box1234  label="Krychle1234"
  AttacherType = Attacher::AttachEngine3D
  Height = 40
  Length = 34
  Placement = pos=(23.08,50.36,89.4) rot=(-0.819161,0.219493,-0.529904;0.936369rad)
  Width = 100
FEATURE [Part::Mirroring] mirror036  label="Krychle1213 (mirrored)002"
  Base = (0,0,0)
  Normal = (1,0,0)
  Source = -> Box1234
FEATURE [Part::Cylinder] Cylinder2383  label="Válec2383"
  Angle = 360
  AttacherType = Attacher::AttachEngine3D
  Height = 200
  Placement = pos=(24,0,81) rot=(0.186157,0.694747,0.694747;2.7735rad)
  Radius = 2.5
FEATURE [Part::Cylinder] Cylinder2370  label="Válec2370"
  Angle = 360
  AttacherType = Attacher::AttachEngine3D
  Height = 200
  Placement = pos=(24,0,81) rot=(0.186157,0.694747,0.694747;2.7735rad)
  Radius = 2.5
FEATURE [Part::Compound] Compound1156
  Links = -> [Cylinder2367,Cylinder2365,Cylinder2374,Cylinder2368,Cylinder2370,Cylinder2366]
  Placement = pos=(-8,-11,-2) rot=(0,0,1;0rad)
FEATURE [Part::Mirroring] mirror027  label="Compound1151 (mirrored)001"
  Base = (0,0,0)
  Normal = (1,0,0)
  Source = -> Compound1156
FEATURE [Part::Cylinder] Cylinder2386  label="Válec2386"
  Angle = 360
  AttacherType = Attacher::AttachEngine3D
  Height = 200
  Placement = pos=(12,0,81) rot=(0.186157,0.694747,0.694747;2.7735rad)
  Radius = 2.5
FEATURE [Part::Box] Box1228  label="Krychle1228"
  AttacherType = Attacher::AttachEngine3D
  Height = 20
  Length = 8
  Placement = pos=(7.64,33.65,80) rot=(0,0,-1;0.872665rad)
  Width = 6
FEATURE [Part::Cylinder] Cylinder2377  label="Válec2377"
  Angle = 360
  AttacherType = Attacher::AttachEngine3D
  Height = 200
  Placement = pos=(6,0,81) rot=(0.186157,0.694747,0.694747;2.7735rad)
  Radius = 2.5
FEATURE [Part::Box] Box1227  label="Krychle1227"
  AttacherType = Attacher::AttachEngine3D
  Height = 100
  Length = 1.5
  Placement = pos=(8.63532,33.646,7e-15) rot=(0,0,-1;0.872665rad)
  Width = 4
FEATURE [Part::Compound] Compound1158
  Links = -> [Box1223,Box1227,Box1225,Box1226]
FEATURE [Part::Mirroring] mirror028  label="Compound1152 (mirrored)001"
  Base = (0,0,0)
  Normal = (1,0,0)
  Source = -> Compound1158
FEATURE [Part::Box] Box1231  label="Krychle1231"
  AttacherType = Attacher::AttachEngine3D
  Height = 20
  Length = 8
  Placement = pos=(50.79,34,80) rot=(0,0,-1;0.698132rad)
  Width = 6
FEATURE [Part::Compound] Compound1157
  Links = -> [Box1229,Box1228,Box1231,Box1230]
FEATURE [Part::Mirroring] mirror032  label="Compound1153 (mirrored)001"
  Base = (0,0,0)
  Normal = (1,0,0)
  Source = -> Compound1157
FEATURE [Part::Cylinder] Cylinder2387  label="Válec2387"
  Angle = 360
  AttacherType = Attacher::AttachEngine3D
  Height = 200
  Placement = pos=(0,0,81) rot=(0.186157,0.694747,0.694747;2.77349rad)
  Radius = 2.5
FEATURE [Part::Box] Box1259  label="Krychle1259"
  AttacherType = Attacher::AttachEngine3D
  Height = 20
  Length = 8
  Placement = pos=(7.64,33.65,80) rot=(0,0,-1;0.872665rad)
  Width = 6
FEATURE [Part::Cylinder] Cylinder2384  label="Válec2384"
  Angle = 360
  AttacherType = Attacher::AttachEngine3D
  Height = 200
  Placement = pos=(12,0,81) rot=(0.186157,0.694747,0.694747;2.7735rad)
  Radius = 2.5
FEATURE [Part::Cylinder] Cylinder2376  label="Válec2376"
  Angle = 360
  AttacherType = Attacher::AttachEngine3D
  Height = 200
  Placement = pos=(6,0,81) rot=(0.186157,0.694747,0.694747;2.7735rad)
  Radius = 2.5
FEATURE [Part::Compound] Compound1155
  Links = -> [Cylinder2375,Cylinder2376,Cylinder2372,Cylinder2373,Cylinder2371,Cylinder2369]
  Placement = pos=(-6.01912,-7.56902,40.5645) rot=(-0.866025,0.5,0;0.785398rad)
FEATURE [Part::Mirroring] mirror031  label="Compound1154 (mirrored)001"
  Base = (0,0,0)
  Normal = (1,0,0)
  Source = -> Compound1155
FEATURE [Part::Cylinder] Cylinder2382  label="Válec2382"
  Angle = 360
  AttacherType = Attacher::AttachEngine3D
  Height = 200
  Placement = pos=(24,0,81) rot=(0.186157,0.694747,0.694747;2.7735rad)
  Radius = 2.5
FEATURE [Part::Cylinder] Cylinder2380  label="Válec2380"
  Angle = 360
  AttacherType = Attacher::AttachEngine3D
  Height = 200
  Placement = pos=(18,0,81) rot=(0.186157,0.694747,0.694747;2.7735rad)
  Radius = 2.5
FEATURE [Part::Box] Box1261  label="Krychle1261"
  AttacherType = Attacher::AttachEngine3D
  Height = 20
  Length = 8
  Placement = pos=(30,-0.35,80) rot=(0,0,-1;0.872665rad)
  Width = 6
FEATURE [Part::Box] Box1237  label="Krychle1237"
  AttacherType = Attacher::AttachEngine3D
  Height = 100
  Length = 1.5
  Placement = pos=(8.63532,33.646,7e-15) rot=(0,0,-1;0.872665rad)
  Width = 4
FEATURE [Part::Cylinder] Cylinder2388  label="Válec2388"
  Angle = 360
  AttacherType = Attacher::AttachEngine3D
  Height = 200
  Placement = pos=(6,0,81) rot=(0.186157,0.694747,0.694747;2.7735rad)
  Radius = 2.5
FEATURE [Part::Cylinder] Cylinder2381  label="Válec2381"
  Angle = 360
  AttacherType = Attacher::AttachEngine3D
  Height = 200
  Placement = pos=(30,0,81) rot=(0.186157,0.694747,0.694747;2.7735rad)
  Radius = 2.5
FEATURE [Part::Cylinder] Cylinder2385  label="Válec2385"
  Angle = 360
  AttacherType = Attacher::AttachEngine3D
  Height = 200
  Placement = pos=(18,0,81) rot=(0.186157,0.694747,0.694747;2.7735rad)
  Radius = 2.5
FEATURE [Part::Compound] Compound1159
  Links = -> [Cylinder2387,Cylinder2388,Cylinder2384,Cylinder2385,Cylinder2383,Cylinder2381]
  Placement = pos=(-6.01912,-7.56902,40.5645) rot=(-0.866025,0.5,0;0.785398rad)
FEATURE [Part::Mirroring] mirror037  label="Compound1154 (mirrored)002"
  Base = (0,0,0)
  Normal = (1,0,0)
  Source = -> Compound1159
FEATURE [Part::Box] Box1235  label="Krychle1235"
  AttacherType = Attacher::AttachEngine3D
  Height = 100
  Length = 1.5
  Placement = pos=(33.6353,-2.354,7e-15) rot=(0,0,-1;0.872665rad)
  Width = 4
FEATURE [Part::Cylinder] Cylinder2379  label="Válec2379"
  Angle = 360
  AttacherType = Attacher::AttachEngine3D
  Height = 200
  Placement = pos=(0,0,81) rot=(0.186157,0.694747,0.694747;2.77349rad)
  Radius = 2.5
FEATURE [Part::Compound] Compound1160
  Links = -> [Cylinder2379,Cylinder2377,Cylinder2386,Cylinder2380,Cylinder2382,Cylinder2378]
  Placement = pos=(-8,-11,-2) rot=(0,0,1;0rad)
FEATURE [Part::Mirroring] mirror033  label="Compound1151 (mirrored)002"
  Base = (0,0,0)
  Normal = (1,0,0)
  Source = -> Compound1160
FEATURE [Part::Box] Box1233  label="Krychle1233"
  AttacherType = Attacher::AttachEngine3D
  Height = 100
  Length = 1.5
  Placement = pos=(23.7894,59.3071,0) rot=(0,0,-1;0.698132rad)
  Width = 4
FEATURE [Part::Box] Box1266  label="Krychle1266"
  AttacherType = Attacher::AttachEngine3D
  Height = 20
  Length = 8
  Placement = pos=(22.79,59.31,80) rot=(0,0,-1;0.698132rad)
  Width = 6
FEATURE [Part::Box] Box1265  label="Krychle1265"
  AttacherType = Attacher::AttachEngine3D
  Height = 20
  Length = 8
  Placement = pos=(30,-0.35,80) rot=(0,0,-1;0.872665rad)
  Width = 6
FEATURE [Part::Box] Box1262  label="Krychle1262"
  AttacherType = Attacher::AttachEngine3D
  Height = 20
  Length = 8
  Placement = pos=(22.79,59.31,80) rot=(0,0,-1;0.698132rad)
  Width = 6
FEATURE [Part::Box] Box1267  label="Krychle1267"
  AttacherType = Attacher::AttachEngine3D
  Height = 20
  Length = 8
  Placement = pos=(7.64,33.65,80) rot=(0,0,-1;0.872665rad)
  Width = 6
FEATURE [Part::Box] Box1264  label="Krychle1264"
  AttacherType = Attacher::AttachEngine3D
  Height = 20
  Length = 8
  Placement = pos=(50.79,34,80) rot=(0,0,-1;0.698132rad)
  Width = 6
FEATURE [Part::Compound] Compound1150
  Links = -> [Box1262,Box1263,Box1264,Box1265]
FEATURE [Part::Cut] Cut779
  Base = -> Cut774
  Tool = -> Compound1150
FEATURE [Part::Cut] Cut782
  Base = -> Cut779
  Tool = -> mirror033
FEATURE [Part::Box] Box1258  label="Krychle1258"
  AttacherType = Attacher::AttachEngine3D
  Height = 20
  Length = 8
  Placement = pos=(22.79,59.31,80) rot=(0,0,-1;0.698132rad)
  Width = 6
FEATURE [Part::Box] Box1269  label="Krychle1269"
  AttacherType = Attacher::AttachEngine3D
  Height = 20
  Length = 8
  Placement = pos=(30,-0.35,80) rot=(0,0,-1;0.872665rad)
  Width = 6
FEATURE [Part::Compound] Compound1161
  Links = -> [Box1266,Box1267,Box1268,Box1269]
FEATURE [Part::Mirroring] mirror038  label="Compound1153 (mirrored)002"
  Base = (0,0,0)
  Normal = (1,0,0)
  Source = -> Compound1161
FEATURE [Part::Box] Box1236  label="Krychle1236"
  AttacherType = Attacher::AttachEngine3D
  Height = 100
  Length = 1.5
  Placement = pos=(53.7894,33.3071,0) rot=(0,0,-1;0.698132rad)
  Width = 4
FEATURE [Part::Compound] Compound1162
  Links = -> [Box1233,Box1237,Box1235,Box1236]
FEATURE [Part::Mirroring] mirror034  label="Compound1152 (mirrored)002"
  Base = (0,0,0)
  Normal = (1,0,0)
  Source = -> Compound1162
FEATURE [Part::Cut] Cut785
  Base = -> Cut782
  Tool = -> mirror034
FEATURE [Part::Cut] Cut788
  Base = -> Cut785
  Tool = -> mirror035
FEATURE [Part::Cut] Cut791
  Base = -> Cut788
  Tool = -> mirror036
FEATURE [Part::Cut] Cut794
  Base = -> Cut791
  Tool = -> mirror037
FEATURE [Part::Cut] Cut797
  Base = -> Cut794
  Tool = -> mirror038
FEATURE [Part::Cut] Cut799
  Base = -> Cut797
  Tool = -> Cut798
FEATURE [Part::Fillet] Fillet013
  Base = -> Cut799
  Edges = 1 edges r=4: [Edge90]
FEATURE [Part::Fillet] Fillet009
  Base = -> Fillet013
  Edges = 1 edges r=4: [Edge99]
FEATURE [Part::Fillet] Fillet010
  Base = -> Fillet009
  Edges = 1 edges r=2: [Edge17]
FEATURE [Part::Box] Box1260  label="Krychle1260"
  AttacherType = Attacher::AttachEngine3D
  Height = 20
  Length = 8
  Placement = pos=(50.79,34,80) rot=(0,0,-1;0.698132rad)
  Width = 6
FEATURE [Part::Compound] Compound1149
  Links = -> [Box1258,Box1259,Box1260,Box1261]
FEATURE [Part::Cut] Cut778
  Base = -> Cut775
  Tool = -> Compound1149
FEATURE [Part::Cut] Cut781
  Base = -> Cut778
  Tool = -> mirror027
FEATURE [Part::Cut] Cut784
  Base = -> Cut781
  Tool = -> mirror028
FEATURE [Part::Cut] Cut787
  Base = -> Cut784
  Tool = -> mirror029
FEATURE [Part::Cut] Cut790
  Base = -> Cut787
  Tool = -> mirror030
FEATURE [Part::Cut] Cut793
  Base = -> Cut790
  Tool = -> mirror031
FEATURE [Part::Cut] Cut796
  Base = -> Cut793
  Tool = -> mirror032
FEATURE [Part::Cut] Cut805
  Base = -> Cut796
  Tool = -> Compound1183
FEATURE [Part::Cut] Cut800
  Base = -> Cut805
  Tool = -> Compound1189
FEATURE [Part::Cut] Cut801
  Base = -> Cut800
  Tool = -> Compound1195
FEATURE [Part::Compound] Compound1193  label="Base_bare-turret-holed"
  Links = -> [Fillet010,Tube055,Cut801,Cut804]
FEATURE [Mesh::Feature] Mesh005  label="Base_bare-turret-holed (Meshed)"
FEATURE [Part::Cylinder] Cylinder2417  label="Válec2417"
  Angle = 360
  AttacherType = Attacher::AttachEngine3D
  Height = 60
  Placement = pos=(-35.5,-61.4878,0) rot=(0,0,-1;0.523599rad)
  Radius = 1.5
FEATURE [Part::Compound] Compound1116
  Links = -> [Cylinder2122,Cylinder2124,Cylinder2128,Cylinder2117,Cylinder2118,Cylinder2126,Cylinder2123,Cylinder2121,Cylinder2112,Cylinder2113,Cylinder2114,Cylinder2417]
FEATURE [Part::Cut] Cut707
  Base = -> Chamfer084
  Tool = -> Compound1116
FEATURE [Part::Cylinder] Cylinder2418  label="Válec2418"
  Angle = 360
  AttacherType = Attacher::AttachEngine3D
  Height = 3
  Placement = pos=(-35.5,-61.4878,0) rot=(0,0,-1;0.523599rad)
  Radius = 3
FEATURE [Part::Compound] Compound1117
  Links = -> [Cylinder2138,Cylinder2115,Cylinder2129,Cylinder2127,Cylinder2120,Cylinder2119,Cylinder2130,Cylinder2139,Cylinder2111,Cylinder2125,Cylinder2116,Cylinder2418]
  Placement = pos=(0,0,17) rot=(0,0,1;0rad)
FEATURE [Part::Cut] Cut706  label="Base_big-ring-seal-wavy"
  Base = -> Cut707
  Placement = pos=(0,0,17) rot=(0.991445,0.130526,0;3.14159rad)
  Tool = -> Compound1117
FEATURE [Mesh::Feature] Mesh  label="Base_big-ring-seal-wavy (Meshed)"
